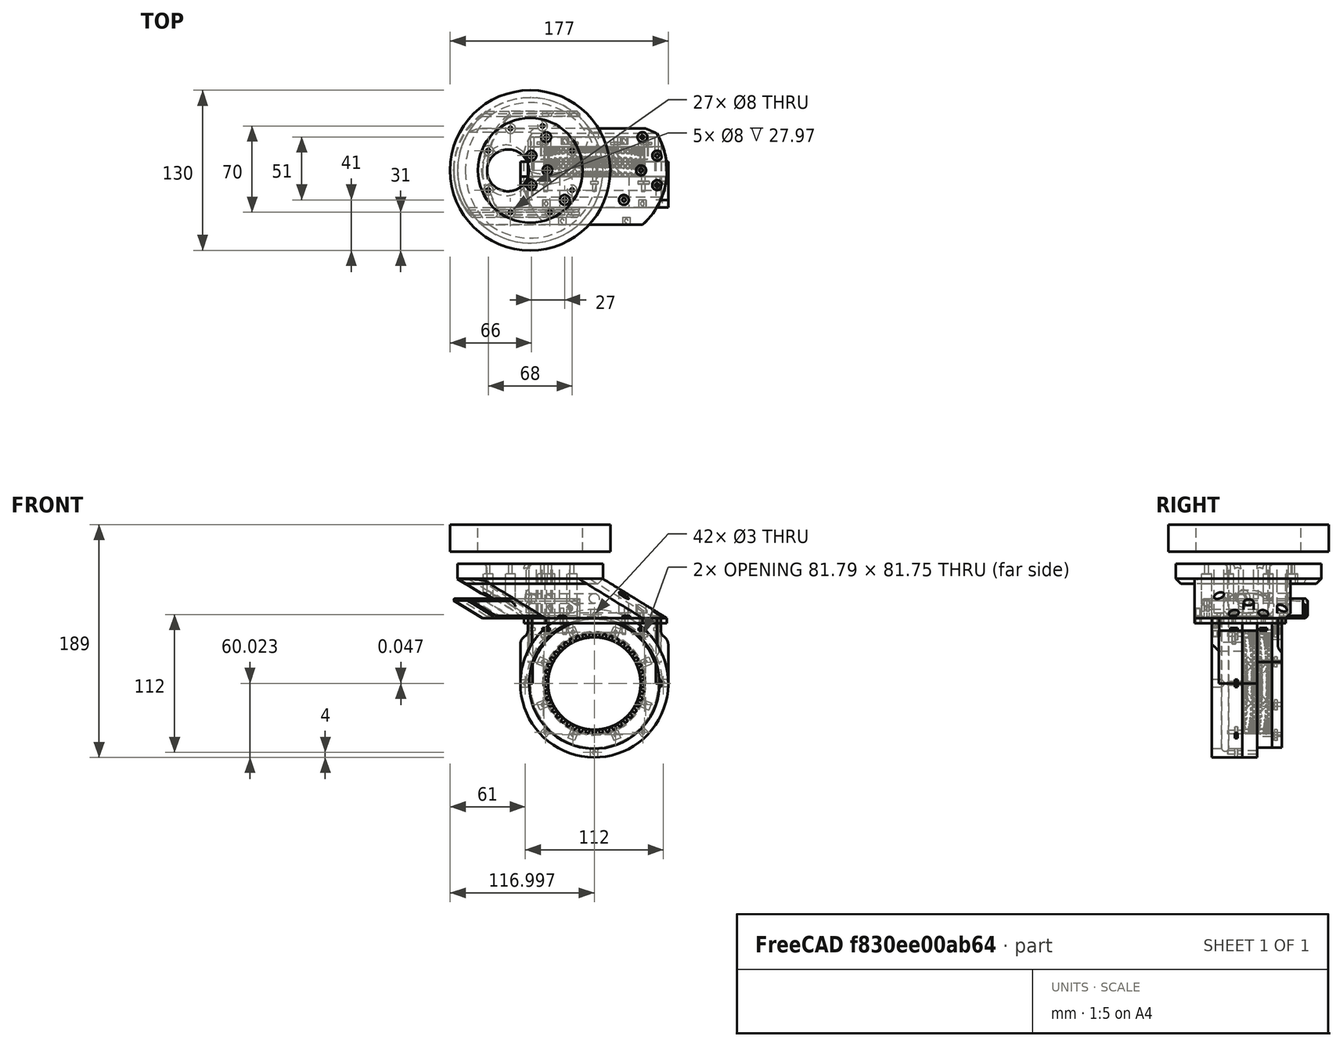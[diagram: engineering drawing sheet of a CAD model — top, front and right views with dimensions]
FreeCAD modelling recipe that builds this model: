
FCSTD DOCUMENT  (FreeCAD 0.19R24276 (Git))
Label: Base_neck_034
License: All rights reserved
LicenseURL: http://en.wikipedia.org/wiki/All_rights_reserved
objects: Part::Cylinder×1148, Part::Cut×314, Part::Compound×235, Part::Box×126, Part::Chamfer×46, Part::Fillet×33, Sketcher::SketchObject×20, Part::Extrusion×20, Part::Common×10, Part::FeaturePython×6, Part::Torus×3, Part::Mirroring×2, Mesh::Feature×1
note: 1963 computed .brp shape members not serialized (recipe doc carries the construction recipe); baked Part::Feature solids carry a one-line shape summary decoded from their .brp

FEATURE [Sketcher::SketchObject] Sketch003
  FullyConstrained = false
  sketch-geometry (1):
    g0: Circle CenterX=-186.411 CenterY=73.9277 CenterZ=0 NormalX=0 NormalY=0 NormalZ=1 AngleXU=0 Radius=59
FEATURE [Part::Extrusion] Extrude001
  Base = -> Sketch003
  Dir = (52,0,32)
  DirMode = 0
  FaceMakerClass = Part::FaceMakerBullseye
  LengthFwd = 61
  LengthRev = 0
  Placement = pos=(-134,74,-22) rot=(0,0,1;3.14159rad)
  Solid = true
  Symmetric = false
FEATURE [Part::Cylinder] Cylinder1076  label="Válec1076"
  Angle = 360
  AttacherType = Attacher::AttachEngine3D
  Height = 100
  Placement = pos=(103,-12,-60) rot=(0,0,1;0rad)
  Radius = 1.5
FEATURE [Part::Cylinder] Cylinder1077  label="Válec1077"
  Angle = 360
  AttacherType = Attacher::AttachEngine3D
  Height = 100
  Placement = pos=(103,6,-60) rot=(0,0,1;0rad)
  Radius = 1.5
FEATURE [Part::Cylinder] Cylinder1078  label="Válec1078"
  Angle = 360
  AttacherType = Attacher::AttachEngine3D
  Height = 100
  Placement = pos=(76,18,-60) rot=(0,0,1;0rad)
  Radius = 1.5
FEATURE [Part::Cylinder] Cylinder1079  label="Válec1079"
  Angle = 360
  AttacherType = Attacher::AttachEngine3D
  Height = 100
  Placement = pos=(91,-21,-60) rot=(0,0,1;0rad)
  Radius = 1.5
FEATURE [Part::Cylinder] Cylinder1080  label="Válec1080"
  Angle = 360
  AttacherType = Attacher::AttachEngine3D
  Height = 100
  Placement = pos=(13,-21,-60) rot=(0,0,1;0rad)
  Radius = 1.5
FEATURE [Part::Cylinder] Cylinder1081  label="Válec1081"
  Angle = 360
  AttacherType = Attacher::AttachEngine3D
  Height = 100
  Placement = pos=(28,18,-60) rot=(0,0,1;0rad)
  Radius = 1.5
FEATURE [Part::Cylinder] Cylinder1083  label="Válec1083"
  Angle = 360
  AttacherType = Attacher::AttachEngine3D
  Height = 100
  Placement = pos=(1,-12,-60) rot=(0,0,1;0rad)
  Radius = 1.5
FEATURE [Part::Cylinder] Cylinder1084  label="Válec1084"
  Angle = 360
  AttacherType = Attacher::AttachEngine3D
  Height = 100
  Placement = pos=(1,6,-60) rot=(0,0,1;0rad)
  Radius = 1.5
FEATURE [Part::Compound] Compound559  label="srouby_monoblok"
  Links = -> [Cylinder1076,Cylinder1077,Cylinder1078,Cylinder1079,Cylinder1080,Cylinder1081,Cylinder1083,Cylinder1084]
FEATURE [Part::Cut] Cut247
  Base = -> Extrude001
  Tool = -> Compound559
FEATURE [Part::Cylinder] Cylinder1085  label="Válec1085"
  Angle = 360
  AttacherType = Attacher::AttachEngine3D
  Height = 100
  Placement = pos=(-50,0,-60) rot=(0,0,1;0rad)
  Radius = 1.5
FEATURE [Part::Cylinder] Cylinder1086  label="Válec1086"
  Angle = 360
  AttacherType = Attacher::AttachEngine3D
  Height = 100
  Placement = pos=(-36,34,-60) rot=(0,0,1;0rad)
  Radius = 1.5
FEATURE [Part::Cylinder] Cylinder1087  label="Válec1087"
  Angle = 360
  AttacherType = Attacher::AttachEngine3D
  Height = 100
  Placement = pos=(-36,-34,-60) rot=(0,0,1;0rad)
  Radius = 1.5
FEATURE [Part::Cylinder] Cylinder1088  label="Válec1088"
  Angle = 360
  AttacherType = Attacher::AttachEngine3D
  Height = 100
  Placement = pos=(50,0,-60) rot=(0,0,1;0rad)
  Radius = 1.5
FEATURE [Part::Cylinder] Cylinder1089  label="Válec1089"
  Angle = 360
  AttacherType = Attacher::AttachEngine3D
  Height = 100
  Placement = pos=(36,34,-60) rot=(0,0,1;0rad)
  Radius = 1.5
FEATURE [Part::Cylinder] Cylinder1090  label="Válec1090"
  Angle = 360
  AttacherType = Attacher::AttachEngine3D
  Height = 100
  Placement = pos=(36,-34,-60) rot=(0,0,1;0rad)
  Radius = 1.5
FEATURE [Part::Compound] Compound560  label="sbouby_baze"
  Links = -> [Cylinder1085,Cylinder1086,Cylinder1087,Cylinder1088,Cylinder1089,Cylinder1090]
FEATURE [Part::Cylinder] Cylinder1091  label="Válec1091"
  Angle = 360
  AttacherType = Attacher::AttachEngine3D
  Height = 16
  Placement = pos=(0,0,2) rot=(0,0,1;0rad)
  Radius = 59
FEATURE [Part::Cylinder] Cylinder1092  label="Válec1092"
  Angle = 360
  AttacherType = Attacher::AttachEngine3D
  Height = 4
  Placement = pos=(52,0,-26) rot=(0,0,1;0rad)
  Radius = 59
FEATURE [Part::Cylinder] Cylinder1101  label="Válec1101"
  Angle = 360
  AttacherType = Attacher::AttachEngine3D
  Height = 100
  Placement = pos=(103,-12,-60) rot=(0,0,1;0rad)
  Radius = 1.5
FEATURE [Part::Cylinder] Cylinder1102  label="Válec1102"
  Angle = 360
  AttacherType = Attacher::AttachEngine3D
  Height = 100
  Placement = pos=(103,6,-60) rot=(0,0,1;0rad)
  Radius = 1.5
FEATURE [Part::Cylinder] Cylinder1103  label="Válec1103"
  Angle = 360
  AttacherType = Attacher::AttachEngine3D
  Height = 100
  Placement = pos=(76,18,-60) rot=(0,0,1;0rad)
  Radius = 1.5
FEATURE [Part::Cylinder] Cylinder1104  label="Válec1104"
  Angle = 360
  AttacherType = Attacher::AttachEngine3D
  Height = 100
  Placement = pos=(91,-21,-60) rot=(0,0,1;0rad)
  Radius = 1.5
FEATURE [Part::Cylinder] Cylinder1105  label="Válec1105"
  Angle = 360
  AttacherType = Attacher::AttachEngine3D
  Height = 100
  Placement = pos=(13,-21,-60) rot=(0,0,1;0rad)
  Radius = 1.5
FEATURE [Part::Cylinder] Cylinder1106  label="Válec1106"
  Angle = 360
  AttacherType = Attacher::AttachEngine3D
  Height = 100
  Placement = pos=(28,18,-60) rot=(0,0,1;0rad)
  Radius = 1.5
FEATURE [Part::Cylinder] Cylinder1107  label="Válec1107"
  Angle = 360
  AttacherType = Attacher::AttachEngine3D
  Height = 100
  Placement = pos=(1,-12,-60) rot=(0,0,1;0rad)
  Radius = 1.5
FEATURE [Part::Cylinder] Cylinder1108  label="Válec1108"
  Angle = 360
  AttacherType = Attacher::AttachEngine3D
  Height = 100
  Placement = pos=(1,6,-60) rot=(0,0,1;0rad)
  Radius = 1.5
FEATURE [Part::Compound] Compound562  label="srouby_monoblok001"
  Links = -> [Cylinder1101,Cylinder1102,Cylinder1103,Cylinder1104,Cylinder1105,Cylinder1106,Cylinder1107,Cylinder1108]
FEATURE [Part::Cut] Cut250
  Base = -> Cylinder1092
  Tool = -> Compound562
FEATURE [Part::Cylinder] Cylinder1109  label="Válec1109"
  Angle = 360
  AttacherType = Attacher::AttachEngine3D
  Height = 20
  Placement = pos=(103,-12,-20) rot=(0,0,1;0rad)
  Radius = 4
FEATURE [Part::Cylinder] Cylinder1110  label="Válec1110"
  Angle = 360
  AttacherType = Attacher::AttachEngine3D
  Height = 20
  Placement = pos=(103,6,-20) rot=(0,0,1;0rad)
  Radius = 4
FEATURE [Part::Cylinder] Cylinder1111  label="Válec1111"
  Angle = 360
  AttacherType = Attacher::AttachEngine3D
  Height = 20
  Placement = pos=(76,18,-18) rot=(0,0,1;0rad)
  Radius = 4
FEATURE [Part::Cylinder] Cylinder1112  label="Válec1112"
  Angle = 360
  AttacherType = Attacher::AttachEngine3D
  Height = 20
  Placement = pos=(91,-21,-18) rot=(0,0,1;0rad)
  Radius = 4
FEATURE [Part::Cylinder] Cylinder1113  label="Válec1113"
  Angle = 360
  AttacherType = Attacher::AttachEngine3D
  Height = 40
  Placement = pos=(13,-21,-18) rot=(0,0,1;0rad)
  Radius = 4
FEATURE [Part::Cylinder] Cylinder1114  label="Válec1114"
  Angle = 360
  AttacherType = Attacher::AttachEngine3D
  Height = 40
  Placement = pos=(28,18,-18) rot=(0,0,1;0rad)
  Radius = 4
FEATURE [Part::Cylinder] Cylinder1115  label="Válec1115"
  Angle = 360
  AttacherType = Attacher::AttachEngine3D
  Height = 40
  Placement = pos=(1,-12,-18) rot=(0,0,1;0rad)
  Radius = 4
FEATURE [Part::Cylinder] Cylinder1116  label="Válec1116"
  Angle = 360
  AttacherType = Attacher::AttachEngine3D
  Height = 40
  Placement = pos=(1,6,-18) rot=(0,0,1;0rad)
  Radius = 4
FEATURE [Part::Compound] Compound563  label="srouby_monoblok_silne001"
  Links = -> [Cylinder1109,Cylinder1110,Cylinder1111,Cylinder1112,Cylinder1113,Cylinder1114,Cylinder1115,Cylinder1116]
FEATURE [Part::Cut] Cut248
  Base = -> Cut247
  Tool = -> Compound563
FEATURE [Part::Cylinder] Cylinder1117  label="Válec1117"
  Angle = 360
  AttacherType = Attacher::AttachEngine3D
  Height = 20
  Placement = pos=(103,-12,-20) rot=(0,0,1;0rad)
  Radius = 4
FEATURE [Part::Cylinder] Cylinder1118  label="Válec1118"
  Angle = 360
  AttacherType = Attacher::AttachEngine3D
  Height = 20
  Placement = pos=(103,6,-20) rot=(0,0,1;0rad)
  Radius = 4
FEATURE [Part::Cylinder] Cylinder1119  label="Válec1119"
  Angle = 360
  AttacherType = Attacher::AttachEngine3D
  Height = 20
  Placement = pos=(76,18,-18) rot=(0,0,1;0rad)
  Radius = 4
FEATURE [Part::Cylinder] Cylinder1120  label="Válec1120"
  Angle = 360
  AttacherType = Attacher::AttachEngine3D
  Height = 20
  Placement = pos=(91,-21,-18) rot=(0,0,1;0rad)
  Radius = 4
FEATURE [Part::Cylinder] Cylinder1121  label="Válec1121"
  Angle = 360
  AttacherType = Attacher::AttachEngine3D
  Height = 40
  Placement = pos=(13,-21,-18) rot=(0,0,1;0rad)
  Radius = 4
FEATURE [Part::Cylinder] Cylinder1122  label="Válec1122"
  Angle = 360
  AttacherType = Attacher::AttachEngine3D
  Height = 40
  Placement = pos=(28,18,-18) rot=(0,0,1;0rad)
  Radius = 4
FEATURE [Part::Cylinder] Cylinder1123  label="Válec1123"
  Angle = 360
  AttacherType = Attacher::AttachEngine3D
  Height = 40
  Placement = pos=(1,-12,-18) rot=(0,0,1;0rad)
  Radius = 4
FEATURE [Part::Cylinder] Cylinder1124  label="Válec1124"
  Angle = 360
  AttacherType = Attacher::AttachEngine3D
  Height = 40
  Placement = pos=(1,6,-18) rot=(0,0,1;0rad)
  Radius = 4
FEATURE [Part::Compound] Compound564  label="srouby_monoblok_silne002"
  Links = -> [Cylinder1117,Cylinder1118,Cylinder1119,Cylinder1120,Cylinder1121,Cylinder1122,Cylinder1123,Cylinder1124]
FEATURE [Part::Cut] Cut249
  Base = -> Cylinder1091
  Tool = -> Compound564
FEATURE [Part::Cylinder] Cylinder1137  label="Válec1137"
  Angle = 360
  AttacherType = Attacher::AttachEngine3D
  Height = 100
  Placement = pos=(16,34,-90) rot=(0,0,1;0rad)
  Radius = 4
FEATURE [Part::Cylinder] Cylinder1138  label="Válec1138"
  Angle = 360
  AttacherType = Attacher::AttachEngine3D
  Height = 100
  Placement = pos=(-34,-16,-90) rot=(0,0,1;0rad)
  Radius = 4
FEATURE [Part::Cylinder] Cylinder1139  label="Válec1139"
  Angle = 360
  AttacherType = Attacher::AttachEngine3D
  Height = 100
  Placement = pos=(-16,34,-90) rot=(0,0,1;0rad)
  Radius = 4
FEATURE [Part::Cylinder] Cylinder1140  label="Válec1140"
  Angle = 360
  AttacherType = Attacher::AttachEngine3D
  Height = 100
  Placement = pos=(-16,-34,-90) rot=(0,0,1;0rad)
  Radius = 4
FEATURE [Part::Cylinder] Cylinder1141  label="Válec1141"
  Angle = 360
  AttacherType = Attacher::AttachEngine3D
  Height = 100
  Placement = pos=(36,0,-90) rot=(0,0,1;0rad)
  Radius = 4
FEATURE [Part::Cylinder] Cylinder1142  label="Válec1142"
  Angle = 360
  AttacherType = Attacher::AttachEngine3D
  Height = 100
  Placement = pos=(16,-34,-90) rot=(0,0,1;0rad)
  Radius = 4
FEATURE [Part::Compound] Compound567  label="sbouby_baze_silne002"
  Links = -> [Cylinder1138,Cylinder1139,Cylinder1140,Cylinder1141,Cylinder1137,Cylinder1142]
FEATURE [Part::Cut] Cut252
  Base = -> Cut248
  Tool = -> Compound567
FEATURE [Part::Cylinder] Cylinder1143  label="Válec1143"
  Angle = 360
  AttacherType = Attacher::AttachEngine3D
  Height = 100
  Placement = pos=(36,34,-60) rot=(0,0,1;0rad)
  Radius = 1.5
FEATURE [Part::Cylinder] Cylinder1144  label="Válec1144"
  Angle = 360
  AttacherType = Attacher::AttachEngine3D
  Height = 100
  Placement = pos=(-50,0,-60) rot=(0,0,1;0rad)
  Radius = 1.5
FEATURE [Part::Cylinder] Cylinder1145  label="Válec1145"
  Angle = 360
  AttacherType = Attacher::AttachEngine3D
  Height = 100
  Placement = pos=(-36,34,-60) rot=(0,0,1;0rad)
  Radius = 1.5
FEATURE [Part::Cylinder] Cylinder1146  label="Válec1146"
  Angle = 360
  AttacherType = Attacher::AttachEngine3D
  Height = 100
  Placement = pos=(-36,-34,-60) rot=(0,0,1;0rad)
  Radius = 1.5
FEATURE [Part::Cylinder] Cylinder1147  label="Válec1147"
  Angle = 360
  AttacherType = Attacher::AttachEngine3D
  Height = 100
  Placement = pos=(50,0,-60) rot=(0,0,1;0rad)
  Radius = 1.5
FEATURE [Part::Cylinder] Cylinder1148  label="Válec1148"
  Angle = 360
  AttacherType = Attacher::AttachEngine3D
  Height = 100
  Placement = pos=(36,-34,-60) rot=(0,0,1;0rad)
  Radius = 1.5
FEATURE [Part::Compound] Compound568  label="sbouby_baze001"
  Links = -> [Cylinder1144,Cylinder1145,Cylinder1146,Cylinder1147,Cylinder1143,Cylinder1148]
FEATURE [Part::Cut] Cut254
  Base = -> Cut252
  Tool = -> Compound568
FEATURE [Part::Box] Box214  label="Krychle214"
  AttacherType = Attacher::AttachEngine3D
  Height = 100
  Length = 200
  Placement = pos=(-60,-130,-90) rot=(0,0,1;0rad)
  Width = 100
FEATURE [Part::Cut] Cut256
  Base = -> Cut254
  Tool = -> Box214
FEATURE [Part::Box] Box233  label="Krychle233"
  AttacherType = Attacher::AttachEngine3D
  Height = 100
  Length = 200
  Placement = pos=(-60,-124,-90) rot=(0,0,1;0rad)
  Width = 100
FEATURE [Part::Box] Box234  label="Krychle234"
  AttacherType = Attacher::AttachEngine3D
  Height = 100
  Length = 200
  Placement = pos=(-60,44,-90) rot=(0,0,1;0rad)
  Width = 100
FEATURE [Part::Cut] Cut286
  Base = -> Cut256
  Tool = -> Box234
FEATURE [Part::Box] Box235  label="Krychle235"
  AttacherType = Attacher::AttachEngine3D
  Height = 100
  Length = 200
  Placement = pos=(-60,44,-90) rot=(0,0,1;0rad)
  Width = 100
FEATURE [Part::Cylinder] Cylinder1228  label="Válec1228"
  Angle = 360
  AttacherType = Attacher::AttachEngine3D
  Height = 100
  Placement = pos=(90,0,-60) rot=(0,0,1;0rad)
  Radius = 1.5
FEATURE [Part::Cylinder] Cylinder1229  label="Válec1229"
  Angle = 360
  AttacherType = Attacher::AttachEngine3D
  Height = 100
  Placement = pos=(14,0,-60) rot=(0,0,1;0rad)
  Radius = 1.5
FEATURE [Part::Compound] Compound623  label="srouby_troj"
  Links = -> [Cylinder1228,Cylinder1229]
FEATURE [Part::Cylinder] Cylinder1230  label="Válec1230"
  Angle = 360
  AttacherType = Attacher::AttachEngine3D
  Height = 100
  Placement = pos=(90,0,-18) rot=(0,0,1;0rad)
  Radius = 4
FEATURE [Part::Box] Box238  label="Krychle238"
  AttacherType = Attacher::AttachEngine3D
  Height = 2
  Length = 6
  Placement = pos=(75,38,-22) rot=(0,0,1;0rad)
  Width = 6
FEATURE [Part::Box] Box239  label="Krychle239"
  AttacherType = Attacher::AttachEngine3D
  Height = 2
  Length = 6
  Placement = pos=(23,38,-22) rot=(0,0,1;0rad)
  Width = 6
FEATURE [Part::Compound] Compound619
  Links = -> [Box238,Box239]
FEATURE [Part::Cut] Cut289
  Base = -> Cut286
  Tool = -> Compound619
FEATURE [Part::Cylinder] Cylinder1232  label="Válec1232"
  Angle = 360
  AttacherType = Attacher::AttachEngine3D
  Height = 32
  Placement = pos=(26,41,-42) rot=(0,0,1;0rad)
  Radius = 1.5
FEATURE [Part::Cylinder] Cylinder1233  label="Válec1233"
  Angle = 360
  AttacherType = Attacher::AttachEngine3D
  Height = 32
  Placement = pos=(78,41,-42) rot=(0,0,1;0rad)
  Radius = 1.5
FEATURE [Part::Compound] Compound620
  Links = -> [Cylinder1232,Cylinder1233]
FEATURE [Part::Cylinder] Cylinder1234  label="Válec1234"
  Angle = 360
  AttacherType = Attacher::AttachEngine3D
  Height = 32
  Placement = pos=(26,41,-46) rot=(0,0,1;0rad)
  Radius = 1.5
FEATURE [Part::Cylinder] Cylinder1235  label="Válec1235"
  Angle = 360
  AttacherType = Attacher::AttachEngine3D
  Height = 32
  Placement = pos=(78,41,-46) rot=(0,0,1;0rad)
  Radius = 1.5
FEATURE [Part::Compound] Compound621
  Links = -> [Cylinder1234,Cylinder1235]
FEATURE [Part::Cut] Cut290
  Base = -> Cut289
  Tool = -> Compound621
FEATURE [Part::Cut] Cut292
  Base = -> Cut290
  Tool = -> Compound623
FEATURE [Part::Cylinder] Cylinder1236  label="Válec1236"
  Angle = 360
  AttacherType = Attacher::AttachEngine3D
  Height = 100
  Placement = pos=(90,0,-18) rot=(0,0,1;0rad)
  Radius = 4
FEATURE [Part::Cylinder] Cylinder1237  label="Válec1237"
  Angle = 360
  AttacherType = Attacher::AttachEngine3D
  Height = 100
  Placement = pos=(14,0,-18) rot=(0,0,1;0rad)
  Radius = 4
FEATURE [Part::Compound] Compound624  label="srouby_troj_silne001"
  Links = -> [Cylinder1236,Cylinder1237]
FEATURE [Part::Cylinder] Cylinder1238  label="Válec1238"
  Angle = 360
  AttacherType = Attacher::AttachEngine3D
  Height = 100
  Placement = pos=(90,0,-60) rot=(0,0,1;0rad)
  Radius = 1.5
FEATURE [Part::Cylinder] Cylinder1239  label="Válec1239"
  Angle = 360
  AttacherType = Attacher::AttachEngine3D
  Height = 100
  Placement = pos=(14,0,-60) rot=(0,0,1;0rad)
  Radius = 1.5
FEATURE [Part::Compound] Compound625  label="srouby_troj001"
  Links = -> [Cylinder1238,Cylinder1239]
FEATURE [Part::FeaturePython] Tube044  label="ZKL-6017"  # WARN: FeaturePython — macro-defined, semantics opaque (R4)
  AttacherType = Attacher::AttachEngine3D
  Height = 22
  InnerRadius = 42.5
  OuterRadius = 65
  Placement = pos=(0,0,32) rot=(0,0,1;0rad)
FEATURE [Sketcher::SketchObject] Sketch004
  FullyConstrained = false
  sketch-geometry (1):
    g0: Circle CenterX=-186.411 CenterY=73.9277 CenterZ=0 NormalX=0 NormalY=0 NormalZ=1 AngleXU=0 Radius=59
FEATURE [Part::Extrusion] Extrude002
  Base = -> Sketch004
  Dir = (52,0,32)
  DirMode = 0
  FaceMakerClass = Part::FaceMakerBullseye
  LengthFwd = 61
  LengthRev = 0
  Placement = pos=(-134,74,-22) rot=(0,0,1;3.14159rad)
  Solid = true
  Symmetric = false
FEATURE [Part::Cylinder] Cylinder1256  label="Válec1256"
  Angle = 360
  AttacherType = Attacher::AttachEngine3D
  Height = 100
  Placement = pos=(16,34,-90) rot=(0,0,1;0rad)
  Radius = 4
FEATURE [Part::Cylinder] Cylinder1257  label="Válec1257"
  Angle = 360
  AttacherType = Attacher::AttachEngine3D
  Height = 100
  Placement = pos=(-34,-16,-90) rot=(0,0,1;0rad)
  Radius = 4
FEATURE [Part::Cylinder] Cylinder1258  label="Válec1258"
  Angle = 360
  AttacherType = Attacher::AttachEngine3D
  Height = 100
  Placement = pos=(-16,34,-90) rot=(0,0,1;0rad)
  Radius = 4
FEATURE [Part::Cylinder] Cylinder1259  label="Válec1259"
  Angle = 360
  AttacherType = Attacher::AttachEngine3D
  Height = 100
  Placement = pos=(-16,-34,-90) rot=(0,0,1;0rad)
  Radius = 4
FEATURE [Part::Cylinder] Cylinder1260  label="Válec1260"
  Angle = 360
  AttacherType = Attacher::AttachEngine3D
  Height = 100
  Placement = pos=(34,-16,-90) rot=(0,0,1;0rad)
  Radius = 4
FEATURE [Part::Cylinder] Cylinder1261  label="Válec1261"
  Angle = 360
  AttacherType = Attacher::AttachEngine3D
  Height = 100
  Placement = pos=(10,-36,-90) rot=(0,0,1;0rad)
  Radius = 4
FEATURE [Part::Cylinder] Cylinder1262  label="Válec1262"
  Angle = 360
  AttacherType = Attacher::AttachEngine3D
  Height = 100
  Placement = pos=(16,34,-60) rot=(0,0,1;0rad)
  Radius = 1.5
FEATURE [Part::Cylinder] Cylinder1263  label="Válec1263"
  Angle = 360
  AttacherType = Attacher::AttachEngine3D
  Height = 100
  Placement = pos=(-34,16,-60) rot=(0,0,1;0rad)
  Radius = 1.5
FEATURE [Part::Cylinder] Cylinder1264  label="Válec1264"
  Angle = 360
  AttacherType = Attacher::AttachEngine3D
  Height = 100
  Placement = pos=(-34,-16,-60) rot=(0,0,1;0rad)
  Radius = 1.5
FEATURE [Part::Cylinder] Cylinder1265  label="Válec1265"
  Angle = 360
  AttacherType = Attacher::AttachEngine3D
  Height = 100
  Placement = pos=(34,-16,-60) rot=(0,0,1;0rad)
  Radius = 1.5
FEATURE [Part::Cylinder] Cylinder1266  label="Válec1266"
  Angle = 360
  AttacherType = Attacher::AttachEngine3D
  Height = 100
  Placement = pos=(34,16,-60) rot=(0,0,1;0rad)
  Radius = 1.5
FEATURE [Part::Cylinder] Cylinder1267  label="Válec1267"
  Angle = 360
  AttacherType = Attacher::AttachEngine3D
  Height = 100
  Placement = pos=(10,-36,-60) rot=(0,0,1;0rad)
  Radius = 1.5
FEATURE [Part::Box] Box240  label="Krychle240"
  AttacherType = Attacher::AttachEngine3D
  Height = 100
  Length = 200
  Placement = pos=(-60,-134,-90) rot=(0,0,1;0rad)
  Width = 100
FEATURE [Part::Box] Box241  label="Krychle241"
  AttacherType = Attacher::AttachEngine3D
  Height = 100
  Length = 200
  Placement = pos=(-60,44,-90) rot=(0,0,1;0rad)
  Width = 100
FEATURE [Part::Cylinder] Cylinder1268  label="Válec1268"
  Angle = 360
  AttacherType = Attacher::AttachEngine3D
  Height = 100
  Placement = pos=(90,0,-60) rot=(0,0,1;0rad)
  Radius = 1.5
FEATURE [Part::Cylinder] Cylinder1269  label="Válec1269"
  Angle = 360
  AttacherType = Attacher::AttachEngine3D
  Height = 100
  Placement = pos=(14,0,-60) rot=(0,0,1;0rad)
  Radius = 1.5
FEATURE [Part::Cylinder] Cylinder1270  label="Válec1270"
  Angle = 360
  AttacherType = Attacher::AttachEngine3D
  Height = 100
  Placement = pos=(90,0,-18) rot=(0,0,1;0rad)
  Radius = 4
FEATURE [Part::Compound] Compound670  label="srouby_troj002"
  Links = -> [Cylinder1268,Cylinder1269]
FEATURE [Part::Cylinder] Cylinder1271  label="Válec1271"
  Angle = 360
  AttacherType = Attacher::AttachEngine3D
  Height = 100
  Placement = pos=(14,0,-18) rot=(0,0,1;0rad)
  Radius = 4
FEATURE [Part::Compound] Compound669  label="srouby_troj_silne002"
  Links = -> [Cylinder1270,Cylinder1271]
FEATURE [Part::Box] Box242  label="Krychle242"
  AttacherType = Attacher::AttachEngine3D
  Height = 2
  Length = 6
  Placement = pos=(75,38,-22) rot=(0,0,1;0rad)
  Width = 6
FEATURE [Part::Box] Box243  label="Krychle243"
  AttacherType = Attacher::AttachEngine3D
  Height = 2
  Length = 6
  Placement = pos=(23,38,-22) rot=(0,0,1;0rad)
  Width = 6
FEATURE [Part::Compound] Compound667
  Links = -> [Box242,Box243]
FEATURE [Part::Cylinder] Cylinder1272  label="Válec1272"
  Angle = 360
  AttacherType = Attacher::AttachEngine3D
  Height = 32
  Placement = pos=(26,41,-46) rot=(0,0,1;0rad)
  Radius = 1.5
FEATURE [Part::Cylinder] Cylinder1273  label="Válec1273"
  Angle = 360
  AttacherType = Attacher::AttachEngine3D
  Height = 32
  Placement = pos=(78,41,-46) rot=(0,0,1;0rad)
  Radius = 1.5
FEATURE [Part::Compound] Compound668
  Links = -> [Cylinder1272,Cylinder1273]
FEATURE [Part::Cylinder] Cylinder1274  label="Válec1274"
  Angle = 360
  AttacherType = Attacher::AttachEngine3D
  Height = 100
  Placement = pos=(-34,16,-90) rot=(0,0,1;0rad)
  Radius = 4
FEATURE [Part::Cylinder] Cylinder1275  label="Válec1275"
  Angle = 360
  AttacherType = Attacher::AttachEngine3D
  Height = 100
  Placement = pos=(34,16,-90) rot=(0,0,1;0rad)
  Radius = 4
FEATURE [Part::Compound] Compound665  label="sbouby_baze_silne003"
  Links = -> [Cylinder1257,Cylinder1258,Cylinder1259,Cylinder1260,Cylinder1256,Cylinder1261,Cylinder1274,Cylinder1275]
FEATURE [Part::FeaturePython] Tube045  label="ZKL-6017-2"  # WARN: FeaturePython — macro-defined, semantics opaque (R4)
  AttacherType = Attacher::AttachEngine3D
  Height = 22
  InnerRadius = 42.5
  OuterRadius = 65
  Placement = pos=(0,0,-16) rot=(0,0,1;0rad)
FEATURE [Part::Cylinder] Cylinder1276  label="Válec1276"
  Angle = 360
  AttacherType = Attacher::AttachEngine3D
  Height = 100
  Placement = pos=(-34,-16,-90) rot=(0,0,1;0rad)
  Radius = 4
FEATURE [Part::Cylinder] Cylinder1277  label="Válec1277"
  Angle = 360
  AttacherType = Attacher::AttachEngine3D
  Height = 100
  Placement = pos=(-16,34,-90) rot=(0,0,1;0rad)
  Radius = 4
FEATURE [Part::Cylinder] Cylinder1278  label="Válec1278"
  Angle = 360
  AttacherType = Attacher::AttachEngine3D
  Height = 100
  Placement = pos=(-16,-34,-90) rot=(0,0,1;0rad)
  Radius = 4
FEATURE [Part::Cylinder] Cylinder1279  label="Válec1279"
  Angle = 360
  AttacherType = Attacher::AttachEngine3D
  Height = 100
  Placement = pos=(34,-16,-90) rot=(0,0,1;0rad)
  Radius = 4
FEATURE [Part::Cylinder] Cylinder1280  label="Válec1280"
  Angle = 360
  AttacherType = Attacher::AttachEngine3D
  Height = 100
  Placement = pos=(16,34,-90) rot=(0,0,1;0rad)
  Radius = 4
FEATURE [Part::Cylinder] Cylinder1281  label="Válec1281"
  Angle = 360
  AttacherType = Attacher::AttachEngine3D
  Height = 100
  Placement = pos=(16,-34,-90) rot=(0,0,1;0rad)
  Radius = 4
FEATURE [Part::Cylinder] Cylinder1282  label="Válec1282"
  Angle = 360
  AttacherType = Attacher::AttachEngine3D
  Height = 100
  Placement = pos=(-34,16,-90) rot=(0,0,1;0rad)
  Radius = 4
FEATURE [Part::Cylinder] Cylinder1283  label="Válec1283"
  Angle = 360
  AttacherType = Attacher::AttachEngine3D
  Height = 100
  Placement = pos=(34,16,-90) rot=(0,0,1;0rad)
  Radius = 4
FEATURE [Part::Compound] Compound566  label="sbouby_baze_silne001"
  Links = -> [Cylinder1276,Cylinder1277,Cylinder1278,Cylinder1279,Cylinder1280,Cylinder1281,Cylinder1282,Cylinder1283]
FEATURE [Part::Cut] Cut253
  Base = -> Cut249
  Tool = -> Compound566
FEATURE [Part::Cut] Cut255
  Base = -> Cut253
  Tool = -> Compound560
FEATURE [Part::Chamfer] Chamfer036
  Base = -> Cut255
  Edges = 1 edges r=4: [Edge3]
FEATURE [Part::Cut] Cut294
  Base = -> Chamfer036
  Placement = pos=(0,0,4) rot=(0,0,1;0rad)
  Tool = -> Compound624
FEATURE [Part::Cylinder] Cylinder1284  label="Válec1284"
  Angle = 360
  AttacherType = Attacher::AttachEngine3D
  Height = 100
  Placement = pos=(-34,-16,-90) rot=(0,0,1;0rad)
  Radius = 4
FEATURE [Part::Cylinder] Cylinder1285  label="Válec1285"
  Angle = 360
  AttacherType = Attacher::AttachEngine3D
  Height = 100
  Placement = pos=(-16,34,-90) rot=(0,0,1;0rad)
  Radius = 4
FEATURE [Part::Cylinder] Cylinder1286  label="Válec1286"
  Angle = 360
  AttacherType = Attacher::AttachEngine3D
  Height = 100
  Placement = pos=(-16,-34,-90) rot=(0,0,1;0rad)
  Radius = 4
FEATURE [Part::Cylinder] Cylinder1287  label="Válec1287"
  Angle = 360
  AttacherType = Attacher::AttachEngine3D
  Height = 100
  Placement = pos=(34,-16,-90) rot=(0,0,1;0rad)
  Radius = 4
FEATURE [Part::Cylinder] Cylinder1288  label="Válec1288"
  Angle = 360
  AttacherType = Attacher::AttachEngine3D
  Height = 100
  Placement = pos=(16,34,-90) rot=(0,0,1;0rad)
  Radius = 4
FEATURE [Part::Cylinder] Cylinder1289  label="Válec1289"
  Angle = 360
  AttacherType = Attacher::AttachEngine3D
  Height = 100
  Placement = pos=(16,-34,-90) rot=(0,0,1;0rad)
  Radius = 4
FEATURE [Part::Cylinder] Cylinder1290  label="Válec1290"
  Angle = 360
  AttacherType = Attacher::AttachEngine3D
  Height = 100
  Placement = pos=(-34,16,-90) rot=(0,0,1;0rad)
  Radius = 4
FEATURE [Part::Cylinder] Cylinder1291  label="Válec1291"
  Angle = 360
  AttacherType = Attacher::AttachEngine3D
  Height = 100
  Placement = pos=(34,16,-90) rot=(0,0,1;0rad)
  Radius = 4
FEATURE [Part::Compound] Compound565  label="sbouby_baze_silne"
  Links = -> [Cylinder1284,Cylinder1285,Cylinder1286,Cylinder1287,Cylinder1288,Cylinder1289,Cylinder1290,Cylinder1291]
FEATURE [Part::Cut] Cut251
  Base = -> Cut250
  Tool = -> Compound565
FEATURE [Part::Cut] Cut285
  Base = -> Cut251
  Tool = -> Box233
FEATURE [Part::Cut] Cut287
  Base = -> Cut285
  Tool = -> Box235
FEATURE [Part::Cut] Cut288
  Base = -> Cut287
  Tool = -> Compound620
FEATURE [Part::Cut] Cut291
  Base = -> Cut288
  Tool = -> Compound625
FEATURE [Part::Cylinder] Cylinder1292  label="Válec1292"
  Angle = 360
  AttacherType = Attacher::AttachEngine3D
  Height = 100
  Placement = pos=(-16,-34,-60) rot=(0,0,1;0rad)
  Radius = 1.5
FEATURE [Part::Cylinder] Cylinder1293  label="Válec1293"
  Angle = 360
  AttacherType = Attacher::AttachEngine3D
  Height = 100
  Placement = pos=(-16,34,-60) rot=(0,0,1;0rad)
  Radius = 1.5
FEATURE [Part::Compound] Compound666  label="sbouby_baze002"
  Links = -> [Cylinder1263,Cylinder1264,Cylinder1265,Cylinder1266,Cylinder1262,Cylinder1267,Cylinder1292,Cylinder1293]
FEATURE [Part::Cylinder] Cylinder1294  label="Válec1294"
  Angle = 360
  AttacherType = Attacher::AttachEngine3D
  Height = 100
  Placement = pos=(-34,16,-60) rot=(0,0,1;0rad)
  Radius = 1.5
FEATURE [Part::Cylinder] Cylinder1295  label="Válec1295"
  Angle = 360
  AttacherType = Attacher::AttachEngine3D
  Height = 100
  Placement = pos=(-34,-16,-60) rot=(0,0,1;0rad)
  Radius = 1.5
FEATURE [Part::Cylinder] Cylinder1296  label="Válec1296"
  Angle = 360
  AttacherType = Attacher::AttachEngine3D
  Height = 100
  Placement = pos=(34,-16,-60) rot=(0,0,1;0rad)
  Radius = 1.5
FEATURE [Part::Cylinder] Cylinder1297  label="Válec1297"
  Angle = 360
  AttacherType = Attacher::AttachEngine3D
  Height = 100
  Placement = pos=(34,16,-60) rot=(0,0,1;0rad)
  Radius = 1.5
FEATURE [Part::Cylinder] Cylinder1298  label="Válec1298"
  Angle = 360
  AttacherType = Attacher::AttachEngine3D
  Height = 100
  Placement = pos=(16,34,-60) rot=(0,0,1;0rad)
  Radius = 1.5
FEATURE [Part::Cylinder] Cylinder1299  label="Válec1299"
  Angle = 360
  AttacherType = Attacher::AttachEngine3D
  Height = 100
  Placement = pos=(10,-36,-60) rot=(0,0,1;0rad)
  Radius = 1.5
FEATURE [Part::Cylinder] Cylinder1300  label="Válec1300"
  Angle = 360
  AttacherType = Attacher::AttachEngine3D
  Height = 100
  Placement = pos=(-16,-34,-60) rot=(0,0,1;0rad)
  Radius = 1.5
FEATURE [Part::Cylinder] Cylinder1301  label="Válec1301"
  Angle = 360
  AttacherType = Attacher::AttachEngine3D
  Height = 100
  Placement = pos=(-16,34,-60) rot=(0,0,1;0rad)
  Radius = 1.5
FEATURE [Part::Compound] Compound671  label="sbouby_baze003"
  Links = -> [Cylinder1294,Cylinder1295,Cylinder1296,Cylinder1297,Cylinder1298,Cylinder1299,Cylinder1300,Cylinder1301]
FEATURE [Part::Cylinder] Cylinder1308  label="Válec1308"
  Angle = 360
  AttacherType = Attacher::AttachEngine3D
  Height = 16
  Placement = pos=(0,0,2) rot=(0,0,1;0rad)
  Radius = 59
FEATURE [Part::Cylinder] Cylinder1309  label="Válec1309"
  Angle = 360
  AttacherType = Attacher::AttachEngine3D
  Height = 20
  Placement = pos=(103,-12,-20) rot=(0,0,1;0rad)
  Radius = 4
FEATURE [Part::Cylinder] Cylinder1310  label="Válec1310"
  Angle = 360
  AttacherType = Attacher::AttachEngine3D
  Height = 20
  Placement = pos=(103,12,-20) rot=(0,0,1;0rad)
  Radius = 4
FEATURE [Part::Cylinder] Cylinder1311  label="Válec1311"
  Angle = 360
  AttacherType = Attacher::AttachEngine3D
  Height = 20
  Placement = pos=(76,24,-18) rot=(0,0,1;0rad)
  Radius = 4
FEATURE [Part::Cylinder] Cylinder1312  label="Válec1312"
  Angle = 360
  AttacherType = Attacher::AttachEngine3D
  Height = 20
  Placement = pos=(91,-27,-18) rot=(0,0,1;0rad)
  Radius = 4
FEATURE [Part::Cylinder] Cylinder1313  label="Válec1313"
  Angle = 360
  AttacherType = Attacher::AttachEngine3D
  Height = 40
  Placement = pos=(13,-27,-18) rot=(0,0,1;0rad)
  Radius = 4
FEATURE [Part::Cylinder] Cylinder1314  label="Válec1314"
  Angle = 360
  AttacherType = Attacher::AttachEngine3D
  Height = 40
  Placement = pos=(28,24,-18) rot=(0,0,1;0rad)
  Radius = 4
FEATURE [Part::Cylinder] Cylinder1315  label="Válec1315"
  Angle = 360
  AttacherType = Attacher::AttachEngine3D
  Height = 40
  Placement = pos=(1,-12,-18) rot=(0,0,1;0rad)
  Radius = 4
FEATURE [Part::Cylinder] Cylinder1316  label="Válec1316"
  Angle = 360
  AttacherType = Attacher::AttachEngine3D
  Height = 40
  Placement = pos=(1,12,-18) rot=(0,0,1;0rad)
  Radius = 4
FEATURE [Part::Compound] Compound672  label="srouby_monoblok_silne004"
  Links = -> [Cylinder1309,Cylinder1310,Cylinder1311,Cylinder1312,Cylinder1313,Cylinder1314,Cylinder1315,Cylinder1316]
FEATURE [Part::Cut] Cut305
  Base = -> Cylinder1308
  Tool = -> Compound672
FEATURE [Part::Cylinder] Cylinder1317  label="Válec1317"
  Angle = 360
  AttacherType = Attacher::AttachEngine3D
  Height = 100
  Placement = pos=(90,0,-18) rot=(0,0,1;0rad)
  Radius = 4
FEATURE [Part::Cylinder] Cylinder1318  label="Válec1318"
  Angle = 360
  AttacherType = Attacher::AttachEngine3D
  Height = 100
  Placement = pos=(14,0,-18) rot=(0,0,1;0rad)
  Radius = 4
FEATURE [Part::Compound] Compound674  label="srouby_troj_silne003"
  Links = -> [Cylinder1317,Cylinder1318]
FEATURE [Part::Cylinder] Cylinder1319  label="Válec1319"
  Angle = 360
  AttacherType = Attacher::AttachEngine3D
  Height = 100
  Placement = pos=(-16,-34,-90) rot=(0,0,1;0rad)
  Radius = 4
FEATURE [Part::Cylinder] Cylinder1320  label="Válec1320"
  Angle = 360
  AttacherType = Attacher::AttachEngine3D
  Height = 100
  Placement = pos=(-34,-16,-90) rot=(0,0,1;0rad)
  Radius = 4
FEATURE [Part::Cylinder] Cylinder1321  label="Válec1321"
  Angle = 360
  AttacherType = Attacher::AttachEngine3D
  Height = 100
  Placement = pos=(-16,34,-90) rot=(0,0,1;0rad)
  Radius = 4
FEATURE [Part::Cylinder] Cylinder1322  label="Válec1322"
  Angle = 360
  AttacherType = Attacher::AttachEngine3D
  Height = 100
  Placement = pos=(34,-16,-90) rot=(0,0,1;0rad)
  Radius = 4
FEATURE [Part::Cylinder] Cylinder1323  label="Válec1323"
  Angle = 360
  AttacherType = Attacher::AttachEngine3D
  Height = 100
  Placement = pos=(16,34,-90) rot=(0,0,1;0rad)
  Radius = 4
FEATURE [Part::Cylinder] Cylinder1324  label="Válec1324"
  Angle = 360
  AttacherType = Attacher::AttachEngine3D
  Height = 100
  Placement = pos=(10,-36,-90) rot=(0,0,1;0rad)
  Radius = 4
FEATURE [Part::Cylinder] Cylinder1325  label="Válec1325"
  Angle = 360
  AttacherType = Attacher::AttachEngine3D
  Height = 100
  Placement = pos=(-34,16,-90) rot=(0,0,1;0rad)
  Radius = 4
FEATURE [Part::Cylinder] Cylinder1326  label="Válec1326"
  Angle = 360
  AttacherType = Attacher::AttachEngine3D
  Height = 100
  Placement = pos=(34,16,-90) rot=(0,0,1;0rad)
  Radius = 4
FEATURE [Part::Compound] Compound673  label="sbouby_baze_silne004"
  Links = -> [Cylinder1320,Cylinder1321,Cylinder1319,Cylinder1322,Cylinder1323,Cylinder1324,Cylinder1325,Cylinder1326]
FEATURE [Part::Cut] Cut306
  Base = -> Cut305
  Tool = -> Compound673
FEATURE [Part::Cut] Cut307
  Base = -> Cut306
  Tool = -> Compound671
FEATURE [Part::Chamfer] Chamfer038
  Base = -> Cut307
  Edges = 1 edges r=4: [Edge3]
FEATURE [Part::Cut] Cut308
  Base = -> Chamfer038
  Placement = pos=(0,0,4) rot=(0,0,1;0rad)
  Tool = -> Compound674
FEATURE [Part::Box] Box489  label="Krychle489"
  AttacherType = Attacher::AttachEngine3D
  Height = 6
  Length = 6
  Placement = pos=(-54,-45,4) rot=(0,0,1;0rad)
  Width = 2
FEATURE [Part::Cylinder] Cylinder1337  label="Válec1337"
  Angle = 360
  AttacherType = Attacher::AttachEngine3D
  Height = 20
  Placement = pos=(-39.6,-39.6,-10) rot=(0,0,-1;0.785398rad)
  Radius = 4
FEATURE [Part::Cylinder] Cylinder1338  label="Válec1338"
  Angle = 360
  AttacherType = Attacher::AttachEngine3D
  Height = 40
  Placement = pos=(59,-17,0) rot=(0,0,1;0rad)
  Radius = 10
FEATURE [Part::Box] Box490  label="Krychle490"
  AttacherType = Attacher::AttachEngine3D
  Height = 6
  Length = 6
  Placement = pos=(48,-45,4) rot=(0,0,1;0rad)
  Width = 2
FEATURE [Part::Cylinder] Cylinder1339  label="Válec1339"
  Angle = 360
  AttacherType = Attacher::AttachEngine3D
  Height = 20
  Placement = pos=(51,-40,7) rot=(1,0,0;1.5708rad)
  Radius = 1.5
FEATURE [Part::Cylinder] Cylinder1340  label="Válec1340"
  Angle = 360
  AttacherType = Attacher::AttachEngine3D
  Height = 20
  Placement = pos=(-24,-40,-5) rot=(1,0,0;1.5708rad)
  Radius = 1.5
FEATURE [Part::Cylinder] Cylinder1341  label="Válec1341"
  Angle = 360
  AttacherType = Attacher::AttachEngine3D
  Height = 8
  Placement = pos=(0,0,20) rot=(0,0,1;0rad)
  Radius = 52
FEATURE [Part::Box] Box491  label="Krychle491"
  AttacherType = Attacher::AttachEngine3D
  Height = 6
  Length = 6
  Placement = pos=(-27,-47,-8) rot=(0,0,1;0rad)
  Width = 2
FEATURE [Part::Cylinder] Cylinder1342  label="Válec1342"
  Angle = 360
  AttacherType = Attacher::AttachEngine3D
  Height = 40
  Placement = pos=(-59,-17,0) rot=(0,0,1;0rad)
  Radius = 10
FEATURE [Part::Box] Box492  label="Krychle492"
  AttacherType = Attacher::AttachEngine3D
  Height = 8
  Length = 108
  Placement = pos=(-54,-53,20) rot=(0,0,1;0rad)
  Width = 36
FEATURE [Part::Box] Box493  label="Krychle493"
  AttacherType = Attacher::AttachEngine3D
  Height = 6
  Length = 6
  Placement = pos=(21,-47,-8) rot=(0,0,1;0rad)
  Width = 2
FEATURE [Part::Cylinder] Cylinder1343  label="Válec1343"
  Angle = 360
  AttacherType = Attacher::AttachEngine3D
  Height = 20
  Placement = pos=(24,-40,-5) rot=(1,0,0;1.5708rad)
  Radius = 1.5
FEATURE [Part::Cylinder] Cylinder1344  label="Válec1344"
  Angle = 360
  AttacherType = Attacher::AttachEngine3D
  Height = 20
  Placement = pos=(39.6,-39.6,-10) rot=(0,0,1;0.785398rad)
  Radius = 4
FEATURE [Part::Cylinder] Cylinder1345  label="Válec1345"
  Angle = 360
  AttacherType = Attacher::AttachEngine3D
  Height = 20
  Placement = pos=(-51,-40,7) rot=(1,0,0;1.5708rad)
  Radius = 1.5
FEATURE [Part::Cylinder] Cylinder1346  label="Válec1346"
  Angle = 360
  AttacherType = Attacher::AttachEngine3D
  Height = 50
  Placement = pos=(0,-56,2) rot=(0,0,1;0rad)
  Radius = 1.5
FEATURE [Part::Cylinder] Cylinder1347  label="Válec1347"
  Angle = 360
  AttacherType = Attacher::AttachEngine3D
  Height = 50
  Placement = pos=(-39.598,39.598,2) rot=(0,0,1;3.92699rad)
  Radius = 1.5
FEATURE [Part::Box] Box494  label="Krychle494"
  AttacherType = Attacher::AttachEngine3D
  Height = 12
  Length = 10
  Placement = pos=(50,-43,10) rot=(0,0,1;0rad)
  Width = 43
FEATURE [Part::Cylinder] Cylinder1348  label="Válec1348"
  Angle = 360
  AttacherType = Attacher::AttachEngine3D
  Height = 16
  Placement = pos=(-60,-43,10) rot=(0,0,1;0rad)
  Radius = 6
FEATURE [Part::Cylinder] Cylinder1349  label="Válec1349"
  Angle = 360
  AttacherType = Attacher::AttachEngine3D
  Height = 50
  Placement = pos=(39.598,39.598,2) rot=(0,0,1;2.35619rad)
  Radius = 1.5
FEATURE [Part::Cylinder] Cylinder1350  label="Válec1350"
  Angle = 360
  AttacherType = Attacher::AttachEngine3D
  Height = 50
  Placement = pos=(-39.598,-39.598,2) rot=(0,0,-1;0.785398rad)
  Radius = 1.5
FEATURE [Part::Cylinder] Cylinder1351  label="Válec1351"
  Angle = 360
  AttacherType = Attacher::AttachEngine3D
  Height = 50
  Placement = pos=(56,0,2) rot=(0,0,1;1.5708rad)
  Radius = 1.5
FEATURE [Part::Compound] Compound863
  Links = -> [Cylinder1340,Cylinder1343,Cylinder1339,Cylinder1345]
FEATURE [Part::Compound] Compound864
  Links = -> [Box491,Box493,Box490,Box489]
FEATURE [Part::Cut] Cut481
  Base = -> Box492
  Placement = pos=(0,0,-20) rot=(0,0,1;0rad)
  Tool = -> Cylinder1341
FEATURE [Part::FeaturePython] Tube091  # WARN: FeaturePython — macro-defined, semantics opaque (R4)
  AttacherType = Attacher::AttachEngine3D
  Height = 8
  InnerRadius = 42
  OuterRadius = 52
  Placement = pos=(0,0,-8) rot=(0,0,1;0rad)
FEATURE [Part::Compound] Compound865
  Links = -> [Cylinder1338,Cylinder1342]
FEATURE [Part::Cut] Cut484
  Base = -> Cut481
  Placement = pos=(0,0,-8) rot=(0,0,1;0rad)
  Tool = -> Compound865
FEATURE [Part::Compound] Compound866
  Links = -> [Cylinder1337,Cylinder1344]
FEATURE [Part::Cut] Cut482
  Base = -> Cut484
  Tool = -> Compound866
FEATURE [Part::Cut] Cut483
  Base = -> Cut482
  Tool = -> Compound864
FEATURE [Part::Cut] Cut480
  Base = -> Cut483
  Tool = -> Compound863
FEATURE [Part::Fillet] Fillet020
  Base = -> Cut480
  Edges = 2 edges r=12: [Edge2,Edge38]
  Placement = pos=(0,0,-6) rot=(0,0,1;0rad)
FEATURE [Part::Box] Box495  label="Krychle495"
  AttacherType = Attacher::AttachEngine3D
  Height = 12
  Length = 10
  Placement = pos=(-60,-43,10) rot=(0,0,1;0rad)
  Width = 43
FEATURE [Part::Compound] Compound867
  Links = -> [Box495,Box494]
FEATURE [Part::Cylinder] Cylinder1352  label="Válec1352"
  Angle = 360
  AttacherType = Attacher::AttachEngine3D
  Height = 16
  Placement = pos=(60,-43,10) rot=(0,0,1;0rad)
  Radius = 6
FEATURE [Part::Compound] Compound869
  Links = -> [Cylinder1352,Cylinder1348]
FEATURE [Part::Cylinder] Cylinder1353  label="Válec1353"
  Angle = 360
  AttacherType = Attacher::AttachEngine3D
  Height = 50
  Placement = pos=(-1.2e-14,56,2) rot=(0,0,1;3.14159rad)
  Radius = 1.5
FEATURE [Part::Cylinder] Cylinder1354  label="Válec1354"
  Angle = 360
  AttacherType = Attacher::AttachEngine3D
  Height = 50
  Placement = pos=(-56,-1.3e-14,2) rot=(0,0,-1;1.5708rad)
  Radius = 1.5
FEATURE [Part::Cylinder] Cylinder1355  label="Válec1355"
  Angle = 360
  AttacherType = Attacher::AttachEngine3D
  Height = 50
  Placement = pos=(39.598,-39.598,2) rot=(0,0,1;0.785398rad)
  Radius = 1.5
FEATURE [Part::Compound] Compound868
  Links = -> [Cylinder1346,Cylinder1355,Cylinder1351,Cylinder1349,Cylinder1353,Cylinder1347,Cylinder1354,Cylinder1350]
FEATURE [Part::Cut] Cut485
  Base = -> Compound867
  Tool = -> Compound868
FEATURE [Part::Cut] Cut486
  Base = -> Cut485
  Tool = -> Compound869
FEATURE [Part::Fillet] Fillet021
  Base = -> Cut486
  Edges = 2 edges r=8: [Edge4,Edge43]
  Placement = pos=(0,0,-4) rot=(0,0,1;0rad)
FEATURE [Part::Cylinder] Cylinder1364  label="Válec1364"
  Angle = 360
  AttacherType = Attacher::AttachEngine3D
  Height = 50
  Placement = pos=(-39.598,39.598,2) rot=(0,0,1;3.92699rad)
  Radius = 1.5
FEATURE [Part::Cylinder] Cylinder1365  label="Válec1365"
  Angle = 360
  AttacherType = Attacher::AttachEngine3D
  Height = 50
  Placement = pos=(-56,-1.3e-14,2) rot=(0,0,-1;1.5708rad)
  Radius = 1.5
FEATURE [Part::Cylinder] Cylinder1366  label="Válec1366"
  Angle = 360
  AttacherType = Attacher::AttachEngine3D
  Height = 50
  Placement = pos=(39.598,39.598,2) rot=(0,0,1;2.35619rad)
  Radius = 1.5
FEATURE [Part::Cylinder] Cylinder1367  label="Válec1367"
  Angle = 360
  AttacherType = Attacher::AttachEngine3D
  Height = 50
  Placement = pos=(-39.598,-39.598,2) rot=(0,0,-1;0.785398rad)
  Radius = 1.5
FEATURE [Part::Cylinder] Cylinder1368  label="Válec1368"
  Angle = 360
  AttacherType = Attacher::AttachEngine3D
  Height = 16
  Placement = pos=(0,0,20) rot=(0,0,1;0rad)
  Radius = 52
FEATURE [Part::Cylinder] Cylinder1369  label="Válec1369"
  Angle = 360
  AttacherType = Attacher::AttachEngine3D
  Height = 50
  Placement = pos=(0,-56,2) rot=(0,0,1;0rad)
  Radius = 1.5
FEATURE [Part::Cylinder] Cylinder1370  label="Válec1370"
  Angle = 360
  AttacherType = Attacher::AttachEngine3D
  Height = 50
  Placement = pos=(-1.2e-14,56,2) rot=(0,0,1;3.14159rad)
  Radius = 1.5
FEATURE [Part::Cylinder] Cylinder1371  label="Válec1371"
  Angle = 360
  AttacherType = Attacher::AttachEngine3D
  Height = 50
  Placement = pos=(39.598,-39.598,2) rot=(0,0,1;0.785398rad)
  Radius = 1.5
FEATURE [Part::Compound] Compound871
  Links = -> [Cylinder1369,Cylinder1371,Cylinder1366,Cylinder1370,Cylinder1364,Cylinder1365,Cylinder1367]
FEATURE [Part::Box] Box497  label="Krychle497"
  AttacherType = Attacher::AttachEngine3D
  Height = 12
  Length = 108
  Placement = pos=(-54,-53,20) rot=(0,0,1;0rad)
  Width = 36
FEATURE [Part::Cut] Cut490
  Base = -> Box497
  Placement = pos=(0,0,-10) rot=(0,0,1;0rad)
  Tool = -> Cylinder1368
FEATURE [Part::Cut] Cut489
  Base = -> Cut490
  Placement = pos=(0,0,-4) rot=(0,0,1;0rad)
  Tool = -> Compound871
FEATURE [Part::Cylinder] Cylinder1372  label="Válec1372"
  Angle = 360
  AttacherType = Attacher::AttachEngine3D
  Height = 20
  Placement = pos=(51,-40,7) rot=(1,0,0;1.5708rad)
  Radius = 1.5
FEATURE [Part::Cylinder] Cylinder1373  label="Válec1373"
  Angle = 360
  AttacherType = Attacher::AttachEngine3D
  Height = 20
  Placement = pos=(0,45,-18) rot=(0,0,1;0rad)
  Radius = 1.5
FEATURE [Part::Cylinder] Cylinder1374  label="Válec1374"
  Angle = 360
  AttacherType = Attacher::AttachEngine3D
  Height = 20
  Placement = pos=(-24,-40,-5) rot=(1,0,0;1.5708rad)
  Radius = 1.5
FEATURE [Part::Box] Box498  label="Krychle498"
  AttacherType = Attacher::AttachEngine3D
  Height = 2
  Length = 6
  Placement = pos=(3,-41,-4) rot=(0,0,1;3.14159rad)
  Width = 8
FEATURE [Part::Cylinder] Cylinder1375  label="Válec1375"
  Angle = 360
  AttacherType = Attacher::AttachEngine3D
  Height = 20
  Placement = pos=(-51,-40,7) rot=(1,0,0;1.5708rad)
  Radius = 1.5
FEATURE [Part::Box] Box499  label="Krychle499"
  AttacherType = Attacher::AttachEngine3D
  Height = 6
  Length = 6
  Placement = pos=(48,-45,4) rot=(0,0,1;0rad)
  Width = 2
FEATURE [Part::Box] Box500  label="Krychle500"
  AttacherType = Attacher::AttachEngine3D
  Height = 2
  Length = 6
  Placement = pos=(-41,-3,-4) rot=(0,0,1;1.5708rad)
  Width = 8
FEATURE [Part::Cylinder] Cylinder1376  label="Válec1376"
  Angle = 360
  AttacherType = Attacher::AttachEngine3D
  Height = 20
  Placement = pos=(24,-40,-5) rot=(1,0,0;1.5708rad)
  Radius = 1.5
FEATURE [Part::Cylinder] Cylinder1377  label="Válec1377"
  Angle = 360
  AttacherType = Attacher::AttachEngine3D
  Height = 20
  Placement = pos=(1.4e-14,-45,-18) rot=(0,0,1;3.14159rad)
  Radius = 1.5
FEATURE [Part::Box] Box501  label="Krychle501"
  AttacherType = Attacher::AttachEngine3D
  Height = 2
  Length = 6
  Placement = pos=(41,3,-4) rot=(0,0,-1;1.5708rad)
  Width = 8
FEATURE [Part::Cylinder] Cylinder1378  label="Válec1378"
  Angle = 360
  AttacherType = Attacher::AttachEngine3D
  Height = 20
  Placement = pos=(-45,-6e-15,-18) rot=(0,0,1;1.5708rad)
  Radius = 1.5
FEATURE [Part::Cylinder] Cylinder1379  label="Válec1379"
  Angle = 360
  AttacherType = Attacher::AttachEngine3D
  Height = 20
  Placement = pos=(-31.8198,-31.8198,-18) rot=(0,0,1;2.35619rad)
  Radius = 1.5
FEATURE [Part::Cylinder] Cylinder1380  label="Válec1380"
  Angle = 360
  AttacherType = Attacher::AttachEngine3D
  Height = 20
  Placement = pos=(45,1.9e-14,-18) rot=(0,0,-1;1.5708rad)
  Radius = 1.5
FEATURE [Part::Box] Box502  label="Krychle502"
  AttacherType = Attacher::AttachEngine3D
  Height = 2
  Length = 6
  Placement = pos=(-3,41,-4) rot=(0,0,1;0rad)
  Width = 8
FEATURE [Part::Box] Box503  label="Krychle503"
  AttacherType = Attacher::AttachEngine3D
  Height = 2
  Length = 6
  Placement = pos=(-31.1127,26.8701,-4) rot=(0,0,1;0.785398rad)
  Width = 8
FEATURE [Part::Box] Box504  label="Krychle504"
  AttacherType = Attacher::AttachEngine3D
  Height = 6
  Length = 6
  Placement = pos=(-27,-47,-8) rot=(0,0,1;0rad)
  Width = 2
FEATURE [Part::Box] Box505  label="Krychle505"
  AttacherType = Attacher::AttachEngine3D
  Height = 2
  Length = 6
  Placement = pos=(31.1127,-26.8701,-4) rot=(0,0,1;3.92699rad)
  Width = 8
FEATURE [Part::Cylinder] Cylinder1381  label="Válec1381"
  Angle = 360
  AttacherType = Attacher::AttachEngine3D
  Height = 20
  Placement = pos=(31.8198,31.8198,-18) rot=(0,0,-1;0.785398rad)
  Radius = 1.5
FEATURE [Part::Box] Box506  label="Krychle506"
  AttacherType = Attacher::AttachEngine3D
  Height = 6
  Length = 6
  Placement = pos=(-54,-45,4) rot=(0,0,1;0rad)
  Width = 2
FEATURE [Part::Compound] Compound875
  Links = -> [Cylinder1374,Cylinder1376,Cylinder1372,Cylinder1375]
FEATURE [Part::FeaturePython] wormgear062  # WARN: FeaturePython — macro-defined, semantics opaque (R4)
  AttacherType = Attacher::AttachEngine3D
  Placement = pos=(0,0,0) rot=(0,0,1;0.083427rad)
  beta = 40.5833
  clearance = 0.25
  diameter = 78.8
  head = 0
  height = 20
  module = 1.5
  pressure_angle = 20
  reverse_pitch = false
  teeth = 45
  version = 0.0.3
FEATURE [Part::FeaturePython] wormgear063  # WARN: FeaturePython — macro-defined, semantics opaque (R4)
  AttacherType = Attacher::AttachEngine3D
  Placement = pos=(0,0,0) rot=(0,0,1;0.124791rad)
  beta = 40.5833
  clearance = 0.25
  diameter = 78.8
  head = 0
  height = 20
  module = 1.5
  pressure_angle = 20
  reverse_pitch = true
  teeth = 45
  version = 0.0.3
FEATURE [Part::Cylinder] Cylinder1382  label="Válec1382"
  Angle = 360
  AttacherType = Attacher::AttachEngine3D
  Height = 20
  Placement = pos=(-31.8198,31.8198,-18) rot=(0,0,1;0.785398rad)
  Radius = 1.5
FEATURE [Part::Box] Box507  label="Krychle507"
  AttacherType = Attacher::AttachEngine3D
  Height = 6
  Length = 6
  Placement = pos=(21,-47,-8) rot=(0,0,1;0rad)
  Width = 2
FEATURE [Part::Compound] Compound874
  Links = -> [Box504,Box507,Box499,Box506]
FEATURE [Part::Cut] Cut494
  Base = -> Tube091
  Tool = -> Compound874
FEATURE [Part::Cut] Cut492
  Base = -> Cut494
  Tool = -> Compound875
FEATURE [Part::Cylinder] Cylinder1383  label="Válec1383"
  Angle = 360
  AttacherType = Attacher::AttachEngine3D
  Height = 20
  Placement = pos=(31.8198,-31.8198,-18) rot=(0,0,1;3.92699rad)
  Radius = 1.5
FEATURE [Part::Compound] Compound872
  Links = -> [Cylinder1373,Cylinder1382,Cylinder1378,Cylinder1379,Cylinder1377,Cylinder1383,Cylinder1380,Cylinder1381]
  Placement = pos=(0,0,0) rot=(0,0,1;0.392699rad)
FEATURE [Part::Box] Box508  label="Krychle508"
  AttacherType = Attacher::AttachEngine3D
  Height = 2
  Length = 6
  Placement = pos=(26.8701,31.1127,-4) rot=(0,0,-1;0.785398rad)
  Width = 8
FEATURE [Part::Box] Box509  label="Krychle509"
  AttacherType = Attacher::AttachEngine3D
  Height = 2
  Length = 6
  Placement = pos=(-26.8701,-31.1127,-4) rot=(0,0,1;2.35619rad)
  Width = 8
FEATURE [Part::Compound] Compound873
  Links = -> [Box502,Box503,Box500,Box509,Box498,Box505,Box501,Box508]
  Placement = pos=(0,0,0) rot=(0,0,1;0.392699rad)
FEATURE [Part::Cut] Cut493
  Base = -> Cut492
  Tool = -> Compound873
FEATURE [Part::Cut] Cut491
  Base = -> Cut493
  Placement = pos=(0,0,-6) rot=(0,0,1;0rad)
  Tool = -> Compound872
FEATURE [Part::Cylinder] Cylinder1384  label="Válec1384"
  Angle = 360
  AttacherType = Attacher::AttachEngine3D
  Height = 40
  Placement = pos=(-59,-17,0) rot=(0,0,1;0rad)
  Radius = 10
FEATURE [Part::Cylinder] Cylinder1385  label="Válec1385"
  Angle = 360
  AttacherType = Attacher::AttachEngine3D
  Height = 20
  Placement = pos=(-51,-40,7) rot=(1,0,0;1.5708rad)
  Radius = 1.5
FEATURE [Part::Box] Box510  label="Krychle510"
  AttacherType = Attacher::AttachEngine3D
  Height = 12
  Length = 108
  Placement = pos=(-54,-53,20) rot=(0,0,1;0rad)
  Width = 36
FEATURE [Part::Cylinder] Cylinder1386  label="Válec1386"
  Angle = 360
  AttacherType = Attacher::AttachEngine3D
  Height = 20
  Placement = pos=(0,0,20) rot=(0,0,1;0rad)
  Radius = 52
FEATURE [Part::Cut] Cut498
  Base = -> Box510
  Placement = pos=(0,0,-20) rot=(0,0,1;0rad)
  Tool = -> Cylinder1386
FEATURE [Part::Cylinder] Cylinder1387  label="Válec1387"
  Angle = 360
  AttacherType = Attacher::AttachEngine3D
  Height = 20
  Placement = pos=(-39.6,-39.6,-10) rot=(0,0,-1;0.785398rad)
  Radius = 4
FEATURE [Part::Box] Box511  label="Krychle511"
  AttacherType = Attacher::AttachEngine3D
  Height = 6
  Length = 6
  Placement = pos=(48,-45,4) rot=(0,0,1;0rad)
  Width = 2
FEATURE [Part::Cylinder] Cylinder1388  label="Válec1388"
  Angle = 360
  AttacherType = Attacher::AttachEngine3D
  Height = 40
  Placement = pos=(59,-17,0) rot=(0,0,1;0rad)
  Radius = 10
FEATURE [Part::Compound] Compound878
  Links = -> [Cylinder1388,Cylinder1384]
FEATURE [Part::Cut] Cut499
  Base = -> Cut498
  Tool = -> Compound878
FEATURE [Part::Cylinder] Cylinder1389  label="Válec1389"
  Angle = 360
  AttacherType = Attacher::AttachEngine3D
  Height = 20
  Placement = pos=(-20,-40,-5) rot=(1,0,0;1.5708rad)
  Radius = 1.5
FEATURE [Part::Cylinder] Cylinder1390  label="Válec1390"
  Angle = 360
  AttacherType = Attacher::AttachEngine3D
  Height = 20
  Placement = pos=(51,-40,7) rot=(1,0,0;1.5708rad)
  Radius = 1.5
FEATURE [Part::Cylinder] Cylinder1391  label="Válec1391"
  Angle = 360
  AttacherType = Attacher::AttachEngine3D
  Height = 20
  Placement = pos=(20,-40,-5) rot=(1,0,0;1.5708rad)
  Radius = 1.5
FEATURE [Part::Compound] Compound879
  Links = -> [Cylinder1389,Cylinder1391,Cylinder1390,Cylinder1385]
FEATURE [Part::Box] Box512  label="Krychle512"
  AttacherType = Attacher::AttachEngine3D
  Height = 6
  Length = 6
  Placement = pos=(-23,-47,-8) rot=(0,0,1;0rad)
  Width = 2
FEATURE [Part::Box] Box513  label="Krychle513"
  AttacherType = Attacher::AttachEngine3D
  Height = 6
  Length = 6
  Placement = pos=(-54,-45,4) rot=(0,0,1;0rad)
  Width = 2
FEATURE [Part::Cylinder] Cylinder1392  label="Válec1392"
  Angle = 360
  AttacherType = Attacher::AttachEngine3D
  Height = 20
  Placement = pos=(39.6,-39.6,-10) rot=(0,0,1;0.785398rad)
  Radius = 4
FEATURE [Part::Compound] Compound876
  Links = -> [Cylinder1387,Cylinder1392]
FEATURE [Part::Cut] Cut496
  Base = -> Cut499
  Tool = -> Compound876
FEATURE [Part::Box] Box514  label="Krychle514"
  AttacherType = Attacher::AttachEngine3D
  Height = 6
  Length = 6
  Placement = pos=(17,-47,-8) rot=(0,0,1;0rad)
  Width = 2
FEATURE [Part::Compound] Compound877
  Links = -> [Box512,Box514,Box511,Box513]
FEATURE [Part::Cut] Cut497
  Base = -> Cut496
  Tool = -> Compound877
FEATURE [Part::Cut] Cut495
  Base = -> Cut497
  Tool = -> Compound879
FEATURE [Part::Fillet] Fillet022
  Base = -> Cut495
  Edges = 2 edges r=12: [Edge3,Edge36]
  Placement = pos=(0,0,-6) rot=(0,0,1;0rad)
FEATURE [Part::Cylinder] Cylinder1393  label="Válec1393"
  Angle = 360
  AttacherType = Attacher::AttachEngine3D
  Height = 50
  Placement = pos=(31.8198,31.8198,-18) rot=(0,0,-1;0.785398rad)
  Radius = 1.5
FEATURE [Part::Cylinder] Cylinder1394  label="Válec1394"
  Angle = 360
  AttacherType = Attacher::AttachEngine3D
  Height = 50
  Placement = pos=(39.598,-39.598,2) rot=(0,0,1;0.785398rad)
  Radius = 1.5
FEATURE [Part::Cylinder] Cylinder1395  label="Válec1395"
  Angle = 360
  AttacherType = Attacher::AttachEngine3D
  Height = 50
  Placement = pos=(0,45,-18) rot=(0,0,1;0rad)
  Radius = 1.5
FEATURE [Part::Cylinder] Cylinder1396  label="Válec1396"
  Angle = 360
  AttacherType = Attacher::AttachEngine3D
  Height = 50
  Placement = pos=(1.4e-14,-45,-18) rot=(0,0,1;3.14159rad)
  Radius = 1.5
FEATURE [Part::Cylinder] Cylinder1397  label="Válec1397"
  Angle = 360
  AttacherType = Attacher::AttachEngine3D
  Height = 50
  Placement = pos=(31.8198,-31.8198,-18) rot=(0,0,1;3.92699rad)
  Radius = 1.5
FEATURE [Part::Cylinder] Cylinder1398  label="Válec1398"
  Angle = 360
  AttacherType = Attacher::AttachEngine3D
  Height = 20
  Placement = pos=(39.6,-39.6,-10) rot=(0,0,1;0.785398rad)
  Radius = 4
FEATURE [Part::Cylinder] Cylinder1399  label="Válec1399"
  Angle = 360
  AttacherType = Attacher::AttachEngine3D
  Height = 50
  Placement = pos=(-31.8198,31.8198,-18) rot=(0,0,1;0.785398rad)
  Radius = 1.5
FEATURE [Part::Cylinder] Cylinder1400  label="Válec1400"
  Angle = 360
  AttacherType = Attacher::AttachEngine3D
  Height = 50
  Placement = pos=(-56,-1.3e-14,2) rot=(0,0,-1;1.5708rad)
  Radius = 1.5
FEATURE [Part::Cylinder] Cylinder1401  label="Válec1401"
  Angle = 360
  AttacherType = Attacher::AttachEngine3D
  Height = 50
  Placement = pos=(45,1.9e-14,-18) rot=(0,0,-1;1.5708rad)
  Radius = 1.5
FEATURE [Part::Cylinder] Cylinder1402  label="Válec1402"
  Angle = 360
  AttacherType = Attacher::AttachEngine3D
  Height = 50
  Placement = pos=(-39.598,39.598,2) rot=(0,0,1;3.92699rad)
  Radius = 1.5
FEATURE [Part::Cylinder] Cylinder1403  label="Válec1403"
  Angle = 360
  AttacherType = Attacher::AttachEngine3D
  Height = 50
  Placement = pos=(-31.8198,-31.8198,-18) rot=(0,0,1;2.35619rad)
  Radius = 1.5
FEATURE [Part::Cylinder] Cylinder1404  label="Válec1404"
  Angle = 360
  AttacherType = Attacher::AttachEngine3D
  Height = 50
  Placement = pos=(-45,-6e-15,-18) rot=(0,0,1;1.5708rad)
  Radius = 1.5
FEATURE [Part::Cylinder] Cylinder1405  label="Válec1405"
  Angle = 360
  AttacherType = Attacher::AttachEngine3D
  Height = 50
  Placement = pos=(-39.598,-39.598,2) rot=(0,0,-1;0.785398rad)
  Radius = 1.5
FEATURE [Part::Cylinder] Cylinder1406  label="Válec1406"
  Angle = 360
  AttacherType = Attacher::AttachEngine3D
  Height = 12
  Radius = 52
FEATURE [Part::Cut] Cut500
  Base = -> Cylinder1406
  Tool = -> wormgear062
FEATURE [Part::Cylinder] Cylinder1407  label="Válec1407"
  Angle = 360
  AttacherType = Attacher::AttachEngine3D
  Height = 50
  Placement = pos=(0,-56,2) rot=(0,0,1;0rad)
  Radius = 1.5
FEATURE [Part::Cylinder] Cylinder1408  label="Válec1408"
  Angle = 360
  AttacherType = Attacher::AttachEngine3D
  Height = 50
  Placement = pos=(-1.2e-14,56,2) rot=(0,0,1;3.14159rad)
  Radius = 1.5
FEATURE [Part::Cylinder] Cylinder1409  label="Válec1409"
  Angle = 360
  AttacherType = Attacher::AttachEngine3D
  Height = 50
  Placement = pos=(39.598,39.598,2) rot=(0,0,1;2.35619rad)
  Radius = 1.5
FEATURE [Part::Cylinder] Cylinder1410  label="Válec1410"
  Angle = 360
  AttacherType = Attacher::AttachEngine3D
  Height = 12
  Radius = 60
FEATURE [Part::Cylinder] Cylinder1411  label="Válec1411"
  Angle = 360
  AttacherType = Attacher::AttachEngine3D
  Height = 50
  Placement = pos=(56,0,2) rot=(0,0,1;1.5708rad)
  Radius = 1.5
FEATURE [Part::Compound] Compound881
  Links = -> [Cylinder1407,Cylinder1394,Cylinder1411,Cylinder1409,Cylinder1408,Cylinder1402,Cylinder1400,Cylinder1405]
FEATURE [Part::Cylinder] Cylinder1412  label="Válec1412"
  Angle = 360
  AttacherType = Attacher::AttachEngine3D
  Height = 20
  Placement = pos=(-39.6,-39.6,-10) rot=(0,0,-1;0.785398rad)
  Radius = 4
FEATURE [Part::Compound] Compound880
  Links = -> [Cylinder1412,Cylinder1398]
FEATURE [Part::Cylinder] Cylinder1413  label="Válec1413"
  Angle = 360
  AttacherType = Attacher::AttachEngine3D
  Height = 40
  Placement = pos=(0,-17,13) rot=(1,0,0;1.5708rad)
  Radius = 59
FEATURE [Part::Cut] Cut503
  Base = -> Cylinder1410
  Placement = pos=(0,0,12) rot=(0,0,1;0.034907rad)
  Tool = -> wormgear063
FEATURE [Part::Compound] Compound882
  Links = -> [Cut503,Cut500]
FEATURE [Part::Cut] Cut501
  Base = -> Compound882
  Tool = -> Compound881
FEATURE [Part::Cut] Cut504
  Base = -> Cut501
  Tool = -> Compound880
FEATURE [Part::Common] Common004
  Base = -> Fillet020
  Tool = -> Cylinder1413
FEATURE [Part::Compound] Compound883
  Links = -> [Cylinder1395,Cylinder1399,Cylinder1404,Cylinder1403,Cylinder1396,Cylinder1397,Cylinder1401,Cylinder1393]
  Placement = pos=(0,0,-20) rot=(0,0,1;0.392699rad)
FEATURE [Part::Cut] Cut502
  Base = -> Cut504
  Placement = pos=(0,0,-6) rot=(0,0,1;0rad)
  Tool = -> Compound883
FEATURE [Part::Compound] Compound884  label="J-max-deep_monoblok"
  Links = -> [Fillet021,Cut489,Cut491,Fillet022,Cut502,Common004]
  Placement = pos=(52,13,-75) rot=(0,0.707107,-0.707107;3.14159rad)
FEATURE [Part::Torus] Torus004  label="Anuloid004"
  Angle1 = -180
  Angle2 = 180
  Angle3 = 360
  AttacherType = Attacher::AttachEngine3D
  Placement = pos=(0,0,34) rot=(0,0,1;0rad)
  Radius1 = 51.9
  Radius2 = 3.1
FEATURE [Part::Box] Box464  label="Krychle464"
  AttacherType = Attacher::AttachEngine3D
  Height = 19
  Length = 10
  Placement = pos=(-60,-43,10) rot=(0,0,1;0rad)
  Width = 43
FEATURE [Part::Box] Box465  label="Krychle465"
  AttacherType = Attacher::AttachEngine3D
  Height = 19
  Length = 10
  Placement = pos=(50,-43,10) rot=(0,0,1;0rad)
  Width = 43
FEATURE [Part::Cylinder] Cylinder1414  label="Válec1414"
  Angle = 360
  AttacherType = Attacher::AttachEngine3D
  Height = 33
  Placement = pos=(60,-43,10) rot=(0,0,1;0rad)
  Radius = 6
FEATURE [Part::Box] Box466  label="Krychle466"
  AttacherType = Attacher::AttachEngine3D
  Height = 2
  Length = 6
  Placement = pos=(45.9619,41.7193,23) rot=(0,0,1;2.35619rad)
  Width = 10
FEATURE [Part::Box] Box467  label="Krychle467"
  AttacherType = Attacher::AttachEngine3D
  Height = 2
  Length = 6
  Placement = pos=(62,-3,23) rot=(0,0,1;1.5708rad)
  Width = 10
FEATURE [Part::Box] Box468  label="Krychle468"
  AttacherType = Attacher::AttachEngine3D
  Height = 2
  Length = 6
  Placement = pos=(41.7193,-45.9619,23) rot=(0,0,1;0.785398rad)
  Width = 10
FEATURE [Part::Box] Box469  label="Krychle469"
  AttacherType = Attacher::AttachEngine3D
  Height = 2
  Length = 6
  Placement = pos=(-3,-62,23) rot=(0,0,1;0rad)
  Width = 10
FEATURE [Part::Box] Box470  label="Krychle470"
  AttacherType = Attacher::AttachEngine3D
  Height = 2
  Length = 6
  Placement = pos=(-45.9619,-41.7193,23) rot=(0,0,-1;0.785398rad)
  Width = 10
FEATURE [Part::Box] Box471  label="Krychle471"
  AttacherType = Attacher::AttachEngine3D
  Height = 2
  Length = 6
  Placement = pos=(-62,3,23) rot=(0,0,-1;1.5708rad)
  Width = 10
FEATURE [Part::Cylinder] Cylinder1415  label="Válec1415"
  Angle = 360
  AttacherType = Attacher::AttachEngine3D
  Height = 50
  Placement = pos=(39.598,39.598,2) rot=(0,0,1;2.35619rad)
  Radius = 1.5
FEATURE [Part::Cylinder] Cylinder1416  label="Válec1416"
  Angle = 360
  AttacherType = Attacher::AttachEngine3D
  Height = 33
  Placement = pos=(-60,-43,10) rot=(0,0,1;0rad)
  Radius = 6
FEATURE [Part::Cylinder] Cylinder1417  label="Válec1417"
  Angle = 360
  AttacherType = Attacher::AttachEngine3D
  Height = 50
  Placement = pos=(-39.598,39.598,2) rot=(0,0,1;3.92699rad)
  Radius = 1.5
FEATURE [Part::Cylinder] Cylinder1418  label="Válec1418"
  Angle = 360
  AttacherType = Attacher::AttachEngine3D
  Height = 50
  Placement = pos=(56,0,2) rot=(0,0,1;1.5708rad)
  Radius = 1.5
FEATURE [Part::Cylinder] Cylinder1302  label="Válec1302"
  Angle = 360
  AttacherType = Attacher::AttachEngine3D
  Height = 50
  Placement = pos=(-1.2e-14,56,2) rot=(0,0,1;3.14159rad)
  Radius = 1.5
FEATURE [Part::Cylinder] Cylinder1303  label="Válec1303"
  Angle = 360
  AttacherType = Attacher::AttachEngine3D
  Height = 50
  Placement = pos=(-56,-1.3e-14,2) rot=(0,0,-1;1.5708rad)
  Radius = 1.5
FEATURE [Part::Cylinder] Cylinder1304  label="Válec1304"
  Angle = 360
  AttacherType = Attacher::AttachEngine3D
  Height = 50
  Placement = pos=(0,-56,2) rot=(0,0,1;0rad)
  Radius = 1.5
FEATURE [Part::Cylinder] Cylinder1305  label="Válec1305"
  Angle = 360
  AttacherType = Attacher::AttachEngine3D
  Height = 50
  Placement = pos=(39.598,-39.598,2) rot=(0,0,1;0.785398rad)
  Radius = 1.5
FEATURE [Part::Cylinder] Cylinder1306  label="Válec1306"
  Angle = 360
  AttacherType = Attacher::AttachEngine3D
  Height = 50
  Placement = pos=(-39.598,-39.598,2) rot=(0,0,-1;0.785398rad)
  Radius = 1.5
FEATURE [Part::Cylinder] Cylinder1307  label="Válec1307"
  Angle = 360
  AttacherType = Attacher::AttachEngine3D
  Height = 33
  Placement = pos=(0,0,20) rot=(0,0,1;0rad)
  Radius = 60
FEATURE [Part::Cylinder] Cylinder1419  label="Válec1419"
  Angle = 360
  AttacherType = Attacher::AttachEngine3D
  Height = 40
  Placement = pos=(-51,-40,25) rot=(1,0,0;1.5708rad)
  Radius = 1.5
FEATURE [Part::Cylinder] Cylinder1420  label="Válec1420"
  Angle = 360
  AttacherType = Attacher::AttachEngine3D
  Height = 40
  Placement = pos=(51,-40,25) rot=(1,0,0;1.5708rad)
  Radius = 1.5
FEATURE [Part::Box] Box472  label="Krychle472"
  AttacherType = Attacher::AttachEngine3D
  Height = 2
  Length = 6
  Placement = pos=(3,62,23) rot=(0,0,1;3.14159rad)
  Width = 10
FEATURE [Part::Box] Box473  label="Krychle473"
  AttacherType = Attacher::AttachEngine3D
  Height = 2
  Length = 6
  Placement = pos=(-41.7193,45.9619,23) rot=(0,0,1;3.92699rad)
  Width = 10
FEATURE [Part::Box] Box474  label="Krychle474"
  AttacherType = Attacher::AttachEngine3D
  Height = 6
  Length = 6
  Placement = pos=(48,-45,35) rot=(0,0,1;0rad)
  Width = 2
FEATURE [Part::Box] Box475  label="Krychle475"
  AttacherType = Attacher::AttachEngine3D
  Height = 6
  Length = 6
  Placement = pos=(-54,-45,35) rot=(0,0,1;0rad)
  Width = 2
FEATURE [Part::Cylinder] Cylinder1421  label="Válec1421"
  Angle = 360
  AttacherType = Attacher::AttachEngine3D
  Height = 40
  Placement = pos=(-51,-40,38) rot=(1,0,0;1.5708rad)
  Radius = 1.5
FEATURE [Part::Cylinder] Cylinder1422  label="Válec1422"
  Angle = 360
  AttacherType = Attacher::AttachEngine3D
  Height = 40
  Placement = pos=(51,-40,38) rot=(1,0,0;1.5708rad)
  Radius = 1.5
FEATURE [Part::Cylinder] Cylinder1423  label="Válec1423"
  Angle = 360
  AttacherType = Attacher::AttachEngine3D
  Height = 10
  Placement = pos=(-40,0,36) rot=(0,0,1;0rad)
  Radius = 3.5
FEATURE [Part::Cylinder] Cylinder1424  label="Válec1424"
  Angle = 360
  AttacherType = Attacher::AttachEngine3D
  Height = 20
  Placement = pos=(39.598,-39.598,2) rot=(0,0,1;0.785398rad)
  Radius = 1.5
FEATURE [Part::Cylinder] Cylinder1425  label="Válec1425"
  Angle = 360
  AttacherType = Attacher::AttachEngine3D
  Height = 50
  Placement = pos=(-51.5,0,34) rot=(0,0,1;0rad)
  Radius = 3.5
FEATURE [Part::Cylinder] Cylinder1426  label="Válec1426"
  Angle = 360
  AttacherType = Attacher::AttachEngine3D
  Height = 20
  Placement = pos=(0,-56,2) rot=(0,0,1;0rad)
  Radius = 1.5
FEATURE [Part::Cylinder] Cylinder1427  label="Válec1427"
  Angle = 360
  AttacherType = Attacher::AttachEngine3D
  Height = 20
  Placement = pos=(56,0,2) rot=(0,0,1;1.5708rad)
  Radius = 1.5
FEATURE [Part::Cylinder] Cylinder1428  label="Válec1428"
  Angle = 360
  AttacherType = Attacher::AttachEngine3D
  Height = 20
  Placement = pos=(39.598,39.598,2) rot=(0,0,1;2.35619rad)
  Radius = 1.5
FEATURE [Part::Cylinder] Cylinder1429  label="Válec1429"
  Angle = 360
  AttacherType = Attacher::AttachEngine3D
  Height = 20
  Placement = pos=(-1.2e-14,56,2) rot=(0,0,1;3.14159rad)
  Radius = 1.5
FEATURE [Part::Cylinder] Cylinder1430  label="Válec1430"
  Angle = 360
  AttacherType = Attacher::AttachEngine3D
  Height = 20
  Placement = pos=(-39.598,39.598,2) rot=(0,0,1;3.92699rad)
  Radius = 1.5
FEATURE [Part::Cylinder] Cylinder1431  label="Válec1431"
  Angle = 360
  AttacherType = Attacher::AttachEngine3D
  Height = 20
  Placement = pos=(-56,-1.3e-14,2) rot=(0,0,-1;1.5708rad)
  Radius = 1.5
FEATURE [Part::Cylinder] Cylinder1432  label="Válec1432"
  Angle = 360
  AttacherType = Attacher::AttachEngine3D
  Height = 20
  Placement = pos=(-39.598,-39.598,2) rot=(0,0,-1;0.785398rad)
  Radius = 1.5
FEATURE [Part::Box] Box476  label="Krychle476"
  AttacherType = Attacher::AttachEngine3D
  Height = 2
  Length = 6
  Placement = pos=(-3,-60,23) rot=(0,0,1;0rad)
  Width = 8
FEATURE [Part::Box] Box477  label="Krychle477"
  AttacherType = Attacher::AttachEngine3D
  Height = 2
  Length = 6
  Placement = pos=(40.3051,-44.5477,23) rot=(0,0,1;0.785398rad)
  Width = 8
FEATURE [Part::Box] Box478  label="Krychle478"
  AttacherType = Attacher::AttachEngine3D
  Height = 2
  Length = 6
  Placement = pos=(60,-3,23) rot=(0,0,1;1.5708rad)
  Width = 8
FEATURE [Part::Box] Box479  label="Krychle479"
  AttacherType = Attacher::AttachEngine3D
  Height = 2
  Length = 6
  Placement = pos=(44.5477,40.3051,23) rot=(0,0,1;2.35619rad)
  Width = 8
FEATURE [Part::Box] Box480  label="Krychle480"
  AttacherType = Attacher::AttachEngine3D
  Height = 2
  Length = 6
  Placement = pos=(3,60,23) rot=(0,0,1;3.14159rad)
  Width = 8
FEATURE [Part::Box] Box481  label="Krychle481"
  AttacherType = Attacher::AttachEngine3D
  Height = 2
  Length = 6
  Placement = pos=(-40.3051,44.5477,23) rot=(0,0,1;3.92699rad)
  Width = 8
FEATURE [Part::Box] Box482  label="Krychle482"
  AttacherType = Attacher::AttachEngine3D
  Height = 2
  Length = 6
  Placement = pos=(-60,3,23) rot=(0,0,-1;1.5708rad)
  Width = 8
FEATURE [Part::Box] Box483  label="Krychle483"
  AttacherType = Attacher::AttachEngine3D
  Height = 2
  Length = 6
  Placement = pos=(-44.5477,-40.3051,23) rot=(0,0,-1;0.785398rad)
  Width = 8
FEATURE [Part::Cylinder] Cylinder1433  label="Válec1433"
  Angle = 360
  AttacherType = Attacher::AttachEngine3D
  Height = 25
  Placement = pos=(0,0,20) rot=(0,0,1;0rad)
  Radius = 60
FEATURE [Part::Box] Box484  label="Krychle484"
  AttacherType = Attacher::AttachEngine3D
  Height = 25
  Length = 108
  Placement = pos=(-54,-53,20) rot=(0,0,1;0rad)
  Width = 46
FEATURE [Part::Cut] Cut458
  Base = -> Box484
  Tool = -> Cylinder1433
FEATURE [Part::Cylinder] Cylinder1434  label="Válec1434"
  Angle = 360
  AttacherType = Attacher::AttachEngine3D
  Height = 40
  Placement = pos=(0,-17,27) rot=(1,0,0;1.5708rad)
  Radius = 59
FEATURE [Part::Box] Box485  label="Krychle485"
  AttacherType = Attacher::AttachEngine3D
  Height = 6
  Length = 6
  Placement = pos=(36,-47,56) rot=(0,0,1;0rad)
  Width = 2
FEATURE [Part::FeaturePython] Tube090  # WARN: FeaturePython — macro-defined, semantics opaque (R4)
  AttacherType = Attacher::AttachEngine3D
  Height = 25
  InnerRadius = 53
  OuterRadius = 60
  Placement = pos=(0,0,20) rot=(0,0,1;0rad)
FEATURE [Part::Compound] Compound851
  Links = -> [Cylinder1421,Cylinder1422]
  Placement = pos=(0,8,-11) rot=(0,0,1;0rad)
FEATURE [Part::Cut] Cut468
  Base = -> Cut458
  Tool = -> Compound851
FEATURE [Part::Compound] Compound852
  Links = -> [Cylinder1426,Cylinder1424,Cylinder1427,Cylinder1428,Cylinder1429,Cylinder1430,Cylinder1431,Cylinder1432]
  Placement = pos=(0,0,10) rot=(0,0,1;0rad)
FEATURE [Part::Compound] Compound853
  Links = -> [Box474,Box475]
  Placement = pos=(0,0,-11) rot=(0,0,1;0rad)
FEATURE [Part::Cut] Cut455
  Base = -> Cut468
  Placement = pos=(0,0,12) rot=(0,0,1;0rad)
  Tool = -> Compound853
FEATURE [Part::Common] Common002
  Base = -> Cut455
  Tool = -> Cylinder1434
FEATURE [Part::Compound] Compound854
  Links = -> [Cylinder1304,Cylinder1305,Cylinder1418,Cylinder1415,Cylinder1302,Cylinder1417,Cylinder1303,Cylinder1306]
FEATURE [Part::Compound] Compound855
  Links = -> [Box476,Box477,Box478,Box479,Box480,Box481,Box482,Box483]
  Placement = pos=(0,0,1) rot=(0,0,1;0rad)
FEATURE [Part::Compound] Compound856
  Links = -> [Cylinder1419,Cylinder1420]
  Placement = pos=(0,8,2) rot=(0,0,1;0rad)
FEATURE [Part::Compound] Compound857
  Links = -> [Box472,Box473,Box471,Box470,Box469,Box468,Box467,Box466]
  Placement = pos=(0,0,1) rot=(0,0,1;0rad)
FEATURE [Part::Compound] Compound858
  Links = -> [Cylinder1414,Cylinder1416]
FEATURE [Part::Compound] Compound859
  Links = -> [Box464,Box465]
FEATURE [Part::Cut] Cut460
  Base = -> Compound859
  Tool = -> Compound854
FEATURE [Part::Cut] Cut461
  Base = -> Cut460
  Placement = pos=(0,0,10) rot=(0,0,1;0rad)
  Tool = -> Compound858
FEATURE [Part::Cut] Cut463
  Base = -> Tube090
  Tool = -> Torus004
FEATURE [Part::Cut] Cut462
  Base = -> Cut463
  Tool = -> Cylinder1423
FEATURE [Part::Cut] Cut456  label="J-max_lozo-harmo006"
  Base = -> Cut462
  Tool = -> Cylinder1425
FEATURE [Part::Cut] Cut457
  Base = -> Cut456
  Tool = -> Compound852
FEATURE [Part::Cut] Cut464
  Base = -> Cut457
  Placement = pos=(0,0,12) rot=(0,0,1;0rad)
  Tool = -> Compound855
FEATURE [Part::Cut] Cut465
  Base = -> Cut461
  Tool = -> Cylinder1307
FEATURE [Part::Cut] Cut466
  Base = -> Cut465
  Tool = -> Compound857
FEATURE [Part::Cut] Cut467
  Base = -> Cut466
  Placement = pos=(0,0,12) rot=(0,0,1;0rad)
  Tool = -> Compound856
FEATURE [Part::Cylinder] Cylinder1435  label="Válec1435"
  Angle = 360
  AttacherType = Attacher::AttachEngine3D
  Height = 40
  Placement = pos=(39,-40,59) rot=(1,0,0;1.5708rad)
  Radius = 1.5
FEATURE [Part::Cylinder] Cylinder1436  label="Válec1436"
  Angle = 360
  AttacherType = Attacher::AttachEngine3D
  Height = 40
  Placement = pos=(-39,-40,59) rot=(1,0,0;1.5708rad)
  Radius = 1.5
FEATURE [Part::Compound] Compound847
  Links = -> [Cylinder1435,Cylinder1436]
  Placement = pos=(0,0,-5) rot=(0,0,1;0rad)
FEATURE [Part::Box] Box486  label="Krychle486"
  AttacherType = Attacher::AttachEngine3D
  Height = 6
  Length = 6
  Placement = pos=(-42,-47,56) rot=(0,0,1;0rad)
  Width = 2
FEATURE [Part::Compound] Compound850
  Links = -> [Box486,Box485]
  Placement = pos=(0,2,-5) rot=(0,0,1;0rad)
FEATURE [Part::Cut] Cut470
  Base = -> Common002
  Tool = -> Compound850
FEATURE [Part::Cut] Cut471
  Base = -> Cut470
  Tool = -> Compound847
FEATURE [Part::Box] Box487  label="Krychle487"
  AttacherType = Attacher::AttachEngine3D
  Height = 6
  Length = 6
  Placement = pos=(36,-47,56) rot=(0,0,1;0rad)
  Width = 2
FEATURE [Part::Box] Box488  label="Krychle488"
  AttacherType = Attacher::AttachEngine3D
  Height = 6
  Length = 6
  Placement = pos=(-42,-47,56) rot=(0,0,1;0rad)
  Width = 2
FEATURE [Part::Compound] Compound849
  Links = -> [Box488,Box487]
  Placement = pos=(0,2,-5) rot=(0,0,1;0rad)
FEATURE [Part::Cut] Cut459
  Base = -> Cut464
  Tool = -> Compound849
FEATURE [Part::Cylinder] Cylinder1437  label="Válec1437"
  Angle = 360
  AttacherType = Attacher::AttachEngine3D
  Height = 40
  Placement = pos=(39,-40,59) rot=(1,0,0;1.5708rad)
  Radius = 1.5
FEATURE [Part::Cylinder] Cylinder1327  label="Válec1327"
  Angle = 360
  AttacherType = Attacher::AttachEngine3D
  Height = 40
  Placement = pos=(-39,-40,59) rot=(1,0,0;1.5708rad)
  Radius = 1.5
FEATURE [Part::Compound] Compound848
  Links = -> [Cylinder1437,Cylinder1327]
  Placement = pos=(0,2,-5) rot=(0,0,1;0rad)
FEATURE [Part::Cut] Cut469
  Base = -> Cut459
  Tool = -> Compound848
FEATURE [Part::Fillet] Fillet019
  Base = -> Cut467
  Edges = 2 edges r=8: [Edge8,Edge63]
FEATURE [Part::Compound] Compound860  label="J-max-deep_bearing-ring"
  Links = -> [Cut469,Fillet019,Cut471]
  Placement = pos=(52,27,-75) rot=(0,0.707107,-0.707107;3.14159rad)
FEATURE [Part::Cylinder] Cylinder1438  label="Válec1438"
  Angle = 360
  AttacherType = Attacher::AttachEngine3D
  Height = 100
  Placement = pos=(103,-12,-60) rot=(0,0,1;0rad)
  Radius = 1.5
FEATURE [Part::Cylinder] Cylinder1439  label="Válec1439"
  Angle = 360
  AttacherType = Attacher::AttachEngine3D
  Height = 100
  Placement = pos=(103,12,-60) rot=(0,0,1;0rad)
  Radius = 1.5
FEATURE [Part::Cylinder] Cylinder1440  label="Válec1440"
  Angle = 360
  AttacherType = Attacher::AttachEngine3D
  Height = 100
  Placement = pos=(76,24,-60) rot=(0,0,1;0rad)
  Radius = 1.5
FEATURE [Part::Cylinder] Cylinder1441  label="Válec1441"
  Angle = 360
  AttacherType = Attacher::AttachEngine3D
  Height = 100
  Placement = pos=(91,-27,-60) rot=(0,0,1;0rad)
  Radius = 1.5
FEATURE [Part::Cylinder] Cylinder1442  label="Válec1442"
  Angle = 360
  AttacherType = Attacher::AttachEngine3D
  Height = 100
  Placement = pos=(13,-27,-60) rot=(0,0,1;0rad)
  Radius = 1.5
FEATURE [Part::Cylinder] Cylinder1443  label="Válec1443"
  Angle = 360
  AttacherType = Attacher::AttachEngine3D
  Height = 100
  Placement = pos=(28,24,-60) rot=(0,0,1;0rad)
  Radius = 1.5
FEATURE [Part::Cylinder] Cylinder1444  label="Válec1444"
  Angle = 360
  AttacherType = Attacher::AttachEngine3D
  Height = 100
  Placement = pos=(1,-12,-60) rot=(0,0,1;0rad)
  Radius = 1.5
FEATURE [Part::Cylinder] Cylinder1445  label="Válec1445"
  Angle = 360
  AttacherType = Attacher::AttachEngine3D
  Height = 100
  Placement = pos=(1,12,-60) rot=(0,0,1;0rad)
  Radius = 1.5
FEATURE [Part::Compound] Compound663  label="srouby_monoblok002"
  Links = -> [Cylinder1438,Cylinder1439,Cylinder1440,Cylinder1441,Cylinder1442,Cylinder1443,Cylinder1444,Cylinder1445]
FEATURE [Part::Cut] Cut296
  Base = -> Extrude002
  Tool = -> Compound663
FEATURE [Part::Cylinder] Cylinder1446  label="Válec1446"
  Angle = 360
  AttacherType = Attacher::AttachEngine3D
  Height = 20
  Placement = pos=(103,-12,-20) rot=(0,0,1;0rad)
  Radius = 4
FEATURE [Part::Cylinder] Cylinder1447  label="Válec1447"
  Angle = 360
  AttacherType = Attacher::AttachEngine3D
  Height = 20
  Placement = pos=(103,12,-20) rot=(0,0,1;0rad)
  Radius = 4
FEATURE [Part::Cylinder] Cylinder1448  label="Válec1448"
  Angle = 360
  AttacherType = Attacher::AttachEngine3D
  Height = 20
  Placement = pos=(76,24,-18) rot=(0,0,1;0rad)
  Radius = 4
FEATURE [Part::Cylinder] Cylinder1449  label="Válec1449"
  Angle = 360
  AttacherType = Attacher::AttachEngine3D
  Height = 20
  Placement = pos=(91,-27,-18) rot=(0,0,1;0rad)
  Radius = 4
FEATURE [Part::Cylinder] Cylinder1450  label="Válec1450"
  Angle = 360
  AttacherType = Attacher::AttachEngine3D
  Height = 40
  Placement = pos=(13,-27,-18) rot=(0,0,1;0rad)
  Radius = 4
FEATURE [Part::Cylinder] Cylinder1451  label="Válec1451"
  Angle = 360
  AttacherType = Attacher::AttachEngine3D
  Height = 40
  Placement = pos=(28,24,-18) rot=(0,0,1;0rad)
  Radius = 4
FEATURE [Part::Cylinder] Cylinder1452  label="Válec1452"
  Angle = 360
  AttacherType = Attacher::AttachEngine3D
  Height = 40
  Placement = pos=(1,-12,-18) rot=(0,0,1;0rad)
  Radius = 4
FEATURE [Part::Cylinder] Cylinder1453  label="Válec1453"
  Angle = 360
  AttacherType = Attacher::AttachEngine3D
  Height = 40
  Placement = pos=(1,12,-18) rot=(0,0,1;0rad)
  Radius = 4
FEATURE [Part::Compound] Compound664  label="srouby_monoblok_silne003"
  Links = -> [Cylinder1446,Cylinder1447,Cylinder1448,Cylinder1449,Cylinder1450,Cylinder1451,Cylinder1452,Cylinder1453]
FEATURE [Part::Cut] Cut295
  Base = -> Cut296
  Tool = -> Compound664
FEATURE [Part::Cut] Cut297
  Base = -> Cut295
  Tool = -> Compound665
FEATURE [Part::Cut] Cut298
  Base = -> Cut297
  Tool = -> Compound666
FEATURE [Part::Cut] Cut299
  Base = -> Cut298
  Tool = -> Box240
FEATURE [Part::Cut] Cut300
  Base = -> Cut299
  Tool = -> Box241
FEATURE [Part::Cut] Cut301
  Base = -> Cut300
  Tool = -> Compound667
FEATURE [Part::Cut] Cut302
  Base = -> Cut301
  Tool = -> Compound668
FEATURE [Part::Cut] Cut303
  Base = -> Cut302
  Tool = -> Compound670
FEATURE [Part::Cut] Cut304
  Base = -> Cut303
  Tool = -> Compound669
FEATURE [Part::Chamfer] Chamfer
  Base = -> Cut304
  Edges = 1 edges r=4: [Edge44]
FEATURE [Part::Chamfer] Chamfer039
  Base = -> Chamfer
  Edges = 2 edges r=3.5: [Edge4,Edge6]
FEATURE [Part::Cylinder] Cylinder1454  label="Válec1454"
  Angle = 360
  AttacherType = Attacher::AttachEngine3D
  Height = 4
  Placement = pos=(52,0,-26) rot=(0,0,1;0rad)
  Radius = 59
FEATURE [Part::Cylinder] Cylinder1455  label="Válec1455"
  Angle = 360
  AttacherType = Attacher::AttachEngine3D
  Height = 100
  Placement = pos=(103,-12,-60) rot=(0,0,1;0rad)
  Radius = 1.5
FEATURE [Part::Cylinder] Cylinder1456  label="Válec1456"
  Angle = 360
  AttacherType = Attacher::AttachEngine3D
  Height = 100
  Placement = pos=(103,12,-60) rot=(0,0,1;0rad)
  Radius = 1.5
FEATURE [Part::Cylinder] Cylinder1457  label="Válec1457"
  Angle = 360
  AttacherType = Attacher::AttachEngine3D
  Height = 100
  Placement = pos=(76,24,-60) rot=(0,0,1;0rad)
  Radius = 1.5
FEATURE [Part::Cylinder] Cylinder1458  label="Válec1458"
  Angle = 360
  AttacherType = Attacher::AttachEngine3D
  Height = 100
  Placement = pos=(91,-27,-60) rot=(0,0,1;0rad)
  Radius = 1.5
FEATURE [Part::Cylinder] Cylinder1459  label="Válec1459"
  Angle = 360
  AttacherType = Attacher::AttachEngine3D
  Height = 100
  Placement = pos=(13,-27,-60) rot=(0,0,1;0rad)
  Radius = 1.5
FEATURE [Part::Cylinder] Cylinder1460  label="Válec1460"
  Angle = 360
  AttacherType = Attacher::AttachEngine3D
  Height = 100
  Placement = pos=(28,24,-60) rot=(0,0,1;0rad)
  Radius = 1.5
FEATURE [Part::Cylinder] Cylinder1461  label="Válec1461"
  Angle = 360
  AttacherType = Attacher::AttachEngine3D
  Height = 100
  Placement = pos=(1,-12,-60) rot=(0,0,1;0rad)
  Radius = 1.5
FEATURE [Part::Cylinder] Cylinder1462  label="Válec1462"
  Angle = 360
  AttacherType = Attacher::AttachEngine3D
  Height = 100
  Placement = pos=(1,12,-60) rot=(0,0,1;0rad)
  Radius = 1.5
FEATURE [Part::Compound] Compound885  label="srouby_monoblok003"
  Links = -> [Cylinder1455,Cylinder1456,Cylinder1457,Cylinder1458,Cylinder1459,Cylinder1460,Cylinder1461,Cylinder1462]
FEATURE [Part::Cut] Cut505
  Base = -> Cylinder1454
  Tool = -> Compound885
FEATURE [Part::Box] Box515  label="Krychle515"
  AttacherType = Attacher::AttachEngine3D
  Height = 100
  Length = 200
  Placement = pos=(-60,-130,-90) rot=(0,0,1;0rad)
  Width = 100
FEATURE [Part::Box] Box516  label="Krychle516"
  AttacherType = Attacher::AttachEngine3D
  Height = 100
  Length = 200
  Placement = pos=(-60,44,-90) rot=(0,0,1;0rad)
  Width = 100
FEATURE [Part::Cylinder] Cylinder1463  label="Válec1463"
  Angle = 360
  AttacherType = Attacher::AttachEngine3D
  Height = 100
  Placement = pos=(-34,-16,-90) rot=(0,0,1;0rad)
  Radius = 4
FEATURE [Part::Cylinder] Cylinder1464  label="Válec1464"
  Angle = 360
  AttacherType = Attacher::AttachEngine3D
  Height = 100
  Placement = pos=(-16,34,-90) rot=(0,0,1;0rad)
  Radius = 4
FEATURE [Part::Cylinder] Cylinder1465  label="Válec1465"
  Angle = 360
  AttacherType = Attacher::AttachEngine3D
  Height = 100
  Placement = pos=(-16,-34,-90) rot=(0,0,1;0rad)
  Radius = 4
FEATURE [Part::Cylinder] Cylinder1466  label="Válec1466"
  Angle = 360
  AttacherType = Attacher::AttachEngine3D
  Height = 100
  Placement = pos=(34,-16,-90) rot=(0,0,1;0rad)
  Radius = 4
FEATURE [Part::Cylinder] Cylinder1467  label="Válec1467"
  Angle = 360
  AttacherType = Attacher::AttachEngine3D
  Height = 100
  Placement = pos=(16,34,-90) rot=(0,0,1;0rad)
  Radius = 4
FEATURE [Part::Cylinder] Cylinder1468  label="Válec1468"
  Angle = 360
  AttacherType = Attacher::AttachEngine3D
  Height = 100
  Placement = pos=(16,-34,-90) rot=(0,0,1;0rad)
  Radius = 4
FEATURE [Part::Cylinder] Cylinder1469  label="Válec1469"
  Angle = 360
  AttacherType = Attacher::AttachEngine3D
  Height = 100
  Placement = pos=(-34,16,-90) rot=(0,0,1;0rad)
  Radius = 4
FEATURE [Part::Cylinder] Cylinder1470  label="Válec1470"
  Angle = 360
  AttacherType = Attacher::AttachEngine3D
  Height = 100
  Placement = pos=(34,16,-90) rot=(0,0,1;0rad)
  Radius = 4
FEATURE [Part::Compound] Compound886  label="sbouby_baze_silne005"
  Links = -> [Cylinder1463,Cylinder1464,Cylinder1465,Cylinder1466,Cylinder1467,Cylinder1468,Cylinder1469,Cylinder1470]
FEATURE [Part::Cut] Cut506
  Base = -> Cut505
  Tool = -> Compound886
FEATURE [Part::Cut] Cut507
  Base = -> Cut506
  Tool = -> Box515
FEATURE [Part::Cut] Cut508
  Base = -> Cut507
  Tool = -> Box516
FEATURE [Part::Cylinder] Cylinder1471  label="Válec1471"
  Angle = 360
  AttacherType = Attacher::AttachEngine3D
  Height = 32
  Placement = pos=(26,41,-42) rot=(0,0,1;0rad)
  Radius = 1.5
FEATURE [Part::Cylinder] Cylinder1472  label="Válec1472"
  Angle = 360
  AttacherType = Attacher::AttachEngine3D
  Height = 32
  Placement = pos=(78,41,-42) rot=(0,0,1;0rad)
  Radius = 1.5
FEATURE [Part::Compound] Compound887
  Links = -> [Cylinder1471,Cylinder1472]
FEATURE [Part::Cylinder] Cylinder1473  label="Válec1473"
  Angle = 360
  AttacherType = Attacher::AttachEngine3D
  Height = 100
  Placement = pos=(90,0,-60) rot=(0,0,1;0rad)
  Radius = 1.5
FEATURE [Part::Cylinder] Cylinder1474  label="Válec1474"
  Angle = 360
  AttacherType = Attacher::AttachEngine3D
  Height = 100
  Placement = pos=(14,0,-60) rot=(0,0,1;0rad)
  Radius = 1.5
FEATURE [Part::Compound] Compound888  label="srouby_troj003"
  Links = -> [Cylinder1473,Cylinder1474]
FEATURE [Part::Cut] Cut
  Base = -> Cut508
  Tool = -> Compound887
FEATURE [Part::Cut] Cut509
  Base = -> Cut
  Tool = -> Compound888
FEATURE [Part::Compound] Compound  label="Base_deep-neck"
  Links = -> [Chamfer039,Cut308,Cut509]
FEATURE [Mesh::Feature] Mesh  label="Base_deep-neck (Meshed)"
FEATURE [Part::Cylinder] Cylinder1231  label="Válec1231"
  Angle = 360
  AttacherType = Attacher::AttachEngine3D
  Height = 100
  Placement = pos=(14,0,-18) rot=(0,0,1;0rad)
  Radius = 4
FEATURE [Part::Compound] Compound622  label="srouby_troj_silne"
  Links = -> [Cylinder1230,Cylinder1231]
FEATURE [Part::Cut] Cut293
  Base = -> Cut292
  Tool = -> Compound622
FEATURE [Part::Compound] Compound662  label="Base_neck-foreshift-damaged"
  Links = -> [Cut291,Cut294]
FEATURE [Sketcher::SketchObject] Sketch005
  FullyConstrained = false
  sketch-geometry (1):
    g0: Circle CenterX=-186.411 CenterY=73.9277 CenterZ=0 NormalX=0 NormalY=0 NormalZ=1 AngleXU=0 Radius=59
FEATURE [Part::Cylinder] Cylinder1475  label="Válec1475"
  Angle = 360
  AttacherType = Attacher::AttachEngine3D
  Height = 100
  Placement = pos=(103,-12,-60) rot=(0,0,1;0rad)
  Radius = 1.5
FEATURE [Part::Cylinder] Cylinder1476  label="Válec1476"
  Angle = 360
  AttacherType = Attacher::AttachEngine3D
  Height = 100
  Placement = pos=(103,6,-60) rot=(0,0,1;0rad)
  Radius = 1.5
FEATURE [Part::Cylinder] Cylinder1477  label="Válec1477"
  Angle = 360
  AttacherType = Attacher::AttachEngine3D
  Height = 100
  Placement = pos=(76,18,-60) rot=(0,0,1;0rad)
  Radius = 1.5
FEATURE [Part::Cylinder] Cylinder1478  label="Válec1478"
  Angle = 360
  AttacherType = Attacher::AttachEngine3D
  Height = 100
  Placement = pos=(91,-21,-60) rot=(0,0,1;0rad)
  Radius = 1.5
FEATURE [Part::Cylinder] Cylinder1479  label="Válec1479"
  Angle = 360
  AttacherType = Attacher::AttachEngine3D
  Height = 100
  Placement = pos=(13,-21,-60) rot=(0,0,1;0rad)
  Radius = 1.5
FEATURE [Part::Cylinder] Cylinder1480  label="Válec1480"
  Angle = 360
  AttacherType = Attacher::AttachEngine3D
  Height = 100
  Placement = pos=(28,18,-60) rot=(0,0,1;0rad)
  Radius = 1.5
FEATURE [Part::Cylinder] Cylinder1481  label="Válec1481"
  Angle = 360
  AttacherType = Attacher::AttachEngine3D
  Height = 100
  Placement = pos=(1,-12,-60) rot=(0,0,1;0rad)
  Radius = 1.5
FEATURE [Part::Cylinder] Cylinder1482  label="Válec1482"
  Angle = 360
  AttacherType = Attacher::AttachEngine3D
  Height = 100
  Placement = pos=(1,6,-60) rot=(0,0,1;0rad)
  Radius = 1.5
FEATURE [Part::Cylinder] Cylinder1483  label="Válec1483"
  Angle = 360
  AttacherType = Attacher::AttachEngine3D
  Height = 100
  Placement = pos=(-50,0,-60) rot=(0,0,1;0rad)
  Radius = 1.5
FEATURE [Part::Cylinder] Cylinder1484  label="Válec1484"
  Angle = 360
  AttacherType = Attacher::AttachEngine3D
  Height = 100
  Placement = pos=(-36,34,-60) rot=(0,0,1;0rad)
  Radius = 1.5
FEATURE [Part::Cylinder] Cylinder1485  label="Válec1485"
  Angle = 360
  AttacherType = Attacher::AttachEngine3D
  Height = 100
  Placement = pos=(-36,-34,-60) rot=(0,0,1;0rad)
  Radius = 1.5
FEATURE [Part::Extrusion] Extrude003
  Base = -> Sketch005
  Dir = (52,0,32)
  DirMode = 0
  FaceMakerClass = Part::FaceMakerBullseye
  LengthFwd = 61
  LengthRev = 0
  Placement = pos=(-134,74,-22) rot=(0,0,1;3.14159rad)
  Solid = true
  Symmetric = false
FEATURE [Part::Compound] Compound891  label="srouby_monoblok004"
  Links = -> [Cylinder1475,Cylinder1476,Cylinder1477,Cylinder1478,Cylinder1479,Cylinder1480,Cylinder1481,Cylinder1482]
FEATURE [Part::Cut] Cut510
  Base = -> Extrude003
  Tool = -> Compound891
FEATURE [Part::Cylinder] Cylinder1486  label="Válec1486"
  Angle = 360
  AttacherType = Attacher::AttachEngine3D
  Height = 100
  Placement = pos=(50,0,-60) rot=(0,0,1;0rad)
  Radius = 1.5
FEATURE [Part::Cylinder] Cylinder1487  label="Válec1487"
  Angle = 360
  AttacherType = Attacher::AttachEngine3D
  Height = 100
  Placement = pos=(36,34,-60) rot=(0,0,1;0rad)
  Radius = 1.5
FEATURE [Part::Cylinder] Cylinder1488  label="Válec1488"
  Angle = 360
  AttacherType = Attacher::AttachEngine3D
  Height = 100
  Placement = pos=(36,-34,-60) rot=(0,0,1;0rad)
  Radius = 1.5
FEATURE [Part::Compound] Compound892  label="sbouby_baze004"
  Links = -> [Cylinder1483,Cylinder1484,Cylinder1485,Cylinder1486,Cylinder1487,Cylinder1488]
FEATURE [Part::Cylinder] Cylinder1489  label="Válec1489"
  Angle = 360
  AttacherType = Attacher::AttachEngine3D
  Height = 16
  Placement = pos=(0,0,2) rot=(0,0,1;0rad)
  Radius = 59
FEATURE [Part::Cylinder] Cylinder1490  label="Válec1490"
  Angle = 360
  AttacherType = Attacher::AttachEngine3D
  Height = 4
  Placement = pos=(52,0,-26) rot=(0,0,1;0rad)
  Radius = 59
FEATURE [Part::Cylinder] Cylinder1491  label="Válec1491"
  Angle = 360
  AttacherType = Attacher::AttachEngine3D
  Height = 100
  Placement = pos=(103,-12,-60) rot=(0,0,1;0rad)
  Radius = 1.5
FEATURE [Part::Cylinder] Cylinder1492  label="Válec1492"
  Angle = 360
  AttacherType = Attacher::AttachEngine3D
  Height = 100
  Placement = pos=(103,6,-60) rot=(0,0,1;0rad)
  Radius = 1.5
FEATURE [Part::Cylinder] Cylinder1493  label="Válec1493"
  Angle = 360
  AttacherType = Attacher::AttachEngine3D
  Height = 100
  Placement = pos=(76,18,-60) rot=(0,0,1;0rad)
  Radius = 1.5
FEATURE [Part::Cylinder] Cylinder1494  label="Válec1494"
  Angle = 360
  AttacherType = Attacher::AttachEngine3D
  Height = 100
  Placement = pos=(91,-21,-60) rot=(0,0,1;0rad)
  Radius = 1.5
FEATURE [Part::Cylinder] Cylinder1495  label="Válec1495"
  Angle = 360
  AttacherType = Attacher::AttachEngine3D
  Height = 100
  Placement = pos=(13,-21,-60) rot=(0,0,1;0rad)
  Radius = 1.5
FEATURE [Part::Cylinder] Cylinder1496  label="Válec1496"
  Angle = 360
  AttacherType = Attacher::AttachEngine3D
  Height = 100
  Placement = pos=(28,18,-60) rot=(0,0,1;0rad)
  Radius = 1.5
FEATURE [Part::Cylinder] Cylinder1497  label="Válec1497"
  Angle = 360
  AttacherType = Attacher::AttachEngine3D
  Height = 100
  Placement = pos=(1,-12,-60) rot=(0,0,1;0rad)
  Radius = 1.5
FEATURE [Part::Cylinder] Cylinder1498  label="Válec1498"
  Angle = 360
  AttacherType = Attacher::AttachEngine3D
  Height = 100
  Placement = pos=(1,6,-60) rot=(0,0,1;0rad)
  Radius = 1.5
FEATURE [Part::Compound] Compound893  label="srouby_monoblok005"
  Links = -> [Cylinder1491,Cylinder1492,Cylinder1493,Cylinder1494,Cylinder1495,Cylinder1496,Cylinder1497,Cylinder1498]
FEATURE [Part::Cut] Cut513
  Base = -> Cylinder1490
  Tool = -> Compound893
FEATURE [Part::Cylinder] Cylinder1499  label="Válec1499"
  Angle = 360
  AttacherType = Attacher::AttachEngine3D
  Height = 20
  Placement = pos=(103,-12,-20) rot=(0,0,1;0rad)
  Radius = 4
FEATURE [Part::Cylinder] Cylinder1500  label="Válec1500"
  Angle = 360
  AttacherType = Attacher::AttachEngine3D
  Height = 20
  Placement = pos=(103,6,-20) rot=(0,0,1;0rad)
  Radius = 4
FEATURE [Part::Cylinder] Cylinder1501  label="Válec1501"
  Angle = 360
  AttacherType = Attacher::AttachEngine3D
  Height = 20
  Placement = pos=(76,18,-18) rot=(0,0,1;0rad)
  Radius = 4
FEATURE [Part::Cylinder] Cylinder1502  label="Válec1502"
  Angle = 360
  AttacherType = Attacher::AttachEngine3D
  Height = 20
  Placement = pos=(91,-21,-18) rot=(0,0,1;0rad)
  Radius = 4
FEATURE [Part::Cylinder] Cylinder1503  label="Válec1503"
  Angle = 360
  AttacherType = Attacher::AttachEngine3D
  Height = 40
  Placement = pos=(13,-21,-18) rot=(0,0,1;0rad)
  Radius = 4
FEATURE [Part::Cylinder] Cylinder1504  label="Válec1504"
  Angle = 360
  AttacherType = Attacher::AttachEngine3D
  Height = 40
  Placement = pos=(28,18,-18) rot=(0,0,1;0rad)
  Radius = 4
FEATURE [Part::Cylinder] Cylinder1505  label="Válec1505"
  Angle = 360
  AttacherType = Attacher::AttachEngine3D
  Height = 40
  Placement = pos=(1,-12,-18) rot=(0,0,1;0rad)
  Radius = 4
FEATURE [Part::Cylinder] Cylinder1506  label="Válec1506"
  Angle = 360
  AttacherType = Attacher::AttachEngine3D
  Height = 40
  Placement = pos=(1,6,-18) rot=(0,0,1;0rad)
  Radius = 4
FEATURE [Part::Compound] Compound894  label="srouby_monoblok_silne005"
  Links = -> [Cylinder1499,Cylinder1500,Cylinder1501,Cylinder1502,Cylinder1503,Cylinder1504,Cylinder1505,Cylinder1506]
FEATURE [Part::Cut] Cut511
  Base = -> Cut510
  Tool = -> Compound894
FEATURE [Part::Cylinder] Cylinder1507  label="Válec1507"
  Angle = 360
  AttacherType = Attacher::AttachEngine3D
  Height = 20
  Placement = pos=(103,-12,-20) rot=(0,0,1;0rad)
  Radius = 4
FEATURE [Part::Cylinder] Cylinder1508  label="Válec1508"
  Angle = 360
  AttacherType = Attacher::AttachEngine3D
  Height = 20
  Placement = pos=(103,6,-20) rot=(0,0,1;0rad)
  Radius = 4
FEATURE [Part::Cylinder] Cylinder1509  label="Válec1509"
  Angle = 360
  AttacherType = Attacher::AttachEngine3D
  Height = 20
  Placement = pos=(76,18,-18) rot=(0,0,1;0rad)
  Radius = 4
FEATURE [Part::Cylinder] Cylinder1510  label="Válec1510"
  Angle = 360
  AttacherType = Attacher::AttachEngine3D
  Height = 20
  Placement = pos=(91,-21,-18) rot=(0,0,1;0rad)
  Radius = 4
FEATURE [Part::Cylinder] Cylinder1511  label="Válec1511"
  Angle = 360
  AttacherType = Attacher::AttachEngine3D
  Height = 40
  Placement = pos=(13,-21,-18) rot=(0,0,1;0rad)
  Radius = 4
FEATURE [Part::Cylinder] Cylinder1512  label="Válec1512"
  Angle = 360
  AttacherType = Attacher::AttachEngine3D
  Height = 40
  Placement = pos=(28,18,-18) rot=(0,0,1;0rad)
  Radius = 4
FEATURE [Part::Cylinder] Cylinder1513  label="Válec1513"
  Angle = 360
  AttacherType = Attacher::AttachEngine3D
  Height = 40
  Placement = pos=(1,-12,-18) rot=(0,0,1;0rad)
  Radius = 4
FEATURE [Part::Cylinder] Cylinder1514  label="Válec1514"
  Angle = 360
  AttacherType = Attacher::AttachEngine3D
  Height = 40
  Placement = pos=(1,6,-18) rot=(0,0,1;0rad)
  Radius = 4
FEATURE [Part::Compound] Compound895  label="srouby_monoblok_silne006"
  Links = -> [Cylinder1507,Cylinder1508,Cylinder1509,Cylinder1510,Cylinder1511,Cylinder1512,Cylinder1513,Cylinder1514]
FEATURE [Part::Cut] Cut512
  Base = -> Cylinder1489
  Tool = -> Compound895
FEATURE [Part::Cylinder] Cylinder1125  label="Válec1125"
  Angle = 360
  AttacherType = Attacher::AttachEngine3D
  Height = 100
  Placement = pos=(36,34,-90) rot=(0,0,1;0rad)
  Radius = 4
FEATURE [Part::Cylinder] Cylinder1126  label="Válec1126"
  Angle = 360
  AttacherType = Attacher::AttachEngine3D
  Height = 100
  Placement = pos=(-50,0,-90) rot=(0,0,1;0rad)
  Radius = 4
FEATURE [Part::Cylinder] Cylinder1127  label="Válec1127"
  Angle = 360
  AttacherType = Attacher::AttachEngine3D
  Height = 100
  Placement = pos=(-36,34,-90) rot=(0,0,1;0rad)
  Radius = 4
FEATURE [Part::Cylinder] Cylinder1128  label="Válec1128"
  Angle = 360
  AttacherType = Attacher::AttachEngine3D
  Height = 100
  Placement = pos=(-36,-34,-90) rot=(0,0,1;0rad)
  Radius = 4
FEATURE [Part::Cylinder] Cylinder1129  label="Válec1129"
  Angle = 360
  AttacherType = Attacher::AttachEngine3D
  Height = 100
  Placement = pos=(50,0,-90) rot=(0,0,1;0rad)
  Radius = 4
FEATURE [Part::Cylinder] Cylinder1130  label="Válec1130"
  Angle = 360
  AttacherType = Attacher::AttachEngine3D
  Height = 100
  Placement = pos=(36,-34,-90) rot=(0,0,1;0rad)
  Radius = 4
FEATURE [Part::Compound] Compound896  label="sbouby_baze_silne006"
  Links = -> [Cylinder1126,Cylinder1127,Cylinder1128,Cylinder1129,Cylinder1125,Cylinder1130]
FEATURE [Part::Cut] Cut514
  Base = -> Cut513
  Tool = -> Compound896
FEATURE [Part::Cylinder] Cylinder1131  label="Válec1131"
  Angle = 360
  AttacherType = Attacher::AttachEngine3D
  Height = 100
  Placement = pos=(36,34,-90) rot=(0,0,1;0rad)
  Radius = 4
FEATURE [Part::Cylinder] Cylinder1132  label="Válec1132"
  Angle = 360
  AttacherType = Attacher::AttachEngine3D
  Height = 100
  Placement = pos=(-50,0,-90) rot=(0,0,1;0rad)
  Radius = 4
FEATURE [Part::Cylinder] Cylinder1133  label="Válec1133"
  Angle = 360
  AttacherType = Attacher::AttachEngine3D
  Height = 100
  Placement = pos=(-36,34,-90) rot=(0,0,1;0rad)
  Radius = 4
FEATURE [Part::Cylinder] Cylinder1134  label="Válec1134"
  Angle = 360
  AttacherType = Attacher::AttachEngine3D
  Height = 100
  Placement = pos=(-36,-34,-90) rot=(0,0,1;0rad)
  Radius = 4
FEATURE [Part::Cylinder] Cylinder1135  label="Válec1135"
  Angle = 360
  AttacherType = Attacher::AttachEngine3D
  Height = 100
  Placement = pos=(50,0,-90) rot=(0,0,1;0rad)
  Radius = 4
FEATURE [Part::Cylinder] Cylinder1136  label="Válec1136"
  Angle = 360
  AttacherType = Attacher::AttachEngine3D
  Height = 100
  Placement = pos=(36,-34,-90) rot=(0,0,1;0rad)
  Radius = 4
FEATURE [Part::Compound] Compound897  label="sbouby_baze_silne007"
  Links = -> [Cylinder1132,Cylinder1133,Cylinder1134,Cylinder1135,Cylinder1131,Cylinder1136]
FEATURE [Part::Cut] Cut516
  Base = -> Cut512
  Tool = -> Compound897
FEATURE [Part::Cut] Cut518
  Base = -> Cut516
  Tool = -> Compound892
FEATURE [Part::Cylinder] Cylinder1515  label="Válec1515"
  Angle = 360
  AttacherType = Attacher::AttachEngine3D
  Height = 100
  Placement = pos=(36,34,-90) rot=(0,0,1;0rad)
  Radius = 4
FEATURE [Part::Cylinder] Cylinder1516  label="Válec1516"
  Angle = 360
  AttacherType = Attacher::AttachEngine3D
  Height = 100
  Placement = pos=(-50,0,-90) rot=(0,0,1;0rad)
  Radius = 4
FEATURE [Part::Cylinder] Cylinder1517  label="Válec1517"
  Angle = 360
  AttacherType = Attacher::AttachEngine3D
  Height = 100
  Placement = pos=(-36,34,-90) rot=(0,0,1;0rad)
  Radius = 4
FEATURE [Part::Cylinder] Cylinder1518  label="Válec1518"
  Angle = 360
  AttacherType = Attacher::AttachEngine3D
  Height = 100
  Placement = pos=(-36,-34,-90) rot=(0,0,1;0rad)
  Radius = 4
FEATURE [Part::Cylinder] Cylinder1519  label="Válec1519"
  Angle = 360
  AttacherType = Attacher::AttachEngine3D
  Height = 100
  Placement = pos=(50,0,-90) rot=(0,0,1;0rad)
  Radius = 4
FEATURE [Part::Cylinder] Cylinder1520  label="Válec1520"
  Angle = 360
  AttacherType = Attacher::AttachEngine3D
  Height = 100
  Placement = pos=(36,-34,-90) rot=(0,0,1;0rad)
  Radius = 4
FEATURE [Part::Compound] Compound898  label="sbouby_baze_silne008"
  Links = -> [Cylinder1516,Cylinder1517,Cylinder1518,Cylinder1519,Cylinder1515,Cylinder1520]
FEATURE [Part::Cut] Cut515
  Base = -> Cut511
  Tool = -> Compound898
FEATURE [Part::Cylinder] Cylinder1521  label="Válec1521"
  Angle = 360
  AttacherType = Attacher::AttachEngine3D
  Height = 100
  Placement = pos=(36,34,-60) rot=(0,0,1;0rad)
  Radius = 1.5
FEATURE [Part::Cylinder] Cylinder1522  label="Válec1522"
  Angle = 360
  AttacherType = Attacher::AttachEngine3D
  Height = 100
  Placement = pos=(-50,0,-60) rot=(0,0,1;0rad)
  Radius = 1.5
FEATURE [Part::Cylinder] Cylinder1523  label="Válec1523"
  Angle = 360
  AttacherType = Attacher::AttachEngine3D
  Height = 100
  Placement = pos=(-36,34,-60) rot=(0,0,1;0rad)
  Radius = 1.5
FEATURE [Part::Cylinder] Cylinder1524  label="Válec1524"
  Angle = 360
  AttacherType = Attacher::AttachEngine3D
  Height = 100
  Placement = pos=(-36,-34,-60) rot=(0,0,1;0rad)
  Radius = 1.5
FEATURE [Part::Cylinder] Cylinder1525  label="Válec1525"
  Angle = 360
  AttacherType = Attacher::AttachEngine3D
  Height = 100
  Placement = pos=(50,0,-60) rot=(0,0,1;0rad)
  Radius = 1.5
FEATURE [Part::Cylinder] Cylinder1526  label="Válec1526"
  Angle = 360
  AttacherType = Attacher::AttachEngine3D
  Height = 100
  Placement = pos=(36,-34,-60) rot=(0,0,1;0rad)
  Radius = 1.5
FEATURE [Part::Compound] Compound899  label="sbouby_baze005"
  Links = -> [Cylinder1522,Cylinder1523,Cylinder1524,Cylinder1525,Cylinder1521,Cylinder1526]
FEATURE [Part::Cut] Cut517
  Base = -> Cut515
  Tool = -> Compound899
FEATURE [Part::Box] Box517  label="Krychle517"
  AttacherType = Attacher::AttachEngine3D
  Height = 100
  Length = 200
  Placement = pos=(-60,-130,-90) rot=(0,0,1;0rad)
  Width = 100
FEATURE [Part::Cut] Cut519
  Base = -> Cut517
  Tool = -> Box517
FEATURE [Part::Box] Box518  label="Krychle518"
  AttacherType = Attacher::AttachEngine3D
  Height = 100
  Length = 200
  Placement = pos=(-60,-124,-90) rot=(0,0,1;0rad)
  Width = 100
FEATURE [Part::Cut] Cut520
  Base = -> Cut514
  Tool = -> Box518
FEATURE [Part::Box] Box519  label="Krychle519"
  AttacherType = Attacher::AttachEngine3D
  Height = 100
  Length = 200
  Placement = pos=(-60,44,-90) rot=(0,0,1;0rad)
  Width = 100
FEATURE [Part::Cut] Cut521
  Base = -> Cut519
  Tool = -> Box519
FEATURE [Part::Box] Box520  label="Krychle520"
  AttacherType = Attacher::AttachEngine3D
  Height = 100
  Length = 200
  Placement = pos=(-60,44,-90) rot=(0,0,1;0rad)
  Width = 100
FEATURE [Part::Cut] Cut522
  Base = -> Cut520
  Tool = -> Box520
FEATURE [Part::Cylinder] Cylinder1527  label="Válec1527"
  Angle = 360
  AttacherType = Attacher::AttachEngine3D
  Height = 100
  Placement = pos=(90,0,-60) rot=(0,0,1;0rad)
  Radius = 1.5
FEATURE [Part::Cylinder] Cylinder1528  label="Válec1528"
  Angle = 360
  AttacherType = Attacher::AttachEngine3D
  Height = 100
  Placement = pos=(14,0,-60) rot=(0,0,1;0rad)
  Radius = 1.5
FEATURE [Part::Cylinder] Cylinder1529  label="Válec1529"
  Angle = 360
  AttacherType = Attacher::AttachEngine3D
  Height = 100
  Placement = pos=(90,0,-18) rot=(0,0,1;0rad)
  Radius = 4
FEATURE [Part::Chamfer] Chamfer040
  Base = -> Cut518
  Edges = 1 edges r=4: [Edge3]
FEATURE [Part::Cylinder] Cylinder1530  label="Válec1530"
  Angle = 360
  AttacherType = Attacher::AttachEngine3D
  Height = 100
  Placement = pos=(14,0,-18) rot=(0,0,1;0rad)
  Radius = 4
FEATURE [Part::Box] Box521  label="Krychle521"
  AttacherType = Attacher::AttachEngine3D
  Height = 2
  Length = 6
  Placement = pos=(75,38,-22) rot=(0,0,1;0rad)
  Width = 6
FEATURE [Part::Box] Box522  label="Krychle522"
  AttacherType = Attacher::AttachEngine3D
  Height = 2
  Length = 6
  Placement = pos=(23,38,-22) rot=(0,0,1;0rad)
  Width = 6
FEATURE [Part::Cylinder] Cylinder1531  label="Válec1531"
  Angle = 360
  AttacherType = Attacher::AttachEngine3D
  Height = 32
  Placement = pos=(26,41,-42) rot=(0,0,1;0rad)
  Radius = 1.5
FEATURE [Part::Compound] Compound900
  Links = -> [Box521,Box522]
FEATURE [Part::Cut] Cut524
  Base = -> Cut521
  Tool = -> Compound900
FEATURE [Part::Compound] Compound903  label="srouby_troj_silne004"
  Links = -> [Cylinder1529,Cylinder1530]
FEATURE [Part::Compound] Compound904  label="srouby_troj005"
  Links = -> [Cylinder1527,Cylinder1528]
FEATURE [Part::Cylinder] Cylinder1532  label="Válec1532"
  Angle = 360
  AttacherType = Attacher::AttachEngine3D
  Height = 32
  Placement = pos=(78,41,-42) rot=(0,0,1;0rad)
  Radius = 1.5
FEATURE [Part::Compound] Compound901
  Links = -> [Cylinder1531,Cylinder1532]
FEATURE [Part::Cut] Cut523
  Base = -> Cut522
  Tool = -> Compound901
FEATURE [Part::Cylinder] Cylinder1533  label="Válec1533"
  Angle = 360
  AttacherType = Attacher::AttachEngine3D
  Height = 32
  Placement = pos=(26,41,-46) rot=(0,0,1;0rad)
  Radius = 1.5
FEATURE [Part::Cylinder] Cylinder1534  label="Válec1534"
  Angle = 360
  AttacherType = Attacher::AttachEngine3D
  Height = 32
  Placement = pos=(78,41,-46) rot=(0,0,1;0rad)
  Radius = 1.5
FEATURE [Part::Compound] Compound902
  Links = -> [Cylinder1533,Cylinder1534]
FEATURE [Part::Cut] Cut525
  Base = -> Cut524
  Tool = -> Compound902
FEATURE [Part::Cut] Cut527
  Base = -> Cut525
  Tool = -> Compound904
FEATURE [Part::Cut] Cut528
  Base = -> Cut527
  Tool = -> Compound903
FEATURE [Part::Chamfer] Chamfer041
  Base = -> Cut528
  Edges = 2 edges r=6: [Edge40,Edge42]
FEATURE [Part::Cylinder] Cylinder1535  label="Válec1535"
  Angle = 360
  AttacherType = Attacher::AttachEngine3D
  Height = 100
  Placement = pos=(90,0,-18) rot=(0,0,1;0rad)
  Radius = 4
FEATURE [Part::Cylinder] Cylinder1536  label="Válec1536"
  Angle = 360
  AttacherType = Attacher::AttachEngine3D
  Height = 100
  Placement = pos=(14,0,-18) rot=(0,0,1;0rad)
  Radius = 4
FEATURE [Part::Compound] Compound905  label="srouby_troj_silne005"
  Links = -> [Cylinder1535,Cylinder1536]
FEATURE [Part::Cut] Cut529
  Base = -> Chamfer040
  Placement = pos=(0,0,4) rot=(0,0,1;0rad)
  Tool = -> Compound905
FEATURE [Part::Cylinder] Cylinder1537  label="Válec1537"
  Angle = 360
  AttacherType = Attacher::AttachEngine3D
  Height = 100
  Placement = pos=(90,0,-60) rot=(0,0,1;0rad)
  Radius = 1.5
FEATURE [Part::Cylinder] Cylinder1538  label="Válec1538"
  Angle = 360
  AttacherType = Attacher::AttachEngine3D
  Height = 100
  Placement = pos=(14,0,-60) rot=(0,0,1;0rad)
  Radius = 1.5
FEATURE [Part::Compound] Compound889  label="srouby_troj004"
  Links = -> [Cylinder1537,Cylinder1538]
FEATURE [Part::Cut] Cut526
  Base = -> Cut523
  Tool = -> Compound889
FEATURE [Part::Compound] Compound890  label="Base_neck-foreshift"
  Links = -> [Cut526,Cut529,Chamfer041]
FEATURE [Sketcher::SketchObject] Sketch006
  FullyConstrained = false
  sketch-geometry (1):
    g0: Circle CenterX=-186.411 CenterY=73.9277 CenterZ=0 NormalX=0 NormalY=0 NormalZ=1 AngleXU=0 Radius=59
FEATURE [Part::Extrusion] Extrude004
  Base = -> Sketch006
  Dir = (52,0,32)
  DirMode = 0
  FaceMakerClass = Part::FaceMakerBullseye
  LengthFwd = 61
  LengthRev = 0
  Placement = pos=(-134,74,-22) rot=(0,0,1;3.14159rad)
  Solid = true
  Symmetric = false
FEATURE [Part::Cylinder] Cylinder1539  label="Válec1539"
  Angle = 360
  AttacherType = Attacher::AttachEngine3D
  Height = 100
  Placement = pos=(103,-12,-60) rot=(0,0,1;0rad)
  Radius = 1.5
FEATURE [Part::Cylinder] Cylinder1540  label="Válec1540"
  Angle = 360
  AttacherType = Attacher::AttachEngine3D
  Height = 100
  Placement = pos=(103,6,-60) rot=(0,0,1;0rad)
  Radius = 1.5
FEATURE [Part::Cylinder] Cylinder1541  label="Válec1541"
  Angle = 360
  AttacherType = Attacher::AttachEngine3D
  Height = 100
  Placement = pos=(76,18,-60) rot=(0,0,1;0rad)
  Radius = 1.5
FEATURE [Part::Cylinder] Cylinder1542  label="Válec1542"
  Angle = 360
  AttacherType = Attacher::AttachEngine3D
  Height = 100
  Placement = pos=(91,-21,-60) rot=(0,0,1;0rad)
  Radius = 1.5
FEATURE [Part::Cylinder] Cylinder1543  label="Válec1543"
  Angle = 360
  AttacherType = Attacher::AttachEngine3D
  Height = 100
  Placement = pos=(13,-21,-60) rot=(0,0,1;0rad)
  Radius = 1.5
FEATURE [Part::Cylinder] Cylinder1544  label="Válec1544"
  Angle = 360
  AttacherType = Attacher::AttachEngine3D
  Height = 100
  Placement = pos=(28,18,-60) rot=(0,0,1;0rad)
  Radius = 1.5
FEATURE [Part::Cylinder] Cylinder1545  label="Válec1545"
  Angle = 360
  AttacherType = Attacher::AttachEngine3D
  Height = 100
  Placement = pos=(1,-12,-60) rot=(0,0,1;0rad)
  Radius = 1.5
FEATURE [Part::Cylinder] Cylinder1546  label="Válec1546"
  Angle = 360
  AttacherType = Attacher::AttachEngine3D
  Height = 100
  Placement = pos=(1,6,-60) rot=(0,0,1;0rad)
  Radius = 1.5
FEATURE [Part::Compound] Compound906  label="srouby_monoblok006"
  Links = -> [Cylinder1539,Cylinder1540,Cylinder1541,Cylinder1542,Cylinder1543,Cylinder1544,Cylinder1545,Cylinder1546]
FEATURE [Part::Cut] Cut530
  Base = -> Extrude004
  Tool = -> Compound906
FEATURE [Part::Cylinder] Cylinder1547  label="Válec1547"
  Angle = 360
  AttacherType = Attacher::AttachEngine3D
  Height = 20
  Placement = pos=(103,-12,-20) rot=(0,0,1;0rad)
  Radius = 4
FEATURE [Part::Cylinder] Cylinder1548  label="Válec1548"
  Angle = 360
  AttacherType = Attacher::AttachEngine3D
  Height = 20
  Placement = pos=(103,6,-20) rot=(0,0,1;0rad)
  Radius = 4
FEATURE [Part::Cylinder] Cylinder1549  label="Válec1549"
  Angle = 360
  AttacherType = Attacher::AttachEngine3D
  Height = 20
  Placement = pos=(76,18,-18) rot=(0,0,1;0rad)
  Radius = 4
FEATURE [Part::Cylinder] Cylinder1550  label="Válec1550"
  Angle = 360
  AttacherType = Attacher::AttachEngine3D
  Height = 20
  Placement = pos=(91,-21,-18) rot=(0,0,1;0rad)
  Radius = 4
FEATURE [Part::Cylinder] Cylinder1551  label="Válec1551"
  Angle = 360
  AttacherType = Attacher::AttachEngine3D
  Height = 40
  Placement = pos=(13,-21,-18) rot=(0,0,1;0rad)
  Radius = 4
FEATURE [Part::Cylinder] Cylinder1552  label="Válec1552"
  Angle = 360
  AttacherType = Attacher::AttachEngine3D
  Height = 40
  Placement = pos=(28,18,-18) rot=(0,0,1;0rad)
  Radius = 4
FEATURE [Part::Cylinder] Cylinder1553  label="Válec1553"
  Angle = 360
  AttacherType = Attacher::AttachEngine3D
  Height = 40
  Placement = pos=(1,-12,-18) rot=(0,0,1;0rad)
  Radius = 4
FEATURE [Part::Cylinder] Cylinder1554  label="Válec1554"
  Angle = 360
  AttacherType = Attacher::AttachEngine3D
  Height = 40
  Placement = pos=(1,6,-18) rot=(0,0,1;0rad)
  Radius = 4
FEATURE [Part::Compound] Compound907  label="srouby_monoblok_silne007"
  Links = -> [Cylinder1547,Cylinder1548,Cylinder1549,Cylinder1550,Cylinder1551,Cylinder1552,Cylinder1553,Cylinder1554]
FEATURE [Part::Cut] Cut531
  Base = -> Cut530
  Tool = -> Compound907
FEATURE [Part::Cylinder] Cylinder1555  label="Válec1555"
  Angle = 360
  AttacherType = Attacher::AttachEngine3D
  Height = 100
  Placement = pos=(36,34,-90) rot=(0,0,1;0rad)
  Radius = 4
FEATURE [Part::Cylinder] Cylinder1556  label="Válec1556"
  Angle = 360
  AttacherType = Attacher::AttachEngine3D
  Height = 100
  Placement = pos=(-50,0,-90) rot=(0,0,1;0rad)
  Radius = 4
FEATURE [Part::Cylinder] Cylinder1557  label="Válec1557"
  Angle = 360
  AttacherType = Attacher::AttachEngine3D
  Height = 100
  Placement = pos=(-36,34,-90) rot=(0,0,1;0rad)
  Radius = 4
FEATURE [Part::Cylinder] Cylinder1558  label="Válec1558"
  Angle = 360
  AttacherType = Attacher::AttachEngine3D
  Height = 100
  Placement = pos=(-36,-34,-90) rot=(0,0,1;0rad)
  Radius = 4
FEATURE [Part::Cylinder] Cylinder1559  label="Válec1559"
  Angle = 360
  AttacherType = Attacher::AttachEngine3D
  Height = 100
  Placement = pos=(50,0,-90) rot=(0,0,1;0rad)
  Radius = 4
FEATURE [Part::Cylinder] Cylinder1560  label="Válec1560"
  Angle = 360
  AttacherType = Attacher::AttachEngine3D
  Height = 100
  Placement = pos=(36,-34,-90) rot=(0,0,1;0rad)
  Radius = 4
FEATURE [Part::Compound] Compound908  label="sbouby_baze_silne009"
  Links = -> [Cylinder1556,Cylinder1557,Cylinder1558,Cylinder1559,Cylinder1555,Cylinder1560]
FEATURE [Part::Cut] Cut532
  Base = -> Cut531
  Tool = -> Compound908
FEATURE [Part::Cylinder] Cylinder1561  label="Válec1561"
  Angle = 360
  AttacherType = Attacher::AttachEngine3D
  Height = 100
  Placement = pos=(36,34,-60) rot=(0,0,1;0rad)
  Radius = 1.5
FEATURE [Part::Cylinder] Cylinder1562  label="Válec1562"
  Angle = 360
  AttacherType = Attacher::AttachEngine3D
  Height = 100
  Placement = pos=(-50,0,-60) rot=(0,0,1;0rad)
  Radius = 1.5
FEATURE [Part::Cylinder] Cylinder1563  label="Válec1563"
  Angle = 360
  AttacherType = Attacher::AttachEngine3D
  Height = 100
  Placement = pos=(-36,34,-60) rot=(0,0,1;0rad)
  Radius = 1.5
FEATURE [Part::Cylinder] Cylinder1564  label="Válec1564"
  Angle = 360
  AttacherType = Attacher::AttachEngine3D
  Height = 100
  Placement = pos=(-36,-34,-60) rot=(0,0,1;0rad)
  Radius = 1.5
FEATURE [Part::Cylinder] Cylinder1565  label="Válec1565"
  Angle = 360
  AttacherType = Attacher::AttachEngine3D
  Height = 100
  Placement = pos=(50,0,-60) rot=(0,0,1;0rad)
  Radius = 1.5
FEATURE [Part::Cylinder] Cylinder1566  label="Válec1566"
  Angle = 360
  AttacherType = Attacher::AttachEngine3D
  Height = 100
  Placement = pos=(36,-34,-60) rot=(0,0,1;0rad)
  Radius = 1.5
FEATURE [Part::Compound] Compound909  label="sbouby_baze006"
  Links = -> [Cylinder1562,Cylinder1563,Cylinder1564,Cylinder1565,Cylinder1561,Cylinder1566]
FEATURE [Part::Cut] Cut533
  Base = -> Cut532
  Tool = -> Compound909
FEATURE [Part::Box] Box523  label="Krychle523"
  AttacherType = Attacher::AttachEngine3D
  Height = 100
  Length = 200
  Placement = pos=(-60,-130,-90) rot=(0,0,1;0rad)
  Width = 100
FEATURE [Part::Cut] Cut534
  Base = -> Cut533
  Tool = -> Box523
FEATURE [Part::Box] Box524  label="Krychle524"
  AttacherType = Attacher::AttachEngine3D
  Height = 100
  Length = 200
  Placement = pos=(-60,44,-90) rot=(0,0,1;0rad)
  Width = 100
FEATURE [Part::Cut] Cut535
  Base = -> Cut534
  Tool = -> Box524
FEATURE [Sketcher::SketchObject] Sketch007
  FullyConstrained = false
  sketch-geometry (1):
    g0: Circle CenterX=-186.411 CenterY=73.9277 CenterZ=0 NormalX=0 NormalY=0 NormalZ=1 AngleXU=0 Radius=59
FEATURE [Part::Extrusion] Extrude005
  Base = -> Sketch007
  Dir = (52,0,32)
  DirMode = 0
  FaceMakerClass = Part::FaceMakerBullseye
  LengthFwd = 61
  LengthRev = 0
  Placement = pos=(-134,74,-22) rot=(0,0,1;3.14159rad)
  Solid = true
  Symmetric = false
FEATURE [Part::Cylinder] Cylinder1567  label="Válec1567"
  Angle = 360
  AttacherType = Attacher::AttachEngine3D
  Height = 100
  Placement = pos=(103,-12,-60) rot=(0,0,1;0rad)
  Radius = 1.5
FEATURE [Part::Cylinder] Cylinder1568  label="Válec1568"
  Angle = 360
  AttacherType = Attacher::AttachEngine3D
  Height = 100
  Placement = pos=(103,6,-60) rot=(0,0,1;0rad)
  Radius = 1.5
FEATURE [Part::Cylinder] Cylinder1569  label="Válec1569"
  Angle = 360
  AttacherType = Attacher::AttachEngine3D
  Height = 100
  Placement = pos=(76,18,-60) rot=(0,0,1;0rad)
  Radius = 1.5
FEATURE [Part::Cylinder] Cylinder1570  label="Válec1570"
  Angle = 360
  AttacherType = Attacher::AttachEngine3D
  Height = 100
  Placement = pos=(91,-21,-60) rot=(0,0,1;0rad)
  Radius = 1.5
FEATURE [Part::Cylinder] Cylinder1571  label="Válec1571"
  Angle = 360
  AttacherType = Attacher::AttachEngine3D
  Height = 100
  Placement = pos=(13,-21,-60) rot=(0,0,1;0rad)
  Radius = 1.5
FEATURE [Part::Cylinder] Cylinder1572  label="Válec1572"
  Angle = 360
  AttacherType = Attacher::AttachEngine3D
  Height = 100
  Placement = pos=(28,18,-60) rot=(0,0,1;0rad)
  Radius = 1.5
FEATURE [Part::Cylinder] Cylinder1573  label="Válec1573"
  Angle = 360
  AttacherType = Attacher::AttachEngine3D
  Height = 100
  Placement = pos=(1,-12,-60) rot=(0,0,1;0rad)
  Radius = 1.5
FEATURE [Part::Cylinder] Cylinder1574  label="Válec1574"
  Angle = 360
  AttacherType = Attacher::AttachEngine3D
  Height = 100
  Placement = pos=(1,6,-60) rot=(0,0,1;0rad)
  Radius = 1.5
FEATURE [Part::Compound] Compound910  label="srouby_monoblok007"
  Links = -> [Cylinder1567,Cylinder1568,Cylinder1569,Cylinder1570,Cylinder1571,Cylinder1572,Cylinder1573,Cylinder1574]
FEATURE [Part::Cut] Cut536
  Base = -> Extrude005
  Tool = -> Compound910
FEATURE [Part::Cylinder] Cylinder1575  label="Válec1575"
  Angle = 360
  AttacherType = Attacher::AttachEngine3D
  Height = 20
  Placement = pos=(103,-12,-20) rot=(0,0,1;0rad)
  Radius = 4
FEATURE [Part::Cylinder] Cylinder1576  label="Válec1576"
  Angle = 360
  AttacherType = Attacher::AttachEngine3D
  Height = 20
  Placement = pos=(103,6,-20) rot=(0,0,1;0rad)
  Radius = 4
FEATURE [Part::Cylinder] Cylinder1577  label="Válec1577"
  Angle = 360
  AttacherType = Attacher::AttachEngine3D
  Height = 20
  Placement = pos=(76,18,-18) rot=(0,0,1;0rad)
  Radius = 4
FEATURE [Part::Cylinder] Cylinder1578  label="Válec1578"
  Angle = 360
  AttacherType = Attacher::AttachEngine3D
  Height = 20
  Placement = pos=(91,-21,-18) rot=(0,0,1;0rad)
  Radius = 4
FEATURE [Part::Cylinder] Cylinder1579  label="Válec1579"
  Angle = 360
  AttacherType = Attacher::AttachEngine3D
  Height = 40
  Placement = pos=(13,-21,-18) rot=(0,0,1;0rad)
  Radius = 4
FEATURE [Part::Cylinder] Cylinder1580  label="Válec1580"
  Angle = 360
  AttacherType = Attacher::AttachEngine3D
  Height = 40
  Placement = pos=(28,18,-18) rot=(0,0,1;0rad)
  Radius = 4
FEATURE [Part::Cylinder] Cylinder1581  label="Válec1581"
  Angle = 360
  AttacherType = Attacher::AttachEngine3D
  Height = 40
  Placement = pos=(1,-12,-18) rot=(0,0,1;0rad)
  Radius = 4
FEATURE [Part::Cylinder] Cylinder1582  label="Válec1582"
  Angle = 360
  AttacherType = Attacher::AttachEngine3D
  Height = 40
  Placement = pos=(1,6,-18) rot=(0,0,1;0rad)
  Radius = 4
FEATURE [Part::Compound] Compound911  label="srouby_monoblok_silne008"
  Links = -> [Cylinder1575,Cylinder1576,Cylinder1577,Cylinder1578,Cylinder1579,Cylinder1580,Cylinder1581,Cylinder1582]
FEATURE [Part::Cut] Cut537
  Base = -> Cut536
  Tool = -> Compound911
FEATURE [Part::Cylinder] Cylinder1583  label="Válec1583"
  Angle = 360
  AttacherType = Attacher::AttachEngine3D
  Height = 100
  Placement = pos=(36,34,-90) rot=(0,0,1;0rad)
  Radius = 4
FEATURE [Part::Cylinder] Cylinder1584  label="Válec1584"
  Angle = 360
  AttacherType = Attacher::AttachEngine3D
  Height = 100
  Placement = pos=(-50,0,-90) rot=(0,0,1;0rad)
  Radius = 4
FEATURE [Part::Cylinder] Cylinder1585  label="Válec1585"
  Angle = 360
  AttacherType = Attacher::AttachEngine3D
  Height = 100
  Placement = pos=(-36,34,-90) rot=(0,0,1;0rad)
  Radius = 4
FEATURE [Part::Cylinder] Cylinder1586  label="Válec1586"
  Angle = 360
  AttacherType = Attacher::AttachEngine3D
  Height = 100
  Placement = pos=(-36,-34,-90) rot=(0,0,1;0rad)
  Radius = 4
FEATURE [Part::Cylinder] Cylinder1587  label="Válec1587"
  Angle = 360
  AttacherType = Attacher::AttachEngine3D
  Height = 100
  Placement = pos=(50,0,-90) rot=(0,0,1;0rad)
  Radius = 4
FEATURE [Part::Cylinder] Cylinder1588  label="Válec1588"
  Angle = 360
  AttacherType = Attacher::AttachEngine3D
  Height = 100
  Placement = pos=(36,-34,-90) rot=(0,0,1;0rad)
  Radius = 4
FEATURE [Part::Compound] Compound912  label="sbouby_baze_silne010"
  Links = -> [Cylinder1584,Cylinder1585,Cylinder1586,Cylinder1587,Cylinder1583,Cylinder1588]
FEATURE [Part::Cut] Cut538
  Base = -> Cut537
  Tool = -> Compound912
FEATURE [Part::Cylinder] Cylinder1589  label="Válec1589"
  Angle = 360
  AttacherType = Attacher::AttachEngine3D
  Height = 100
  Placement = pos=(36,34,-60) rot=(0,0,1;0rad)
  Radius = 1.5
FEATURE [Part::Cylinder] Cylinder1590  label="Válec1590"
  Angle = 360
  AttacherType = Attacher::AttachEngine3D
  Height = 100
  Placement = pos=(-50,0,-60) rot=(0,0,1;0rad)
  Radius = 1.5
FEATURE [Part::Cylinder] Cylinder1591  label="Válec1591"
  Angle = 360
  AttacherType = Attacher::AttachEngine3D
  Height = 100
  Placement = pos=(-36,34,-60) rot=(0,0,1;0rad)
  Radius = 1.5
FEATURE [Part::Cylinder] Cylinder1592  label="Válec1592"
  Angle = 360
  AttacherType = Attacher::AttachEngine3D
  Height = 100
  Placement = pos=(-36,-34,-60) rot=(0,0,1;0rad)
  Radius = 1.5
FEATURE [Part::Cylinder] Cylinder1593  label="Válec1593"
  Angle = 360
  AttacherType = Attacher::AttachEngine3D
  Height = 100
  Placement = pos=(50,0,-60) rot=(0,0,1;0rad)
  Radius = 1.5
FEATURE [Part::Cylinder] Cylinder1594  label="Válec1594"
  Angle = 360
  AttacherType = Attacher::AttachEngine3D
  Height = 100
  Placement = pos=(36,-34,-60) rot=(0,0,1;0rad)
  Radius = 1.5
FEATURE [Part::Compound] Compound913  label="sbouby_baze007"
  Links = -> [Cylinder1590,Cylinder1591,Cylinder1592,Cylinder1593,Cylinder1589,Cylinder1594]
FEATURE [Part::Cut] Cut539
  Base = -> Cut538
  Tool = -> Compound913
FEATURE [Part::Box] Box525  label="Krychle525"
  AttacherType = Attacher::AttachEngine3D
  Height = 100
  Length = 200
  Placement = pos=(-60,-130,-90) rot=(0,0,1;0rad)
  Width = 100
FEATURE [Part::Cut] Cut540
  Base = -> Cut539
  Tool = -> Box525
FEATURE [Part::Box] Box526  label="Krychle526"
  AttacherType = Attacher::AttachEngine3D
  Height = 100
  Length = 200
  Placement = pos=(-60,44,-90) rot=(0,0,1;0rad)
  Width = 100
FEATURE [Part::Cut] Cut541
  Base = -> Cut540
  Tool = -> Box526
FEATURE [Sketcher::SketchObject] Sketch008
  FullyConstrained = false
  sketch-geometry (1):
    g0: Circle CenterX=-186.411 CenterY=73.9277 CenterZ=0 NormalX=0 NormalY=0 NormalZ=1 AngleXU=0 Radius=59
FEATURE [Part::Extrusion] Extrude006
  Base = -> Sketch008
  Dir = (52,0,32)
  DirMode = 0
  FaceMakerClass = Part::FaceMakerBullseye
  LengthFwd = 61
  LengthRev = 0
  Placement = pos=(-134,74,-22) rot=(0,0,1;3.14159rad)
  Solid = true
  Symmetric = false
FEATURE [Part::Box] Box527  label="Krychle527"
  AttacherType = Attacher::AttachEngine3D
  Height = 100
  Length = 200
  Placement = pos=(-60,-134,-90) rot=(0,0,1;0rad)
  Width = 100
FEATURE [Part::Box] Box528  label="Krychle528"
  AttacherType = Attacher::AttachEngine3D
  Height = 100
  Length = 200
  Placement = pos=(-60,48,-90) rot=(0,0,1;0rad)
  Width = 100
FEATURE [Part::Cut] Cut542
  Base = -> Extrude006
  Tool = -> Box527
FEATURE [Part::Cut] Cut543
  Base = -> Cut542
  Placement = pos=(-32,0,0) rot=(0,0,1;0rad)
  Tool = -> Box528
FEATURE [Sketcher::SketchObject] Sketch009
  FullyConstrained = false
  sketch-geometry (1):
    g0: Circle CenterX=-186.411 CenterY=73.9277 CenterZ=0 NormalX=0 NormalY=0 NormalZ=1 AngleXU=0 Radius=59
FEATURE [Part::Extrusion] Extrude007
  Base = -> Sketch009
  Dir = (52,0,32)
  DirMode = 0
  FaceMakerClass = Part::FaceMakerBullseye
  LengthFwd = 61
  LengthRev = 0
  Placement = pos=(-134,74,-22) rot=(0,0,1;3.14159rad)
  Solid = true
  Symmetric = false
FEATURE [Part::Box] Box529  label="Krychle529"
  AttacherType = Attacher::AttachEngine3D
  Height = 100
  Length = 200
  Placement = pos=(-60,-130,-90) rot=(0,0,1;0rad)
  Width = 100
FEATURE [Part::Cut] Cut544
  Base = -> Extrude007
  Tool = -> Box529
FEATURE [Part::Box] Box530  label="Krychle530"
  AttacherType = Attacher::AttachEngine3D
  Height = 100
  Length = 200
  Placement = pos=(-60,44,-90) rot=(0,0,1;0rad)
  Width = 100
FEATURE [Part::Cut] Cut545
  Base = -> Cut544
  Placement = pos=(-26,0,0) rot=(0,0,1;0rad)
  Tool = -> Box530
FEATURE [Part::Cut] Cut546
  Base = -> Cut543
  Tool = -> Cut545
FEATURE [Part::Cylinder] Cylinder  label="Válec"
  Angle = 360
  AttacherType = Attacher::AttachEngine3D
  Height = 40
  Placement = pos=(0,0,-6) rot=(0,0,1;0rad)
  Radius = 100
FEATURE [Part::Cut] Cut547
  Base = -> Cut546
  Tool = -> Cylinder
FEATURE [Part::Cylinder] Cylinder1595  label="Válec1595"
  Angle = 360
  AttacherType = Attacher::AttachEngine3D
  Height = 160
  Placement = pos=(32,80,-14) rot=(1,0,0;1.5708rad)
  Radius = 1.25
FEATURE [Part::Cylinder] Cylinder1596  label="Válec1596"
  Angle = 360
  AttacherType = Attacher::AttachEngine3D
  Height = 160
  Placement = pos=(16,80,-14) rot=(1,0,0;1.5708rad)
  Radius = 1.25
FEATURE [Part::Compound] Compound914
  Links = -> [Cylinder1595,Cylinder1596]
FEATURE [Part::Cylinder] Cylinder1597  label="Válec1597"
  Angle = 360
  AttacherType = Attacher::AttachEngine3D
  Height = 3
  Placement = pos=(32,80,-14) rot=(1,0,0;1.5708rad)
  Radius = 2.5
FEATURE [Part::Cylinder] Cylinder1598  label="Válec1598"
  Angle = 360
  AttacherType = Attacher::AttachEngine3D
  Height = 3
  Placement = pos=(16,80,-14) rot=(1,0,0;1.5708rad)
  Radius = 2.5
FEATURE [Part::Compound] Compound915
  Links = -> [Cylinder1597,Cylinder1598]
  Placement = pos=(0,-31,0) rot=(0,0,1;0rad)
FEATURE [Part::Cylinder] Cylinder1599  label="Válec1599"
  Angle = 360
  AttacherType = Attacher::AttachEngine3D
  Height = 3
  Placement = pos=(32,80,-14) rot=(1,0,0;1.5708rad)
  Radius = 2.5
FEATURE [Part::Cylinder] Cylinder1600  label="Válec1600"
  Angle = 360
  AttacherType = Attacher::AttachEngine3D
  Height = 3
  Placement = pos=(16,80,-14) rot=(1,0,0;1.5708rad)
  Radius = 2.5
FEATURE [Part::Compound] Compound916
  Links = -> [Cylinder1599,Cylinder1600]
  Placement = pos=(0,-112,0) rot=(0,0,1;0rad)
FEATURE [Part::Cut] Cut548
  Base = -> Cut547
  Tool = -> Compound914
FEATURE [Part::Cut] Cut549
  Base = -> Cut548
  Tool = -> Compound916
FEATURE [Part::Cut] Cut550
  Base = -> Cut549
  Tool = -> Compound915
FEATURE [Part::Chamfer] Chamfer042
  Base = -> Cut550
  Edges = 2 edges r=3: [Edge3,Edge18]
FEATURE [Part::Chamfer] Chamfer043
  Base = -> Chamfer042
  Edges = 2 edges r=2: [Edge6,Edge23]
FEATURE [Part::Box] Box531  label="Krychle531"
  AttacherType = Attacher::AttachEngine3D
  Height = 100
  Length = 100
  Placement = pos=(40,-100,-90) rot=(0,0,1;0rad)
  Width = 200
FEATURE [Part::Cut] Cut551
  Base = -> Chamfer043
  Tool = -> Box531
FEATURE [Part::Chamfer] Chamfer044
  Base = -> Cut551
  Edges = 1 edges r=2: [Edge6]
FEATURE [Part::Chamfer] Chamfer045
  Base = -> Chamfer044
  Edges = 1 edges r=2: [Edge23]
FEATURE [Part::Chamfer] Chamfer046  label="cable-organizer"
  Base = -> Chamfer045
  Edges = 2 edges r=1.9: [Edge11,Edge41]
FEATURE [Sketcher::SketchObject] Sketch010
  FullyConstrained = false
  sketch-geometry (1):
    g0: Circle CenterX=-186.411 CenterY=73.9277 CenterZ=0 NormalX=0 NormalY=0 NormalZ=1 AngleXU=0 Radius=59
FEATURE [Part::Extrusion] Extrude008
  Base = -> Sketch010
  Dir = (52,0,32)
  DirMode = 0
  FaceMakerClass = Part::FaceMakerBullseye
  LengthFwd = 61
  LengthRev = 0
  Placement = pos=(-134,74,-22) rot=(0,0,1;3.14159rad)
  Solid = true
  Symmetric = false
FEATURE [Sketcher::SketchObject] Sketch011
  FullyConstrained = false
  sketch-geometry (1):
    g0: Circle CenterX=-186.411 CenterY=73.9277 CenterZ=0 NormalX=0 NormalY=0 NormalZ=1 AngleXU=0 Radius=59
FEATURE [Part::Extrusion] Extrude009
  Base = -> Sketch011
  Dir = (52,0,32)
  DirMode = 0
  FaceMakerClass = Part::FaceMakerBullseye
  LengthFwd = 61
  LengthRev = 0
  Placement = pos=(-134,74,-22) rot=(0,0,1;3.14159rad)
  Solid = true
  Symmetric = false
FEATURE [Part::Box] Box532  label="Krychle532"
  AttacherType = Attacher::AttachEngine3D
  Height = 100
  Length = 200
  Placement = pos=(-60,-138,-90) rot=(0,0,1;0rad)
  Width = 100
FEATURE [Part::Cut] Cut552
  Base = -> Extrude008
  Tool = -> Box532
FEATURE [Part::Box] Box533  label="Krychle533"
  AttacherType = Attacher::AttachEngine3D
  Height = 100
  Length = 200
  Placement = pos=(-60,48,-90) rot=(0,0,1;0rad)
  Width = 100
FEATURE [Part::Cut] Cut553
  Base = -> Cut552
  Placement = pos=(-32,0,0) rot=(0,0,1;0rad)
  Tool = -> Box533
FEATURE [Part::Box] Box534  label="Krychle534"
  AttacherType = Attacher::AttachEngine3D
  Height = 100
  Length = 200
  Placement = pos=(-60,-134,-90) rot=(0,0,1;0rad)
  Width = 100
FEATURE [Part::Cut] Cut555
  Base = -> Extrude009
  Tool = -> Box534
FEATURE [Part::Box] Box535  label="Krychle535"
  AttacherType = Attacher::AttachEngine3D
  Height = 100
  Length = 200
  Placement = pos=(-60,44,-90) rot=(0,0,1;0rad)
  Width = 100
FEATURE [Part::Cut] Cut554
  Base = -> Cut555
  Placement = pos=(-26,0,0) rot=(0,0,1;0rad)
  Tool = -> Box535
FEATURE [Part::Cut] Cut557
  Base = -> Cut553
  Tool = -> Cut554
FEATURE [Part::Cylinder] Cylinder1601  label="Válec1601"
  Angle = 360
  AttacherType = Attacher::AttachEngine3D
  Height = 160
  Placement = pos=(32,80,-14) rot=(1,0,0;1.5708rad)
  Radius = 1.25
FEATURE [Part::Cylinder] Cylinder1602  label="Válec1602"
  Angle = 360
  AttacherType = Attacher::AttachEngine3D
  Height = 160
  Placement = pos=(16,80,-14) rot=(1,0,0;1.5708rad)
  Radius = 1.25
FEATURE [Part::Compound] Compound917
  Links = -> [Cylinder1601,Cylinder1602]
FEATURE [Part::Cylinder] Cylinder1603  label="Válec1603"
  Angle = 360
  AttacherType = Attacher::AttachEngine3D
  Height = 40
  Placement = pos=(0,0,-6) rot=(0,0,1;0rad)
  Radius = 100
FEATURE [Part::Cut] Cut556
  Base = -> Cut557
  Tool = -> Cylinder1603
FEATURE [Part::Cylinder] Cylinder1604  label="Válec1604"
  Angle = 360
  AttacherType = Attacher::AttachEngine3D
  Height = 3
  Placement = pos=(32,80,-14) rot=(1,0,0;1.5708rad)
  Radius = 2.5
FEATURE [Part::Cylinder] Cylinder1605  label="Válec1605"
  Angle = 360
  AttacherType = Attacher::AttachEngine3D
  Height = 3
  Placement = pos=(16,80,-14) rot=(1,0,0;1.5708rad)
  Radius = 2.5
FEATURE [Part::Compound] Compound918
  Links = -> [Cylinder1604,Cylinder1605]
  Placement = pos=(0,-31,0) rot=(0,0,1;0rad)
FEATURE [Part::Cylinder] Cylinder1606  label="Válec1606"
  Angle = 360
  AttacherType = Attacher::AttachEngine3D
  Height = 3
  Placement = pos=(32,80,-14) rot=(1,0,0;1.5708rad)
  Radius = 2.5
FEATURE [Part::Cylinder] Cylinder1607  label="Válec1607"
  Angle = 360
  AttacherType = Attacher::AttachEngine3D
  Height = 3
  Placement = pos=(16,80,-14) rot=(1,0,0;1.5708rad)
  Radius = 2.5
FEATURE [Part::Compound] Compound919
  Links = -> [Cylinder1606,Cylinder1607]
  Placement = pos=(0,-116,0) rot=(0,0,1;0rad)
FEATURE [Part::Box] Box536  label="Krychle536"
  AttacherType = Attacher::AttachEngine3D
  Height = 100
  Length = 100
  Placement = pos=(40,-100,-90) rot=(0,0,1;0rad)
  Width = 200
FEATURE [Part::Cut] Cut558
  Base = -> Cut556
  Tool = -> Compound917
FEATURE [Part::Cut] Cut559
  Base = -> Cut558
  Tool = -> Compound919
FEATURE [Part::Cut] Cut560
  Base = -> Cut559
  Tool = -> Compound918
FEATURE [Part::Chamfer] Chamfer047
  Base = -> Cut560
  Edges = 2 edges r=3: [Edge3,Edge18]
FEATURE [Part::Chamfer] Chamfer048
  Base = -> Chamfer047
  Edges = 2 edges r=2: [Edge6,Edge23]
FEATURE [Part::Cut] Cut561
  Base = -> Chamfer048
  Tool = -> Box536
FEATURE [Part::Chamfer] Chamfer049
  Base = -> Cut561
  Edges = 1 edges r=2: [Edge6]
FEATURE [Part::Chamfer] Chamfer050
  Base = -> Chamfer049
  Edges = 1 edges r=2: [Edge23]
FEATURE [Part::Chamfer] Chamfer051  label="deep-neck-cable-organizer"
  Base = -> Chamfer050
  Edges = 2 edges r=1.9: [Edge11,Edge41]
FEATURE [Part::Chamfer] Chamfer052  label="Base_deep-neck-cable-organizer"
  Base = -> Chamfer051
  Edges = 2 edges r=3: [Edge26,Edge27]
FEATURE [Part::Chamfer] Chamfer053  label="Base_neck-cable-organizer"
  Base = -> Chamfer046
  Edges = 2 edges r=3: [Edge26,Edge27]
FEATURE [Sketcher::SketchObject] Sketch012
  FullyConstrained = false
  sketch-geometry (1):
    g0: Circle CenterX=-186.411 CenterY=73.9277 CenterZ=0 NormalX=0 NormalY=0 NormalZ=1 AngleXU=0 Radius=59
FEATURE [Part::Extrusion] Extrude010
  Base = -> Sketch012
  Dir = (40,0,32)
  DirMode = 0
  FaceMakerClass = Part::FaceMakerBullseye
  LengthFwd = 67
  LengthRev = 0
  Placement = pos=(-134,74,-22) rot=(0,0,1;3.14159rad)
  Solid = true
  Symmetric = false
FEATURE [Part::Cylinder] Cylinder1608  label="Válec1608"
  Angle = 360
  AttacherType = Attacher::AttachEngine3D
  Height = 100
  Placement = pos=(-34,-16,-90) rot=(0,0,1;0rad)
  Radius = 4
FEATURE [Part::Cylinder] Cylinder1609  label="Válec1609"
  Angle = 360
  AttacherType = Attacher::AttachEngine3D
  Height = 100
  Placement = pos=(16,34,-90) rot=(0,0,1;0rad)
  Radius = 4
FEATURE [Part::Cylinder] Cylinder1610  label="Válec1610"
  Angle = 360
  AttacherType = Attacher::AttachEngine3D
  Height = 100
  Placement = pos=(-16,34,-90) rot=(0,0,1;0rad)
  Radius = 4
FEATURE [Part::Cylinder] Cylinder1611  label="Válec1611"
  Angle = 360
  AttacherType = Attacher::AttachEngine3D
  Height = 100
  Placement = pos=(-16,-34,-90) rot=(0,0,1;0rad)
  Radius = 4
FEATURE [Part::Cylinder] Cylinder1612  label="Válec1612"
  Angle = 360
  AttacherType = Attacher::AttachEngine3D
  Height = 100
  Placement = pos=(34,-16,-90) rot=(0,0,1;0rad)
  Radius = 4
FEATURE [Part::Cylinder] Cylinder1613  label="Válec1613"
  Angle = 360
  AttacherType = Attacher::AttachEngine3D
  Height = 100
  Placement = pos=(10,-36,-90) rot=(0,0,1;0rad)
  Radius = 4
FEATURE [Part::Cylinder] Cylinder1614  label="Válec1614"
  Angle = 360
  AttacherType = Attacher::AttachEngine3D
  Height = 100
  Placement = pos=(16,34,-60) rot=(0,0,1;0rad)
  Radius = 1.5
FEATURE [Part::Cylinder] Cylinder1615  label="Válec1615"
  Angle = 360
  AttacherType = Attacher::AttachEngine3D
  Height = 100
  Placement = pos=(-34,16,-60) rot=(0,0,1;0rad)
  Radius = 1.5
FEATURE [Part::Cylinder] Cylinder1616  label="Válec1616"
  Angle = 360
  AttacherType = Attacher::AttachEngine3D
  Height = 100
  Placement = pos=(-34,-16,-60) rot=(0,0,1;0rad)
  Radius = 1.5
FEATURE [Part::Cylinder] Cylinder1617  label="Válec1617"
  Angle = 360
  AttacherType = Attacher::AttachEngine3D
  Height = 100
  Placement = pos=(34,-16,-60) rot=(0,0,1;0rad)
  Radius = 1.5
FEATURE [Part::Cylinder] Cylinder1618  label="Válec1618"
  Angle = 360
  AttacherType = Attacher::AttachEngine3D
  Height = 100
  Placement = pos=(34,16,-60) rot=(0,0,1;0rad)
  Radius = 1.5
FEATURE [Part::Cylinder] Cylinder1619  label="Válec1619"
  Angle = 360
  AttacherType = Attacher::AttachEngine3D
  Height = 100
  Placement = pos=(10,-36,-60) rot=(0,0,1;0rad)
  Radius = 1.5
FEATURE [Part::Box] Box537  label="Krychle537"
  AttacherType = Attacher::AttachEngine3D
  Height = 120
  Length = 200
  Placement = pos=(-60,-134,-90) rot=(0,0,1;0rad)
  Width = 100
FEATURE [Part::Box] Box538  label="Krychle538"
  AttacherType = Attacher::AttachEngine3D
  Height = 120
  Length = 200
  Placement = pos=(-60,44,-90) rot=(0,0,1;0rad)
  Width = 100
FEATURE [Part::Cylinder] Cylinder1620  label="Válec1620"
  Angle = 360
  AttacherType = Attacher::AttachEngine3D
  Height = 100
  Placement = pos=(90,0,-60) rot=(0,0,1;0rad)
  Radius = 1.5
FEATURE [Part::Cylinder] Cylinder1621  label="Válec1621"
  Angle = 360
  AttacherType = Attacher::AttachEngine3D
  Height = 100
  Placement = pos=(14,0,-60) rot=(0,0,1;0rad)
  Radius = 1.5
FEATURE [Part::Cylinder] Cylinder1622  label="Válec1622"
  Angle = 360
  AttacherType = Attacher::AttachEngine3D
  Height = 100
  Placement = pos=(90,0,-18) rot=(0,0,1;0rad)
  Radius = 4
FEATURE [Part::Cylinder] Cylinder1623  label="Válec1623"
  Angle = 360
  AttacherType = Attacher::AttachEngine3D
  Height = 100
  Placement = pos=(14,0,-18) rot=(0,0,1;0rad)
  Radius = 4
FEATURE [Part::Box] Box539  label="Krychle539"
  AttacherType = Attacher::AttachEngine3D
  Height = 2
  Length = 6
  Placement = pos=(75,38,-22) rot=(0,0,1;0rad)
  Width = 6
FEATURE [Part::Box] Box540  label="Krychle540"
  AttacherType = Attacher::AttachEngine3D
  Height = 2
  Length = 6
  Placement = pos=(23,38,-22) rot=(0,0,1;0rad)
  Width = 6
FEATURE [Part::Cylinder] Cylinder1624  label="Válec1624"
  Angle = 360
  AttacherType = Attacher::AttachEngine3D
  Height = 32
  Placement = pos=(26,41,-46) rot=(0,0,1;0rad)
  Radius = 1.5
FEATURE [Part::Cylinder] Cylinder1625  label="Válec1625"
  Angle = 360
  AttacherType = Attacher::AttachEngine3D
  Height = 32
  Placement = pos=(78,41,-46) rot=(0,0,1;0rad)
  Radius = 1.5
FEATURE [Part::Cylinder] Cylinder1626  label="Válec1626"
  Angle = 360
  AttacherType = Attacher::AttachEngine3D
  Height = 100
  Placement = pos=(-34,16,-90) rot=(0,0,1;0rad)
  Radius = 4
FEATURE [Part::Cylinder] Cylinder1627  label="Válec1627"
  Angle = 360
  AttacherType = Attacher::AttachEngine3D
  Height = 100
  Placement = pos=(34,16,-90) rot=(0,0,1;0rad)
  Radius = 4
FEATURE [Part::Cylinder] Cylinder1628  label="Válec1628"
  Angle = 360
  AttacherType = Attacher::AttachEngine3D
  Height = 100
  Placement = pos=(-16,-34,-60) rot=(0,0,1;0rad)
  Radius = 1.5
FEATURE [Part::Cylinder] Cylinder1629  label="Válec1629"
  Angle = 360
  AttacherType = Attacher::AttachEngine3D
  Height = 100
  Placement = pos=(-16,34,-60) rot=(0,0,1;0rad)
  Radius = 1.5
FEATURE [Part::Cylinder] Cylinder1630  label="Válec1630"
  Angle = 360
  AttacherType = Attacher::AttachEngine3D
  Height = 100
  Placement = pos=(-34,16,-60) rot=(0,0,1;0rad)
  Radius = 1.5
FEATURE [Part::Cylinder] Cylinder1631  label="Válec1631"
  Angle = 360
  AttacherType = Attacher::AttachEngine3D
  Height = 100
  Placement = pos=(-34,-16,-60) rot=(0,0,1;0rad)
  Radius = 1.5
FEATURE [Part::Cylinder] Cylinder1632  label="Válec1632"
  Angle = 360
  AttacherType = Attacher::AttachEngine3D
  Height = 100
  Placement = pos=(34,-16,-60) rot=(0,0,1;0rad)
  Radius = 1.5
FEATURE [Part::Cylinder] Cylinder1633  label="Válec1633"
  Angle = 360
  AttacherType = Attacher::AttachEngine3D
  Height = 100
  Placement = pos=(34,16,-60) rot=(0,0,1;0rad)
  Radius = 1.5
FEATURE [Part::Compound] Compound922  label="sbouby_baze_silne011"
  Links = -> [Cylinder1608,Cylinder1610,Cylinder1611,Cylinder1612,Cylinder1609,Cylinder1613,Cylinder1626,Cylinder1627]
  Placement = pos=(0,0,12) rot=(0,0,1;0rad)
FEATURE [Part::Compound] Compound923  label="sbouby_baze008"
  Links = -> [Cylinder1615,Cylinder1616,Cylinder1617,Cylinder1618,Cylinder1614,Cylinder1619,Cylinder1628,Cylinder1629]
FEATURE [Part::Compound] Compound924
  Links = -> [Box539,Box540]
FEATURE [Part::Compound] Compound925
  Links = -> [Cylinder1624,Cylinder1625]
FEATURE [Part::Compound] Compound926  label="srouby_troj_silne006"
  Links = -> [Cylinder1622,Cylinder1623]
FEATURE [Part::Compound] Compound927  label="srouby_troj006"
  Links = -> [Cylinder1620,Cylinder1621]
FEATURE [Part::Cylinder] Cylinder1634  label="Válec1634"
  Angle = 360
  AttacherType = Attacher::AttachEngine3D
  Height = 100
  Placement = pos=(16,34,-60) rot=(0,0,1;0rad)
  Radius = 1.5
FEATURE [Part::Cylinder] Cylinder1635  label="Válec1635"
  Angle = 360
  AttacherType = Attacher::AttachEngine3D
  Height = 100
  Placement = pos=(10,-36,-60) rot=(0,0,1;0rad)
  Radius = 1.5
FEATURE [Part::Cylinder] Cylinder1636  label="Válec1636"
  Angle = 360
  AttacherType = Attacher::AttachEngine3D
  Height = 100
  Placement = pos=(-16,-34,-60) rot=(0,0,1;0rad)
  Radius = 1.5
FEATURE [Part::Cylinder] Cylinder1637  label="Válec1637"
  Angle = 360
  AttacherType = Attacher::AttachEngine3D
  Height = 100
  Placement = pos=(-16,34,-60) rot=(0,0,1;0rad)
  Radius = 1.5
FEATURE [Part::Compound] Compound928  label="sbouby_baze009"
  Links = -> [Cylinder1630,Cylinder1631,Cylinder1632,Cylinder1633,Cylinder1634,Cylinder1635,Cylinder1636,Cylinder1637]
FEATURE [Part::Cylinder] Cylinder1638  label="Válec1638"
  Angle = 360
  AttacherType = Attacher::AttachEngine3D
  Height = 16
  Placement = pos=(0,0,2) rot=(0,0,1;0rad)
  Radius = 59
FEATURE [Part::Cylinder] Cylinder1639  label="Válec1639"
  Angle = 360
  AttacherType = Attacher::AttachEngine3D
  Height = 20
  Placement = pos=(103,-12,-20) rot=(0,0,1;0rad)
  Radius = 4
FEATURE [Part::Cylinder] Cylinder1640  label="Válec1640"
  Angle = 360
  AttacherType = Attacher::AttachEngine3D
  Height = 20
  Placement = pos=(103,12,-20) rot=(0,0,1;0rad)
  Radius = 4
FEATURE [Part::Cylinder] Cylinder1641  label="Válec1641"
  Angle = 360
  AttacherType = Attacher::AttachEngine3D
  Height = 20
  Placement = pos=(76,24,-18) rot=(0,0,1;0rad)
  Radius = 4
FEATURE [Part::Cylinder] Cylinder1642  label="Válec1642"
  Angle = 360
  AttacherType = Attacher::AttachEngine3D
  Height = 20
  Placement = pos=(91,-27,-18) rot=(0,0,1;0rad)
  Radius = 4
FEATURE [Part::Cylinder] Cylinder1643  label="Válec1643"
  Angle = 360
  AttacherType = Attacher::AttachEngine3D
  Height = 40
  Placement = pos=(13,-27,-18) rot=(0,0,1;0rad)
  Radius = 4
FEATURE [Part::Cylinder] Cylinder1644  label="Válec1644"
  Angle = 360
  AttacherType = Attacher::AttachEngine3D
  Height = 40
  Placement = pos=(28,24,-18) rot=(0,0,1;0rad)
  Radius = 4
FEATURE [Part::Cylinder] Cylinder1645  label="Válec1645"
  Angle = 360
  AttacherType = Attacher::AttachEngine3D
  Height = 40
  Placement = pos=(1,-12,-18) rot=(0,0,1;0rad)
  Radius = 4
FEATURE [Part::Cylinder] Cylinder1646  label="Válec1646"
  Angle = 360
  AttacherType = Attacher::AttachEngine3D
  Height = 40
  Placement = pos=(1,12,-18) rot=(0,0,1;0rad)
  Radius = 4
FEATURE [Part::Compound] Compound929  label="srouby_monoblok_silne010"
  Links = -> [Cylinder1639,Cylinder1640,Cylinder1641,Cylinder1642,Cylinder1643,Cylinder1644,Cylinder1645,Cylinder1646]
FEATURE [Part::Cut] Cut572
  Base = -> Cylinder1638
  Tool = -> Compound929
FEATURE [Part::Cylinder] Cylinder1647  label="Válec1647"
  Angle = 360
  AttacherType = Attacher::AttachEngine3D
  Height = 100
  Placement = pos=(90,0,-18) rot=(0,0,1;0rad)
  Radius = 4
FEATURE [Part::Cylinder] Cylinder1648  label="Válec1648"
  Angle = 360
  AttacherType = Attacher::AttachEngine3D
  Height = 100
  Placement = pos=(14,0,-18) rot=(0,0,1;0rad)
  Radius = 4
FEATURE [Part::Compound] Compound931  label="srouby_troj_silne007"
  Links = -> [Cylinder1647,Cylinder1648]
FEATURE [Part::Cylinder] Cylinder1649  label="Válec1649"
  Angle = 360
  AttacherType = Attacher::AttachEngine3D
  Height = 100
  Placement = pos=(-16,-34,-90) rot=(0,0,1;0rad)
  Radius = 4
FEATURE [Part::Cylinder] Cylinder1650  label="Válec1650"
  Angle = 360
  AttacherType = Attacher::AttachEngine3D
  Height = 100
  Placement = pos=(-34,-16,-90) rot=(0,0,1;0rad)
  Radius = 4
FEATURE [Part::Cylinder] Cylinder1651  label="Válec1651"
  Angle = 360
  AttacherType = Attacher::AttachEngine3D
  Height = 100
  Placement = pos=(-16,34,-90) rot=(0,0,1;0rad)
  Radius = 4
FEATURE [Part::Cylinder] Cylinder1652  label="Válec1652"
  Angle = 360
  AttacherType = Attacher::AttachEngine3D
  Height = 100
  Placement = pos=(34,-16,-90) rot=(0,0,1;0rad)
  Radius = 4
FEATURE [Part::Cylinder] Cylinder1653  label="Válec1653"
  Angle = 360
  AttacherType = Attacher::AttachEngine3D
  Height = 100
  Placement = pos=(16,34,-90) rot=(0,0,1;0rad)
  Radius = 4
FEATURE [Part::Cylinder] Cylinder1654  label="Válec1654"
  Angle = 360
  AttacherType = Attacher::AttachEngine3D
  Height = 100
  Placement = pos=(10,-36,-90) rot=(0,0,1;0rad)
  Radius = 4
FEATURE [Part::Cylinder] Cylinder1655  label="Válec1655"
  Angle = 360
  AttacherType = Attacher::AttachEngine3D
  Height = 100
  Placement = pos=(-34,16,-90) rot=(0,0,1;0rad)
  Radius = 4
FEATURE [Part::Cylinder] Cylinder1656  label="Válec1656"
  Angle = 360
  AttacherType = Attacher::AttachEngine3D
  Height = 100
  Placement = pos=(34,16,-90) rot=(0,0,1;0rad)
  Radius = 4
FEATURE [Part::Compound] Compound930  label="sbouby_baze_silne012"
  Links = -> [Cylinder1650,Cylinder1651,Cylinder1649,Cylinder1652,Cylinder1653,Cylinder1654,Cylinder1655,Cylinder1656]
FEATURE [Part::Cut] Cut573
  Base = -> Cut572
  Tool = -> Compound930
FEATURE [Part::Cut] Cut574
  Base = -> Cut573
  Tool = -> Compound928
FEATURE [Part::Chamfer] Chamfer054
  Base = -> Cut574
  Edges = 1 edges r=4: [Edge3]
FEATURE [Part::Cut] Cut575
  Base = -> Chamfer054
  Placement = pos=(0,0,14) rot=(0,0,1;0rad)
  Tool = -> Compound931
FEATURE [Part::Cylinder] Cylinder1657  label="Válec1657"
  Angle = 360
  AttacherType = Attacher::AttachEngine3D
  Height = 100
  Placement = pos=(103,-12,-60) rot=(0,0,1;0rad)
  Radius = 1.5
FEATURE [Part::Cylinder] Cylinder1658  label="Válec1658"
  Angle = 360
  AttacherType = Attacher::AttachEngine3D
  Height = 100
  Placement = pos=(103,12,-60) rot=(0,0,1;0rad)
  Radius = 1.5
FEATURE [Part::Cylinder] Cylinder1659  label="Válec1659"
  Angle = 360
  AttacherType = Attacher::AttachEngine3D
  Height = 100
  Placement = pos=(76,24,-60) rot=(0,0,1;0rad)
  Radius = 1.5
FEATURE [Part::Cylinder] Cylinder1660  label="Válec1660"
  Angle = 360
  AttacherType = Attacher::AttachEngine3D
  Height = 100
  Placement = pos=(91,-27,-60) rot=(0,0,1;0rad)
  Radius = 1.5
FEATURE [Part::Cylinder] Cylinder1661  label="Válec1661"
  Angle = 360
  AttacherType = Attacher::AttachEngine3D
  Height = 100
  Placement = pos=(13,-27,-60) rot=(0,0,1;0rad)
  Radius = 1.5
FEATURE [Part::Cylinder] Cylinder1662  label="Válec1662"
  Angle = 360
  AttacherType = Attacher::AttachEngine3D
  Height = 100
  Placement = pos=(28,24,-60) rot=(0,0,1;0rad)
  Radius = 1.5
FEATURE [Part::Cylinder] Cylinder1663  label="Válec1663"
  Angle = 360
  AttacherType = Attacher::AttachEngine3D
  Height = 100
  Placement = pos=(1,-12,-60) rot=(0,0,1;0rad)
  Radius = 1.5
FEATURE [Part::Cylinder] Cylinder1664  label="Válec1664"
  Angle = 360
  AttacherType = Attacher::AttachEngine3D
  Height = 100
  Placement = pos=(1,12,-60) rot=(0,0,1;0rad)
  Radius = 1.5
FEATURE [Part::Compound] Compound920  label="srouby_monoblok008"
  Links = -> [Cylinder1657,Cylinder1658,Cylinder1659,Cylinder1660,Cylinder1661,Cylinder1662,Cylinder1663,Cylinder1664]
FEATURE [Part::Cut] Cut563
  Base = -> Extrude010
  Tool = -> Compound920
FEATURE [Part::Cylinder] Cylinder1665  label="Válec1665"
  Angle = 360
  AttacherType = Attacher::AttachEngine3D
  Height = 20
  Placement = pos=(103,-12,-20) rot=(0,0,1;0rad)
  Radius = 4
FEATURE [Part::Cylinder] Cylinder1666  label="Válec1666"
  Angle = 360
  AttacherType = Attacher::AttachEngine3D
  Height = 20
  Placement = pos=(103,12,-20) rot=(0,0,1;0rad)
  Radius = 4
FEATURE [Part::Cylinder] Cylinder1667  label="Válec1667"
  Angle = 360
  AttacherType = Attacher::AttachEngine3D
  Height = 32
  Placement = pos=(76,24,-18) rot=(0,0,1;0rad)
  Radius = 4
FEATURE [Part::Cylinder] Cylinder1668  label="Válec1668"
  Angle = 360
  AttacherType = Attacher::AttachEngine3D
  Height = 20
  Placement = pos=(91,-27,-18) rot=(0,0,1;0rad)
  Radius = 4
FEATURE [Part::Cylinder] Cylinder1669  label="Válec1669"
  Angle = 360
  AttacherType = Attacher::AttachEngine3D
  Height = 40
  Placement = pos=(13,-27,-18) rot=(0,0,1;0rad)
  Radius = 4
FEATURE [Part::Cylinder] Cylinder1670  label="Válec1670"
  Angle = 360
  AttacherType = Attacher::AttachEngine3D
  Height = 40
  Placement = pos=(28,24,-18) rot=(0,0,1;0rad)
  Radius = 4
FEATURE [Part::Cylinder] Cylinder1671  label="Válec1671"
  Angle = 360
  AttacherType = Attacher::AttachEngine3D
  Height = 40
  Placement = pos=(1,-12,-18) rot=(0,0,1;0rad)
  Radius = 4
FEATURE [Part::Cylinder] Cylinder1672  label="Válec1672"
  Angle = 360
  AttacherType = Attacher::AttachEngine3D
  Height = 40
  Placement = pos=(1,12,-18) rot=(0,0,1;0rad)
  Radius = 4
FEATURE [Part::Compound] Compound921  label="srouby_monoblok_silne009"
  Links = -> [Cylinder1665,Cylinder1666,Cylinder1667,Cylinder1668,Cylinder1669,Cylinder1670,Cylinder1671,Cylinder1672]
FEATURE [Part::Cut] Cut562
  Base = -> Cut563
  Tool = -> Compound921
FEATURE [Part::Cut] Cut564
  Base = -> Cut562
  Tool = -> Compound922
FEATURE [Part::Cut] Cut565
  Base = -> Cut564
  Tool = -> Compound923
FEATURE [Part::Cut] Cut566
  Base = -> Cut565
  Tool = -> Box537
FEATURE [Part::Cut] Cut567
  Base = -> Cut566
  Tool = -> Box538
FEATURE [Part::Cut] Cut568
  Base = -> Cut567
  Tool = -> Compound924
FEATURE [Part::Cut] Cut569
  Base = -> Cut568
  Tool = -> Compound925
FEATURE [Part::Cut] Cut570
  Base = -> Cut569
  Tool = -> Compound927
FEATURE [Part::Cut] Cut571
  Base = -> Cut570
  Tool = -> Compound926
FEATURE [Part::Chamfer] Chamfer055
  Base = -> Cut571
  Edges = 1 edges r=4: [Edge44]
FEATURE [Part::Chamfer] Chamfer056
  Base = -> Chamfer055
  Edges = 2 edges r=3.5: [Edge4,Edge6]
FEATURE [Part::Cylinder] Cylinder1673  label="Válec1673"
  Angle = 360
  AttacherType = Attacher::AttachEngine3D
  Height = 4
  Placement = pos=(52,0,-26) rot=(0,0,1;0rad)
  Radius = 59
FEATURE [Part::Cylinder] Cylinder1674  label="Válec1674"
  Angle = 360
  AttacherType = Attacher::AttachEngine3D
  Height = 100
  Placement = pos=(103,-12,-60) rot=(0,0,1;0rad)
  Radius = 1.5
FEATURE [Part::Cylinder] Cylinder1675  label="Válec1675"
  Angle = 360
  AttacherType = Attacher::AttachEngine3D
  Height = 100
  Placement = pos=(103,12,-60) rot=(0,0,1;0rad)
  Radius = 1.5
FEATURE [Part::Cylinder] Cylinder1676  label="Válec1676"
  Angle = 360
  AttacherType = Attacher::AttachEngine3D
  Height = 100
  Placement = pos=(76,24,-60) rot=(0,0,1;0rad)
  Radius = 1.5
FEATURE [Part::Cylinder] Cylinder1677  label="Válec1677"
  Angle = 360
  AttacherType = Attacher::AttachEngine3D
  Height = 100
  Placement = pos=(91,-27,-60) rot=(0,0,1;0rad)
  Radius = 1.5
FEATURE [Part::Cylinder] Cylinder1678  label="Válec1678"
  Angle = 360
  AttacherType = Attacher::AttachEngine3D
  Height = 100
  Placement = pos=(13,-27,-60) rot=(0,0,1;0rad)
  Radius = 1.5
FEATURE [Part::Cylinder] Cylinder1679  label="Válec1679"
  Angle = 360
  AttacherType = Attacher::AttachEngine3D
  Height = 100
  Placement = pos=(28,24,-60) rot=(0,0,1;0rad)
  Radius = 1.5
FEATURE [Part::Cylinder] Cylinder1680  label="Válec1680"
  Angle = 360
  AttacherType = Attacher::AttachEngine3D
  Height = 100
  Placement = pos=(1,-12,-60) rot=(0,0,1;0rad)
  Radius = 1.5
FEATURE [Part::Cylinder] Cylinder1681  label="Válec1681"
  Angle = 360
  AttacherType = Attacher::AttachEngine3D
  Height = 100
  Placement = pos=(1,12,-60) rot=(0,0,1;0rad)
  Radius = 1.5
FEATURE [Part::Compound] Compound932  label="srouby_monoblok009"
  Links = -> [Cylinder1674,Cylinder1675,Cylinder1676,Cylinder1677,Cylinder1678,Cylinder1679,Cylinder1680,Cylinder1681]
FEATURE [Part::Cut] Cut576
  Base = -> Cylinder1673
  Tool = -> Compound932
FEATURE [Part::Box] Box541  label="Krychle541"
  AttacherType = Attacher::AttachEngine3D
  Height = 100
  Length = 200
  Placement = pos=(-60,-130,-90) rot=(0,0,1;0rad)
  Width = 100
FEATURE [Part::Box] Box542  label="Krychle542"
  AttacherType = Attacher::AttachEngine3D
  Height = 100
  Length = 200
  Placement = pos=(-60,44,-90) rot=(0,0,1;0rad)
  Width = 100
FEATURE [Part::Cylinder] Cylinder1682  label="Válec1682"
  Angle = 360
  AttacherType = Attacher::AttachEngine3D
  Height = 100
  Placement = pos=(-34,-16,-90) rot=(0,0,1;0rad)
  Radius = 4
FEATURE [Part::Cylinder] Cylinder1683  label="Válec1683"
  Angle = 360
  AttacherType = Attacher::AttachEngine3D
  Height = 100
  Placement = pos=(-16,34,-90) rot=(0,0,1;0rad)
  Radius = 4
FEATURE [Part::Cylinder] Cylinder1684  label="Válec1684"
  Angle = 360
  AttacherType = Attacher::AttachEngine3D
  Height = 100
  Placement = pos=(-16,-34,-90) rot=(0,0,1;0rad)
  Radius = 4
FEATURE [Part::Cylinder] Cylinder1685  label="Válec1685"
  Angle = 360
  AttacherType = Attacher::AttachEngine3D
  Height = 100
  Placement = pos=(34,-16,-90) rot=(0,0,1;0rad)
  Radius = 4
FEATURE [Part::Cylinder] Cylinder1686  label="Válec1686"
  Angle = 360
  AttacherType = Attacher::AttachEngine3D
  Height = 100
  Placement = pos=(16,34,-90) rot=(0,0,1;0rad)
  Radius = 4
FEATURE [Part::Cylinder] Cylinder1687  label="Válec1687"
  Angle = 360
  AttacherType = Attacher::AttachEngine3D
  Height = 100
  Placement = pos=(16,-34,-90) rot=(0,0,1;0rad)
  Radius = 4
FEATURE [Part::Cylinder] Cylinder1688  label="Válec1688"
  Angle = 360
  AttacherType = Attacher::AttachEngine3D
  Height = 100
  Placement = pos=(-34,16,-90) rot=(0,0,1;0rad)
  Radius = 4
FEATURE [Part::Cylinder] Cylinder1689  label="Válec1689"
  Angle = 360
  AttacherType = Attacher::AttachEngine3D
  Height = 100
  Placement = pos=(34,16,-90) rot=(0,0,1;0rad)
  Radius = 4
FEATURE [Part::Compound] Compound933  label="sbouby_baze_silne013"
  Links = -> [Cylinder1682,Cylinder1683,Cylinder1684,Cylinder1685,Cylinder1686,Cylinder1687,Cylinder1688,Cylinder1689]
FEATURE [Part::Cut] Cut577
  Base = -> Cut576
  Tool = -> Compound933
FEATURE [Part::Cut] Cut578
  Base = -> Cut577
  Tool = -> Box541
FEATURE [Part::Cut] Cut579
  Base = -> Cut578
  Tool = -> Box542
FEATURE [Part::Cylinder] Cylinder1690  label="Válec1690"
  Angle = 360
  AttacherType = Attacher::AttachEngine3D
  Height = 32
  Placement = pos=(26,41,-42) rot=(0,0,1;0rad)
  Radius = 1.5
FEATURE [Part::Cylinder] Cylinder1691  label="Válec1691"
  Angle = 360
  AttacherType = Attacher::AttachEngine3D
  Height = 32
  Placement = pos=(78,41,-42) rot=(0,0,1;0rad)
  Radius = 1.5
FEATURE [Part::Compound] Compound934
  Links = -> [Cylinder1690,Cylinder1691]
FEATURE [Part::Cut] Cut580
  Base = -> Cut579
  Tool = -> Compound934
FEATURE [Part::Cylinder] Cylinder1692  label="Válec1692"
  Angle = 360
  AttacherType = Attacher::AttachEngine3D
  Height = 100
  Placement = pos=(90,0,-60) rot=(0,0,1;0rad)
  Radius = 1.5
FEATURE [Part::Cylinder] Cylinder1693  label="Válec1693"
  Angle = 360
  AttacherType = Attacher::AttachEngine3D
  Height = 100
  Placement = pos=(14,0,-60) rot=(0,0,1;0rad)
  Radius = 1.5
FEATURE [Part::Compound] Compound935  label="srouby_troj007"
  Links = -> [Cylinder1692,Cylinder1693]
FEATURE [Part::Cut] Cut581
  Base = -> Cut580
  Tool = -> Compound935
FEATURE [Part::Compound] Compound936  label="Base_deep-neck-higher"
  Links = -> [Chamfer056,Cut575,Cut581]
FEATURE [Part::Cylinder] Cylinder1694  label="Válec1694"
  Angle = 360
  AttacherType = Attacher::AttachEngine3D
  Height = 160
  Placement = pos=(-18,0,-60) rot=(0,0,1;0rad)
  Radius = 17
FEATURE [Part::Cylinder] Cylinder1695  label="Válec1695"
  Angle = 360
  AttacherType = Attacher::AttachEngine3D
  Height = 100
  Placement = pos=(-34,16,-60) rot=(0,0,1;0rad)
  Radius = 1.5
FEATURE [Part::Cylinder] Cylinder1696  label="Válec1696"
  Angle = 360
  AttacherType = Attacher::AttachEngine3D
  Height = 100
  Placement = pos=(-34,-16,-60) rot=(0,0,1;0rad)
  Radius = 1.5
FEATURE [Part::Cylinder] Cylinder1697  label="Válec1697"
  Angle = 360
  AttacherType = Attacher::AttachEngine3D
  Height = 100
  Placement = pos=(34,-16,-60) rot=(0,0,1;0rad)
  Radius = 1.5
FEATURE [Part::Cylinder] Cylinder1698  label="Válec1698"
  Angle = 360
  AttacherType = Attacher::AttachEngine3D
  Height = 100
  Placement = pos=(34,16,-60) rot=(0,0,1;0rad)
  Radius = 1.5
FEATURE [Part::Cylinder] Cylinder1699  label="Válec1699"
  Angle = 360
  AttacherType = Attacher::AttachEngine3D
  Height = 100
  Placement = pos=(16,34,-60) rot=(0,0,1;0rad)
  Radius = 1.5
FEATURE [Part::Cylinder] Cylinder1700  label="Válec1700"
  Angle = 360
  AttacherType = Attacher::AttachEngine3D
  Height = 100
  Placement = pos=(10,-36,-60) rot=(0,0,1;0rad)
  Radius = 1.5
FEATURE [Part::Cylinder] Cylinder1701  label="Válec1701"
  Angle = 360
  AttacherType = Attacher::AttachEngine3D
  Height = 100
  Placement = pos=(-16,-34,-60) rot=(0,0,1;0rad)
  Radius = 1.5
FEATURE [Part::Cylinder] Cylinder1702  label="Válec1702"
  Angle = 360
  AttacherType = Attacher::AttachEngine3D
  Height = 100
  Placement = pos=(-16,34,-60) rot=(0,0,1;0rad)
  Radius = 1.5
FEATURE [Part::Cylinder] Cylinder1703  label="Válec1703"
  Angle = 360
  AttacherType = Attacher::AttachEngine3D
  Height = 16
  Placement = pos=(0,0,2) rot=(0,0,1;0rad)
  Radius = 59
FEATURE [Part::Cylinder] Cylinder1704  label="Válec1704"
  Angle = 360
  AttacherType = Attacher::AttachEngine3D
  Height = 20
  Placement = pos=(103,-12,-20) rot=(0,0,1;0rad)
  Radius = 4
FEATURE [Part::Cylinder] Cylinder1705  label="Válec1705"
  Angle = 360
  AttacherType = Attacher::AttachEngine3D
  Height = 20
  Placement = pos=(103,12,-20) rot=(0,0,1;0rad)
  Radius = 4
FEATURE [Part::Cylinder] Cylinder1706  label="Válec1706"
  Angle = 360
  AttacherType = Attacher::AttachEngine3D
  Height = 20
  Placement = pos=(76,24,-18) rot=(0,0,1;0rad)
  Radius = 4
FEATURE [Part::Cylinder] Cylinder1707  label="Válec1707"
  Angle = 360
  AttacherType = Attacher::AttachEngine3D
  Height = 20
  Placement = pos=(91,-27,-18) rot=(0,0,1;0rad)
  Radius = 4
FEATURE [Part::Cylinder] Cylinder1708  label="Válec1708"
  Angle = 360
  AttacherType = Attacher::AttachEngine3D
  Height = 40
  Placement = pos=(13,-27,-18) rot=(0,0,1;0rad)
  Radius = 4
FEATURE [Part::Cylinder] Cylinder1709  label="Válec1709"
  Angle = 360
  AttacherType = Attacher::AttachEngine3D
  Height = 40
  Placement = pos=(28,24,-18) rot=(0,0,1;0rad)
  Radius = 4
FEATURE [Part::Cylinder] Cylinder1710  label="Válec1710"
  Angle = 360
  AttacherType = Attacher::AttachEngine3D
  Height = 40
  Placement = pos=(1,-12,-18) rot=(0,0,1;0rad)
  Radius = 4
FEATURE [Part::Cylinder] Cylinder1711  label="Válec1711"
  Angle = 360
  AttacherType = Attacher::AttachEngine3D
  Height = 40
  Placement = pos=(1,12,-18) rot=(0,0,1;0rad)
  Radius = 4
FEATURE [Part::Cylinder] Cylinder1712  label="Válec1712"
  Angle = 360
  AttacherType = Attacher::AttachEngine3D
  Height = 100
  Placement = pos=(90,0,-18) rot=(0,0,1;0rad)
  Radius = 4
FEATURE [Part::Cylinder] Cylinder1713  label="Válec1713"
  Angle = 360
  AttacherType = Attacher::AttachEngine3D
  Height = 100
  Placement = pos=(14,0,-18) rot=(0,0,1;0rad)
  Radius = 4
FEATURE [Part::Cylinder] Cylinder1714  label="Válec1714"
  Angle = 360
  AttacherType = Attacher::AttachEngine3D
  Height = 100
  Placement = pos=(-16,-34,-90) rot=(0,0,1;0rad)
  Radius = 4
FEATURE [Part::Cylinder] Cylinder1715  label="Válec1715"
  Angle = 360
  AttacherType = Attacher::AttachEngine3D
  Height = 100
  Placement = pos=(-34,-16,-90) rot=(0,0,1;0rad)
  Radius = 4
FEATURE [Part::Cylinder] Cylinder1716  label="Válec1716"
  Angle = 360
  AttacherType = Attacher::AttachEngine3D
  Height = 100
  Placement = pos=(-16,34,-90) rot=(0,0,1;0rad)
  Radius = 4
FEATURE [Part::Cylinder] Cylinder1717  label="Válec1717"
  Angle = 360
  AttacherType = Attacher::AttachEngine3D
  Height = 100
  Placement = pos=(34,-16,-90) rot=(0,0,1;0rad)
  Radius = 4
FEATURE [Part::Cylinder] Cylinder1718  label="Válec1718"
  Angle = 360
  AttacherType = Attacher::AttachEngine3D
  Height = 100
  Placement = pos=(16,34,-90) rot=(0,0,1;0rad)
  Radius = 4
FEATURE [Part::Cylinder] Cylinder1719  label="Válec1719"
  Angle = 360
  AttacherType = Attacher::AttachEngine3D
  Height = 100
  Placement = pos=(10,-36,-90) rot=(0,0,1;0rad)
  Radius = 4
FEATURE [Part::Cylinder] Cylinder1720  label="Válec1720"
  Angle = 360
  AttacherType = Attacher::AttachEngine3D
  Height = 100
  Placement = pos=(-34,16,-90) rot=(0,0,1;0rad)
  Radius = 4
FEATURE [Part::Cylinder] Cylinder1721  label="Válec1721"
  Angle = 360
  AttacherType = Attacher::AttachEngine3D
  Height = 100
  Placement = pos=(34,16,-90) rot=(0,0,1;0rad)
  Radius = 4
FEATURE [Part::Cylinder] Cylinder1722  label="Válec1722"
  Angle = 360
  AttacherType = Attacher::AttachEngine3D
  Height = 4
  Placement = pos=(52,0,-26) rot=(0,0,1;0rad)
  Radius = 59
FEATURE [Part::Cylinder] Cylinder1723  label="Válec1723"
  Angle = 360
  AttacherType = Attacher::AttachEngine3D
  Height = 100
  Placement = pos=(103,-12,-60) rot=(0,0,1;0rad)
  Radius = 1.5
FEATURE [Part::Cylinder] Cylinder1724  label="Válec1724"
  Angle = 360
  AttacherType = Attacher::AttachEngine3D
  Height = 100
  Placement = pos=(103,12,-60) rot=(0,0,1;0rad)
  Radius = 1.5
FEATURE [Part::Cylinder] Cylinder1725  label="Válec1725"
  Angle = 360
  AttacherType = Attacher::AttachEngine3D
  Height = 100
  Placement = pos=(76,24,-60) rot=(0,0,1;0rad)
  Radius = 1.5
FEATURE [Part::Cylinder] Cylinder1726  label="Válec1726"
  Angle = 360
  AttacherType = Attacher::AttachEngine3D
  Height = 100
  Placement = pos=(91,-27,-60) rot=(0,0,1;0rad)
  Radius = 1.5
FEATURE [Part::Cylinder] Cylinder1727  label="Válec1727"
  Angle = 360
  AttacherType = Attacher::AttachEngine3D
  Height = 100
  Placement = pos=(13,-27,-60) rot=(0,0,1;0rad)
  Radius = 1.5
FEATURE [Part::Cylinder] Cylinder1728  label="Válec1728"
  Angle = 360
  AttacherType = Attacher::AttachEngine3D
  Height = 100
  Placement = pos=(28,24,-60) rot=(0,0,1;0rad)
  Radius = 1.5
FEATURE [Part::Cylinder] Cylinder1729  label="Válec1729"
  Angle = 360
  AttacherType = Attacher::AttachEngine3D
  Height = 100
  Placement = pos=(1,-12,-60) rot=(0,0,1;0rad)
  Radius = 1.5
FEATURE [Part::Cylinder] Cylinder1730  label="Válec1730"
  Angle = 360
  AttacherType = Attacher::AttachEngine3D
  Height = 100
  Placement = pos=(1,12,-60) rot=(0,0,1;0rad)
  Radius = 1.5
FEATURE [Part::Box] Box543  label="Krychle543"
  AttacherType = Attacher::AttachEngine3D
  Height = 100
  Length = 200
  Placement = pos=(-60,-130,-90) rot=(0,0,1;0rad)
  Width = 100
FEATURE [Part::Box] Box544  label="Krychle544"
  AttacherType = Attacher::AttachEngine3D
  Height = 100
  Length = 200
  Placement = pos=(-60,44,-90) rot=(0,0,1;0rad)
  Width = 100
FEATURE [Part::Cylinder] Cylinder1731  label="Válec1731"
  Angle = 360
  AttacherType = Attacher::AttachEngine3D
  Height = 100
  Placement = pos=(-34,-16,-90) rot=(0,0,1;0rad)
  Radius = 4
FEATURE [Part::Cylinder] Cylinder1732  label="Válec1732"
  Angle = 360
  AttacherType = Attacher::AttachEngine3D
  Height = 100
  Placement = pos=(-16,34,-90) rot=(0,0,1;0rad)
  Radius = 4
FEATURE [Part::Cylinder] Cylinder1733  label="Válec1733"
  Angle = 360
  AttacherType = Attacher::AttachEngine3D
  Height = 100
  Placement = pos=(-16,-34,-90) rot=(0,0,1;0rad)
  Radius = 4
FEATURE [Part::Cylinder] Cylinder1734  label="Válec1734"
  Angle = 360
  AttacherType = Attacher::AttachEngine3D
  Height = 100
  Placement = pos=(34,-16,-90) rot=(0,0,1;0rad)
  Radius = 4
FEATURE [Part::Cylinder] Cylinder1735  label="Válec1735"
  Angle = 360
  AttacherType = Attacher::AttachEngine3D
  Height = 100
  Placement = pos=(16,34,-90) rot=(0,0,1;0rad)
  Radius = 4
FEATURE [Part::Cylinder] Cylinder1736  label="Válec1736"
  Angle = 360
  AttacherType = Attacher::AttachEngine3D
  Height = 100
  Placement = pos=(16,-34,-90) rot=(0,0,1;0rad)
  Radius = 4
FEATURE [Part::Cylinder] Cylinder1737  label="Válec1737"
  Angle = 360
  AttacherType = Attacher::AttachEngine3D
  Height = 100
  Placement = pos=(-34,16,-90) rot=(0,0,1;0rad)
  Radius = 4
FEATURE [Part::Cylinder] Cylinder1738  label="Válec1738"
  Angle = 360
  AttacherType = Attacher::AttachEngine3D
  Height = 100
  Placement = pos=(34,16,-90) rot=(0,0,1;0rad)
  Radius = 4
FEATURE [Part::Cylinder] Cylinder1739  label="Válec1739"
  Angle = 360
  AttacherType = Attacher::AttachEngine3D
  Height = 32
  Placement = pos=(26,41,-42) rot=(0,0,1;0rad)
  Radius = 1.5
FEATURE [Part::Cylinder] Cylinder1740  label="Válec1740"
  Angle = 360
  AttacherType = Attacher::AttachEngine3D
  Height = 32
  Placement = pos=(78,41,-42) rot=(0,0,1;0rad)
  Radius = 1.5
FEATURE [Part::Cylinder] Cylinder1741  label="Válec1741"
  Angle = 360
  AttacherType = Attacher::AttachEngine3D
  Height = 100
  Placement = pos=(90,0,-60) rot=(0,0,1;0rad)
  Radius = 1.5
FEATURE [Part::Cylinder] Cylinder1742  label="Válec1742"
  Angle = 360
  AttacherType = Attacher::AttachEngine3D
  Height = 100
  Placement = pos=(14,0,-60) rot=(0,0,1;0rad)
  Radius = 1.5
FEATURE [Sketcher::SketchObject] Sketch013
  FullyConstrained = false
  sketch-geometry (1):
    g0: Circle CenterX=-186.411 CenterY=73.9277 CenterZ=0 NormalX=0 NormalY=0 NormalZ=1 AngleXU=0 Radius=59
FEATURE [Part::Extrusion] Extrude011
  Base = -> Sketch013
  Dir = (52,0,32)
  DirMode = 0
  FaceMakerClass = Part::FaceMakerBullseye
  LengthFwd = 61
  LengthRev = 0
  Placement = pos=(-134.5,74,-22) rot=(0,0,1;3.14159rad)
  Solid = true
  Symmetric = false
FEATURE [Part::Compound] Compound938  label="sbouby_baze010"
  Links = -> [Cylinder1695,Cylinder1696,Cylinder1697,Cylinder1698,Cylinder1699,Cylinder1700,Cylinder1701,Cylinder1702]
FEATURE [Part::Compound] Compound939  label="srouby_monoblok_silne011"
  Links = -> [Cylinder1704,Cylinder1705,Cylinder1706,Cylinder1707,Cylinder1708,Cylinder1709,Cylinder1710,Cylinder1711]
FEATURE [Part::Cut] Cut593
  Base = -> Cylinder1703
  Tool = -> Compound939
FEATURE [Part::Compound] Compound940  label="sbouby_baze_silne014"
  Links = -> [Cylinder1715,Cylinder1716,Cylinder1714,Cylinder1717,Cylinder1718,Cylinder1719,Cylinder1720,Cylinder1721]
FEATURE [Part::Cut] Cut594
  Base = -> Cut593
  Tool = -> Compound940
FEATURE [Part::Cut] Cut595
  Base = -> Cut594
  Tool = -> Compound938
FEATURE [Part::Chamfer] Chamfer059
  Base = -> Cut595
  Edges = 1 edges r=4: [Edge3]
FEATURE [Part::Compound] Compound941  label="srouby_troj_silne008"
  Links = -> [Cylinder1712,Cylinder1713]
FEATURE [Part::Cut] Cut596
  Base = -> Chamfer059
  Placement = pos=(0,0,4) rot=(0,0,1;0rad)
  Tool = -> Compound941
FEATURE [Part::Cut] Cut585
  Base = -> Cut596
  Tool = -> Cylinder1694
FEATURE [Part::Fillet] Fillet003
  Base = -> Cut585
  Edges = 1 edges r=4: [Edge10]
FEATURE [Part::Compound] Compound942  label="srouby_monoblok010"
  Links = -> [Cylinder1723,Cylinder1724,Cylinder1725,Cylinder1726,Cylinder1727,Cylinder1728,Cylinder1729,Cylinder1730]
FEATURE [Part::Cut] Cut597
  Base = -> Cylinder1722
  Tool = -> Compound942
FEATURE [Part::Compound] Compound943  label="sbouby_baze_silne015"
  Links = -> [Cylinder1731,Cylinder1732,Cylinder1733,Cylinder1734,Cylinder1735,Cylinder1736,Cylinder1737,Cylinder1738]
FEATURE [Part::Cut] Cut598
  Base = -> Cut597
  Tool = -> Compound943
FEATURE [Part::Cut] Cut599
  Base = -> Cut598
  Tool = -> Box543
FEATURE [Part::Cut] Cut600
  Base = -> Cut599
  Tool = -> Box544
FEATURE [Part::Compound] Compound944
  Links = -> [Cylinder1739,Cylinder1740]
FEATURE [Part::Cut] Cut601
  Base = -> Cut600
  Tool = -> Compound944
FEATURE [Part::Compound] Compound945  label="srouby_troj008"
  Links = -> [Cylinder1741,Cylinder1742]
FEATURE [Part::Cut] Cut602
  Base = -> Cut601
  Tool = -> Compound945
FEATURE [Part::Cylinder] Cylinder1743  label="Válec1743"
  Angle = 360
  AttacherType = Attacher::AttachEngine3D
  Height = 100
  Placement = pos=(-16,34,-90) rot=(0,0,1;0rad)
  Radius = 4
FEATURE [Part::Cylinder] Cylinder1744  label="Válec1744"
  Angle = 360
  AttacherType = Attacher::AttachEngine3D
  Height = 100
  Placement = pos=(-34,-16,-90) rot=(0,0,1;0rad)
  Radius = 4
FEATURE [Part::Cylinder] Cylinder1745  label="Válec1745"
  Angle = 360
  AttacherType = Attacher::AttachEngine3D
  Height = 100
  Placement = pos=(16,34,-90) rot=(0,0,1;0rad)
  Radius = 4
FEATURE [Part::Cylinder] Cylinder1746  label="Válec1746"
  Angle = 360
  AttacherType = Attacher::AttachEngine3D
  Height = 160
  Placement = pos=(-18,0,-60) rot=(0,0,1;0rad)
  Radius = 17
FEATURE [Part::Cut] Cut586
  Base = -> Cut602
  Tool = -> Cylinder1746
FEATURE [Part::Fillet] Fillet001
  Base = -> Cut586
  Edges = 1 edges r=8: [Edge55]
FEATURE [Part::Fillet] Fillet002
  Base = -> Fillet001
  Edges = 1 edges r=8: [Edge38]
FEATURE [Part::Cylinder] Cylinder1747  label="Válec1747"
  Angle = 360
  AttacherType = Attacher::AttachEngine3D
  Height = 160
  Placement = pos=(-18,0,-60) rot=(0,0,1;0rad)
  Radius = 17
FEATURE [Part::Cylinder] Cylinder1748  label="Válec1748"
  Angle = 360
  AttacherType = Attacher::AttachEngine3D
  Height = 100
  Placement = pos=(34,-16,-90) rot=(0,0,1;0rad)
  Radius = 4
FEATURE [Part::Cylinder] Cylinder1749  label="Válec1749"
  Angle = 360
  AttacherType = Attacher::AttachEngine3D
  Height = 100
  Placement = pos=(-16,-34,-90) rot=(0,0,1;0rad)
  Radius = 4
FEATURE [Part::Cylinder] Cylinder1750  label="Válec1750"
  Angle = 360
  AttacherType = Attacher::AttachEngine3D
  Height = 100
  Placement = pos=(10,-36,-90) rot=(0,0,1;0rad)
  Radius = 4
FEATURE [Part::Cylinder] Cylinder1751  label="Válec1751"
  Angle = 360
  AttacherType = Attacher::AttachEngine3D
  Height = 100
  Placement = pos=(16,34,-60) rot=(0,0,1;0rad)
  Radius = 1.5
FEATURE [Part::Cylinder] Cylinder1752  label="Válec1752"
  Angle = 360
  AttacherType = Attacher::AttachEngine3D
  Height = 100
  Placement = pos=(-34,16,-60) rot=(0,0,1;0rad)
  Radius = 1.5
FEATURE [Part::Cylinder] Cylinder1753  label="Válec1753"
  Angle = 360
  AttacherType = Attacher::AttachEngine3D
  Height = 100
  Placement = pos=(-34,-16,-60) rot=(0,0,1;0rad)
  Radius = 1.5
FEATURE [Part::Cylinder] Cylinder1754  label="Válec1754"
  Angle = 360
  AttacherType = Attacher::AttachEngine3D
  Height = 100
  Placement = pos=(34,-16,-60) rot=(0,0,1;0rad)
  Radius = 1.5
FEATURE [Part::Cylinder] Cylinder1755  label="Válec1755"
  Angle = 360
  AttacherType = Attacher::AttachEngine3D
  Height = 100
  Placement = pos=(34,16,-60) rot=(0,0,1;0rad)
  Radius = 1.5
FEATURE [Part::Cylinder] Cylinder1756  label="Válec1756"
  Angle = 360
  AttacherType = Attacher::AttachEngine3D
  Height = 100
  Placement = pos=(10,-36,-60) rot=(0,0,1;0rad)
  Radius = 1.5
FEATURE [Part::Box] Box545  label="Krychle545"
  AttacherType = Attacher::AttachEngine3D
  Height = 100
  Length = 200
  Placement = pos=(-60,-134,-90) rot=(0,0,1;0rad)
  Width = 100
FEATURE [Part::Box] Box546  label="Krychle546"
  AttacherType = Attacher::AttachEngine3D
  Height = 100
  Length = 200
  Placement = pos=(-60,44,-90) rot=(0,0,1;0rad)
  Width = 100
FEATURE [Part::Cylinder] Cylinder1757  label="Válec1757"
  Angle = 360
  AttacherType = Attacher::AttachEngine3D
  Height = 100
  Placement = pos=(90,0,-60) rot=(0,0,1;0rad)
  Radius = 1.5
FEATURE [Part::Cylinder] Cylinder1758  label="Válec1758"
  Angle = 360
  AttacherType = Attacher::AttachEngine3D
  Height = 100
  Placement = pos=(14,0,-60) rot=(0,0,1;0rad)
  Radius = 1.5
FEATURE [Part::Cylinder] Cylinder1759  label="Válec1759"
  Angle = 360
  AttacherType = Attacher::AttachEngine3D
  Height = 100
  Placement = pos=(90,0,-18) rot=(0,0,1;0rad)
  Radius = 4
FEATURE [Part::Cylinder] Cylinder1760  label="Válec1760"
  Angle = 360
  AttacherType = Attacher::AttachEngine3D
  Height = 100
  Placement = pos=(14,0,-18) rot=(0,0,1;0rad)
  Radius = 4
FEATURE [Part::Box] Box547  label="Krychle547"
  AttacherType = Attacher::AttachEngine3D
  Height = 2
  Length = 6
  Placement = pos=(75,38,-22) rot=(0,0,1;0rad)
  Width = 6
FEATURE [Part::Box] Box548  label="Krychle548"
  AttacherType = Attacher::AttachEngine3D
  Height = 2
  Length = 6
  Placement = pos=(23,38,-22) rot=(0,0,1;0rad)
  Width = 6
FEATURE [Part::Cylinder] Cylinder1761  label="Válec1761"
  Angle = 360
  AttacherType = Attacher::AttachEngine3D
  Height = 32
  Placement = pos=(26,41,-46) rot=(0,0,1;0rad)
  Radius = 1.5
FEATURE [Part::Cylinder] Cylinder1762  label="Válec1762"
  Angle = 360
  AttacherType = Attacher::AttachEngine3D
  Height = 32
  Placement = pos=(78,41,-46) rot=(0,0,1;0rad)
  Radius = 1.5
FEATURE [Part::Cylinder] Cylinder1763  label="Válec1763"
  Angle = 360
  AttacherType = Attacher::AttachEngine3D
  Height = 100
  Placement = pos=(-34,16,-90) rot=(0,0,1;0rad)
  Radius = 4
FEATURE [Part::Cylinder] Cylinder1764  label="Válec1764"
  Angle = 360
  AttacherType = Attacher::AttachEngine3D
  Height = 100
  Placement = pos=(34,16,-90) rot=(0,0,1;0rad)
  Radius = 4
FEATURE [Part::Cylinder] Cylinder1765  label="Válec1765"
  Angle = 360
  AttacherType = Attacher::AttachEngine3D
  Height = 100
  Placement = pos=(-16,-34,-60) rot=(0,0,1;0rad)
  Radius = 1.5
FEATURE [Part::Cylinder] Cylinder1766  label="Válec1766"
  Angle = 360
  AttacherType = Attacher::AttachEngine3D
  Height = 100
  Placement = pos=(-16,34,-60) rot=(0,0,1;0rad)
  Radius = 1.5
FEATURE [Part::Cylinder] Cylinder1767  label="Válec1767"
  Angle = 360
  AttacherType = Attacher::AttachEngine3D
  Height = 100
  Placement = pos=(103,-12,-60) rot=(0,0,1;0rad)
  Radius = 1.5
FEATURE [Part::Cylinder] Cylinder1768  label="Válec1768"
  Angle = 360
  AttacherType = Attacher::AttachEngine3D
  Height = 100
  Placement = pos=(103,12,-60) rot=(0,0,1;0rad)
  Radius = 1.5
FEATURE [Part::Cylinder] Cylinder1769  label="Válec1769"
  Angle = 360
  AttacherType = Attacher::AttachEngine3D
  Height = 100
  Placement = pos=(76,24,-60) rot=(0,0,1;0rad)
  Radius = 1.5
FEATURE [Part::Cylinder] Cylinder1770  label="Válec1770"
  Angle = 360
  AttacherType = Attacher::AttachEngine3D
  Height = 100
  Placement = pos=(91,-27,-60) rot=(0,0,1;0rad)
  Radius = 1.5
FEATURE [Part::Cylinder] Cylinder1771  label="Válec1771"
  Angle = 360
  AttacherType = Attacher::AttachEngine3D
  Height = 100
  Placement = pos=(13,-27,-60) rot=(0,0,1;0rad)
  Radius = 1.5
FEATURE [Part::Cylinder] Cylinder1772  label="Válec1772"
  Angle = 360
  AttacherType = Attacher::AttachEngine3D
  Height = 100
  Placement = pos=(28,24,-60) rot=(0,0,1;0rad)
  Radius = 1.5
FEATURE [Part::Cylinder] Cylinder1773  label="Válec1773"
  Angle = 360
  AttacherType = Attacher::AttachEngine3D
  Height = 100
  Placement = pos=(1,-12,-60) rot=(0,0,1;0rad)
  Radius = 1.5
FEATURE [Part::Cylinder] Cylinder1774  label="Válec1774"
  Angle = 360
  AttacherType = Attacher::AttachEngine3D
  Height = 100
  Placement = pos=(1,12,-60) rot=(0,0,1;0rad)
  Radius = 1.5
FEATURE [Part::Cylinder] Cylinder1775  label="Válec1775"
  Angle = 360
  AttacherType = Attacher::AttachEngine3D
  Height = 20
  Placement = pos=(103,-12,-20) rot=(0,0,1;0rad)
  Radius = 4
FEATURE [Part::Cylinder] Cylinder1776  label="Válec1776"
  Angle = 360
  AttacherType = Attacher::AttachEngine3D
  Height = 20
  Placement = pos=(103,12,-20) rot=(0,0,1;0rad)
  Radius = 4
FEATURE [Part::Cylinder] Cylinder1777  label="Válec1777"
  Angle = 360
  AttacherType = Attacher::AttachEngine3D
  Height = 20
  Placement = pos=(76,24,-18) rot=(0,0,1;0rad)
  Radius = 4
FEATURE [Part::Cylinder] Cylinder1778  label="Válec1778"
  Angle = 360
  AttacherType = Attacher::AttachEngine3D
  Height = 20
  Placement = pos=(91,-27,-18) rot=(0,0,1;0rad)
  Radius = 4
FEATURE [Part::Cylinder] Cylinder1779  label="Válec1779"
  Angle = 360
  AttacherType = Attacher::AttachEngine3D
  Height = 40
  Placement = pos=(13,-27,-18) rot=(0,0,1;0rad)
  Radius = 4
FEATURE [Part::Cylinder] Cylinder1780  label="Válec1780"
  Angle = 360
  AttacherType = Attacher::AttachEngine3D
  Height = 40
  Placement = pos=(28,24,-18) rot=(0,0,1;0rad)
  Radius = 4
FEATURE [Part::Cylinder] Cylinder1781  label="Válec1781"
  Angle = 360
  AttacherType = Attacher::AttachEngine3D
  Height = 40
  Placement = pos=(1,-12,-18) rot=(0,0,1;0rad)
  Radius = 4
FEATURE [Part::Cylinder] Cylinder1782  label="Válec1782"
  Angle = 360
  AttacherType = Attacher::AttachEngine3D
  Height = 40
  Placement = pos=(1,12,-18) rot=(0,0,1;0rad)
  Radius = 4
FEATURE [Part::Compound] Compound946  label="srouby_monoblok_silne012"
  Links = -> [Cylinder1775,Cylinder1776,Cylinder1777,Cylinder1778,Cylinder1779,Cylinder1780,Cylinder1781,Cylinder1782]
FEATURE [Part::Compound] Compound947  label="srouby_monoblok011"
  Links = -> [Cylinder1767,Cylinder1768,Cylinder1769,Cylinder1770,Cylinder1771,Cylinder1772,Cylinder1773,Cylinder1774]
FEATURE [Part::Cut] Cut584
  Base = -> Extrude011
  Tool = -> Compound947
FEATURE [Part::Cut] Cut589
  Base = -> Cut584
  Tool = -> Compound946
FEATURE [Part::Compound] Compound948  label="sbouby_baze_silne016"
  Links = -> [Cylinder1744,Cylinder1743,Cylinder1749,Cylinder1748,Cylinder1745,Cylinder1750,Cylinder1763,Cylinder1764]
FEATURE [Part::Cut] Cut587
  Base = -> Cut589
  Tool = -> Compound948
FEATURE [Part::Compound] Compound949  label="sbouby_baze011"
  Links = -> [Cylinder1752,Cylinder1753,Cylinder1754,Cylinder1755,Cylinder1751,Cylinder1756,Cylinder1765,Cylinder1766]
FEATURE [Part::Cut] Cut591
  Base = -> Cut587
  Tool = -> Compound949
FEATURE [Part::Cut] Cut592
  Base = -> Cut591
  Tool = -> Box545
FEATURE [Part::Cut] Cut590
  Base = -> Cut592
  Tool = -> Box546
FEATURE [Part::Compound] Compound950
  Links = -> [Box547,Box548]
FEATURE [Part::Cut] Cut588
  Base = -> Cut590
  Tool = -> Compound950
FEATURE [Part::Compound] Compound951
  Links = -> [Cylinder1761,Cylinder1762]
FEATURE [Part::Cut] Cut603
  Base = -> Cut588
  Tool = -> Compound951
FEATURE [Part::Compound] Compound952  label="srouby_troj_silne009"
  Links = -> [Cylinder1759,Cylinder1760]
FEATURE [Part::Compound] Compound953  label="srouby_troj009"
  Links = -> [Cylinder1757,Cylinder1758]
FEATURE [Part::Cut] Cut604
  Base = -> Cut603
  Tool = -> Compound953
FEATURE [Part::Cut] Cut582
  Base = -> Cut604
  Tool = -> Compound952
FEATURE [Part::Chamfer] Chamfer060
  Base = -> Cut582
  Edges = 1 edges r=4: [Edge44]
FEATURE [Part::Chamfer] Chamfer057
  Base = -> Chamfer060
  Edges = 1 edges r=3: [Edge6]
FEATURE [Part::Chamfer] Chamfer058
  Base = -> Chamfer057
  Edges = 1 edges r=3: [Edge7]
FEATURE [Part::Cut] Cut583
  Base = -> Chamfer058
  Tool = -> Cylinder1747
FEATURE [Part::Fillet] Fillet
  Base = -> Cut583
  Edges = 2 edges r=3: [Edge4,Edge36]
FEATURE [Part::Compound] Compound937  label="Base_deep-neck-holed"
  Links = -> [Fillet,Fillet002,Fillet003]
FEATURE [Sketcher::SketchObject] Sketch014
  FullyConstrained = false
  sketch-geometry (1):
    g0: Circle CenterX=-186.411 CenterY=73.9277 CenterZ=0 NormalX=0 NormalY=0 NormalZ=1 AngleXU=0 Radius=59
FEATURE [Part::Cylinder] Cylinder1783  label="Válec1783"
  Angle = 360
  AttacherType = Attacher::AttachEngine3D
  Height = 100
  Placement = pos=(16,34,-90) rot=(0,0,1;0rad)
  Radius = 4
FEATURE [Part::Cylinder] Cylinder1784  label="Válec1784"
  Angle = 360
  AttacherType = Attacher::AttachEngine3D
  Height = 100
  Placement = pos=(-34,16,-90) rot=(0,0,1;0rad)
  Radius = 4
FEATURE [Part::Cylinder] Cylinder1785  label="Válec1785"
  Angle = 360
  AttacherType = Attacher::AttachEngine3D
  Height = 100
  Placement = pos=(10,-36,-90) rot=(0,0,1;0rad)
  Radius = 4
FEATURE [Part::Cylinder] Cylinder1786  label="Válec1786"
  Angle = 360
  AttacherType = Attacher::AttachEngine3D
  Height = 100
  Placement = pos=(34,16,-90) rot=(0,0,1;0rad)
  Radius = 4
FEATURE [Part::Cylinder] Cylinder1787  label="Válec1787"
  Angle = 360
  AttacherType = Attacher::AttachEngine3D
  Height = 100
  Placement = pos=(34,-16,-90) rot=(0,0,1;0rad)
  Radius = 4
FEATURE [Part::Cylinder] Cylinder1788  label="Válec1788"
  Angle = 360
  AttacherType = Attacher::AttachEngine3D
  Height = 100
  Placement = pos=(-16,-34,-90) rot=(0,0,1;0rad)
  Radius = 4
FEATURE [Part::Cylinder] Cylinder1789  label="Válec1789"
  Angle = 360
  AttacherType = Attacher::AttachEngine3D
  Height = 100
  Placement = pos=(14,0,-18) rot=(0,0,1;0rad)
  Radius = 4
FEATURE [Part::Cylinder] Cylinder1790  label="Válec1790"
  Angle = 360
  AttacherType = Attacher::AttachEngine3D
  Height = 100
  Placement = pos=(90,0,-18) rot=(0,0,1;0rad)
  Radius = 4
FEATURE [Part::Cylinder] Cylinder1791  label="Válec1791"
  Angle = 360
  AttacherType = Attacher::AttachEngine3D
  Height = 40
  Placement = pos=(1,12,-18) rot=(0,0,1;0rad)
  Radius = 4
FEATURE [Part::Cylinder] Cylinder1792  label="Válec1792"
  Angle = 360
  AttacherType = Attacher::AttachEngine3D
  Height = 40
  Placement = pos=(1,-12,-18) rot=(0,0,1;0rad)
  Radius = 4
FEATURE [Part::Cylinder] Cylinder1793  label="Válec1793"
  Angle = 360
  AttacherType = Attacher::AttachEngine3D
  Height = 40
  Placement = pos=(28,24,-18) rot=(0,0,1;0rad)
  Radius = 4
FEATURE [Part::Cylinder] Cylinder1794  label="Válec1794"
  Angle = 360
  AttacherType = Attacher::AttachEngine3D
  Height = 40
  Placement = pos=(13,-27,-18) rot=(0,0,1;0rad)
  Radius = 4
FEATURE [Part::Cylinder] Cylinder1795  label="Válec1795"
  Angle = 360
  AttacherType = Attacher::AttachEngine3D
  Height = 20
  Placement = pos=(91,-27,-18) rot=(0,0,1;0rad)
  Radius = 4
FEATURE [Part::Cylinder] Cylinder1796  label="Válec1796"
  Angle = 360
  AttacherType = Attacher::AttachEngine3D
  Height = 20
  Placement = pos=(76,24,-18) rot=(0,0,1;0rad)
  Radius = 4
FEATURE [Part::Cylinder] Cylinder1797  label="Válec1797"
  Angle = 360
  AttacherType = Attacher::AttachEngine3D
  Height = 20
  Placement = pos=(103,12,-20) rot=(0,0,1;0rad)
  Radius = 4
FEATURE [Part::Cylinder] Cylinder1798  label="Válec1798"
  Angle = 360
  AttacherType = Attacher::AttachEngine3D
  Height = 16
  Placement = pos=(0,0,2) rot=(0,0,1;0rad)
  Radius = 59
FEATURE [Part::Cylinder] Cylinder1799  label="Válec1799"
  Angle = 360
  AttacherType = Attacher::AttachEngine3D
  Height = 100
  Placement = pos=(1,12,-60) rot=(0,0,1;0rad)
  Radius = 1.5
FEATURE [Part::Cylinder] Cylinder1800  label="Válec1800"
  Angle = 360
  AttacherType = Attacher::AttachEngine3D
  Height = 100
  Placement = pos=(-16,-34,-90) rot=(0,0,1;0rad)
  Radius = 4
FEATURE [Part::Cylinder] Cylinder1801  label="Válec1801"
  Angle = 360
  AttacherType = Attacher::AttachEngine3D
  Height = 100
  Placement = pos=(-34,16,-90) rot=(0,0,1;0rad)
  Radius = 4
FEATURE [Part::Cylinder] Cylinder1802  label="Válec1802"
  Angle = 360
  AttacherType = Attacher::AttachEngine3D
  Height = 32
  Placement = pos=(26,41,-42) rot=(0,0,1;0rad)
  Radius = 1.5
FEATURE [Part::Cylinder] Cylinder1803  label="Válec1803"
  Angle = 360
  AttacherType = Attacher::AttachEngine3D
  Height = 100
  Placement = pos=(-16,34,-60) rot=(0,0,1;0rad)
  Radius = 1.5
FEATURE [Part::Cylinder] Cylinder1804  label="Válec1804"
  Angle = 360
  AttacherType = Attacher::AttachEngine3D
  Height = 100
  Placement = pos=(-16,-34,-60) rot=(0,0,1;0rad)
  Radius = 1.5
FEATURE [Part::Cylinder] Cylinder1805  label="Válec1805"
  Angle = 360
  AttacherType = Attacher::AttachEngine3D
  Height = 100
  Placement = pos=(10,-36,-60) rot=(0,0,1;0rad)
  Radius = 1.5
FEATURE [Part::Cylinder] Cylinder1806  label="Válec1806"
  Angle = 360
  AttacherType = Attacher::AttachEngine3D
  Height = 100
  Placement = pos=(16,34,-60) rot=(0,0,1;0rad)
  Radius = 1.5
FEATURE [Part::Cylinder] Cylinder1807  label="Válec1807"
  Angle = 360
  AttacherType = Attacher::AttachEngine3D
  Height = 100
  Placement = pos=(1,-12,-60) rot=(0,0,1;0rad)
  Radius = 1.5
FEATURE [Part::Cylinder] Cylinder1808  label="Válec1808"
  Angle = 360
  AttacherType = Attacher::AttachEngine3D
  Height = 100
  Placement = pos=(28,24,-60) rot=(0,0,1;0rad)
  Radius = 1.5
FEATURE [Part::Cylinder] Cylinder1809  label="Válec1809"
  Angle = 360
  AttacherType = Attacher::AttachEngine3D
  Height = 100
  Placement = pos=(-34,-16,-60) rot=(0,0,1;0rad)
  Radius = 1.5
FEATURE [Part::Cylinder] Cylinder1810  label="Válec1810"
  Angle = 360
  AttacherType = Attacher::AttachEngine3D
  Height = 32
  Placement = pos=(78,41,-42) rot=(0,0,1;0rad)
  Radius = 1.5
FEATURE [Part::Cylinder] Cylinder1811  label="Válec1811"
  Angle = 360
  AttacherType = Attacher::AttachEngine3D
  Height = 100
  Placement = pos=(34,16,-90) rot=(0,0,1;0rad)
  Radius = 4
FEATURE [Part::Cylinder] Cylinder1812  label="Válec1812"
  Angle = 360
  AttacherType = Attacher::AttachEngine3D
  Height = 100
  Placement = pos=(16,-34,-90) rot=(0,0,1;0rad)
  Radius = 4
FEATURE [Part::Cylinder] Cylinder1813  label="Válec1813"
  Angle = 360
  AttacherType = Attacher::AttachEngine3D
  Height = 100
  Placement = pos=(-16,34,-90) rot=(0,0,1;0rad)
  Radius = 4
FEATURE [Part::Cylinder] Cylinder1814  label="Válec1814"
  Angle = 360
  AttacherType = Attacher::AttachEngine3D
  Height = 100
  Placement = pos=(-34,-16,-90) rot=(0,0,1;0rad)
  Radius = 4
FEATURE [Part::Cylinder] Cylinder1815  label="Válec1815"
  Angle = 360
  AttacherType = Attacher::AttachEngine3D
  Height = 100
  Placement = pos=(16,34,-90) rot=(0,0,1;0rad)
  Radius = 4
FEATURE [Part::Cylinder] Cylinder1816  label="Válec1816"
  Angle = 360
  AttacherType = Attacher::AttachEngine3D
  Height = 100
  Placement = pos=(34,-16,-90) rot=(0,0,1;0rad)
  Radius = 4
FEATURE [Part::Cylinder] Cylinder1817  label="Válec1817"
  Angle = 360
  AttacherType = Attacher::AttachEngine3D
  Height = 20
  Placement = pos=(103,-12,-20) rot=(0,0,1;0rad)
  Radius = 4
FEATURE [Part::Box] Box549  label="Krychle549"
  AttacherType = Attacher::AttachEngine3D
  Height = 100
  Length = 200
  Placement = pos=(-60,44,-90) rot=(0,0,1;0rad)
  Width = 100
FEATURE [Part::Box] Box550  label="Krychle550"
  AttacherType = Attacher::AttachEngine3D
  Height = 100
  Length = 200
  Placement = pos=(-60,-130,-90) rot=(0,0,1;0rad)
  Width = 100
FEATURE [Part::Cylinder] Cylinder1818  label="Válec1818"
  Angle = 360
  AttacherType = Attacher::AttachEngine3D
  Height = 100
  Placement = pos=(13,-27,-60) rot=(0,0,1;0rad)
  Radius = 1.5
FEATURE [Part::Cylinder] Cylinder1819  label="Válec1819"
  Angle = 360
  AttacherType = Attacher::AttachEngine3D
  Height = 100
  Placement = pos=(91,-27,-60) rot=(0,0,1;0rad)
  Radius = 1.5
FEATURE [Part::Cylinder] Cylinder1820  label="Válec1820"
  Angle = 360
  AttacherType = Attacher::AttachEngine3D
  Height = 100
  Placement = pos=(76,24,-60) rot=(0,0,1;0rad)
  Radius = 1.5
FEATURE [Part::Cylinder] Cylinder1821  label="Válec1821"
  Angle = 360
  AttacherType = Attacher::AttachEngine3D
  Height = 100
  Placement = pos=(103,12,-60) rot=(0,0,1;0rad)
  Radius = 1.5
FEATURE [Part::Cylinder] Cylinder1822  label="Válec1822"
  Angle = 360
  AttacherType = Attacher::AttachEngine3D
  Height = 100
  Placement = pos=(103,-12,-60) rot=(0,0,1;0rad)
  Radius = 1.5
FEATURE [Part::Cylinder] Cylinder1823  label="Válec1823"
  Angle = 360
  AttacherType = Attacher::AttachEngine3D
  Height = 4
  Placement = pos=(52,0,-26) rot=(0,0,1;0rad)
  Radius = 59
FEATURE [Part::Cylinder] Cylinder1824  label="Válec1824"
  Angle = 360
  AttacherType = Attacher::AttachEngine3D
  Height = 100
  Placement = pos=(34,16,-60) rot=(0,0,1;0rad)
  Radius = 1.5
FEATURE [Part::Cylinder] Cylinder1825  label="Válec1825"
  Angle = 360
  AttacherType = Attacher::AttachEngine3D
  Height = 100
  Placement = pos=(34,-16,-60) rot=(0,0,1;0rad)
  Radius = 1.5
FEATURE [Part::Cylinder] Cylinder1826  label="Válec1826"
  Angle = 360
  AttacherType = Attacher::AttachEngine3D
  Height = 100
  Placement = pos=(-16,34,-90) rot=(0,0,1;0rad)
  Radius = 4
FEATURE [Part::Cylinder] Cylinder1827  label="Válec1827"
  Angle = 360
  AttacherType = Attacher::AttachEngine3D
  Height = 100
  Placement = pos=(-34,-16,-90) rot=(0,0,1;0rad)
  Radius = 4
FEATURE [Part::Cylinder] Cylinder1828  label="Válec1828"
  Angle = 360
  AttacherType = Attacher::AttachEngine3D
  Height = 100
  Placement = pos=(-34,16,-60) rot=(0,0,1;0rad)
  Radius = 1.5
FEATURE [Part::Cylinder] Cylinder1829  label="Válec1829"
  Angle = 360
  AttacherType = Attacher::AttachEngine3D
  Height = 100
  Placement = pos=(90,0,-60) rot=(0,0,1;0rad)
  Radius = 1.5
FEATURE [Part::Extrusion] Extrude012
  Base = -> Sketch014
  Dir = (40,0,32)
  DirMode = 0
  FaceMakerClass = Part::FaceMakerBullseye
  LengthFwd = 67
  LengthRev = 0
  Placement = pos=(-134.5,74,-22) rot=(0,0,1;3.14159rad)
  Solid = true
  Symmetric = false
FEATURE [Part::Compound] Compound954  label="sbouby_baze012"
  Links = -> [Cylinder1828,Cylinder1809,Cylinder1825,Cylinder1824,Cylinder1806,Cylinder1805,Cylinder1804,Cylinder1803]
FEATURE [Part::Compound] Compound955  label="srouby_monoblok_silne013"
  Links = -> [Cylinder1817,Cylinder1797,Cylinder1796,Cylinder1795,Cylinder1794,Cylinder1793,Cylinder1792,Cylinder1791]
FEATURE [Part::Compound] Compound956  label="sbouby_baze_silne017"
  Links = -> [Cylinder1827,Cylinder1826,Cylinder1788,Cylinder1787,Cylinder1783,Cylinder1785,Cylinder1784,Cylinder1786]
FEATURE [Part::Compound] Compound957  label="srouby_troj_silne010"
  Links = -> [Cylinder1790,Cylinder1789]
FEATURE [Part::Cut] Cut614
  Base = -> Cylinder1798
  Tool = -> Compound955
FEATURE [Part::Cut] Cut615
  Base = -> Cut614
  Tool = -> Compound956
FEATURE [Part::Cut] Cut619
  Base = -> Cut615
  Tool = -> Compound954
FEATURE [Part::Chamfer] Chamfer061
  Base = -> Cut619
  Edges = 1 edges r=4: [Edge3]
FEATURE [Part::Cut] Cut620
  Base = -> Chamfer061
  Placement = pos=(-0.5,0,14) rot=(0,0,1;0rad)
  Tool = -> Compound957
FEATURE [Part::Box] Box551  label="Krychle551"
  AttacherType = Attacher::AttachEngine3D
  Height = 120
  Length = 200
  Placement = pos=(-60,44,-90) rot=(0,0,1;0rad)
  Width = 100
FEATURE [Part::Cylinder] Cylinder1830  label="Válec1830"
  Angle = 360
  AttacherType = Attacher::AttachEngine3D
  Height = 100
  Placement = pos=(14,0,-60) rot=(0,0,1;0rad)
  Radius = 1.5
FEATURE [Part::Box] Box552  label="Krychle552"
  AttacherType = Attacher::AttachEngine3D
  Height = 120
  Length = 200
  Placement = pos=(-60,-134,-90) rot=(0,0,1;0rad)
  Width = 100
FEATURE [Part::Cylinder] Cylinder1831  label="Válec1831"
  Angle = 360
  AttacherType = Attacher::AttachEngine3D
  Height = 100
  Placement = pos=(90,0,-60) rot=(0,0,1;0rad)
  Radius = 1.5
FEATURE [Part::Cylinder] Cylinder1832  label="Válec1832"
  Angle = 360
  AttacherType = Attacher::AttachEngine3D
  Height = 100
  Placement = pos=(10,-36,-60) rot=(0,0,1;0rad)
  Radius = 1.5
FEATURE [Part::Cylinder] Cylinder1833  label="Válec1833"
  Angle = 360
  AttacherType = Attacher::AttachEngine3D
  Height = 100
  Placement = pos=(34,16,-60) rot=(0,0,1;0rad)
  Radius = 1.5
FEATURE [Part::Cylinder] Cylinder1834  label="Válec1834"
  Angle = 360
  AttacherType = Attacher::AttachEngine3D
  Height = 160
  Placement = pos=(-18,0,-60) rot=(0,0,1;0rad)
  Radius = 17
FEATURE [Part::Cylinder] Cylinder1835  label="Válec1835"
  Angle = 360
  AttacherType = Attacher::AttachEngine3D
  Height = 160
  Placement = pos=(-18,0,-60) rot=(0,0,1;0rad)
  Radius = 17
FEATURE [Part::Cylinder] Cylinder1836  label="Válec1836"
  Angle = 360
  AttacherType = Attacher::AttachEngine3D
  Height = 100
  Placement = pos=(14,0,-18) rot=(0,0,1;0rad)
  Radius = 4
FEATURE [Part::Cylinder] Cylinder1837  label="Válec1837"
  Angle = 360
  AttacherType = Attacher::AttachEngine3D
  Height = 100
  Placement = pos=(-34,16,-90) rot=(0,0,1;0rad)
  Radius = 4
FEATURE [Part::Cylinder] Cylinder1838  label="Válec1838"
  Angle = 360
  AttacherType = Attacher::AttachEngine3D
  Height = 100
  Placement = pos=(90,0,-18) rot=(0,0,1;0rad)
  Radius = 4
FEATURE [Part::Cylinder] Cylinder1839  label="Válec1839"
  Angle = 360
  AttacherType = Attacher::AttachEngine3D
  Height = 100
  Placement = pos=(16,34,-90) rot=(0,0,1;0rad)
  Radius = 4
FEATURE [Part::Box] Box553  label="Krychle553"
  AttacherType = Attacher::AttachEngine3D
  Height = 2
  Length = 6
  Placement = pos=(23,38,-22) rot=(0,0,1;0rad)
  Width = 6
FEATURE [Part::Cylinder] Cylinder1840  label="Válec1840"
  Angle = 360
  AttacherType = Attacher::AttachEngine3D
  Height = 100
  Placement = pos=(34,-16,-60) rot=(0,0,1;0rad)
  Radius = 1.5
FEATURE [Part::Cylinder] Cylinder1841  label="Válec1841"
  Angle = 360
  AttacherType = Attacher::AttachEngine3D
  Height = 100
  Placement = pos=(-34,-16,-60) rot=(0,0,1;0rad)
  Radius = 1.5
FEATURE [Part::Cylinder] Cylinder1842  label="Válec1842"
  Angle = 360
  AttacherType = Attacher::AttachEngine3D
  Height = 100
  Placement = pos=(34,16,-90) rot=(0,0,1;0rad)
  Radius = 4
FEATURE [Part::Cylinder] Cylinder1843  label="Válec1843"
  Angle = 360
  AttacherType = Attacher::AttachEngine3D
  Height = 32
  Placement = pos=(78,41,-46) rot=(0,0,1;0rad)
  Radius = 1.5
FEATURE [Part::Cylinder] Cylinder1844  label="Válec1844"
  Angle = 360
  AttacherType = Attacher::AttachEngine3D
  Height = 100
  Placement = pos=(-34,16,-60) rot=(0,0,1;0rad)
  Radius = 1.5
FEATURE [Part::Cylinder] Cylinder1845  label="Válec1845"
  Angle = 360
  AttacherType = Attacher::AttachEngine3D
  Height = 160
  Placement = pos=(-18,0,-60) rot=(0,0,1;0rad)
  Radius = 17
FEATURE [Part::Cut] Cut613
  Base = -> Cut620
  Tool = -> Cylinder1845
FEATURE [Part::Cylinder] Cylinder1846  label="Válec1846"
  Angle = 360
  AttacherType = Attacher::AttachEngine3D
  Height = 100
  Placement = pos=(-16,34,-60) rot=(0,0,1;0rad)
  Radius = 1.5
FEATURE [Part::Cylinder] Cylinder1847  label="Válec1847"
  Angle = 360
  AttacherType = Attacher::AttachEngine3D
  Height = 100
  Placement = pos=(103,-12,-60) rot=(0,0,1;0rad)
  Radius = 1.5
FEATURE [Part::Cylinder] Cylinder1848  label="Válec1848"
  Angle = 360
  AttacherType = Attacher::AttachEngine3D
  Height = 100
  Placement = pos=(103,12,-60) rot=(0,0,1;0rad)
  Radius = 1.5
FEATURE [Part::Cylinder] Cylinder1849  label="Válec1849"
  Angle = 360
  AttacherType = Attacher::AttachEngine3D
  Height = 100
  Placement = pos=(76,24,-60) rot=(0,0,1;0rad)
  Radius = 1.5
FEATURE [Part::Cylinder] Cylinder1850  label="Válec1850"
  Angle = 360
  AttacherType = Attacher::AttachEngine3D
  Height = 100
  Placement = pos=(91,-27,-60) rot=(0,0,1;0rad)
  Radius = 1.5
FEATURE [Part::Cylinder] Cylinder1851  label="Válec1851"
  Angle = 360
  AttacherType = Attacher::AttachEngine3D
  Height = 100
  Placement = pos=(28,24,-60) rot=(0,0,1;0rad)
  Radius = 1.5
FEATURE [Part::Cylinder] Cylinder1852  label="Válec1852"
  Angle = 360
  AttacherType = Attacher::AttachEngine3D
  Height = 100
  Placement = pos=(1,-12,-60) rot=(0,0,1;0rad)
  Radius = 1.5
FEATURE [Part::Cylinder] Cylinder1853  label="Válec1853"
  Angle = 360
  AttacherType = Attacher::AttachEngine3D
  Height = 20
  Placement = pos=(103,-12,-20) rot=(0,0,1;0rad)
  Radius = 4
FEATURE [Part::Cylinder] Cylinder1854  label="Válec1854"
  Angle = 360
  AttacherType = Attacher::AttachEngine3D
  Height = 32
  Placement = pos=(76,24,-18) rot=(0,0,1;0rad)
  Radius = 4
FEATURE [Part::Cylinder] Cylinder1855  label="Válec1855"
  Angle = 360
  AttacherType = Attacher::AttachEngine3D
  Height = 20
  Placement = pos=(91,-27,-18) rot=(0,0,1;0rad)
  Radius = 4
FEATURE [Part::Cylinder] Cylinder1856  label="Válec1856"
  Angle = 360
  AttacherType = Attacher::AttachEngine3D
  Height = 40
  Placement = pos=(13,-27,-18) rot=(0,0,1;0rad)
  Radius = 4
FEATURE [Part::Cylinder] Cylinder1857  label="Válec1857"
  Angle = 360
  AttacherType = Attacher::AttachEngine3D
  Height = 40
  Placement = pos=(28,24,-18) rot=(0,0,1;0rad)
  Radius = 4
FEATURE [Part::Cylinder] Cylinder1858  label="Válec1858"
  Angle = 360
  AttacherType = Attacher::AttachEngine3D
  Height = 40
  Placement = pos=(1,-12,-18) rot=(0,0,1;0rad)
  Radius = 4
FEATURE [Part::Cylinder] Cylinder1859  label="Válec1859"
  Angle = 360
  AttacherType = Attacher::AttachEngine3D
  Height = 40
  Placement = pos=(1,12,-18) rot=(0,0,1;0rad)
  Radius = 4
FEATURE [Part::Cylinder] Cylinder1860  label="Válec1860"
  Angle = 360
  AttacherType = Attacher::AttachEngine3D
  Height = 100
  Placement = pos=(1,12,-60) rot=(0,0,1;0rad)
  Radius = 1.5
FEATURE [Part::Cylinder] Cylinder1861  label="Válec1861"
  Angle = 360
  AttacherType = Attacher::AttachEngine3D
  Height = 20
  Placement = pos=(103,12,-20) rot=(0,0,1;0rad)
  Radius = 4
FEATURE [Part::Cylinder] Cylinder1862  label="Válec1862"
  Angle = 360
  AttacherType = Attacher::AttachEngine3D
  Height = 100
  Placement = pos=(13,-27,-60) rot=(0,0,1;0rad)
  Radius = 1.5
FEATURE [Part::Cylinder] Cylinder1863  label="Válec1863"
  Angle = 360
  AttacherType = Attacher::AttachEngine3D
  Height = 100
  Placement = pos=(-16,-34,-60) rot=(0,0,1;0rad)
  Radius = 1.5
FEATURE [Part::Cylinder] Cylinder1864  label="Válec1864"
  Angle = 360
  AttacherType = Attacher::AttachEngine3D
  Height = 100
  Placement = pos=(-34,-16,-90) rot=(0,0,1;0rad)
  Radius = 4
FEATURE [Part::Cylinder] Cylinder1865  label="Válec1865"
  Angle = 360
  AttacherType = Attacher::AttachEngine3D
  Height = 100
  Placement = pos=(-16,34,-90) rot=(0,0,1;0rad)
  Radius = 4
FEATURE [Part::Cylinder] Cylinder1866  label="Válec1866"
  Angle = 360
  AttacherType = Attacher::AttachEngine3D
  Height = 100
  Placement = pos=(16,34,-60) rot=(0,0,1;0rad)
  Radius = 1.5
FEATURE [Part::Cylinder] Cylinder1867  label="Válec1867"
  Angle = 360
  AttacherType = Attacher::AttachEngine3D
  Height = 100
  Placement = pos=(10,-36,-90) rot=(0,0,1;0rad)
  Radius = 4
FEATURE [Part::Cylinder] Cylinder1868  label="Válec1868"
  Angle = 360
  AttacherType = Attacher::AttachEngine3D
  Height = 100
  Placement = pos=(34,-16,-90) rot=(0,0,1;0rad)
  Radius = 4
FEATURE [Part::Box] Box554  label="Krychle554"
  AttacherType = Attacher::AttachEngine3D
  Height = 2
  Length = 6
  Placement = pos=(75,38,-22) rot=(0,0,1;0rad)
  Width = 6
FEATURE [Part::Cylinder] Cylinder1869  label="Válec1869"
  Angle = 360
  AttacherType = Attacher::AttachEngine3D
  Height = 32
  Placement = pos=(26,41,-46) rot=(0,0,1;0rad)
  Radius = 1.5
FEATURE [Part::Cylinder] Cylinder1870  label="Válec1870"
  Angle = 360
  AttacherType = Attacher::AttachEngine3D
  Height = 100
  Placement = pos=(-16,-34,-90) rot=(0,0,1;0rad)
  Radius = 4
FEATURE [Part::Cylinder] Cylinder1871  label="Válec1871"
  Angle = 360
  AttacherType = Attacher::AttachEngine3D
  Height = 100
  Placement = pos=(14,0,-60) rot=(0,0,1;0rad)
  Radius = 1.5
FEATURE [Part::Fillet] Fillet025
  Base = -> Cut613
  Edges = 1 edges r=4: [Edge11]
FEATURE [Part::Compound] Compound959  label="sbouby_baze013"
  Links = -> [Cylinder1844,Cylinder1841,Cylinder1840,Cylinder1833,Cylinder1866,Cylinder1832,Cylinder1863,Cylinder1846]
FEATURE [Part::Compound] Compound960  label="srouby_monoblok_silne014"
  Links = -> [Cylinder1853,Cylinder1861,Cylinder1854,Cylinder1855,Cylinder1856,Cylinder1857,Cylinder1858,Cylinder1859]
FEATURE [Part::Compound] Compound961  label="srouby_troj010"
  Links = -> [Cylinder1831,Cylinder1830]
FEATURE [Part::Compound] Compound962
  Links = -> [Box554,Box553]
FEATURE [Part::Compound] Compound963  label="sbouby_baze_silne018"
  Links = -> [Cylinder1864,Cylinder1865,Cylinder1870,Cylinder1868,Cylinder1839,Cylinder1867,Cylinder1837,Cylinder1842]
  Placement = pos=(-0.5,0,12) rot=(0,0,1;0rad)
FEATURE [Part::Compound] Compound964  label="srouby_monoblok012"
  Links = -> [Cylinder1847,Cylinder1848,Cylinder1849,Cylinder1850,Cylinder1862,Cylinder1851,Cylinder1852,Cylinder1860]
FEATURE [Part::Cut] Cut618
  Base = -> Extrude012
  Tool = -> Compound964
FEATURE [Part::Cut] Cut617
  Base = -> Cut618
  Tool = -> Compound960
FEATURE [Part::Cut] Cut610
  Base = -> Cut617
  Tool = -> Compound963
FEATURE [Part::Cut] Cut625
  Base = -> Cut610
  Tool = -> Compound959
FEATURE [Part::Cut] Cut605
  Base = -> Cut625
  Tool = -> Box552
FEATURE [Part::Cut] Cut606
  Base = -> Cut605
  Tool = -> Box551
FEATURE [Part::Cut] Cut607
  Base = -> Cut606
  Tool = -> Compound962
FEATURE [Part::Compound] Compound965
  Links = -> [Cylinder1869,Cylinder1843]
FEATURE [Part::Cut] Cut608
  Base = -> Cut607
  Tool = -> Compound965
FEATURE [Part::Cut] Cut609
  Base = -> Cut608
  Tool = -> Compound961
FEATURE [Part::Compound] Compound966  label="srouby_troj_silne011"
  Links = -> [Cylinder1838,Cylinder1836]
FEATURE [Part::Cut] Cut616
  Base = -> Cut609
  Tool = -> Compound966
FEATURE [Part::Chamfer] Chamfer062
  Base = -> Cut616
  Edges = 1 edges r=4: [Edge44]
FEATURE [Part::Compound] Compound967  label="srouby_troj011"
  Links = -> [Cylinder1829,Cylinder1871]
FEATURE [Part::Compound] Compound968  label="srouby_monoblok013"
  Links = -> [Cylinder1822,Cylinder1821,Cylinder1820,Cylinder1819,Cylinder1818,Cylinder1808,Cylinder1807,Cylinder1799]
FEATURE [Part::Cut] Cut621
  Base = -> Cylinder1823
  Tool = -> Compound968
FEATURE [Part::Compound] Compound969
  Links = -> [Cylinder1802,Cylinder1810]
FEATURE [Part::Compound] Compound970  label="sbouby_baze_silne019"
  Links = -> [Cylinder1814,Cylinder1813,Cylinder1800,Cylinder1816,Cylinder1815,Cylinder1812,Cylinder1801,Cylinder1811]
  Placement = pos=(-0.5,0,0) rot=(0,0,1;0rad)
FEATURE [Part::Cut] Cut622
  Base = -> Cut621
  Tool = -> Compound970
FEATURE [Part::Cut] Cut623
  Base = -> Cut622
  Tool = -> Box550
FEATURE [Part::Cut] Cut626
  Base = -> Cut623
  Tool = -> Box549
FEATURE [Part::Cut] Cut627
  Base = -> Cut626
  Tool = -> Compound969
FEATURE [Part::Cut] Cut624
  Base = -> Cut627
  Tool = -> Compound967
FEATURE [Part::Cut] Cut612
  Base = -> Cut624
  Tool = -> Cylinder1834
FEATURE [Part::Fillet] Fillet023
  Base = -> Cut612
  Edges = 2 edges r=8: [Edge55,Edge57]
FEATURE [Part::Chamfer] Chamfer063
  Base = -> Chamfer062
  Edges = 2 edges r=3: [Edge4,Edge6]
FEATURE [Part::Cut] Cut611
  Base = -> Chamfer063
  Tool = -> Cylinder1835
FEATURE [Part::Fillet] Fillet024
  Base = -> Cut611
  Edges = 2 edges r=3: [Edge3,Edge34]
FEATURE [Part::Compound] Compound958  label="Base_deep-highneck-holed"
  Links = -> [Fillet024,Fillet023,Fillet025]
FEATURE [Part::Cylinder] Cylinder1872  label="Válec1872"
  Angle = 360
  AttacherType = Attacher::AttachEngine3D
  Height = 100
  Placement = pos=(-16,-34,-90) rot=(0,0,1;0rad)
  Radius = 4
FEATURE [Part::Cylinder] Cylinder1873  label="Válec1873"
  Angle = 360
  AttacherType = Attacher::AttachEngine3D
  Height = 100
  Placement = pos=(14,0,-18) rot=(0,0,1;0rad)
  Radius = 4
FEATURE [Part::Cylinder] Cylinder1874  label="Válec1874"
  Angle = 360
  AttacherType = Attacher::AttachEngine3D
  Height = 20
  Placement = pos=(76,24,-18) rot=(0,0,1;0rad)
  Radius = 4
FEATURE [Part::Cylinder] Cylinder1875  label="Válec1875"
  Angle = 360
  AttacherType = Attacher::AttachEngine3D
  Height = 20
  Placement = pos=(103,-12,-20) rot=(0,0,1;0rad)
  Radius = 4
FEATURE [Part::Cylinder] Cylinder1876  label="Válec1876"
  Angle = 360
  AttacherType = Attacher::AttachEngine3D
  Height = 16
  Placement = pos=(0,0,2) rot=(0,0,1;0rad)
  Radius = 59
FEATURE [Part::Cylinder] Cylinder1877  label="Válec1877"
  Angle = 360
  AttacherType = Attacher::AttachEngine3D
  Height = 20
  Placement = pos=(103,12,-20) rot=(0,0,1;0rad)
  Radius = 4
FEATURE [Part::Cylinder] Cylinder1878  label="Válec1878"
  Angle = 360
  AttacherType = Attacher::AttachEngine3D
  Height = 20
  Placement = pos=(91,-27,-18) rot=(0,0,1;0rad)
  Radius = 4
FEATURE [Part::Cylinder] Cylinder1879  label="Válec1879"
  Angle = 360
  AttacherType = Attacher::AttachEngine3D
  Height = 40
  Placement = pos=(13,-27,-18) rot=(0,0,1;0rad)
  Radius = 4
FEATURE [Part::Cylinder] Cylinder1880  label="Válec1880"
  Angle = 360
  AttacherType = Attacher::AttachEngine3D
  Height = 40
  Placement = pos=(28,24,-18) rot=(0,0,1;0rad)
  Radius = 4
FEATURE [Part::Cylinder] Cylinder1881  label="Válec1881"
  Angle = 360
  AttacherType = Attacher::AttachEngine3D
  Height = 40
  Placement = pos=(1,-12,-18) rot=(0,0,1;0rad)
  Radius = 4
FEATURE [Part::Cylinder] Cylinder1882  label="Válec1882"
  Angle = 360
  AttacherType = Attacher::AttachEngine3D
  Height = 40
  Placement = pos=(1,12,-18) rot=(0,0,1;0rad)
  Radius = 4
FEATURE [Part::Compound] Compound974  label="srouby_monoblok_silne015"
  Links = -> [Cylinder1875,Cylinder1877,Cylinder1874,Cylinder1878,Cylinder1879,Cylinder1880,Cylinder1881,Cylinder1882]
FEATURE [Part::Cylinder] Cylinder1883  label="Válec1883"
  Angle = 360
  AttacherType = Attacher::AttachEngine3D
  Height = 100
  Placement = pos=(90,0,-18) rot=(0,0,1;0rad)
  Radius = 4
FEATURE [Part::Compound] Compound973  label="srouby_troj_silne012"
  Links = -> [Cylinder1883,Cylinder1873]
FEATURE [Part::Cylinder] Cylinder1884  label="Válec1884"
  Angle = 360
  AttacherType = Attacher::AttachEngine3D
  Height = 100
  Placement = pos=(-16,34,-90) rot=(0,0,1;0rad)
  Radius = 4
FEATURE [Part::Cylinder] Cylinder1885  label="Válec1885"
  Angle = 360
  AttacherType = Attacher::AttachEngine3D
  Height = 100
  Placement = pos=(-34,16,-90) rot=(0,0,1;0rad)
  Radius = 4
FEATURE [Part::Cylinder] Cylinder1886  label="Válec1886"
  Angle = 360
  AttacherType = Attacher::AttachEngine3D
  Height = 16
  Placement = pos=(0,0,10) rot=(0,0,1;0rad)
  Radius = 59
FEATURE [Part::Cylinder] Cylinder1887  label="Válec1887"
  Angle = 360
  AttacherType = Attacher::AttachEngine3D
  Height = 100
  Placement = pos=(10,-36,-60) rot=(0,0,1;0rad)
  Radius = 1.5
FEATURE [Part::Cylinder] Cylinder1888  label="Válec1888"
  Angle = 360
  AttacherType = Attacher::AttachEngine3D
  Height = 100
  Placement = pos=(-16,-34,-60) rot=(0,0,1;0rad)
  Radius = 1.5
FEATURE [Part::Cylinder] Cylinder1889  label="Válec1889"
  Angle = 360
  AttacherType = Attacher::AttachEngine3D
  Height = 100
  Placement = pos=(34,16,-60) rot=(0,0,1;0rad)
  Radius = 1.5
FEATURE [Part::Cylinder] Cylinder1890  label="Válec1890"
  Angle = 360
  AttacherType = Attacher::AttachEngine3D
  Height = 100
  Placement = pos=(16,34,-60) rot=(0,0,1;0rad)
  Radius = 1.5
FEATURE [Part::Cylinder] Cylinder1891  label="Válec1891"
  Angle = 360
  AttacherType = Attacher::AttachEngine3D
  Height = 100
  Placement = pos=(91,-27,-60) rot=(0,0,1;0rad)
  Radius = 1.5
FEATURE [Part::Cylinder] Cylinder1892  label="Válec1892"
  Angle = 360
  AttacherType = Attacher::AttachEngine3D
  Height = 100
  Placement = pos=(-34,-16,-60) rot=(0,0,1;0rad)
  Radius = 1.5
FEATURE [Part::Cylinder] Cylinder1893  label="Válec1893"
  Angle = 360
  AttacherType = Attacher::AttachEngine3D
  Height = 100
  Placement = pos=(16,34,-90) rot=(0,0,1;0rad)
  Radius = 4
FEATURE [Part::Cylinder] Cylinder1894  label="Válec1894"
  Angle = 360
  AttacherType = Attacher::AttachEngine3D
  Height = 100
  Placement = pos=(13,-27,-60) rot=(0,0,1;0rad)
  Radius = 1.5
FEATURE [Part::Cylinder] Cylinder1895  label="Válec1895"
  Angle = 360
  AttacherType = Attacher::AttachEngine3D
  Height = 100
  Placement = pos=(34,-16,-60) rot=(0,0,1;0rad)
  Radius = 1.5
FEATURE [Part::Cylinder] Cylinder1896  label="Válec1896"
  Angle = 360
  AttacherType = Attacher::AttachEngine3D
  Height = 100
  Placement = pos=(10,-36,-90) rot=(0,0,1;0rad)
  Radius = 4
FEATURE [Part::Cylinder] Cylinder1897  label="Válec1897"
  Angle = 360
  AttacherType = Attacher::AttachEngine3D
  Height = 160
  Placement = pos=(-18,0,-60) rot=(0,0,1;0rad)
  Radius = 17
FEATURE [Part::Box] Box555  label="Krychle555"
  AttacherType = Attacher::AttachEngine3D
  Height = 100
  Length = 200
  Placement = pos=(-60,44,-90) rot=(0,0,1;0rad)
  Width = 100
FEATURE [Part::Cylinder] Cylinder1898  label="Válec1898"
  Angle = 360
  AttacherType = Attacher::AttachEngine3D
  Height = 100
  Placement = pos=(1,-12,-60) rot=(0,0,1;0rad)
  Radius = 1.5
FEATURE [Part::Cylinder] Cylinder1899  label="Válec1899"
  Angle = 360
  AttacherType = Attacher::AttachEngine3D
  Height = 100
  Placement = pos=(34,16,-90) rot=(0,0,1;0rad)
  Radius = 4
FEATURE [Part::Cylinder] Cylinder1900  label="Válec1900"
  Angle = 360
  AttacherType = Attacher::AttachEngine3D
  Height = 100
  Placement = pos=(-34,-16,-90) rot=(0,0,1;0rad)
  Radius = 4
FEATURE [Part::Cylinder] Cylinder1901  label="Válec1901"
  Angle = 360
  AttacherType = Attacher::AttachEngine3D
  Height = 100
  Placement = pos=(-34,16,-90) rot=(0,0,1;0rad)
  Radius = 4
FEATURE [Part::Cylinder] Cylinder1902  label="Válec1902"
  Angle = 360
  AttacherType = Attacher::AttachEngine3D
  Height = 100
  Placement = pos=(34,16,-90) rot=(0,0,1;0rad)
  Radius = 4
FEATURE [Part::Cylinder] Cylinder1903  label="Válec1903"
  Angle = 360
  AttacherType = Attacher::AttachEngine3D
  Height = 32
  Placement = pos=(26,41,-42) rot=(0,0,1;0rad)
  Radius = 1.5
FEATURE [Part::Cylinder] Cylinder1904  label="Válec1904"
  Angle = 360
  AttacherType = Attacher::AttachEngine3D
  Height = 160
  Placement = pos=(-18,0,-60) rot=(0,0,1;0rad)
  Radius = 17
FEATURE [Part::Cylinder] Cylinder1905  label="Válec1905"
  Angle = 360
  AttacherType = Attacher::AttachEngine3D
  Height = 100
  Placement = pos=(-34,16,-60) rot=(0,0,1;0rad)
  Radius = 1.5
FEATURE [Part::Cylinder] Cylinder1906  label="Válec1906"
  Angle = 360
  AttacherType = Attacher::AttachEngine3D
  Height = 20
  Placement = pos=(103,12,-20) rot=(0,0,1;0rad)
  Radius = 4
FEATURE [Part::Cylinder] Cylinder1907  label="Válec1907"
  Angle = 360
  AttacherType = Attacher::AttachEngine3D
  Height = 100
  Placement = pos=(-16,34,-90) rot=(0,0,1;0rad)
  Radius = 4
FEATURE [Part::Cylinder] Cylinder1908  label="Válec1908"
  Angle = 360
  AttacherType = Attacher::AttachEngine3D
  Height = 100
  Placement = pos=(-16,-34,-90) rot=(0,0,1;0rad)
  Radius = 4
FEATURE [Part::Cylinder] Cylinder1909  label="Válec1909"
  Angle = 360
  AttacherType = Attacher::AttachEngine3D
  Height = 40
  Placement = pos=(1,-12,-18) rot=(0,0,1;0rad)
  Radius = 4
FEATURE [Part::Cylinder] Cylinder1910  label="Válec1910"
  Angle = 360
  AttacherType = Attacher::AttachEngine3D
  Height = 100
  Placement = pos=(14,0,-60) rot=(0,0,1;0rad)
  Radius = 1.5
FEATURE [Part::Cylinder] Cylinder1911  label="Válec1911"
  Angle = 360
  AttacherType = Attacher::AttachEngine3D
  Height = 100
  Placement = pos=(-16,34,-60) rot=(0,0,1;0rad)
  Radius = 1.5
FEATURE [Part::Cylinder] Cylinder1912  label="Válec1912"
  Angle = 360
  AttacherType = Attacher::AttachEngine3D
  Height = 100
  Placement = pos=(34,-16,-90) rot=(0,0,1;0rad)
  Radius = 4
FEATURE [Part::Cylinder] Cylinder1913  label="Válec1913"
  Angle = 360
  AttacherType = Attacher::AttachEngine3D
  Height = 100
  Placement = pos=(16,34,-90) rot=(0,0,1;0rad)
  Radius = 4
FEATURE [Part::Cylinder] Cylinder1914  label="Válec1914"
  Angle = 360
  AttacherType = Attacher::AttachEngine3D
  Height = 100
  Placement = pos=(16,-34,-90) rot=(0,0,1;0rad)
  Radius = 4
FEATURE [Part::Cylinder] Cylinder1915  label="Válec1915"
  Angle = 360
  AttacherType = Attacher::AttachEngine3D
  Height = 40
  Placement = pos=(28,24,-18) rot=(0,0,1;0rad)
  Radius = 4
FEATURE [Part::Cylinder] Cylinder1916  label="Válec1916"
  Angle = 360
  AttacherType = Attacher::AttachEngine3D
  Height = 20
  Placement = pos=(91,-27,-18) rot=(0,0,1;0rad)
  Radius = 4
FEATURE [Part::Cylinder] Cylinder1917  label="Válec1917"
  Angle = 360
  AttacherType = Attacher::AttachEngine3D
  Height = 100
  Placement = pos=(28,24,-60) rot=(0,0,1;0rad)
  Radius = 1.5
FEATURE [Part::Cylinder] Cylinder1918  label="Válec1918"
  Angle = 360
  AttacherType = Attacher::AttachEngine3D
  Height = 20
  Placement = pos=(76,24,-18) rot=(0,0,1;0rad)
  Radius = 4
FEATURE [Part::Cylinder] Cylinder1919  label="Válec1919"
  Angle = 360
  AttacherType = Attacher::AttachEngine3D
  Height = 100
  Placement = pos=(-34,-16,-90) rot=(0,0,1;0rad)
  Radius = 4
FEATURE [Part::Cylinder] Cylinder1920  label="Válec1920"
  Angle = 360
  AttacherType = Attacher::AttachEngine3D
  Height = 100
  Placement = pos=(1,12,-60) rot=(0,0,1;0rad)
  Radius = 1.5
FEATURE [Part::Cylinder] Cylinder1921  label="Válec1921"
  Angle = 360
  AttacherType = Attacher::AttachEngine3D
  Height = 40
  Placement = pos=(13,-27,-18) rot=(0,0,1;0rad)
  Radius = 4
FEATURE [Part::Cylinder] Cylinder1922  label="Válec1922"
  Angle = 360
  AttacherType = Attacher::AttachEngine3D
  Height = 100
  Placement = pos=(34,-16,-90) rot=(0,0,1;0rad)
  Radius = 4
FEATURE [Part::Cylinder] Cylinder1923  label="Válec1923"
  Angle = 360
  AttacherType = Attacher::AttachEngine3D
  Height = 100
  Placement = pos=(-34,-16,-90) rot=(0,0,1;0rad)
  Radius = 4
FEATURE [Part::Cylinder] Cylinder1924  label="Válec1924"
  Angle = 360
  AttacherType = Attacher::AttachEngine3D
  Height = 100
  Placement = pos=(103,-12,-60) rot=(0,0,1;0rad)
  Radius = 1.5
FEATURE [Part::Cylinder] Cylinder1925  label="Válec1925"
  Angle = 360
  AttacherType = Attacher::AttachEngine3D
  Height = 4
  Placement = pos=(52,0,-26) rot=(0,0,1;0rad)
  Radius = 59
FEATURE [Part::Cylinder] Cylinder1926  label="Válec1926"
  Angle = 360
  AttacherType = Attacher::AttachEngine3D
  Height = 100
  Placement = pos=(76,24,-60) rot=(0,0,1;0rad)
  Radius = 1.5
FEATURE [Part::Cylinder] Cylinder1927  label="Válec1927"
  Angle = 360
  AttacherType = Attacher::AttachEngine3D
  Height = 100
  Placement = pos=(103,12,-60) rot=(0,0,1;0rad)
  Radius = 1.5
FEATURE [Part::Cylinder] Cylinder1928  label="Válec1928"
  Angle = 360
  AttacherType = Attacher::AttachEngine3D
  Height = 100
  Placement = pos=(-16,-34,-90) rot=(0,0,1;0rad)
  Radius = 4
FEATURE [Part::Cylinder] Cylinder1929  label="Válec1929"
  Angle = 360
  AttacherType = Attacher::AttachEngine3D
  Height = 100
  Placement = pos=(14,0,-18) rot=(0,0,1;0rad)
  Radius = 4
FEATURE [Part::Cylinder] Cylinder1930  label="Válec1930"
  Angle = 360
  AttacherType = Attacher::AttachEngine3D
  Height = 20
  Placement = pos=(76,24,-18) rot=(0,0,1;0rad)
  Radius = 4
FEATURE [Part::Cylinder] Cylinder1931  label="Válec1931"
  Angle = 360
  AttacherType = Attacher::AttachEngine3D
  Height = 20
  Placement = pos=(103,-12,-20) rot=(0,0,1;0rad)
  Radius = 4
FEATURE [Part::Cylinder] Cylinder1932  label="Válec1932"
  Angle = 360
  AttacherType = Attacher::AttachEngine3D
  Height = 40
  Placement = pos=(1,12,-18) rot=(0,0,1;0rad)
  Radius = 4
FEATURE [Part::Cylinder] Cylinder1933  label="Válec1933"
  Angle = 360
  AttacherType = Attacher::AttachEngine3D
  Height = 16
  Placement = pos=(0,0,2) rot=(0,0,1;0rad)
  Radius = 59
FEATURE [Part::Cylinder] Cylinder1934  label="Válec1934"
  Angle = 360
  AttacherType = Attacher::AttachEngine3D
  Height = 20
  Placement = pos=(103,12,-20) rot=(0,0,1;0rad)
  Radius = 4
FEATURE [Part::Cylinder] Cylinder1935  label="Válec1935"
  Angle = 360
  AttacherType = Attacher::AttachEngine3D
  Height = 20
  Placement = pos=(91,-27,-18) rot=(0,0,1;0rad)
  Radius = 4
FEATURE [Part::Cylinder] Cylinder1936  label="Válec1936"
  Angle = 360
  AttacherType = Attacher::AttachEngine3D
  Height = 40
  Placement = pos=(13,-27,-18) rot=(0,0,1;0rad)
  Radius = 4
FEATURE [Part::Cylinder] Cylinder1937  label="Válec1937"
  Angle = 360
  AttacherType = Attacher::AttachEngine3D
  Height = 40
  Placement = pos=(28,24,-18) rot=(0,0,1;0rad)
  Radius = 4
FEATURE [Part::Cylinder] Cylinder1938  label="Válec1938"
  Angle = 360
  AttacherType = Attacher::AttachEngine3D
  Height = 40
  Placement = pos=(1,-12,-18) rot=(0,0,1;0rad)
  Radius = 4
FEATURE [Part::Cylinder] Cylinder1939  label="Válec1939"
  Angle = 360
  AttacherType = Attacher::AttachEngine3D
  Height = 40
  Placement = pos=(1,12,-18) rot=(0,0,1;0rad)
  Radius = 4
FEATURE [Part::Cylinder] Cylinder1940  label="Válec1940"
  Angle = 360
  AttacherType = Attacher::AttachEngine3D
  Height = 100
  Placement = pos=(90,0,-18) rot=(0,0,1;0rad)
  Radius = 4
FEATURE [Part::Cylinder] Cylinder1941  label="Válec1941"
  Angle = 360
  AttacherType = Attacher::AttachEngine3D
  Height = 100
  Placement = pos=(-16,34,-90) rot=(0,0,1;0rad)
  Radius = 4
FEATURE [Part::Cylinder] Cylinder1942  label="Válec1942"
  Angle = 360
  AttacherType = Attacher::AttachEngine3D
  Height = 100
  Placement = pos=(-16,34,-90) rot=(0,0,1;0rad)
  Radius = 4
FEATURE [Part::Cylinder] Cylinder1943  label="Válec1943"
  Angle = 360
  AttacherType = Attacher::AttachEngine3D
  Height = 100
  Placement = pos=(90,0,-60) rot=(0,0,1;0rad)
  Radius = 1.5
FEATURE [Part::Cylinder] Cylinder1944  label="Válec1944"
  Angle = 360
  AttacherType = Attacher::AttachEngine3D
  Height = 32
  Placement = pos=(78,41,-42) rot=(0,0,1;0rad)
  Radius = 1.5
FEATURE [Part::Box] Box556  label="Krychle556"
  AttacherType = Attacher::AttachEngine3D
  Height = 100
  Length = 200
  Placement = pos=(-60,-130,-90) rot=(0,0,1;0rad)
  Width = 100
FEATURE [Part::Cylinder] Cylinder1945  label="Válec1945"
  Angle = 360
  AttacherType = Attacher::AttachEngine3D
  Height = 100
  Placement = pos=(16,34,-90) rot=(0,0,1;0rad)
  Radius = 4
FEATURE [Part::Cylinder] Cylinder1946  label="Válec1946"
  Angle = 360
  AttacherType = Attacher::AttachEngine3D
  Height = 160
  Placement = pos=(-18,0,-60) rot=(0,0,1;0rad)
  Radius = 17
FEATURE [Part::Cylinder] Cylinder1947  label="Válec1947"
  Angle = 360
  AttacherType = Attacher::AttachEngine3D
  Height = 100
  Placement = pos=(-34,16,-90) rot=(0,0,1;0rad)
  Radius = 4
FEATURE [Part::Compound] Compound976  label="sbouby_baze_silne021"
  Links = -> [Cylinder1923,Cylinder1942,Cylinder1928,Cylinder1922,Cylinder1893,Cylinder1896,Cylinder1947,Cylinder1899]
FEATURE [Part::Compound] Compound977  label="srouby_monoblok_silne016"
  Links = -> [Cylinder1931,Cylinder1934,Cylinder1930,Cylinder1935,Cylinder1936,Cylinder1937,Cylinder1938,Cylinder1939]
FEATURE [Part::Cut] Cut648
  Base = -> Cylinder1933
  Tool = -> Compound977
FEATURE [Part::Cut] Cut649
  Base = -> Cut648
  Tool = -> Compound976
FEATURE [Part::Compound] Compound978  label="srouby_troj_silne013"
  Links = -> [Cylinder1940,Cylinder1929]
FEATURE [Part::Compound] Compound979  label="srouby_monoblok014"
  Links = -> [Cylinder1924,Cylinder1927,Cylinder1926,Cylinder1891,Cylinder1894,Cylinder1917,Cylinder1898,Cylinder1920]
FEATURE [Part::Cut] Cut630
  Base = -> Cylinder1925
  Tool = -> Compound979
FEATURE [Part::Compound] Compound980  label="sbouby_baze015"
  Links = -> [Cylinder1905,Cylinder1892,Cylinder1895,Cylinder1889,Cylinder1890,Cylinder1887,Cylinder1888,Cylinder1911]
FEATURE [Part::Cut] Cut628
  Base = -> Cut649
  Tool = -> Compound980
FEATURE [Part::Chamfer] Chamfer067
  Base = -> Cut628
  Edges = 1 edges r=4: [Edge3]
FEATURE [Part::Cut] Cut629
  Base = -> Chamfer067
  Placement = pos=(0,0,4) rot=(0,0,1;0rad)
  Tool = -> Compound978
FEATURE [Part::Cut] Cut635
  Base = -> Cut629
  Tool = -> Cylinder1904
FEATURE [Part::Fillet] Fillet028
  Base = -> Cut635
  Edges = 1 edges r=4: [Edge10]
FEATURE [Part::Compound] Compound981  label="sbouby_baze_silne022"
  Links = -> [Cylinder1919,Cylinder1907,Cylinder1908,Cylinder1912,Cylinder1913,Cylinder1914,Cylinder1901,Cylinder1902]
FEATURE [Part::Cut] Cut644
  Base = -> Cut630
  Tool = -> Compound981
FEATURE [Part::Cut] Cut645
  Base = -> Cut644
  Tool = -> Box556
FEATURE [Part::Cut] Cut646
  Base = -> Cut645
  Tool = -> Box555
FEATURE [Sketcher::SketchObject] Sketch015
  FullyConstrained = false
  sketch-geometry (1):
    g0: Circle CenterX=-186.411 CenterY=73.9277 CenterZ=0 NormalX=0 NormalY=0 NormalZ=1 AngleXU=0 Radius=59
FEATURE [Part::Extrusion] Extrude013
  Base = -> Sketch015
  Dir = (52,0,32)
  DirMode = 0
  FaceMakerClass = Part::FaceMakerBullseye
  LengthFwd = 61
  LengthRev = 0
  Placement = pos=(-134.5,74,-22) rot=(0,0,1;3.14159rad)
  Solid = true
  Symmetric = false
FEATURE [Part::Common] Common001
  Base = -> Fillet028
  Tool = -> Extrude013
FEATURE [Sketcher::SketchObject] Sketch016
  FullyConstrained = false
  sketch-geometry (1):
    g0: Circle CenterX=-186.411 CenterY=73.9277 CenterZ=0 NormalX=0 NormalY=0 NormalZ=1 AngleXU=0 Radius=59
FEATURE [Part::Extrusion] Extrude014
  Base = -> Sketch016
  Dir = (52,0,32)
  DirMode = 0
  FaceMakerClass = Part::FaceMakerBullseye
  LengthFwd = 61
  LengthRev = 0
  Placement = pos=(-134.5,74,-22) rot=(0,0,1;3.14159rad)
  Solid = true
  Symmetric = false
FEATURE [Part::Compound] Compound988  label="srouby_troj013"
  Links = -> [Cylinder1943,Cylinder1910]
FEATURE [Part::Compound] Compound991
  Links = -> [Cylinder1903,Cylinder1944]
FEATURE [Part::Cut] Cut647
  Base = -> Cut646
  Tool = -> Compound991
FEATURE [Part::Cut] Cut651
  Base = -> Cut647
  Tool = -> Compound988
FEATURE [Part::Cut] Cut636
  Base = -> Cut651
  Tool = -> Cylinder1946
FEATURE [Part::Fillet] Fillet029
  Base = -> Cut636
  Edges = 1 edges r=8: [Edge55]
FEATURE [Part::Fillet] Fillet027
  Base = -> Fillet029
  Edges = 1 edges r=8: [Edge38]
FEATURE [Part::Cut] Cut653
  Base = -> Cylinder1876
  Tool = -> Compound974
FEATURE [Part::Cylinder] Cylinder1948  label="Válec1948"
  Angle = 360
  AttacherType = Attacher::AttachEngine3D
  Height = 100
  Placement = pos=(34,16,-90) rot=(0,0,1;0rad)
  Radius = 4
FEATURE [Part::Cylinder] Cylinder1949  label="Válec1949"
  Angle = 360
  AttacherType = Attacher::AttachEngine3D
  Height = 100
  Placement = pos=(10,-36,-90) rot=(0,0,1;0rad)
  Radius = 4
FEATURE [Part::Cylinder] Cylinder1950  label="Válec1950"
  Angle = 360
  AttacherType = Attacher::AttachEngine3D
  Height = 100
  Placement = pos=(34,-16,-60) rot=(0,0,1;0rad)
  Radius = 1.5
FEATURE [Part::Cylinder] Cylinder1951  label="Válec1951"
  Angle = 360
  AttacherType = Attacher::AttachEngine3D
  Height = 100
  Placement = pos=(16,34,-90) rot=(0,0,1;0rad)
  Radius = 4
FEATURE [Part::Cylinder] Cylinder1952  label="Válec1952"
  Angle = 360
  AttacherType = Attacher::AttachEngine3D
  Height = 100
  Placement = pos=(-34,-16,-60) rot=(0,0,1;0rad)
  Radius = 1.5
FEATURE [Part::Cylinder] Cylinder1953  label="Válec1953"
  Angle = 360
  AttacherType = Attacher::AttachEngine3D
  Height = 100
  Placement = pos=(-16,-34,-60) rot=(0,0,1;0rad)
  Radius = 1.5
FEATURE [Part::Cylinder] Cylinder1954  label="Válec1954"
  Angle = 360
  AttacherType = Attacher::AttachEngine3D
  Height = 100
  Placement = pos=(34,16,-60) rot=(0,0,1;0rad)
  Radius = 1.5
FEATURE [Part::Cylinder] Cylinder1955  label="Válec1955"
  Angle = 360
  AttacherType = Attacher::AttachEngine3D
  Height = 100
  Placement = pos=(10,-36,-60) rot=(0,0,1;0rad)
  Radius = 1.5
FEATURE [Part::Cylinder] Cylinder1956  label="Válec1956"
  Angle = 360
  AttacherType = Attacher::AttachEngine3D
  Height = 100
  Placement = pos=(-34,16,-60) rot=(0,0,1;0rad)
  Radius = 1.5
FEATURE [Part::Cylinder] Cylinder1957  label="Válec1957"
  Angle = 360
  AttacherType = Attacher::AttachEngine3D
  Height = 160
  Placement = pos=(-18,0,-60) rot=(0,0,1;0rad)
  Radius = 17
FEATURE [Part::Cylinder] Cylinder1958  label="Válec1958"
  Angle = 360
  AttacherType = Attacher::AttachEngine3D
  Height = 100
  Placement = pos=(-16,34,-60) rot=(0,0,1;0rad)
  Radius = 1.5
FEATURE [Part::Cylinder] Cylinder1959  label="Válec1959"
  Angle = 360
  AttacherType = Attacher::AttachEngine3D
  Height = 100
  Placement = pos=(34,-16,-90) rot=(0,0,1;0rad)
  Radius = 4
FEATURE [Part::Cylinder] Cylinder1960  label="Válec1960"
  Angle = 360
  AttacherType = Attacher::AttachEngine3D
  Height = 100
  Placement = pos=(-34,-16,-90) rot=(0,0,1;0rad)
  Radius = 4
FEATURE [Part::Compound] Compound975  label="sbouby_baze_silne020"
  Links = -> [Cylinder1960,Cylinder1884,Cylinder1872,Cylinder1959,Cylinder1951,Cylinder1949,Cylinder1885,Cylinder1948]
FEATURE [Part::Cut] Cut652
  Base = -> Cut653
  Tool = -> Compound975
FEATURE [Part::Cylinder] Cylinder1961  label="Válec1961"
  Angle = 360
  AttacherType = Attacher::AttachEngine3D
  Height = 20
  Placement = pos=(103,-12,-20) rot=(0,0,1;0rad)
  Radius = 4
FEATURE [Part::Compound] Compound985  label="srouby_monoblok_silne017"
  Links = -> [Cylinder1961,Cylinder1906,Cylinder1918,Cylinder1916,Cylinder1921,Cylinder1915,Cylinder1909,Cylinder1932]
FEATURE [Part::Cylinder] Cylinder1962  label="Válec1962"
  Angle = 360
  AttacherType = Attacher::AttachEngine3D
  Height = 100
  Placement = pos=(1,12,-60) rot=(0,0,1;0rad)
  Radius = 1.5
FEATURE [Part::Cylinder] Cylinder1963  label="Válec1963"
  Angle = 360
  AttacherType = Attacher::AttachEngine3D
  Height = 100
  Placement = pos=(1,-12,-60) rot=(0,0,1;0rad)
  Radius = 1.5
FEATURE [Part::Cylinder] Cylinder1964  label="Válec1964"
  Angle = 360
  AttacherType = Attacher::AttachEngine3D
  Height = 100
  Placement = pos=(28,24,-60) rot=(0,0,1;0rad)
  Radius = 1.5
FEATURE [Part::Cylinder] Cylinder1965  label="Válec1965"
  Angle = 360
  AttacherType = Attacher::AttachEngine3D
  Height = 100
  Placement = pos=(13,-27,-60) rot=(0,0,1;0rad)
  Radius = 1.5
FEATURE [Part::Cylinder] Cylinder1966  label="Válec1966"
  Angle = 360
  AttacherType = Attacher::AttachEngine3D
  Height = 100
  Placement = pos=(91,-27,-60) rot=(0,0,1;0rad)
  Radius = 1.5
FEATURE [Part::Cylinder] Cylinder1967  label="Válec1967"
  Angle = 360
  AttacherType = Attacher::AttachEngine3D
  Height = 100
  Placement = pos=(76,24,-60) rot=(0,0,1;0rad)
  Radius = 1.5
FEATURE [Part::Cylinder] Cylinder1968  label="Válec1968"
  Angle = 360
  AttacherType = Attacher::AttachEngine3D
  Height = 100
  Placement = pos=(103,12,-60) rot=(0,0,1;0rad)
  Radius = 1.5
FEATURE [Part::Cylinder] Cylinder1969  label="Válec1969"
  Angle = 360
  AttacherType = Attacher::AttachEngine3D
  Height = 100
  Placement = pos=(103,-12,-60) rot=(0,0,1;0rad)
  Radius = 1.5
FEATURE [Part::Compound] Compound986  label="srouby_monoblok015"
  Links = -> [Cylinder1969,Cylinder1968,Cylinder1967,Cylinder1966,Cylinder1965,Cylinder1964,Cylinder1963,Cylinder1962]
FEATURE [Part::Cut] Cut634
  Base = -> Extrude014
  Tool = -> Compound986
FEATURE [Part::Cut] Cut639
  Base = -> Cut634
  Tool = -> Compound985
FEATURE [Part::Cylinder] Cylinder1970  label="Válec1970"
  Angle = 360
  AttacherType = Attacher::AttachEngine3D
  Height = 100
  Placement = pos=(-16,34,-60) rot=(0,0,1;0rad)
  Radius = 1.5
FEATURE [Part::Cylinder] Cylinder1971  label="Válec1971"
  Angle = 360
  AttacherType = Attacher::AttachEngine3D
  Height = 100
  Placement = pos=(16,34,-60) rot=(0,0,1;0rad)
  Radius = 1.5
FEATURE [Part::Compound] Compound971  label="sbouby_baze014"
  Links = -> [Cylinder1956,Cylinder1952,Cylinder1950,Cylinder1954,Cylinder1971,Cylinder1955,Cylinder1953,Cylinder1958]
FEATURE [Part::Cut] Cut650
  Base = -> Cut652
  Tool = -> Compound971
FEATURE [Part::Chamfer] Chamfer064
  Base = -> Cut650
  Edges = 1 edges r=4: [Edge3]
FEATURE [Part::Cut] Cut655
  Base = -> Chamfer064
  Placement = pos=(0,0,4) rot=(0,0,1;0rad)
  Tool = -> Compound973
FEATURE [Part::Cut] Cut654
  Base = -> Cut655
  Tool = -> Cylinder1957
FEATURE [Part::Fillet] Fillet004
  Base = -> Cut654
  Edges = 1 edges r=4: [Edge10]
FEATURE [Part::Common] Common
  Base = -> Fillet004
  Tool = -> Cylinder1886
FEATURE [Part::Cylinder] Cylinder1972  label="Válec1972"
  Angle = 360
  AttacherType = Attacher::AttachEngine3D
  Height = 100
  Placement = pos=(-16,-34,-60) rot=(0,0,1;0rad)
  Radius = 1.5
FEATURE [Part::Cylinder] Cylinder1973  label="Válec1973"
  Angle = 360
  AttacherType = Attacher::AttachEngine3D
  Height = 100
  Placement = pos=(34,16,-90) rot=(0,0,1;0rad)
  Radius = 4
FEATURE [Part::Cylinder] Cylinder1974  label="Válec1974"
  Angle = 360
  AttacherType = Attacher::AttachEngine3D
  Height = 100
  Placement = pos=(-34,16,-90) rot=(0,0,1;0rad)
  Radius = 4
FEATURE [Part::Cylinder] Cylinder1975  label="Válec1975"
  Angle = 360
  AttacherType = Attacher::AttachEngine3D
  Height = 32
  Placement = pos=(78,41,-46) rot=(0,0,1;0rad)
  Radius = 1.5
FEATURE [Part::Cylinder] Cylinder1976  label="Válec1976"
  Angle = 360
  AttacherType = Attacher::AttachEngine3D
  Height = 32
  Placement = pos=(26,41,-46) rot=(0,0,1;0rad)
  Radius = 1.5
FEATURE [Part::Compound] Compound990
  Links = -> [Cylinder1976,Cylinder1975]
FEATURE [Part::Box] Box557  label="Krychle557"
  AttacherType = Attacher::AttachEngine3D
  Height = 2
  Length = 6
  Placement = pos=(23,38,-22) rot=(0,0,1;0rad)
  Width = 6
FEATURE [Part::Box] Box558  label="Krychle558"
  AttacherType = Attacher::AttachEngine3D
  Height = 2
  Length = 6
  Placement = pos=(75,38,-22) rot=(0,0,1;0rad)
  Width = 6
FEATURE [Part::Compound] Compound989
  Links = -> [Box558,Box557]
FEATURE [Part::Cylinder] Cylinder1977  label="Válec1977"
  Angle = 360
  AttacherType = Attacher::AttachEngine3D
  Height = 100
  Placement = pos=(14,0,-18) rot=(0,0,1;0rad)
  Radius = 4
FEATURE [Part::Cylinder] Cylinder1978  label="Válec1978"
  Angle = 360
  AttacherType = Attacher::AttachEngine3D
  Height = 100
  Placement = pos=(90,0,-18) rot=(0,0,1;0rad)
  Radius = 4
FEATURE [Part::Compound] Compound983  label="srouby_troj_silne014"
  Links = -> [Cylinder1978,Cylinder1977]
FEATURE [Part::Cylinder] Cylinder1979  label="Válec1979"
  Angle = 360
  AttacherType = Attacher::AttachEngine3D
  Height = 100
  Placement = pos=(14,0,-60) rot=(0,0,1;0rad)
  Radius = 1.5
FEATURE [Part::Cylinder] Cylinder1980  label="Válec1980"
  Angle = 360
  AttacherType = Attacher::AttachEngine3D
  Height = 100
  Placement = pos=(90,0,-60) rot=(0,0,1;0rad)
  Radius = 1.5
FEATURE [Part::Compound] Compound982  label="srouby_troj012"
  Links = -> [Cylinder1980,Cylinder1979]
FEATURE [Part::Box] Box559  label="Krychle559"
  AttacherType = Attacher::AttachEngine3D
  Height = 100
  Length = 200
  Placement = pos=(-60,44,-90) rot=(0,0,1;0rad)
  Width = 100
FEATURE [Part::Box] Box560  label="Krychle560"
  AttacherType = Attacher::AttachEngine3D
  Height = 100
  Length = 200
  Placement = pos=(-60,-134,-90) rot=(0,0,1;0rad)
  Width = 100
FEATURE [Part::Cylinder] Cylinder1981  label="Válec1981"
  Angle = 360
  AttacherType = Attacher::AttachEngine3D
  Height = 100
  Placement = pos=(10,-36,-60) rot=(0,0,1;0rad)
  Radius = 1.5
FEATURE [Part::Cylinder] Cylinder1982  label="Válec1982"
  Angle = 360
  AttacherType = Attacher::AttachEngine3D
  Height = 100
  Placement = pos=(34,16,-60) rot=(0,0,1;0rad)
  Radius = 1.5
FEATURE [Part::Cylinder] Cylinder1983  label="Válec1983"
  Angle = 360
  AttacherType = Attacher::AttachEngine3D
  Height = 100
  Placement = pos=(34,-16,-60) rot=(0,0,1;0rad)
  Radius = 1.5
FEATURE [Part::Cylinder] Cylinder1984  label="Válec1984"
  Angle = 360
  AttacherType = Attacher::AttachEngine3D
  Height = 100
  Placement = pos=(-34,-16,-60) rot=(0,0,1;0rad)
  Radius = 1.5
FEATURE [Part::Cylinder] Cylinder1985  label="Válec1985"
  Angle = 360
  AttacherType = Attacher::AttachEngine3D
  Height = 100
  Placement = pos=(-34,16,-60) rot=(0,0,1;0rad)
  Radius = 1.5
FEATURE [Part::Cylinder] Cylinder1986  label="Válec1986"
  Angle = 360
  AttacherType = Attacher::AttachEngine3D
  Height = 100
  Placement = pos=(16,34,-60) rot=(0,0,1;0rad)
  Radius = 1.5
FEATURE [Part::Compound] Compound984  label="sbouby_baze016"
  Links = -> [Cylinder1985,Cylinder1984,Cylinder1983,Cylinder1982,Cylinder1986,Cylinder1981,Cylinder1972,Cylinder1970]
FEATURE [Part::Cylinder] Cylinder1987  label="Válec1987"
  Angle = 360
  AttacherType = Attacher::AttachEngine3D
  Height = 100
  Placement = pos=(10,-36,-90) rot=(0,0,1;0rad)
  Radius = 4
FEATURE [Part::Cylinder] Cylinder1988  label="Válec1988"
  Angle = 360
  AttacherType = Attacher::AttachEngine3D
  Height = 100
  Placement = pos=(-16,-34,-90) rot=(0,0,1;0rad)
  Radius = 4
FEATURE [Part::Cylinder] Cylinder1989  label="Válec1989"
  Angle = 360
  AttacherType = Attacher::AttachEngine3D
  Height = 100
  Placement = pos=(34,-16,-90) rot=(0,0,1;0rad)
  Radius = 4
FEATURE [Part::Compound] Compound987  label="sbouby_baze_silne023"
  Links = -> [Cylinder1900,Cylinder1941,Cylinder1988,Cylinder1989,Cylinder1945,Cylinder1987,Cylinder1974,Cylinder1973]
FEATURE [Part::Cut] Cut637
  Base = -> Cut639
  Tool = -> Compound987
FEATURE [Part::Cut] Cut641
  Base = -> Cut637
  Tool = -> Compound984
FEATURE [Part::Cut] Cut642
  Base = -> Cut641
  Tool = -> Box560
FEATURE [Part::Cut] Cut640
  Base = -> Cut642
  Tool = -> Box559
FEATURE [Part::Cut] Cut638
  Base = -> Cut640
  Tool = -> Compound989
FEATURE [Part::Cut] Cut631
  Base = -> Cut638
  Tool = -> Compound990
FEATURE [Part::Cut] Cut632
  Base = -> Cut631
  Tool = -> Compound982
FEATURE [Part::Cut] Cut643
  Base = -> Cut632
  Tool = -> Compound983
FEATURE [Part::Chamfer] Chamfer068
  Base = -> Cut643
  Edges = 1 edges r=4: [Edge44]
FEATURE [Part::Chamfer] Chamfer065
  Base = -> Chamfer068
  Edges = 1 edges r=3: [Edge6]
FEATURE [Part::Chamfer] Chamfer066
  Base = -> Chamfer065
  Edges = 1 edges r=3: [Edge7]
FEATURE [Part::Cut] Cut633
  Base = -> Chamfer066
  Tool = -> Cylinder1897
FEATURE [Part::Fillet] Fillet026
  Base = -> Cut633
  Edges = 2 edges r=3: [Edge4,Edge36]
FEATURE [Part::Compound] Compound972  label="Base_deep-neck-holed_v2"
  Links = -> [Fillet026,Fillet027,Common,Common001]
FEATURE [Sketcher::SketchObject] Sketch017
  FullyConstrained = false
  sketch-geometry (1):
    g0: Circle CenterX=-186.411 CenterY=73.9277 CenterZ=0 NormalX=0 NormalY=0 NormalZ=1 AngleXU=0 Radius=59
FEATURE [Part::Extrusion] Extrude015
  Base = -> Sketch017
  Dir = (40,0,32)
  DirMode = 0
  FaceMakerClass = Part::FaceMakerBullseye
  LengthFwd = 67
  LengthRev = 0
  Placement = pos=(-134.5,74,-22) rot=(0,0,1;3.14159rad)
  Solid = true
  Symmetric = false
FEATURE [Sketcher::SketchObject] Sketch018
  FullyConstrained = false
  sketch-geometry (1):
    g0: Circle CenterX=-186.411 CenterY=73.9277 CenterZ=0 NormalX=0 NormalY=0 NormalZ=1 AngleXU=0 Radius=59
FEATURE [Part::Cylinder] Cylinder1990  label="Válec1990"
  Angle = 360
  AttacherType = Attacher::AttachEngine3D
  Height = 100
  Placement = pos=(34,-16,-90) rot=(0,0,1;0rad)
  Radius = 4
FEATURE [Part::Cylinder] Cylinder1991  label="Válec1991"
  Angle = 360
  AttacherType = Attacher::AttachEngine3D
  Height = 100
  Placement = pos=(-16,-34,-90) rot=(0,0,1;0rad)
  Radius = 4
FEATURE [Part::Cylinder] Cylinder1992  label="Válec1992"
  Angle = 360
  AttacherType = Attacher::AttachEngine3D
  Height = 100
  Placement = pos=(14,0,-18) rot=(0,0,1;0rad)
  Radius = 4
FEATURE [Part::Cylinder] Cylinder1993  label="Válec1993"
  Angle = 360
  AttacherType = Attacher::AttachEngine3D
  Height = 100
  Placement = pos=(90,0,-18) rot=(0,0,1;0rad)
  Radius = 4
FEATURE [Part::Cylinder] Cylinder1994  label="Válec1994"
  Angle = 360
  AttacherType = Attacher::AttachEngine3D
  Height = 40
  Placement = pos=(1,12,-18) rot=(0,0,1;0rad)
  Radius = 4
FEATURE [Part::Cylinder] Cylinder1995  label="Válec1995"
  Angle = 360
  AttacherType = Attacher::AttachEngine3D
  Height = 40
  Placement = pos=(1,-12,-18) rot=(0,0,1;0rad)
  Radius = 4
FEATURE [Part::Cylinder] Cylinder1996  label="Válec1996"
  Angle = 360
  AttacherType = Attacher::AttachEngine3D
  Height = 40
  Placement = pos=(28,24,-18) rot=(0,0,1;0rad)
  Radius = 4
FEATURE [Part::Cylinder] Cylinder1997  label="Válec1997"
  Angle = 360
  AttacherType = Attacher::AttachEngine3D
  Height = 40
  Placement = pos=(13,-27,-18) rot=(0,0,1;0rad)
  Radius = 4
FEATURE [Part::Cylinder] Cylinder1998  label="Válec1998"
  Angle = 360
  AttacherType = Attacher::AttachEngine3D
  Height = 20
  Placement = pos=(91,-27,-18) rot=(0,0,1;0rad)
  Radius = 4
FEATURE [Part::Cylinder] Cylinder1999  label="Válec1999"
  Angle = 360
  AttacherType = Attacher::AttachEngine3D
  Height = 20
  Placement = pos=(76,24,-18) rot=(0,0,1;0rad)
  Radius = 4
FEATURE [Part::Cylinder] Cylinder2000  label="Válec2000"
  Angle = 360
  AttacherType = Attacher::AttachEngine3D
  Height = 20
  Placement = pos=(103,12,-20) rot=(0,0,1;0rad)
  Radius = 4
FEATURE [Part::Cylinder] Cylinder2001  label="Válec2001"
  Angle = 360
  AttacherType = Attacher::AttachEngine3D
  Height = 16
  Placement = pos=(0,0,2) rot=(0,0,1;0rad)
  Radius = 59
FEATURE [Part::Cylinder] Cylinder2002  label="Válec2002"
  Angle = 360
  AttacherType = Attacher::AttachEngine3D
  Height = 100
  Placement = pos=(-16,34,-60) rot=(0,0,1;0rad)
  Radius = 1.5
FEATURE [Part::Cylinder] Cylinder2003  label="Válec2003"
  Angle = 360
  AttacherType = Attacher::AttachEngine3D
  Height = 100
  Placement = pos=(-16,-34,-60) rot=(0,0,1;0rad)
  Radius = 1.5
FEATURE [Part::Cylinder] Cylinder2004  label="Válec2004"
  Angle = 360
  AttacherType = Attacher::AttachEngine3D
  Height = 100
  Placement = pos=(10,-36,-60) rot=(0,0,1;0rad)
  Radius = 1.5
FEATURE [Part::Cylinder] Cylinder2005  label="Válec2005"
  Angle = 360
  AttacherType = Attacher::AttachEngine3D
  Height = 100
  Placement = pos=(16,34,-60) rot=(0,0,1;0rad)
  Radius = 1.5
FEATURE [Part::Cylinder] Cylinder2006  label="Válec2006"
  Angle = 360
  AttacherType = Attacher::AttachEngine3D
  Height = 100
  Placement = pos=(-34,-16,-60) rot=(0,0,1;0rad)
  Radius = 1.5
FEATURE [Part::Cylinder] Cylinder2007  label="Válec2007"
  Angle = 360
  AttacherType = Attacher::AttachEngine3D
  Height = 20
  Placement = pos=(103,-12,-20) rot=(0,0,1;0rad)
  Radius = 4
FEATURE [Part::Cylinder] Cylinder2008  label="Válec2008"
  Angle = 360
  AttacherType = Attacher::AttachEngine3D
  Height = 100
  Placement = pos=(34,16,-60) rot=(0,0,1;0rad)
  Radius = 1.5
FEATURE [Part::Cylinder] Cylinder2009  label="Válec2009"
  Angle = 360
  AttacherType = Attacher::AttachEngine3D
  Height = 100
  Placement = pos=(34,-16,-60) rot=(0,0,1;0rad)
  Radius = 1.5
FEATURE [Part::Cylinder] Cylinder2010  label="Válec2010"
  Angle = 360
  AttacherType = Attacher::AttachEngine3D
  Height = 100
  Placement = pos=(-16,34,-90) rot=(0,0,1;0rad)
  Radius = 4
FEATURE [Part::Cylinder] Cylinder2011  label="Válec2011"
  Angle = 360
  AttacherType = Attacher::AttachEngine3D
  Height = 100
  Placement = pos=(-34,-16,-90) rot=(0,0,1;0rad)
  Radius = 4
FEATURE [Part::Cylinder] Cylinder2012  label="Válec2012"
  Angle = 360
  AttacherType = Attacher::AttachEngine3D
  Height = 100
  Placement = pos=(-34,16,-60) rot=(0,0,1;0rad)
  Radius = 1.5
FEATURE [Part::Cylinder] Cylinder2013  label="Válec2013"
  Angle = 360
  AttacherType = Attacher::AttachEngine3D
  Height = 160
  Placement = pos=(-18,0,-60) rot=(0,0,1;0rad)
  Radius = 17
FEATURE [Part::Cylinder] Cylinder2014  label="Válec2014"
  Angle = 360
  AttacherType = Attacher::AttachEngine3D
  Height = 16
  Placement = pos=(-0.5,0,19.85) rot=(0,0,1;0rad)
  Radius = 59
FEATURE [Part::Cylinder] Cylinder2015  label="Válec2015"
  Angle = 360
  AttacherType = Attacher::AttachEngine3D
  Height = 100
  Placement = pos=(10,-36,-90) rot=(0,0,1;0rad)
  Radius = 4
FEATURE [Part::Cylinder] Cylinder2016  label="Válec2016"
  Angle = 360
  AttacherType = Attacher::AttachEngine3D
  Height = 100
  Placement = pos=(-34,16,-90) rot=(0,0,1;0rad)
  Radius = 4
FEATURE [Part::Cylinder] Cylinder2017  label="Válec2017"
  Angle = 360
  AttacherType = Attacher::AttachEngine3D
  Height = 100
  Placement = pos=(16,34,-90) rot=(0,0,1;0rad)
  Radius = 4
FEATURE [Part::Cylinder] Cylinder2018  label="Válec2018"
  Angle = 360
  AttacherType = Attacher::AttachEngine3D
  Height = 100
  Placement = pos=(34,16,-90) rot=(0,0,1;0rad)
  Radius = 4
FEATURE [Part::Cylinder] Cylinder2019  label="Válec2019"
  Angle = 360
  AttacherType = Attacher::AttachEngine3D
  Height = 100
  Placement = pos=(34,-16,-90) rot=(0,0,1;0rad)
  Radius = 4
FEATURE [Part::Cylinder] Cylinder2020  label="Válec2020"
  Angle = 360
  AttacherType = Attacher::AttachEngine3D
  Height = 100
  Placement = pos=(-16,-34,-90) rot=(0,0,1;0rad)
  Radius = 4
FEATURE [Part::Cylinder] Cylinder2021  label="Válec2021"
  Angle = 360
  AttacherType = Attacher::AttachEngine3D
  Height = 100
  Placement = pos=(14,0,-18) rot=(0,0,1;0rad)
  Radius = 4
FEATURE [Part::Cylinder] Cylinder2022  label="Válec2022"
  Angle = 360
  AttacherType = Attacher::AttachEngine3D
  Height = 100
  Placement = pos=(90,0,-18) rot=(0,0,1;0rad)
  Radius = 4
FEATURE [Part::Cylinder] Cylinder2023  label="Válec2023"
  Angle = 360
  AttacherType = Attacher::AttachEngine3D
  Height = 40
  Placement = pos=(1,12,-18) rot=(0,0,1;0rad)
  Radius = 4
FEATURE [Part::Cylinder] Cylinder2024  label="Válec2024"
  Angle = 360
  AttacherType = Attacher::AttachEngine3D
  Height = 40
  Placement = pos=(1,-12,-18) rot=(0,0,1;0rad)
  Radius = 4
FEATURE [Part::Cylinder] Cylinder2025  label="Válec2025"
  Angle = 360
  AttacherType = Attacher::AttachEngine3D
  Height = 40
  Placement = pos=(28,24,-18) rot=(0,0,1;0rad)
  Radius = 4
FEATURE [Part::Cylinder] Cylinder2026  label="Válec2026"
  Angle = 360
  AttacherType = Attacher::AttachEngine3D
  Height = 40
  Placement = pos=(13,-27,-18) rot=(0,0,1;0rad)
  Radius = 4
FEATURE [Part::Cylinder] Cylinder2027  label="Válec2027"
  Angle = 360
  AttacherType = Attacher::AttachEngine3D
  Height = 20
  Placement = pos=(91,-27,-18) rot=(0,0,1;0rad)
  Radius = 4
FEATURE [Part::Cylinder] Cylinder2028  label="Válec2028"
  Angle = 360
  AttacherType = Attacher::AttachEngine3D
  Height = 20
  Placement = pos=(76,24,-18) rot=(0,0,1;0rad)
  Radius = 4
FEATURE [Part::Cylinder] Cylinder2029  label="Válec2029"
  Angle = 360
  AttacherType = Attacher::AttachEngine3D
  Height = 20
  Placement = pos=(103,12,-20) rot=(0,0,1;0rad)
  Radius = 4
FEATURE [Part::Cylinder] Cylinder2030  label="Válec2030"
  Angle = 360
  AttacherType = Attacher::AttachEngine3D
  Height = 16
  Placement = pos=(0,0,2) rot=(0,0,1;0rad)
  Radius = 59
FEATURE [Part::Cylinder] Cylinder2031  label="Válec2031"
  Angle = 360
  AttacherType = Attacher::AttachEngine3D
  Height = 100
  Placement = pos=(1,12,-60) rot=(0,0,1;0rad)
  Radius = 1.5
FEATURE [Part::Cylinder] Cylinder2032  label="Válec2032"
  Angle = 360
  AttacherType = Attacher::AttachEngine3D
  Height = 100
  Placement = pos=(1,12,-60) rot=(0,0,1;0rad)
  Radius = 1.5
FEATURE [Part::Cylinder] Cylinder2033  label="Válec2033"
  Angle = 360
  AttacherType = Attacher::AttachEngine3D
  Height = 100
  Placement = pos=(-16,-34,-90) rot=(0,0,1;0rad)
  Radius = 4
FEATURE [Part::Cylinder] Cylinder2034  label="Válec2034"
  Angle = 360
  AttacherType = Attacher::AttachEngine3D
  Height = 100
  Placement = pos=(-34,16,-90) rot=(0,0,1;0rad)
  Radius = 4
FEATURE [Part::Cylinder] Cylinder2035  label="Válec2035"
  Angle = 360
  AttacherType = Attacher::AttachEngine3D
  Height = 32
  Placement = pos=(26,41,-42) rot=(0,0,1;0rad)
  Radius = 1.5
FEATURE [Part::Cylinder] Cylinder2036  label="Válec2036"
  Angle = 360
  AttacherType = Attacher::AttachEngine3D
  Height = 100
  Placement = pos=(-16,34,-60) rot=(0,0,1;0rad)
  Radius = 1.5
FEATURE [Part::Cylinder] Cylinder2037  label="Válec2037"
  Angle = 360
  AttacherType = Attacher::AttachEngine3D
  Height = 100
  Placement = pos=(-16,-34,-60) rot=(0,0,1;0rad)
  Radius = 1.5
FEATURE [Part::Cylinder] Cylinder2038  label="Válec2038"
  Angle = 360
  AttacherType = Attacher::AttachEngine3D
  Height = 100
  Placement = pos=(10,-36,-60) rot=(0,0,1;0rad)
  Radius = 1.5
FEATURE [Part::Cylinder] Cylinder2039  label="Válec2039"
  Angle = 360
  AttacherType = Attacher::AttachEngine3D
  Height = 100
  Placement = pos=(16,34,-60) rot=(0,0,1;0rad)
  Radius = 1.5
FEATURE [Part::Cylinder] Cylinder2040  label="Válec2040"
  Angle = 360
  AttacherType = Attacher::AttachEngine3D
  Height = 100
  Placement = pos=(1,-12,-60) rot=(0,0,1;0rad)
  Radius = 1.5
FEATURE [Part::Cylinder] Cylinder2041  label="Válec2041"
  Angle = 360
  AttacherType = Attacher::AttachEngine3D
  Height = 100
  Placement = pos=(28,24,-60) rot=(0,0,1;0rad)
  Radius = 1.5
FEATURE [Part::Cylinder] Cylinder2042  label="Válec2042"
  Angle = 360
  AttacherType = Attacher::AttachEngine3D
  Height = 100
  Placement = pos=(-34,-16,-60) rot=(0,0,1;0rad)
  Radius = 1.5
FEATURE [Part::Cylinder] Cylinder2043  label="Válec2043"
  Angle = 360
  AttacherType = Attacher::AttachEngine3D
  Height = 32
  Placement = pos=(78,41,-42) rot=(0,0,1;0rad)
  Radius = 1.5
FEATURE [Part::Cylinder] Cylinder2044  label="Válec2044"
  Angle = 360
  AttacherType = Attacher::AttachEngine3D
  Height = 100
  Placement = pos=(34,16,-90) rot=(0,0,1;0rad)
  Radius = 4
FEATURE [Part::Cylinder] Cylinder2045  label="Válec2045"
  Angle = 360
  AttacherType = Attacher::AttachEngine3D
  Height = 100
  Placement = pos=(16,-34,-90) rot=(0,0,1;0rad)
  Radius = 4
FEATURE [Part::Cylinder] Cylinder2046  label="Válec2046"
  Angle = 360
  AttacherType = Attacher::AttachEngine3D
  Height = 100
  Placement = pos=(-16,34,-90) rot=(0,0,1;0rad)
  Radius = 4
FEATURE [Part::Cylinder] Cylinder2047  label="Válec2047"
  Angle = 360
  AttacherType = Attacher::AttachEngine3D
  Height = 100
  Placement = pos=(-34,-16,-90) rot=(0,0,1;0rad)
  Radius = 4
FEATURE [Part::Cylinder] Cylinder2048  label="Válec2048"
  Angle = 360
  AttacherType = Attacher::AttachEngine3D
  Height = 100
  Placement = pos=(16,34,-90) rot=(0,0,1;0rad)
  Radius = 4
FEATURE [Part::Cylinder] Cylinder2049  label="Válec2049"
  Angle = 360
  AttacherType = Attacher::AttachEngine3D
  Height = 100
  Placement = pos=(34,-16,-90) rot=(0,0,1;0rad)
  Radius = 4
FEATURE [Part::Cylinder] Cylinder2050  label="Válec2050"
  Angle = 360
  AttacherType = Attacher::AttachEngine3D
  Height = 20
  Placement = pos=(103,-12,-20) rot=(0,0,1;0rad)
  Radius = 4
FEATURE [Part::Box] Box561  label="Krychle561"
  AttacherType = Attacher::AttachEngine3D
  Height = 100
  Length = 200
  Placement = pos=(-60,44,-90) rot=(0,0,1;0rad)
  Width = 100
FEATURE [Part::Box] Box562  label="Krychle562"
  AttacherType = Attacher::AttachEngine3D
  Height = 100
  Length = 200
  Placement = pos=(-60,-130,-90) rot=(0,0,1;0rad)
  Width = 100
FEATURE [Part::Cylinder] Cylinder2051  label="Válec2051"
  Angle = 360
  AttacherType = Attacher::AttachEngine3D
  Height = 100
  Placement = pos=(13,-27,-60) rot=(0,0,1;0rad)
  Radius = 1.5
FEATURE [Part::Cylinder] Cylinder2052  label="Válec2052"
  Angle = 360
  AttacherType = Attacher::AttachEngine3D
  Height = 100
  Placement = pos=(91,-27,-60) rot=(0,0,1;0rad)
  Radius = 1.5
FEATURE [Part::Cylinder] Cylinder2053  label="Válec2053"
  Angle = 360
  AttacherType = Attacher::AttachEngine3D
  Height = 100
  Placement = pos=(76,24,-60) rot=(0,0,1;0rad)
  Radius = 1.5
FEATURE [Part::Cylinder] Cylinder2054  label="Válec2054"
  Angle = 360
  AttacherType = Attacher::AttachEngine3D
  Height = 100
  Placement = pos=(103,12,-60) rot=(0,0,1;0rad)
  Radius = 1.5
FEATURE [Part::Cylinder] Cylinder2055  label="Válec2055"
  Angle = 360
  AttacherType = Attacher::AttachEngine3D
  Height = 100
  Placement = pos=(103,-12,-60) rot=(0,0,1;0rad)
  Radius = 1.5
FEATURE [Part::Cylinder] Cylinder2056  label="Válec2056"
  Angle = 360
  AttacherType = Attacher::AttachEngine3D
  Height = 4
  Placement = pos=(52,0,-26) rot=(0,0,1;0rad)
  Radius = 59
FEATURE [Part::Cylinder] Cylinder2057  label="Válec2057"
  Angle = 360
  AttacherType = Attacher::AttachEngine3D
  Height = 100
  Placement = pos=(34,16,-60) rot=(0,0,1;0rad)
  Radius = 1.5
FEATURE [Part::Cylinder] Cylinder2058  label="Válec2058"
  Angle = 360
  AttacherType = Attacher::AttachEngine3D
  Height = 100
  Placement = pos=(34,-16,-60) rot=(0,0,1;0rad)
  Radius = 1.5
FEATURE [Part::Cylinder] Cylinder2059  label="Válec2059"
  Angle = 360
  AttacherType = Attacher::AttachEngine3D
  Height = 100
  Placement = pos=(-16,34,-90) rot=(0,0,1;0rad)
  Radius = 4
FEATURE [Part::Cylinder] Cylinder2060  label="Válec2060"
  Angle = 360
  AttacherType = Attacher::AttachEngine3D
  Height = 100
  Placement = pos=(-34,-16,-90) rot=(0,0,1;0rad)
  Radius = 4
FEATURE [Part::Cylinder] Cylinder2061  label="Válec2061"
  Angle = 360
  AttacherType = Attacher::AttachEngine3D
  Height = 100
  Placement = pos=(-34,16,-60) rot=(0,0,1;0rad)
  Radius = 1.5
FEATURE [Part::Compound] Compound993  label="sbouby_baze017"
  Links = -> [Cylinder2061,Cylinder2042,Cylinder2058,Cylinder2057,Cylinder2039,Cylinder2038,Cylinder2037,Cylinder2036]
FEATURE [Part::Cylinder] Cylinder2062  label="Válec2062"
  Angle = 360
  AttacherType = Attacher::AttachEngine3D
  Height = 100
  Placement = pos=(90,0,-60) rot=(0,0,1;0rad)
  Radius = 1.5
FEATURE [Part::Box] Box563  label="Krychle563"
  AttacherType = Attacher::AttachEngine3D
  Height = 120
  Length = 200
  Placement = pos=(-60,44,-90) rot=(0,0,1;0rad)
  Width = 100
FEATURE [Part::Cylinder] Cylinder2063  label="Válec2063"
  Angle = 360
  AttacherType = Attacher::AttachEngine3D
  Height = 100
  Placement = pos=(14,0,-60) rot=(0,0,1;0rad)
  Radius = 1.5
FEATURE [Part::Box] Box564  label="Krychle564"
  AttacherType = Attacher::AttachEngine3D
  Height = 120
  Length = 200
  Placement = pos=(-60,-134,-90) rot=(0,0,1;0rad)
  Width = 100
FEATURE [Part::Cylinder] Cylinder2064  label="Válec2064"
  Angle = 360
  AttacherType = Attacher::AttachEngine3D
  Height = 100
  Placement = pos=(90,0,-60) rot=(0,0,1;0rad)
  Radius = 1.5
FEATURE [Part::Cylinder] Cylinder2065  label="Válec2065"
  Angle = 360
  AttacherType = Attacher::AttachEngine3D
  Height = 100
  Placement = pos=(10,-36,-60) rot=(0,0,1;0rad)
  Radius = 1.5
FEATURE [Part::Cylinder] Cylinder2066  label="Válec2066"
  Angle = 360
  AttacherType = Attacher::AttachEngine3D
  Height = 100
  Placement = pos=(34,16,-60) rot=(0,0,1;0rad)
  Radius = 1.5
FEATURE [Part::Cylinder] Cylinder2067  label="Válec2067"
  Angle = 360
  AttacherType = Attacher::AttachEngine3D
  Height = 160
  Placement = pos=(-18,0,-60) rot=(0,0,1;0rad)
  Radius = 17
FEATURE [Part::Cylinder] Cylinder2068  label="Válec2068"
  Angle = 360
  AttacherType = Attacher::AttachEngine3D
  Height = 160
  Placement = pos=(-18,0,-60) rot=(0,0,1;0rad)
  Radius = 17
FEATURE [Part::Cylinder] Cylinder2069  label="Válec2069"
  Angle = 360
  AttacherType = Attacher::AttachEngine3D
  Height = 100
  Placement = pos=(14,0,-18) rot=(0,0,1;0rad)
  Radius = 4
FEATURE [Part::Cylinder] Cylinder2070  label="Válec2070"
  Angle = 360
  AttacherType = Attacher::AttachEngine3D
  Height = 100
  Placement = pos=(-34,16,-90) rot=(0,0,1;0rad)
  Radius = 4
FEATURE [Part::Cylinder] Cylinder2071  label="Válec2071"
  Angle = 360
  AttacherType = Attacher::AttachEngine3D
  Height = 100
  Placement = pos=(90,0,-18) rot=(0,0,1;0rad)
  Radius = 4
FEATURE [Part::Cylinder] Cylinder2072  label="Válec2072"
  Angle = 360
  AttacherType = Attacher::AttachEngine3D
  Height = 100
  Placement = pos=(16,34,-90) rot=(0,0,1;0rad)
  Radius = 4
FEATURE [Part::Box] Box565  label="Krychle565"
  AttacherType = Attacher::AttachEngine3D
  Height = 2
  Length = 6
  Placement = pos=(23,38,-22) rot=(0,0,1;0rad)
  Width = 6
FEATURE [Part::Cylinder] Cylinder2073  label="Válec2073"
  Angle = 360
  AttacherType = Attacher::AttachEngine3D
  Height = 100
  Placement = pos=(34,-16,-60) rot=(0,0,1;0rad)
  Radius = 1.5
FEATURE [Part::Cylinder] Cylinder2074  label="Válec2074"
  Angle = 360
  AttacherType = Attacher::AttachEngine3D
  Height = 100
  Placement = pos=(-34,-16,-60) rot=(0,0,1;0rad)
  Radius = 1.5
FEATURE [Part::Cylinder] Cylinder2075  label="Válec2075"
  Angle = 360
  AttacherType = Attacher::AttachEngine3D
  Height = 100
  Placement = pos=(34,16,-90) rot=(0,0,1;0rad)
  Radius = 4
FEATURE [Part::Cylinder] Cylinder2076  label="Válec2076"
  Angle = 360
  AttacherType = Attacher::AttachEngine3D
  Height = 32
  Placement = pos=(78,41,-46) rot=(0,0,1;0rad)
  Radius = 1.5
FEATURE [Part::Cylinder] Cylinder2077  label="Válec2077"
  Angle = 360
  AttacherType = Attacher::AttachEngine3D
  Height = 100
  Placement = pos=(-34,16,-60) rot=(0,0,1;0rad)
  Radius = 1.5
FEATURE [Part::Cylinder] Cylinder2078  label="Válec2078"
  Angle = 360
  AttacherType = Attacher::AttachEngine3D
  Height = 160
  Placement = pos=(-18,0,-60) rot=(0,0,1;0rad)
  Radius = 17
FEATURE [Part::Cylinder] Cylinder2079  label="Válec2079"
  Angle = 360
  AttacherType = Attacher::AttachEngine3D
  Height = 100
  Placement = pos=(-16,34,-60) rot=(0,0,1;0rad)
  Radius = 1.5
FEATURE [Part::Cylinder] Cylinder2080  label="Válec2080"
  Angle = 360
  AttacherType = Attacher::AttachEngine3D
  Height = 100
  Placement = pos=(103,-12,-60) rot=(0,0,1;0rad)
  Radius = 1.5
FEATURE [Part::Cylinder] Cylinder2081  label="Válec2081"
  Angle = 360
  AttacherType = Attacher::AttachEngine3D
  Height = 100
  Placement = pos=(103,12,-60) rot=(0,0,1;0rad)
  Radius = 1.5
FEATURE [Part::Cylinder] Cylinder2082  label="Válec2082"
  Angle = 360
  AttacherType = Attacher::AttachEngine3D
  Height = 100
  Placement = pos=(76,24,-60) rot=(0,0,1;0rad)
  Radius = 1.5
FEATURE [Part::Cylinder] Cylinder2083  label="Válec2083"
  Angle = 360
  AttacherType = Attacher::AttachEngine3D
  Height = 100
  Placement = pos=(91,-27,-60) rot=(0,0,1;0rad)
  Radius = 1.5
FEATURE [Part::Cylinder] Cylinder2084  label="Válec2084"
  Angle = 360
  AttacherType = Attacher::AttachEngine3D
  Height = 100
  Placement = pos=(28,24,-60) rot=(0,0,1;0rad)
  Radius = 1.5
FEATURE [Part::Cylinder] Cylinder2085  label="Válec2085"
  Angle = 360
  AttacherType = Attacher::AttachEngine3D
  Height = 100
  Placement = pos=(1,-12,-60) rot=(0,0,1;0rad)
  Radius = 1.5
FEATURE [Part::Cylinder] Cylinder2086  label="Válec2086"
  Angle = 360
  AttacherType = Attacher::AttachEngine3D
  Height = 20
  Placement = pos=(103,-12,-20) rot=(0,0,1;0rad)
  Radius = 4
FEATURE [Part::Cylinder] Cylinder2087  label="Válec2087"
  Angle = 360
  AttacherType = Attacher::AttachEngine3D
  Height = 32
  Placement = pos=(76,24,-18) rot=(0,0,1;0rad)
  Radius = 4
FEATURE [Part::Cylinder] Cylinder2088  label="Válec2088"
  Angle = 360
  AttacherType = Attacher::AttachEngine3D
  Height = 20
  Placement = pos=(91,-27,-18) rot=(0,0,1;0rad)
  Radius = 4
FEATURE [Part::Cylinder] Cylinder2089  label="Válec2089"
  Angle = 360
  AttacherType = Attacher::AttachEngine3D
  Height = 40
  Placement = pos=(13,-27,-18) rot=(0,0,1;0rad)
  Radius = 4
FEATURE [Part::Cylinder] Cylinder2090  label="Válec2090"
  Angle = 360
  AttacherType = Attacher::AttachEngine3D
  Height = 40
  Placement = pos=(28,24,-18) rot=(0,0,1;0rad)
  Radius = 4
FEATURE [Part::Cylinder] Cylinder2091  label="Válec2091"
  Angle = 360
  AttacherType = Attacher::AttachEngine3D
  Height = 40
  Placement = pos=(1,-12,-18) rot=(0,0,1;0rad)
  Radius = 4
FEATURE [Part::Cylinder] Cylinder2092  label="Válec2092"
  Angle = 360
  AttacherType = Attacher::AttachEngine3D
  Height = 40
  Placement = pos=(1,12,-18) rot=(0,0,1;0rad)
  Radius = 4
FEATURE [Part::Cylinder] Cylinder2093  label="Válec2093"
  Angle = 360
  AttacherType = Attacher::AttachEngine3D
  Height = 20
  Placement = pos=(103,12,-20) rot=(0,0,1;0rad)
  Radius = 4
FEATURE [Part::Cylinder] Cylinder2094  label="Válec2094"
  Angle = 360
  AttacherType = Attacher::AttachEngine3D
  Height = 100
  Placement = pos=(13,-27,-60) rot=(0,0,1;0rad)
  Radius = 1.5
FEATURE [Part::Cylinder] Cylinder2095  label="Válec2095"
  Angle = 360
  AttacherType = Attacher::AttachEngine3D
  Height = 100
  Placement = pos=(-16,-34,-60) rot=(0,0,1;0rad)
  Radius = 1.5
FEATURE [Part::Cylinder] Cylinder2096  label="Válec2096"
  Angle = 360
  AttacherType = Attacher::AttachEngine3D
  Height = 100
  Placement = pos=(-34,-16,-90) rot=(0,0,1;0rad)
  Radius = 4
FEATURE [Part::Cylinder] Cylinder2097  label="Válec2097"
  Angle = 360
  AttacherType = Attacher::AttachEngine3D
  Height = 100
  Placement = pos=(-16,34,-90) rot=(0,0,1;0rad)
  Radius = 4
FEATURE [Part::Cylinder] Cylinder2098  label="Válec2098"
  Angle = 360
  AttacherType = Attacher::AttachEngine3D
  Height = 100
  Placement = pos=(16,34,-60) rot=(0,0,1;0rad)
  Radius = 1.5
FEATURE [Part::Cylinder] Cylinder2099  label="Válec2099"
  Angle = 360
  AttacherType = Attacher::AttachEngine3D
  Height = 100
  Placement = pos=(10,-36,-90) rot=(0,0,1;0rad)
  Radius = 4
FEATURE [Part::Cylinder] Cylinder2100  label="Válec2100"
  Angle = 360
  AttacherType = Attacher::AttachEngine3D
  Height = 100
  Placement = pos=(34,-16,-90) rot=(0,0,1;0rad)
  Radius = 4
FEATURE [Part::Box] Box566  label="Krychle566"
  AttacherType = Attacher::AttachEngine3D
  Height = 2
  Length = 6
  Placement = pos=(75,38,-22) rot=(0,0,1;0rad)
  Width = 6
FEATURE [Part::Cylinder] Cylinder2101  label="Válec2101"
  Angle = 360
  AttacherType = Attacher::AttachEngine3D
  Height = 32
  Placement = pos=(26,41,-46) rot=(0,0,1;0rad)
  Radius = 1.5
FEATURE [Part::Cylinder] Cylinder2102  label="Válec2102"
  Angle = 360
  AttacherType = Attacher::AttachEngine3D
  Height = 100
  Placement = pos=(-16,-34,-90) rot=(0,0,1;0rad)
  Radius = 4
FEATURE [Part::Cylinder] Cylinder2103  label="Válec2103"
  Angle = 360
  AttacherType = Attacher::AttachEngine3D
  Height = 100
  Placement = pos=(14,0,-60) rot=(0,0,1;0rad)
  Radius = 1.5
FEATURE [Part::Cylinder] Cylinder2104  label="Válec2104"
  Angle = 360
  AttacherType = Attacher::AttachEngine3D
  Height = 100
  Placement = pos=(10,-36,-90) rot=(0,0,1;0rad)
  Radius = 4
FEATURE [Part::Cylinder] Cylinder2105  label="Válec2105"
  Angle = 360
  AttacherType = Attacher::AttachEngine3D
  Height = 100
  Placement = pos=(-34,16,-90) rot=(0,0,1;0rad)
  Radius = 4
FEATURE [Part::Cylinder] Cylinder2106  label="Válec2106"
  Angle = 360
  AttacherType = Attacher::AttachEngine3D
  Height = 100
  Placement = pos=(16,34,-90) rot=(0,0,1;0rad)
  Radius = 4
FEATURE [Part::Cylinder] Cylinder2107  label="Válec2107"
  Angle = 360
  AttacherType = Attacher::AttachEngine3D
  Height = 100
  Placement = pos=(34,16,-90) rot=(0,0,1;0rad)
  Radius = 4
FEATURE [Part::Compound] Compound994  label="sbouby_baze018"
  Links = -> [Cylinder2012,Cylinder2006,Cylinder2009,Cylinder2008,Cylinder2005,Cylinder2004,Cylinder2003,Cylinder2002]
FEATURE [Part::Compound] Compound995  label="srouby_monoblok_silne018"
  Links = -> [Cylinder2007,Cylinder2000,Cylinder1999,Cylinder1998,Cylinder1997,Cylinder1996,Cylinder1995,Cylinder1994]
FEATURE [Part::Cut] Cut657
  Base = -> Cylinder2001
  Tool = -> Compound995
FEATURE [Part::Compound] Compound996  label="sbouby_baze_silne024"
  Links = -> [Cylinder2011,Cylinder2010,Cylinder1991,Cylinder1990,Cylinder2106,Cylinder2104,Cylinder2105,Cylinder2107]
FEATURE [Part::Cut] Cut661
  Base = -> Cut657
  Tool = -> Compound996
FEATURE [Part::Cut] Cut662
  Base = -> Cut661
  Tool = -> Compound994
FEATURE [Part::Chamfer] Chamfer069
  Base = -> Cut662
  Edges = 1 edges r=4: [Edge3]
FEATURE [Part::Compound] Compound997  label="srouby_troj_silne015"
  Links = -> [Cylinder1993,Cylinder1992]
FEATURE [Part::Extrusion] Extrude016
  Base = -> Sketch018
  Dir = (40,0,32)
  DirMode = 0
  FaceMakerClass = Part::FaceMakerBullseye
  LengthFwd = 67
  LengthRev = 0
  Placement = pos=(-134.5,74,-22) rot=(0,0,1;3.14159rad)
  Solid = true
  Symmetric = false
FEATURE [Part::Compound] Compound998
  Links = -> [Box566,Box565]
FEATURE [Part::Compound] Compound999  label="sbouby_baze_silne025"
  Links = -> [Cylinder2096,Cylinder2097,Cylinder2102,Cylinder2100,Cylinder2072,Cylinder2099,Cylinder2070,Cylinder2075]
  Placement = pos=(-0.5,0,12) rot=(0,0,1;0rad)
FEATURE [Part::Compound] Compound1000  label="srouby_monoblok016"
  Links = -> [Cylinder2080,Cylinder2081,Cylinder2082,Cylinder2083,Cylinder2094,Cylinder2084,Cylinder2085,Cylinder2031]
FEATURE [Part::Compound] Compound1001
  Links = -> [Cylinder2101,Cylinder2076]
FEATURE [Part::Compound] Compound1002  label="srouby_troj_silne016"
  Links = -> [Cylinder2071,Cylinder2069]
FEATURE [Part::Compound] Compound1003  label="srouby_troj014"
  Links = -> [Cylinder2062,Cylinder2103]
FEATURE [Part::Compound] Compound1004  label="srouby_monoblok017"
  Links = -> [Cylinder2055,Cylinder2054,Cylinder2053,Cylinder2052,Cylinder2051,Cylinder2041,Cylinder2040,Cylinder2032]
FEATURE [Part::Compound] Compound1005
  Links = -> [Cylinder2035,Cylinder2043]
FEATURE [Part::Compound] Compound1006  label="sbouby_baze_silne026"
  Links = -> [Cylinder2047,Cylinder2046,Cylinder2033,Cylinder2049,Cylinder2048,Cylinder2045,Cylinder2034,Cylinder2044]
  Placement = pos=(-0.5,0,0) rot=(0,0,1;0rad)
FEATURE [Part::Cut] Cut673
  Base = -> Extrude015
  Tool = -> Compound1000
FEATURE [Part::Cut] Cut676
  Base = -> Cylinder2056
  Tool = -> Compound1004
FEATURE [Part::Cut] Cut677
  Base = -> Cut676
  Tool = -> Compound1006
FEATURE [Part::Cut] Cut678
  Base = -> Cut677
  Tool = -> Box562
FEATURE [Part::Cut] Cut681
  Base = -> Cut678
  Tool = -> Box561
FEATURE [Part::Cut] Cut682
  Base = -> Cut681
  Tool = -> Compound1005
FEATURE [Part::Cut] Cut679
  Base = -> Cut682
  Tool = -> Compound1003
FEATURE [Part::Cut] Cut667
  Base = -> Cut679
  Tool = -> Cylinder2067
FEATURE [Part::Cut] Cut683
  Base = -> Chamfer069
  Placement = pos=(-0.5,0,14) rot=(0,0,1;0rad)
  Tool = -> Compound997
FEATURE [Part::Cut] Cut656
  Base = -> Cut683
  Tool = -> Cylinder2013
FEATURE [Part::Fillet] Fillet008
  Base = -> Cut656
  Edges = 1 edges r=4: [Edge11]
FEATURE [Part::Common] Common005
  Base = -> Extrude016
  Tool = -> Fillet008
FEATURE [Part::Compound] Compound1007  label="srouby_monoblok_silne019"
  Links = -> [Cylinder2050,Cylinder2029,Cylinder2028,Cylinder2027,Cylinder2026,Cylinder2025,Cylinder2024,Cylinder2023]
FEATURE [Part::Cut] Cut669
  Base = -> Cylinder2030
  Tool = -> Compound1007
FEATURE [Part::Compound] Compound1008  label="sbouby_baze_silne027"
  Links = -> [Cylinder2060,Cylinder2059,Cylinder2020,Cylinder2019,Cylinder2017,Cylinder2015,Cylinder2016,Cylinder2018]
FEATURE [Part::Cut] Cut670
  Base = -> Cut669
  Tool = -> Compound1008
FEATURE [Part::Cut] Cut674
  Base = -> Cut670
  Tool = -> Compound993
FEATURE [Part::Chamfer] Chamfer071
  Base = -> Cut674
  Edges = 1 edges r=4: [Edge3]
FEATURE [Part::Compound] Compound1009  label="srouby_troj_silne017"
  Links = -> [Cylinder2022,Cylinder2021]
FEATURE [Part::Cut] Cut675
  Base = -> Chamfer071
  Placement = pos=(-0.5,0,14) rot=(0,0,1;0rad)
  Tool = -> Compound1009
FEATURE [Part::Cut] Cut668
  Base = -> Cut675
  Tool = -> Cylinder2078
FEATURE [Part::Fillet] Fillet005
  Base = -> Cut667
  Edges = 2 edges r=8: [Edge55,Edge57]
FEATURE [Part::Fillet] Fillet007
  Base = -> Cut668
  Edges = 1 edges r=4: [Edge11]
  Placement = pos=(0,0,-0.15) rot=(0,0,1;0rad)
FEATURE [Part::Common] Common003
  Base = -> Fillet007
  Tool = -> Cylinder2014
FEATURE [Part::Compound] Compound1010  label="sbouby_baze019"
  Links = -> [Cylinder2077,Cylinder2074,Cylinder2073,Cylinder2066,Cylinder2098,Cylinder2065,Cylinder2095,Cylinder2079]
FEATURE [Part::Compound] Compound1011  label="srouby_monoblok_silne020"
  Links = -> [Cylinder2086,Cylinder2093,Cylinder2087,Cylinder2088,Cylinder2089,Cylinder2090,Cylinder2091,Cylinder2092]
FEATURE [Part::Cut] Cut672
  Base = -> Cut673
  Tool = -> Compound1011
FEATURE [Part::Cut] Cut664
  Base = -> Cut672
  Tool = -> Compound999
FEATURE [Part::Cut] Cut680
  Base = -> Cut664
  Tool = -> Compound1010
FEATURE [Part::Cut] Cut660
  Base = -> Cut680
  Tool = -> Box564
FEATURE [Part::Cut] Cut659
  Base = -> Cut660
  Tool = -> Box563
FEATURE [Part::Cut] Cut658
  Base = -> Cut659
  Tool = -> Compound998
FEATURE [Part::Cut] Cut663
  Base = -> Cut658
  Tool = -> Compound1001
FEATURE [Part::Compound] Compound1012  label="srouby_troj015"
  Links = -> [Cylinder2064,Cylinder2063]
FEATURE [Part::Cut] Cut665
  Base = -> Cut663
  Tool = -> Compound1012
FEATURE [Part::Cut] Cut671
  Base = -> Cut665
  Tool = -> Compound1002
FEATURE [Part::Chamfer] Chamfer072
  Base = -> Cut671
  Edges = 1 edges r=4: [Edge44]
FEATURE [Part::Chamfer] Chamfer070
  Base = -> Chamfer072
  Edges = 2 edges r=3: [Edge4,Edge6]
FEATURE [Part::Cut] Cut666
  Base = -> Chamfer070
  Tool = -> Cylinder2068
FEATURE [Part::Fillet] Fillet006
  Base = -> Cut666
  Edges = 2 edges r=3: [Edge3,Edge34]
FEATURE [Part::Compound] Compound992  label="Base_deep-highneck-holed_v2"
  Links = -> [Fillet005,Fillet006,Common005,Common003]
FEATURE [Sketcher::SketchObject] Sketch019
  FullyConstrained = false
  sketch-geometry (1):
    g0: Circle CenterX=-186.411 CenterY=73.9277 CenterZ=0 NormalX=0 NormalY=0 NormalZ=1 AngleXU=0 Radius=59
FEATURE [Part::Extrusion] Extrude018
  Base = -> Sketch019
  Dir = (40,0,32)
  DirMode = 0
  FaceMakerClass = Part::FaceMakerBullseye
  LengthFwd = 67
  LengthRev = 0
  Placement = pos=(-134.5,74,-22) rot=(0,0,1;3.14159rad)
  Solid = true
  Symmetric = false
FEATURE [Part::Cylinder] Cylinder2108  label="Válec2108"
  Angle = 360
  AttacherType = Attacher::AttachEngine3D
  Height = 100
  Placement = pos=(-34,16,-90) rot=(0,0,1;0rad)
  Radius = 4
FEATURE [Part::Cylinder] Cylinder2109  label="Válec2109"
  Angle = 360
  AttacherType = Attacher::AttachEngine3D
  Height = 100
  Placement = pos=(34,-16,-90) rot=(0,0,1;0rad)
  Radius = 4
FEATURE [Part::Cylinder] Cylinder2110  label="Válec2110"
  Angle = 360
  AttacherType = Attacher::AttachEngine3D
  Height = 100
  Placement = pos=(90,0,-18) rot=(0,0,1;0rad)
  Radius = 4
FEATURE [Part::Cylinder] Cylinder2111  label="Válec2111"
  Angle = 360
  AttacherType = Attacher::AttachEngine3D
  Height = 20
  Placement = pos=(76,24,-18) rot=(0,0,1;0rad)
  Radius = 4
FEATURE [Part::Cylinder] Cylinder2112  label="Válec2112"
  Angle = 360
  AttacherType = Attacher::AttachEngine3D
  Height = 100
  Placement = pos=(-34,-16,-60) rot=(0,0,1;0rad)
  Radius = 1.5
FEATURE [Part::Cylinder] Cylinder2113  label="Válec2113"
  Angle = 360
  AttacherType = Attacher::AttachEngine3D
  Height = 40
  Placement = pos=(1,-12,-18) rot=(0,0,1;0rad)
  Radius = 4
FEATURE [Part::Cylinder] Cylinder2114  label="Válec2114"
  Angle = 360
  AttacherType = Attacher::AttachEngine3D
  Height = 20
  Placement = pos=(91,-27,-18) rot=(0,0,1;0rad)
  Radius = 4
FEATURE [Part::Cylinder] Cylinder2115  label="Válec2115"
  Angle = 360
  AttacherType = Attacher::AttachEngine3D
  Height = 100
  Placement = pos=(-16,-34,-90) rot=(0,0,1;0rad)
  Radius = 4
FEATURE [Part::Cylinder] Cylinder2116  label="Válec2116"
  Angle = 360
  AttacherType = Attacher::AttachEngine3D
  Height = 40
  Placement = pos=(28,24,-18) rot=(0,0,1;0rad)
  Radius = 4
FEATURE [Part::Cylinder] Cylinder2117  label="Válec2117"
  Angle = 360
  AttacherType = Attacher::AttachEngine3D
  Height = 100
  Placement = pos=(10,-36,-60) rot=(0,0,1;0rad)
  Radius = 1.5
FEATURE [Part::Cylinder] Cylinder2118  label="Válec2118"
  Angle = 360
  AttacherType = Attacher::AttachEngine3D
  Height = 100
  Placement = pos=(-16,34,-60) rot=(0,0,1;0rad)
  Radius = 1.5
FEATURE [Part::Cylinder] Cylinder2119  label="Válec2119"
  Angle = 360
  AttacherType = Attacher::AttachEngine3D
  Height = 100
  Placement = pos=(-34,-16,-90) rot=(0,0,1;0rad)
  Radius = 4
FEATURE [Part::Cylinder] Cylinder2120  label="Válec2120"
  Angle = 360
  AttacherType = Attacher::AttachEngine3D
  Height = 100
  Placement = pos=(14,0,-18) rot=(0,0,1;0rad)
  Radius = 4
FEATURE [Part::Cylinder] Cylinder2121  label="Válec2121"
  Angle = 360
  AttacherType = Attacher::AttachEngine3D
  Height = 20
  Placement = pos=(103,12,-20) rot=(0,0,1;0rad)
  Radius = 4
FEATURE [Part::Cylinder] Cylinder2122  label="Válec2122"
  Angle = 360
  AttacherType = Attacher::AttachEngine3D
  Height = 40
  Placement = pos=(1,12,-18) rot=(0,0,1;0rad)
  Radius = 4
FEATURE [Part::Cylinder] Cylinder2123  label="Válec2123"
  Angle = 360
  AttacherType = Attacher::AttachEngine3D
  Height = 100
  Placement = pos=(-16,-34,-60) rot=(0,0,1;0rad)
  Radius = 1.5
FEATURE [Part::Cylinder] Cylinder2124  label="Válec2124"
  Angle = 360
  AttacherType = Attacher::AttachEngine3D
  Height = 40
  Placement = pos=(13,-27,-18) rot=(0,0,1;0rad)
  Radius = 4
FEATURE [Part::Cylinder] Cylinder2125  label="Válec2125"
  Angle = 360
  AttacherType = Attacher::AttachEngine3D
  Height = 160
  Placement = pos=(-18,0,-60) rot=(0,0,1;0rad)
  Radius = 17
FEATURE [Part::Cylinder] Cylinder2126  label="Válec2126"
  Angle = 360
  AttacherType = Attacher::AttachEngine3D
  Height = 100
  Placement = pos=(-34,16,-90) rot=(0,0,1;0rad)
  Radius = 4
FEATURE [Part::Cylinder] Cylinder2127  label="Válec2127"
  Angle = 360
  AttacherType = Attacher::AttachEngine3D
  Height = 100
  Placement = pos=(-34,16,-60) rot=(0,0,1;0rad)
  Radius = 1.5
FEATURE [Part::Cylinder] Cylinder2128  label="Válec2128"
  Angle = 360
  AttacherType = Attacher::AttachEngine3D
  Height = 20
  Placement = pos=(103,-12,-20) rot=(0,0,1;0rad)
  Radius = 4
FEATURE [Part::Cylinder] Cylinder2129  label="Válec2129"
  Angle = 360
  AttacherType = Attacher::AttachEngine3D
  Height = 16
  Placement = pos=(0,0,2) rot=(0,0,1;0rad)
  Radius = 59
FEATURE [Part::Cylinder] Cylinder2130  label="Válec2130"
  Angle = 360
  AttacherType = Attacher::AttachEngine3D
  Height = 100
  Placement = pos=(-16,34,-90) rot=(0,0,1;0rad)
  Radius = 4
FEATURE [Part::Cylinder] Cylinder2131  label="Válec2131"
  Angle = 360
  AttacherType = Attacher::AttachEngine3D
  Height = 100
  Placement = pos=(10,-36,-90) rot=(0,0,1;0rad)
  Radius = 4
FEATURE [Part::Cylinder] Cylinder2132  label="Válec2132"
  Angle = 360
  AttacherType = Attacher::AttachEngine3D
  Height = 100
  Placement = pos=(1,12,-60) rot=(0,0,1;0rad)
  Radius = 1.5
FEATURE [Part::Cylinder] Cylinder2133  label="Válec2133"
  Angle = 360
  AttacherType = Attacher::AttachEngine3D
  Height = 20
  Placement = pos=(103,12,-20) rot=(0,0,1;0rad)
  Radius = 4
FEATURE [Part::Cylinder] Cylinder2134  label="Válec2134"
  Angle = 360
  AttacherType = Attacher::AttachEngine3D
  Height = 100
  Placement = pos=(14,0,-18) rot=(0,0,1;0rad)
  Radius = 4
FEATURE [Part::Cylinder] Cylinder2135  label="Válec2135"
  Angle = 360
  AttacherType = Attacher::AttachEngine3D
  Height = 100
  Placement = pos=(16,34,-60) rot=(0,0,1;0rad)
  Radius = 1.5
FEATURE [Part::Cylinder] Cylinder2136  label="Válec2136"
  Angle = 360
  AttacherType = Attacher::AttachEngine3D
  Height = 100
  Placement = pos=(34,-16,-60) rot=(0,0,1;0rad)
  Radius = 1.5
FEATURE [Part::Cylinder] Cylinder2137  label="Válec2137"
  Angle = 360
  AttacherType = Attacher::AttachEngine3D
  Height = 100
  Placement = pos=(34,16,-60) rot=(0,0,1;0rad)
  Radius = 1.5
FEATURE [Part::Cylinder] Cylinder2138  label="Válec2138"
  Angle = 360
  AttacherType = Attacher::AttachEngine3D
  Height = 100
  Placement = pos=(-16,-34,-90) rot=(0,0,1;0rad)
  Radius = 4
FEATURE [Part::Cylinder] Cylinder2139  label="Válec2139"
  Angle = 360
  AttacherType = Attacher::AttachEngine3D
  Height = 100
  Placement = pos=(34,-16,-90) rot=(0,0,1;0rad)
  Radius = 4
FEATURE [Part::Cylinder] Cylinder2140  label="Válec2140"
  Angle = 360
  AttacherType = Attacher::AttachEngine3D
  Height = 40
  Placement = pos=(1,-12,-18) rot=(0,0,1;0rad)
  Radius = 4
FEATURE [Part::Cylinder] Cylinder2141  label="Válec2141"
  Angle = 360
  AttacherType = Attacher::AttachEngine3D
  Height = 100
  Placement = pos=(16,34,-90) rot=(0,0,1;0rad)
  Radius = 4
FEATURE [Part::Cylinder] Cylinder2142  label="Válec2142"
  Angle = 360
  AttacherType = Attacher::AttachEngine3D
  Height = 100
  Placement = pos=(34,16,-90) rot=(0,0,1;0rad)
  Radius = 4
FEATURE [Part::Cylinder] Cylinder2143  label="Válec2143"
  Angle = 360
  AttacherType = Attacher::AttachEngine3D
  Height = 100
  Placement = pos=(90,0,-18) rot=(0,0,1;0rad)
  Radius = 4
FEATURE [Part::Cylinder] Cylinder2144  label="Válec2144"
  Angle = 360
  AttacherType = Attacher::AttachEngine3D
  Height = 20
  Placement = pos=(76,24,-18) rot=(0,0,1;0rad)
  Radius = 4
FEATURE [Part::Cylinder] Cylinder2145  label="Válec2145"
  Angle = 360
  AttacherType = Attacher::AttachEngine3D
  Height = 16
  Placement = pos=(0,0,2) rot=(0,0,1;0rad)
  Radius = 59
FEATURE [Part::Cylinder] Cylinder2146  label="Válec2146"
  Angle = 360
  AttacherType = Attacher::AttachEngine3D
  Height = 40
  Placement = pos=(13,-27,-18) rot=(0,0,1;0rad)
  Radius = 4
FEATURE [Part::Cylinder] Cylinder2147  label="Válec2147"
  Angle = 360
  AttacherType = Attacher::AttachEngine3D
  Height = 16
  Placement = pos=(-0.5,0,19.85) rot=(0,0,1;0rad)
  Radius = 59
FEATURE [Part::Cylinder] Cylinder2148  label="Válec2148"
  Angle = 360
  AttacherType = Attacher::AttachEngine3D
  Height = 40
  Placement = pos=(1,12,-18) rot=(0,0,1;0rad)
  Radius = 4
FEATURE [Part::Cylinder] Cylinder2149  label="Válec2149"
  Angle = 360
  AttacherType = Attacher::AttachEngine3D
  Height = 40
  Placement = pos=(28,24,-18) rot=(0,0,1;0rad)
  Radius = 4
FEATURE [Part::Cylinder] Cylinder2150  label="Válec2150"
  Angle = 360
  AttacherType = Attacher::AttachEngine3D
  Height = 20
  Placement = pos=(91,-27,-18) rot=(0,0,1;0rad)
  Radius = 4
FEATURE [Part::Cylinder] Cylinder2151  label="Válec2151"
  Angle = 360
  AttacherType = Attacher::AttachEngine3D
  Height = 100
  Placement = pos=(1,12,-60) rot=(0,0,1;0rad)
  Radius = 1.5
FEATURE [Part::Cylinder] Cylinder2152  label="Válec2152"
  Angle = 360
  AttacherType = Attacher::AttachEngine3D
  Height = 100
  Placement = pos=(-16,-34,-90) rot=(0,0,1;0rad)
  Radius = 4
FEATURE [Part::Cylinder] Cylinder2153  label="Válec2153"
  Angle = 360
  AttacherType = Attacher::AttachEngine3D
  Height = 100
  Placement = pos=(34,-16,-90) rot=(0,0,1;0rad)
  Radius = 4
FEATURE [Part::Cylinder] Cylinder2154  label="Válec2154"
  Angle = 360
  AttacherType = Attacher::AttachEngine3D
  Height = 100
  Placement = pos=(-16,34,-90) rot=(0,0,1;0rad)
  Radius = 4
FEATURE [Part::Cylinder] Cylinder2155  label="Válec2155"
  Angle = 360
  AttacherType = Attacher::AttachEngine3D
  Height = 100
  Placement = pos=(16,34,-60) rot=(0,0,1;0rad)
  Radius = 1.5
FEATURE [Part::Box] Box567  label="Krychle567"
  AttacherType = Attacher::AttachEngine3D
  Height = 100
  Length = 200
  Placement = pos=(-60,-130,-90) rot=(0,0,1;0rad)
  Width = 100
FEATURE [Part::Cylinder] Cylinder2156  label="Válec2156"
  Angle = 360
  AttacherType = Attacher::AttachEngine3D
  Height = 100
  Placement = pos=(16,-34,-90) rot=(0,0,1;0rad)
  Radius = 4
FEATURE [Part::Cylinder] Cylinder2157  label="Válec2157"
  Angle = 360
  AttacherType = Attacher::AttachEngine3D
  Height = 100
  Placement = pos=(-34,16,-90) rot=(0,0,1;0rad)
  Radius = 4
FEATURE [Part::Cylinder] Cylinder2158  label="Válec2158"
  Angle = 360
  AttacherType = Attacher::AttachEngine3D
  Height = 100
  Placement = pos=(-34,-16,-60) rot=(0,0,1;0rad)
  Radius = 1.5
FEATURE [Part::Cylinder] Cylinder2159  label="Válec2159"
  Angle = 360
  AttacherType = Attacher::AttachEngine3D
  Height = 100
  Placement = pos=(1,-12,-60) rot=(0,0,1;0rad)
  Radius = 1.5
FEATURE [Part::Cylinder] Cylinder2160  label="Válec2160"
  Angle = 360
  AttacherType = Attacher::AttachEngine3D
  Height = 100
  Placement = pos=(34,16,-90) rot=(0,0,1;0rad)
  Radius = 4
FEATURE [Part::Cylinder] Cylinder2161  label="Válec2161"
  Angle = 360
  AttacherType = Attacher::AttachEngine3D
  Height = 100
  Placement = pos=(-16,34,-60) rot=(0,0,1;0rad)
  Radius = 1.5
FEATURE [Part::Cylinder] Cylinder2162  label="Válec2162"
  Angle = 360
  AttacherType = Attacher::AttachEngine3D
  Height = 100
  Placement = pos=(16,34,-90) rot=(0,0,1;0rad)
  Radius = 4
FEATURE [Part::Cylinder] Cylinder2163  label="Válec2163"
  Angle = 360
  AttacherType = Attacher::AttachEngine3D
  Height = 100
  Placement = pos=(28,24,-60) rot=(0,0,1;0rad)
  Radius = 1.5
FEATURE [Part::Cylinder] Cylinder2164  label="Válec2164"
  Angle = 360
  AttacherType = Attacher::AttachEngine3D
  Height = 32
  Placement = pos=(26,41,-42) rot=(0,0,1;0rad)
  Radius = 1.5
FEATURE [Part::Cylinder] Cylinder2165  label="Válec2165"
  Angle = 360
  AttacherType = Attacher::AttachEngine3D
  Height = 32
  Placement = pos=(78,41,-42) rot=(0,0,1;0rad)
  Radius = 1.5
FEATURE [Part::Cylinder] Cylinder2166  label="Válec2166"
  Angle = 360
  AttacherType = Attacher::AttachEngine3D
  Height = 100
  Placement = pos=(-34,-16,-90) rot=(0,0,1;0rad)
  Radius = 4
FEATURE [Part::Cylinder] Cylinder2167  label="Válec2167"
  Angle = 360
  AttacherType = Attacher::AttachEngine3D
  Height = 20
  Placement = pos=(103,-12,-20) rot=(0,0,1;0rad)
  Radius = 4
FEATURE [Part::Cylinder] Cylinder2168  label="Válec2168"
  Angle = 360
  AttacherType = Attacher::AttachEngine3D
  Height = 100
  Placement = pos=(-16,-34,-60) rot=(0,0,1;0rad)
  Radius = 1.5
FEATURE [Part::Cylinder] Cylinder2169  label="Válec2169"
  Angle = 360
  AttacherType = Attacher::AttachEngine3D
  Height = 100
  Placement = pos=(10,-36,-60) rot=(0,0,1;0rad)
  Radius = 1.5
FEATURE [Part::Box] Box568  label="Krychle568"
  AttacherType = Attacher::AttachEngine3D
  Height = 100
  Length = 200
  Placement = pos=(-60,44,-90) rot=(0,0,1;0rad)
  Width = 100
FEATURE [Part::Cylinder] Cylinder2170  label="Válec2170"
  Angle = 360
  AttacherType = Attacher::AttachEngine3D
  Height = 100
  Placement = pos=(34,-16,-60) rot=(0,0,1;0rad)
  Radius = 1.5
FEATURE [Part::Cylinder] Cylinder2171  label="Válec2171"
  Angle = 360
  AttacherType = Attacher::AttachEngine3D
  Height = 100
  Placement = pos=(91,-27,-60) rot=(0,0,1;0rad)
  Radius = 1.5
FEATURE [Part::Cylinder] Cylinder2172  label="Válec2172"
  Angle = 360
  AttacherType = Attacher::AttachEngine3D
  Height = 100
  Placement = pos=(103,-12,-60) rot=(0,0,1;0rad)
  Radius = 1.5
FEATURE [Part::Cylinder] Cylinder2173  label="Válec2173"
  Angle = 360
  AttacherType = Attacher::AttachEngine3D
  Height = 100
  Placement = pos=(-34,-16,-90) rot=(0,0,1;0rad)
  Radius = 4
FEATURE [Part::Cylinder] Cylinder2174  label="Válec2174"
  Angle = 360
  AttacherType = Attacher::AttachEngine3D
  Height = 32
  Placement = pos=(78,41,-46) rot=(0,0,1;0rad)
  Radius = 1.5
FEATURE [Part::Cylinder] Cylinder2175  label="Válec2175"
  Angle = 360
  AttacherType = Attacher::AttachEngine3D
  Height = 100
  Placement = pos=(76,24,-60) rot=(0,0,1;0rad)
  Radius = 1.5
FEATURE [Part::Cylinder] Cylinder2176  label="Válec2176"
  Angle = 360
  AttacherType = Attacher::AttachEngine3D
  Height = 4
  Placement = pos=(52,0,-26) rot=(0,0,1;0rad)
  Radius = 59
FEATURE [Part::Cylinder] Cylinder2177  label="Válec2177"
  Angle = 360
  AttacherType = Attacher::AttachEngine3D
  Height = 100
  Placement = pos=(34,16,-60) rot=(0,0,1;0rad)
  Radius = 1.5
FEATURE [Part::Cylinder] Cylinder2178  label="Válec2178"
  Angle = 360
  AttacherType = Attacher::AttachEngine3D
  Height = 100
  Placement = pos=(-34,16,-60) rot=(0,0,1;0rad)
  Radius = 1.5
FEATURE [Part::Cylinder] Cylinder2179  label="Válec2179"
  Angle = 360
  AttacherType = Attacher::AttachEngine3D
  Height = 100
  Placement = pos=(103,12,-60) rot=(0,0,1;0rad)
  Radius = 1.5
FEATURE [Part::Cylinder] Cylinder2180  label="Válec2180"
  Angle = 360
  AttacherType = Attacher::AttachEngine3D
  Height = 100
  Placement = pos=(-16,34,-90) rot=(0,0,1;0rad)
  Radius = 4
FEATURE [Part::Cylinder] Cylinder2181  label="Válec2181"
  Angle = 360
  AttacherType = Attacher::AttachEngine3D
  Height = 100
  Placement = pos=(90,0,-60) rot=(0,0,1;0rad)
  Radius = 1.5
FEATURE [Part::Cylinder] Cylinder2182  label="Válec2182"
  Angle = 360
  AttacherType = Attacher::AttachEngine3D
  Height = 160
  Placement = pos=(-18,0,-60) rot=(0,0,1;0rad)
  Radius = 17
FEATURE [Part::Cylinder] Cylinder2183  label="Válec2183"
  Angle = 360
  AttacherType = Attacher::AttachEngine3D
  Height = 100
  Placement = pos=(13,-27,-60) rot=(0,0,1;0rad)
  Radius = 1.5
FEATURE [Part::Cylinder] Cylinder2184  label="Válec2184"
  Angle = 360
  AttacherType = Attacher::AttachEngine3D
  Height = 160
  Placement = pos=(-18,0,-60) rot=(0,0,1;0rad)
  Radius = 17
FEATURE [Part::Cylinder] Cylinder2185  label="Válec2185"
  Angle = 360
  AttacherType = Attacher::AttachEngine3D
  Height = 100
  Placement = pos=(14,0,-18) rot=(0,0,1;0rad)
  Radius = 4
FEATURE [Part::Box] Box569  label="Krychle569"
  AttacherType = Attacher::AttachEngine3D
  Height = 2
  Length = 6
  Placement = pos=(23,38,-22) rot=(0,0,1;0rad)
  Width = 6
FEATURE [Part::Cylinder] Cylinder2186  label="Válec2186"
  Angle = 360
  AttacherType = Attacher::AttachEngine3D
  Height = 100
  Placement = pos=(-34,16,-90) rot=(0,0,1;0rad)
  Radius = 4
FEATURE [Part::Cylinder] Cylinder2187  label="Válec2187"
  Angle = 360
  AttacherType = Attacher::AttachEngine3D
  Height = 100
  Placement = pos=(14,0,-60) rot=(0,0,1;0rad)
  Radius = 1.5
FEATURE [Part::Cylinder] Cylinder2188  label="Válec2188"
  Angle = 360
  AttacherType = Attacher::AttachEngine3D
  Height = 100
  Placement = pos=(34,16,-90) rot=(0,0,1;0rad)
  Radius = 4
FEATURE [Part::Cylinder] Cylinder2189  label="Válec2189"
  Angle = 360
  AttacherType = Attacher::AttachEngine3D
  Height = 100
  Placement = pos=(1,-12,-60) rot=(0,0,1;0rad)
  Radius = 1.5
FEATURE [Part::Cylinder] Cylinder2190  label="Válec2190"
  Angle = 360
  AttacherType = Attacher::AttachEngine3D
  Height = 100
  Placement = pos=(103,-12,-60) rot=(0,0,1;0rad)
  Radius = 1.5
FEATURE [Part::Cylinder] Cylinder2191  label="Válec2191"
  Angle = 360
  AttacherType = Attacher::AttachEngine3D
  Height = 100
  Placement = pos=(16,34,-90) rot=(0,0,1;0rad)
  Radius = 4
FEATURE [Part::Cylinder] Cylinder2192  label="Válec2192"
  Angle = 360
  AttacherType = Attacher::AttachEngine3D
  Height = 100
  Placement = pos=(90,0,-60) rot=(0,0,1;0rad)
  Radius = 1.5
FEATURE [Part::Cylinder] Cylinder2193  label="Válec2193"
  Angle = 360
  AttacherType = Attacher::AttachEngine3D
  Height = 100
  Placement = pos=(34,-16,-60) rot=(0,0,1;0rad)
  Radius = 1.5
FEATURE [Part::Cylinder] Cylinder2194  label="Válec2194"
  Angle = 360
  AttacherType = Attacher::AttachEngine3D
  Height = 100
  Placement = pos=(-34,-16,-60) rot=(0,0,1;0rad)
  Radius = 1.5
FEATURE [Part::Cylinder] Cylinder2195  label="Válec2195"
  Angle = 360
  AttacherType = Attacher::AttachEngine3D
  Height = 100
  Placement = pos=(34,16,-60) rot=(0,0,1;0rad)
  Radius = 1.5
FEATURE [Part::Cylinder] Cylinder2196  label="Válec2196"
  Angle = 360
  AttacherType = Attacher::AttachEngine3D
  Height = 160
  Placement = pos=(-18,0,-60) rot=(0,0,1;0rad)
  Radius = 17
FEATURE [Part::Cylinder] Cylinder2197  label="Válec2197"
  Angle = 360
  AttacherType = Attacher::AttachEngine3D
  Height = 100
  Placement = pos=(90,0,-18) rot=(0,0,1;0rad)
  Radius = 4
FEATURE [Part::Box] Box570  label="Krychle570"
  AttacherType = Attacher::AttachEngine3D
  Height = 120
  Length = 200
  Placement = pos=(-60,-134,-90) rot=(0,0,1;0rad)
  Width = 100
FEATURE [Part::Cylinder] Cylinder2198  label="Válec2198"
  Angle = 360
  AttacherType = Attacher::AttachEngine3D
  Height = 100
  Placement = pos=(-16,34,-60) rot=(0,0,1;0rad)
  Radius = 1.5
FEATURE [Part::Cylinder] Cylinder2199  label="Válec2199"
  Angle = 360
  AttacherType = Attacher::AttachEngine3D
  Height = 20
  Placement = pos=(103,12,-20) rot=(0,0,1;0rad)
  Radius = 4
FEATURE [Part::Cylinder] Cylinder2200  label="Válec2200"
  Angle = 360
  AttacherType = Attacher::AttachEngine3D
  Height = 100
  Placement = pos=(10,-36,-60) rot=(0,0,1;0rad)
  Radius = 1.5
FEATURE [Part::Box] Box571  label="Krychle571"
  AttacherType = Attacher::AttachEngine3D
  Height = 120
  Length = 200
  Placement = pos=(-60,44,-90) rot=(0,0,1;0rad)
  Width = 100
FEATURE [Part::Cylinder] Cylinder2201  label="Válec2201"
  Angle = 360
  AttacherType = Attacher::AttachEngine3D
  Height = 100
  Placement = pos=(-34,-16,-90) rot=(0,0,1;0rad)
  Radius = 4
FEATURE [Part::Cylinder] Cylinder2202  label="Válec2202"
  Angle = 360
  AttacherType = Attacher::AttachEngine3D
  Height = 100
  Placement = pos=(-34,16,-60) rot=(0,0,1;0rad)
  Radius = 1.5
FEATURE [Part::Cylinder] Cylinder2203  label="Válec2203"
  Angle = 360
  AttacherType = Attacher::AttachEngine3D
  Height = 40
  Placement = pos=(1,-12,-18) rot=(0,0,1;0rad)
  Radius = 4
FEATURE [Part::Cylinder] Cylinder2204  label="Válec2204"
  Angle = 360
  AttacherType = Attacher::AttachEngine3D
  Height = 100
  Placement = pos=(28,24,-60) rot=(0,0,1;0rad)
  Radius = 1.5
FEATURE [Part::Cylinder] Cylinder2205  label="Válec2205"
  Angle = 360
  AttacherType = Attacher::AttachEngine3D
  Height = 20
  Placement = pos=(103,-12,-20) rot=(0,0,1;0rad)
  Radius = 4
FEATURE [Part::Cylinder] Cylinder2206  label="Válec2206"
  Angle = 360
  AttacherType = Attacher::AttachEngine3D
  Height = 32
  Placement = pos=(76,24,-18) rot=(0,0,1;0rad)
  Radius = 4
FEATURE [Part::Cylinder] Cylinder2207  label="Válec2207"
  Angle = 360
  AttacherType = Attacher::AttachEngine3D
  Height = 100
  Placement = pos=(103,12,-60) rot=(0,0,1;0rad)
  Radius = 1.5
FEATURE [Part::Cylinder] Cylinder2208  label="Válec2208"
  Angle = 360
  AttacherType = Attacher::AttachEngine3D
  Height = 100
  Placement = pos=(10,-36,-90) rot=(0,0,1;0rad)
  Radius = 4
FEATURE [Part::Cylinder] Cylinder2209  label="Válec2209"
  Angle = 360
  AttacherType = Attacher::AttachEngine3D
  Height = 100
  Placement = pos=(76,24,-60) rot=(0,0,1;0rad)
  Radius = 1.5
FEATURE [Part::Cylinder] Cylinder2210  label="Válec2210"
  Angle = 360
  AttacherType = Attacher::AttachEngine3D
  Height = 100
  Placement = pos=(91,-27,-60) rot=(0,0,1;0rad)
  Radius = 1.5
FEATURE [Part::Cylinder] Cylinder2211  label="Válec2211"
  Angle = 360
  AttacherType = Attacher::AttachEngine3D
  Height = 40
  Placement = pos=(13,-27,-18) rot=(0,0,1;0rad)
  Radius = 4
FEATURE [Part::Cylinder] Cylinder2212  label="Válec2212"
  Angle = 360
  AttacherType = Attacher::AttachEngine3D
  Height = 20
  Placement = pos=(91,-27,-18) rot=(0,0,1;0rad)
  Radius = 4
FEATURE [Part::Cylinder] Cylinder2213  label="Válec2213"
  Angle = 360
  AttacherType = Attacher::AttachEngine3D
  Height = 40
  Placement = pos=(28,24,-18) rot=(0,0,1;0rad)
  Radius = 4
FEATURE [Part::Cylinder] Cylinder2214  label="Válec2214"
  Angle = 360
  AttacherType = Attacher::AttachEngine3D
  Height = 100
  Placement = pos=(14,0,-60) rot=(0,0,1;0rad)
  Radius = 1.5
FEATURE [Part::Cylinder] Cylinder2215  label="Válec2215"
  Angle = 360
  AttacherType = Attacher::AttachEngine3D
  Height = 100
  Placement = pos=(16,34,-90) rot=(0,0,1;0rad)
  Radius = 4
FEATURE [Part::Cylinder] Cylinder2216  label="Válec2216"
  Angle = 360
  AttacherType = Attacher::AttachEngine3D
  Height = 100
  Placement = pos=(-16,-34,-90) rot=(0,0,1;0rad)
  Radius = 4
FEATURE [Part::Cylinder] Cylinder2217  label="Válec2217"
  Angle = 360
  AttacherType = Attacher::AttachEngine3D
  Height = 40
  Placement = pos=(1,12,-18) rot=(0,0,1;0rad)
  Radius = 4
FEATURE [Part::Cylinder] Cylinder2218  label="Válec2218"
  Angle = 360
  AttacherType = Attacher::AttachEngine3D
  Height = 100
  Placement = pos=(-16,-34,-60) rot=(0,0,1;0rad)
  Radius = 1.5
FEATURE [Part::Cylinder] Cylinder2219  label="Válec2219"
  Angle = 360
  AttacherType = Attacher::AttachEngine3D
  Height = 100
  Placement = pos=(-16,34,-90) rot=(0,0,1;0rad)
  Radius = 4
FEATURE [Part::Cylinder] Cylinder2220  label="Válec2220"
  Angle = 360
  AttacherType = Attacher::AttachEngine3D
  Height = 100
  Placement = pos=(13,-27,-60) rot=(0,0,1;0rad)
  Radius = 1.5
FEATURE [Part::Cylinder] Cylinder2221  label="Válec2221"
  Angle = 360
  AttacherType = Attacher::AttachEngine3D
  Height = 100
  Placement = pos=(16,34,-60) rot=(0,0,1;0rad)
  Radius = 1.5
FEATURE [Part::Compound] Compound1013  label="srouby_troj_silne018"
  Links = -> [Cylinder2143,Cylinder2134]
FEATURE [Part::Compound] Compound1014  label="sbouby_baze020"
  Links = -> [Cylinder2178,Cylinder2158,Cylinder2170,Cylinder2177,Cylinder2155,Cylinder2169,Cylinder2168,Cylinder2161]
FEATURE [Part::Compound] Compound1015  label="srouby_monoblok_silne021"
  Links = -> [Cylinder2128,Cylinder2121,Cylinder2111,Cylinder2114,Cylinder2124,Cylinder2116,Cylinder2113,Cylinder2122]
FEATURE [Part::Compound] Compound1016  label="srouby_troj_silne019"
  Links = -> [Cylinder2110,Cylinder2120]
FEATURE [Part::Compound] Compound1017  label="sbouby_baze021"
  Links = -> [Cylinder2127,Cylinder2112,Cylinder2136,Cylinder2137,Cylinder2135,Cylinder2117,Cylinder2123,Cylinder2118]
FEATURE [Part::Compound] Compound1018  label="sbouby_baze_silne028"
  Links = -> [Cylinder2173,Cylinder2180,Cylinder2138,Cylinder2139,Cylinder2141,Cylinder2131,Cylinder2126,Cylinder2142]
FEATURE [Part::Compound] Compound1020  label="srouby_troj_silne020"
  Links = -> [Cylinder2197,Cylinder2185]
FEATURE [Part::Compound] Compound1021  label="sbouby_baze_silne030"
  Links = -> [Cylinder2166,Cylinder2154,Cylinder2152,Cylinder2153,Cylinder2162,Cylinder2156,Cylinder2157,Cylinder2160]
  Placement = pos=(-0.5,0,0) rot=(0,0,1;0rad)
FEATURE [Part::Compound] Compound1022  label="srouby_monoblok_silne022"
  Links = -> [Cylinder2167,Cylinder2133,Cylinder2144,Cylinder2150,Cylinder2146,Cylinder2149,Cylinder2140,Cylinder2148]
FEATURE [Part::Compound] Compound1023  label="srouby_monoblok018"
  Links = -> [Cylinder2172,Cylinder2179,Cylinder2175,Cylinder2171,Cylinder2183,Cylinder2163,Cylinder2159,Cylinder2132]
FEATURE [Part::Compound] Compound1026  label="srouby_monoblok019"
  Links = -> [Cylinder2190,Cylinder2207,Cylinder2209,Cylinder2210,Cylinder2220,Cylinder2204,Cylinder2189,Cylinder2151]
FEATURE [Part::Compound] Compound1027
  Links = -> [Cylinder2164,Cylinder2165]
FEATURE [Part::Compound] Compound1028  label="sbouby_baze022"
  Links = -> [Cylinder2202,Cylinder2194,Cylinder2193,Cylinder2195,Cylinder2221,Cylinder2200,Cylinder2218,Cylinder2198]
FEATURE [Part::Compound] Compound1029  label="srouby_troj016"
  Links = -> [Cylinder2181,Cylinder2214]
FEATURE [Part::Compound] Compound1030  label="srouby_troj017"
  Links = -> [Cylinder2192,Cylinder2187]
FEATURE [Part::Compound] Compound1031  label="srouby_monoblok_silne023"
  Links = -> [Cylinder2205,Cylinder2199,Cylinder2206,Cylinder2212,Cylinder2211,Cylinder2213,Cylinder2203,Cylinder2217]
FEATURE [Part::Cut] Cut692
  Base = -> Cylinder2145
  Tool = -> Compound1022
FEATURE [Part::Cut] Cut697
  Base = -> Cylinder2129
  Tool = -> Compound1015
FEATURE [Part::Cut] Cut702
  Base = -> Cylinder2176
  Tool = -> Compound1023
FEATURE [Part::Cut] Cut709
  Base = -> Extrude018
  Tool = -> Compound1026
FEATURE [Part::Cut] Cut690
  Base = -> Cut709
  Tool = -> Compound1031
FEATURE [Part::Cut] Cut710
  Base = -> Cut692
  Tool = -> Compound1018
FEATURE [Part::Cut] Cut707
  Base = -> Cut710
  Tool = -> Compound1014
FEATURE [Part::Chamfer] Chamfer074
  Base = -> Cut707
  Edges = 1 edges r=4: [Edge3]
FEATURE [Part::Cut] Cut705
  Base = -> Chamfer074
  Placement = pos=(-0.5,0,14) rot=(0,0,1;0rad)
  Tool = -> Compound1013
FEATURE [Part::Cut] Cut691
  Base = -> Cut705
  Tool = -> Cylinder2184
FEATURE [Part::Fillet] Fillet033
  Base = -> Cut691
  Edges = 1 edges r=4: [Edge11]
  Placement = pos=(0,0,-0.15) rot=(0,0,1;0rad)
FEATURE [Part::Common] Common007
  Base = -> Fillet033
  Tool = -> Cylinder2147
FEATURE [Part::Cut] Cut711
  Base = -> Cut702
  Tool = -> Compound1021
FEATURE [Part::Cut] Cut701
  Base = -> Cut711
  Tool = -> Box567
FEATURE [Part::Cut] Cut704
  Base = -> Cut701
  Tool = -> Box568
FEATURE [Part::Cut] Cut706
  Base = -> Cut704
  Tool = -> Compound1027
FEATURE [Part::Cut] Cut708
  Base = -> Cut706
  Tool = -> Compound1029
FEATURE [Part::Cut] Cut689
  Base = -> Cut708
  Tool = -> Cylinder2182
FEATURE [Part::Fillet] Fillet031
  Base = -> Cut689
  Edges = 2 edges r=8: [Edge55,Edge57]
FEATURE [Sketcher::SketchObject] Sketch020
  FullyConstrained = false
  sketch-geometry (1):
    g0: Circle CenterX=-186.411 CenterY=73.9277 CenterZ=0 NormalX=0 NormalY=0 NormalZ=1 AngleXU=0 Radius=59
FEATURE [Part::Extrusion] Extrude017
  Base = -> Sketch020
  Dir = (40,0,32)
  DirMode = 0
  FaceMakerClass = Part::FaceMakerBullseye
  LengthFwd = 67
  LengthRev = 0
  Placement = pos=(-134.5,74,-22) rot=(0,0,1;3.14159rad)
  Solid = true
  Symmetric = false
FEATURE [Part::Box] Box572  label="Krychle572"
  AttacherType = Attacher::AttachEngine3D
  Height = 2
  Length = 6
  Placement = pos=(75,38,-22) rot=(0,0,1;0rad)
  Width = 6
FEATURE [Part::Compound] Compound1024
  Links = -> [Box572,Box569]
FEATURE [Part::Cylinder] Cylinder2222  label="Válec2222"
  Angle = 360
  AttacherType = Attacher::AttachEngine3D
  Height = 100
  Placement = pos=(10,-36,-90) rot=(0,0,1;0rad)
  Radius = 4
FEATURE [Part::Cylinder] Cylinder2223  label="Válec2223"
  Angle = 360
  AttacherType = Attacher::AttachEngine3D
  Height = 100
  Placement = pos=(34,16,-90) rot=(0,0,1;0rad)
  Radius = 4
FEATURE [Part::Compound] Compound1019  label="sbouby_baze_silne029"
  Links = -> [Cylinder2119,Cylinder2130,Cylinder2115,Cylinder2109,Cylinder2215,Cylinder2222,Cylinder2108,Cylinder2223]
FEATURE [Part::Cut] Cut694
  Base = -> Cut697
  Tool = -> Compound1019
FEATURE [Part::Cut] Cut693
  Base = -> Cut694
  Tool = -> Compound1017
FEATURE [Part::Chamfer] Chamfer073
  Base = -> Cut693
  Edges = 1 edges r=4: [Edge3]
FEATURE [Part::Cut] Cut712
  Base = -> Chamfer073
  Placement = pos=(-0.5,0,14) rot=(0,0,1;0rad)
  Tool = -> Compound1016
FEATURE [Part::Cut] Cut686
  Base = -> Cut712
  Tool = -> Cylinder2125
FEATURE [Part::Fillet] Fillet030
  Base = -> Cut686
  Edges = 1 edges r=4: [Edge11]
FEATURE [Part::Common] Common006
  Base = -> Extrude017
  Tool = -> Fillet030
FEATURE [Part::Cylinder] Cylinder2224  label="Válec2224"
  Angle = 360
  AttacherType = Attacher::AttachEngine3D
  Height = 100
  Placement = pos=(34,-16,-90) rot=(0,0,1;0rad)
  Radius = 4
FEATURE [Part::Compound] Compound1025  label="sbouby_baze_silne031"
  Links = -> [Cylinder2201,Cylinder2219,Cylinder2216,Cylinder2224,Cylinder2191,Cylinder2208,Cylinder2186,Cylinder2188]
  Placement = pos=(-0.5,0,12) rot=(0,0,1;0rad)
FEATURE [Part::Cut] Cut685
  Base = -> Cut690
  Tool = -> Compound1025
FEATURE [Part::Cut] Cut700
  Base = -> Cut685
  Tool = -> Compound1028
FEATURE [Part::Cut] Cut688
  Base = -> Cut700
  Tool = -> Box570
FEATURE [Part::Cut] Cut698
  Base = -> Cut688
  Tool = -> Box571
FEATURE [Part::Cut] Cut687
  Base = -> Cut698
  Tool = -> Compound1024
FEATURE [Part::Cylinder] Cylinder2225  label="Válec2225"
  Angle = 360
  AttacherType = Attacher::AttachEngine3D
  Height = 32
  Placement = pos=(26,41,-46) rot=(0,0,1;0rad)
  Radius = 1.5
FEATURE [Part::Compound] Compound1032
  Links = -> [Cylinder2225,Cylinder2174]
FEATURE [Part::Cut] Cut695
  Base = -> Cut687
  Tool = -> Compound1032
FEATURE [Part::Cut] Cut699
  Base = -> Cut695
  Tool = -> Compound1030
FEATURE [Part::Cut] Cut703
  Base = -> Cut699
  Tool = -> Compound1020
FEATURE [Part::Chamfer] Chamfer076
  Base = -> Cut703
  Edges = 1 edges r=4: [Edge44]
FEATURE [Part::Chamfer] Chamfer075
  Base = -> Chamfer076
  Edges = 2 edges r=3: [Edge4,Edge6]
FEATURE [Part::Cut] Cut696
  Base = -> Chamfer075
  Tool = -> Cylinder2196
FEATURE [Part::Fillet] Fillet032
  Base = -> Cut696
  Edges = 2 edges r=3: [Edge3,Edge34]
FEATURE [Part::Box] Box  label="Krychle"
  AttacherType = Attacher::AttachEngine3D
  Height = 100
  Length = 40
  Placement = pos=(-50,-48,-22) rot=(0,0,1;0rad)
  Width = 100
FEATURE [Part::Torus] Torus  label="Anuloid"
  Angle1 = -180
  Angle2 = 180
  Angle3 = 360
  AttacherType = Attacher::AttachEngine3D
  Placement = pos=(12,-33,-4) rot=(0,0,1;0rad)
  Radius1 = 40
  Radius2 = 4
FEATURE [Part::Cut] Cut713
  Base = -> Torus
  Tool = -> Box
FEATURE [Part::Cut] Cut684
  Base = -> Fillet032
  Tool = -> Cut713
FEATURE [Part::Fillet] Fillet034
  Base = -> Cut684
  Edges = 1 edges r=3: [Edge138]
FEATURE [Part::Fillet] Fillet009
  Base = -> Fillet034
  Edges = 1 edges r=3: [Edge48]
FEATURE [Part::Compound] Compound1033
  Links = -> [Common006,Common007,Fillet031,Fillet009]
FEATURE [Part::Mirroring] mirror  label="Base_deep-highneck-holed_v3"
  Base = (0,0,0)
  Normal = (1e-16,-1,0)
  Source = -> Compound1033
FEATURE [Part::Cylinder] Cylinder2226  label="Válec2226"
  Angle = 360
  AttacherType = Attacher::AttachEngine3D
  Height = 32
  Placement = pos=(78,41,-46) rot=(0,0,1;0rad)
  Radius = 1.5
FEATURE [Part::Cylinder] Cylinder2227  label="Válec2227"
  Angle = 360
  AttacherType = Attacher::AttachEngine3D
  Height = 20
  Placement = pos=(103,-12,-20) rot=(0,0,1;0rad)
  Radius = 4
FEATURE [Part::Cylinder] Cylinder2228  label="Válec2228"
  Angle = 360
  AttacherType = Attacher::AttachEngine3D
  Height = 20
  Placement = pos=(103,12,-20) rot=(0,0,1;0rad)
  Radius = 4
FEATURE [Part::Cylinder] Cylinder2229  label="Válec2229"
  Angle = 360
  AttacherType = Attacher::AttachEngine3D
  Height = 20
  Placement = pos=(76,24,-18) rot=(0,0,1;0rad)
  Radius = 4
FEATURE [Part::Cylinder] Cylinder2230  label="Válec2230"
  Angle = 360
  AttacherType = Attacher::AttachEngine3D
  Height = 100
  Placement = pos=(10,-36,-60) rot=(0,0,1;0rad)
  Radius = 1.5
FEATURE [Part::Cylinder] Cylinder2231  label="Válec2231"
  Angle = 360
  AttacherType = Attacher::AttachEngine3D
  Height = 40
  Placement = pos=(28,24,-18) rot=(0,0,1;0rad)
  Radius = 4
FEATURE [Part::Cylinder] Cylinder2232  label="Válec2232"
  Angle = 360
  AttacherType = Attacher::AttachEngine3D
  Height = 16
  Placement = pos=(0,0,2) rot=(0,0,1;0rad)
  Radius = 59
FEATURE [Part::Cylinder] Cylinder2233  label="Válec2233"
  Angle = 360
  AttacherType = Attacher::AttachEngine3D
  Height = 20
  Placement = pos=(91,-27,-18) rot=(0,0,1;0rad)
  Radius = 4
FEATURE [Part::Cylinder] Cylinder2234  label="Válec2234"
  Angle = 360
  AttacherType = Attacher::AttachEngine3D
  Height = 100
  Placement = pos=(-16,-34,-90) rot=(0,0,1;0rad)
  Radius = 4
FEATURE [Part::Cylinder] Cylinder2235  label="Válec2235"
  Angle = 360
  AttacherType = Attacher::AttachEngine3D
  Height = 100
  Placement = pos=(10,-36,-90) rot=(0,0,1;0rad)
  Radius = 4
FEATURE [Part::Cylinder] Cylinder2236  label="Válec2236"
  Angle = 360
  AttacherType = Attacher::AttachEngine3D
  Height = 32
  Placement = pos=(26,41,-42) rot=(0,0,1;0rad)
  Radius = 1.5
FEATURE [Part::Cylinder] Cylinder2237  label="Válec2237"
  Angle = 360
  AttacherType = Attacher::AttachEngine3D
  Height = 160
  Placement = pos=(-18,0,-60) rot=(0,0,1;0rad)
  Radius = 17
FEATURE [Part::Cylinder] Cylinder2238  label="Válec2238"
  Angle = 360
  AttacherType = Attacher::AttachEngine3D
  Height = 16
  Placement = pos=(0,0,10) rot=(0,0,1;0rad)
  Radius = 59
FEATURE [Part::Cylinder] Cylinder2239  label="Válec2239"
  Angle = 360
  AttacherType = Attacher::AttachEngine3D
  Height = 100
  Placement = pos=(-34,16,-90) rot=(0,0,1;0rad)
  Radius = 4
FEATURE [Part::Cylinder] Cylinder2240  label="Válec2240"
  Angle = 360
  AttacherType = Attacher::AttachEngine3D
  Height = 100
  Placement = pos=(14,0,-18) rot=(0,0,1;0rad)
  Radius = 4
FEATURE [Part::Cylinder] Cylinder2241  label="Válec2241"
  Angle = 360
  AttacherType = Attacher::AttachEngine3D
  Height = 100
  Placement = pos=(90,0,-18) rot=(0,0,1;0rad)
  Radius = 4
FEATURE [Part::Cylinder] Cylinder2242  label="Válec2242"
  Angle = 360
  AttacherType = Attacher::AttachEngine3D
  Height = 100
  Placement = pos=(91,-27,-60) rot=(0,0,1;0rad)
  Radius = 1.5
FEATURE [Part::Cylinder] Cylinder2243  label="Válec2243"
  Angle = 360
  AttacherType = Attacher::AttachEngine3D
  Height = 100
  Placement = pos=(16,34,-60) rot=(0,0,1;0rad)
  Radius = 1.5
FEATURE [Part::Cylinder] Cylinder2244  label="Válec2244"
  Angle = 360
  AttacherType = Attacher::AttachEngine3D
  Height = 100
  Placement = pos=(16,34,-90) rot=(0,0,1;0rad)
  Radius = 4
FEATURE [Part::Cylinder] Cylinder2245  label="Válec2245"
  Angle = 360
  AttacherType = Attacher::AttachEngine3D
  Height = 40
  Placement = pos=(1,-12,-18) rot=(0,0,1;0rad)
  Radius = 4
FEATURE [Part::Cylinder] Cylinder2246  label="Válec2246"
  Angle = 360
  AttacherType = Attacher::AttachEngine3D
  Height = 40
  Placement = pos=(1,12,-18) rot=(0,0,1;0rad)
  Radius = 4
FEATURE [Part::Cylinder] Cylinder2247  label="Válec2247"
  Angle = 360
  AttacherType = Attacher::AttachEngine3D
  Height = 40
  Placement = pos=(13,-27,-18) rot=(0,0,1;0rad)
  Radius = 4
FEATURE [Part::Cylinder] Cylinder2248  label="Válec2248"
  Angle = 360
  AttacherType = Attacher::AttachEngine3D
  Height = 100
  Placement = pos=(-16,34,-90) rot=(0,0,1;0rad)
  Radius = 4
FEATURE [Part::Cylinder] Cylinder2249  label="Válec2249"
  Angle = 360
  AttacherType = Attacher::AttachEngine3D
  Height = 100
  Placement = pos=(-34,16,-90) rot=(0,0,1;0rad)
  Radius = 4
FEATURE [Part::Box] Box573  label="Krychle573"
  AttacherType = Attacher::AttachEngine3D
  Height = 100
  Length = 200
  Placement = pos=(-60,44,-90) rot=(0,0,1;0rad)
  Width = 100
FEATURE [Part::Cylinder] Cylinder2250  label="Válec2250"
  Angle = 360
  AttacherType = Attacher::AttachEngine3D
  Height = 100
  Placement = pos=(34,16,-90) rot=(0,0,1;0rad)
  Radius = 4
FEATURE [Part::Cylinder] Cylinder2251  label="Válec2251"
  Angle = 360
  AttacherType = Attacher::AttachEngine3D
  Height = 100
  Placement = pos=(34,16,-90) rot=(0,0,1;0rad)
  Radius = 4
FEATURE [Part::Cylinder] Cylinder2252  label="Válec2252"
  Angle = 360
  AttacherType = Attacher::AttachEngine3D
  Height = 160
  Placement = pos=(-18,0,-60) rot=(0,0,1;0rad)
  Radius = 17
FEATURE [Part::Cylinder] Cylinder2253  label="Válec2253"
  Angle = 360
  AttacherType = Attacher::AttachEngine3D
  Height = 20
  Placement = pos=(103,12,-20) rot=(0,0,1;0rad)
  Radius = 4
FEATURE [Part::Cylinder] Cylinder2254  label="Válec2254"
  Angle = 360
  AttacherType = Attacher::AttachEngine3D
  Height = 100
  Placement = pos=(14,0,-60) rot=(0,0,1;0rad)
  Radius = 1.5
FEATURE [Part::Cylinder] Cylinder2255  label="Válec2255"
  Angle = 360
  AttacherType = Attacher::AttachEngine3D
  Height = 100
  Placement = pos=(-34,-16,-90) rot=(0,0,1;0rad)
  Radius = 4
FEATURE [Part::Cylinder] Cylinder2256  label="Válec2256"
  Angle = 360
  AttacherType = Attacher::AttachEngine3D
  Height = 100
  Placement = pos=(13,-27,-60) rot=(0,0,1;0rad)
  Radius = 1.5
FEATURE [Part::Cylinder] Cylinder2257  label="Válec2257"
  Angle = 360
  AttacherType = Attacher::AttachEngine3D
  Height = 40
  Placement = pos=(1,-12,-18) rot=(0,0,1;0rad)
  Radius = 4
FEATURE [Part::Cylinder] Cylinder2258  label="Válec2258"
  Angle = 360
  AttacherType = Attacher::AttachEngine3D
  Height = 100
  Placement = pos=(-16,-34,-60) rot=(0,0,1;0rad)
  Radius = 1.5
FEATURE [Part::Cylinder] Cylinder2259  label="Válec2259"
  Angle = 360
  AttacherType = Attacher::AttachEngine3D
  Height = 100
  Placement = pos=(34,-16,-60) rot=(0,0,1;0rad)
  Radius = 1.5
FEATURE [Part::Cylinder] Cylinder2260  label="Válec2260"
  Angle = 360
  AttacherType = Attacher::AttachEngine3D
  Height = 100
  Placement = pos=(16,-34,-90) rot=(0,0,1;0rad)
  Radius = 4
FEATURE [Part::Cylinder] Cylinder2261  label="Válec2261"
  Angle = 360
  AttacherType = Attacher::AttachEngine3D
  Height = 100
  Placement = pos=(34,16,-60) rot=(0,0,1;0rad)
  Radius = 1.5
FEATURE [Part::Cylinder] Cylinder2262  label="Válec2262"
  Angle = 360
  AttacherType = Attacher::AttachEngine3D
  Height = 100
  Placement = pos=(-34,-16,-60) rot=(0,0,1;0rad)
  Radius = 1.5
FEATURE [Part::Cylinder] Cylinder2263  label="Válec2263"
  Angle = 360
  AttacherType = Attacher::AttachEngine3D
  Height = 100
  Placement = pos=(1,-12,-60) rot=(0,0,1;0rad)
  Radius = 1.5
FEATURE [Part::Cylinder] Cylinder2264  label="Válec2264"
  Angle = 360
  AttacherType = Attacher::AttachEngine3D
  Height = 100
  Placement = pos=(-16,34,-60) rot=(0,0,1;0rad)
  Radius = 1.5
FEATURE [Part::Cylinder] Cylinder2265  label="Válec2265"
  Angle = 360
  AttacherType = Attacher::AttachEngine3D
  Height = 100
  Placement = pos=(103,-12,-60) rot=(0,0,1;0rad)
  Radius = 1.5
FEATURE [Part::Cylinder] Cylinder2266  label="Válec2266"
  Angle = 360
  AttacherType = Attacher::AttachEngine3D
  Height = 100
  Placement = pos=(103,12,-60) rot=(0,0,1;0rad)
  Radius = 1.5
FEATURE [Part::Cylinder] Cylinder2267  label="Válec2267"
  Angle = 360
  AttacherType = Attacher::AttachEngine3D
  Height = 100
  Placement = pos=(76,24,-60) rot=(0,0,1;0rad)
  Radius = 1.5
FEATURE [Part::Cylinder] Cylinder2268  label="Válec2268"
  Angle = 360
  AttacherType = Attacher::AttachEngine3D
  Height = 100
  Placement = pos=(34,-16,-90) rot=(0,0,1;0rad)
  Radius = 4
FEATURE [Part::Cylinder] Cylinder2269  label="Válec2269"
  Angle = 360
  AttacherType = Attacher::AttachEngine3D
  Height = 100
  Placement = pos=(-34,16,-60) rot=(0,0,1;0rad)
  Radius = 1.5
FEATURE [Part::Cylinder] Cylinder2270  label="Válec2270"
  Angle = 360
  AttacherType = Attacher::AttachEngine3D
  Height = 100
  Placement = pos=(16,34,-90) rot=(0,0,1;0rad)
  Radius = 4
FEATURE [Part::Cylinder] Cylinder2271  label="Válec2271"
  Angle = 360
  AttacherType = Attacher::AttachEngine3D
  Height = 20
  Placement = pos=(76,24,-18) rot=(0,0,1;0rad)
  Radius = 4
FEATURE [Part::Cylinder] Cylinder2272  label="Válec2272"
  Angle = 360
  AttacherType = Attacher::AttachEngine3D
  Height = 20
  Placement = pos=(91,-27,-18) rot=(0,0,1;0rad)
  Radius = 4
FEATURE [Part::Cylinder] Cylinder2273  label="Válec2273"
  Angle = 360
  AttacherType = Attacher::AttachEngine3D
  Height = 100
  Placement = pos=(-16,34,-90) rot=(0,0,1;0rad)
  Radius = 4
FEATURE [Part::Cylinder] Cylinder2274  label="Válec2274"
  Angle = 360
  AttacherType = Attacher::AttachEngine3D
  Height = 100
  Placement = pos=(28,24,-60) rot=(0,0,1;0rad)
  Radius = 1.5
FEATURE [Part::Cylinder] Cylinder2275  label="Válec2275"
  Angle = 360
  AttacherType = Attacher::AttachEngine3D
  Height = 100
  Placement = pos=(-34,-16,-90) rot=(0,0,1;0rad)
  Radius = 4
FEATURE [Part::Cylinder] Cylinder2276  label="Válec2276"
  Angle = 360
  AttacherType = Attacher::AttachEngine3D
  Height = 100
  Placement = pos=(34,-16,-90) rot=(0,0,1;0rad)
  Radius = 4
FEATURE [Part::Cylinder] Cylinder2277  label="Válec2277"
  Angle = 360
  AttacherType = Attacher::AttachEngine3D
  Height = 100
  Placement = pos=(-16,-34,-90) rot=(0,0,1;0rad)
  Radius = 4
FEATURE [Part::Cylinder] Cylinder2278  label="Válec2278"
  Angle = 360
  AttacherType = Attacher::AttachEngine3D
  Height = 100
  Placement = pos=(1,12,-60) rot=(0,0,1;0rad)
  Radius = 1.5
FEATURE [Part::Cylinder] Cylinder2279  label="Válec2279"
  Angle = 360
  AttacherType = Attacher::AttachEngine3D
  Height = 40
  Placement = pos=(1,12,-18) rot=(0,0,1;0rad)
  Radius = 4
FEATURE [Part::Cylinder] Cylinder2280  label="Válec2280"
  Angle = 360
  AttacherType = Attacher::AttachEngine3D
  Height = 100
  Placement = pos=(-16,-34,-90) rot=(0,0,1;0rad)
  Radius = 4
FEATURE [Part::Cylinder] Cylinder2281  label="Válec2281"
  Angle = 360
  AttacherType = Attacher::AttachEngine3D
  Height = 40
  Placement = pos=(13,-27,-18) rot=(0,0,1;0rad)
  Radius = 4
FEATURE [Part::Cylinder] Cylinder2282  label="Válec2282"
  Angle = 360
  AttacherType = Attacher::AttachEngine3D
  Height = 100
  Placement = pos=(-34,-16,-90) rot=(0,0,1;0rad)
  Radius = 4
FEATURE [Part::Cylinder] Cylinder2283  label="Válec2283"
  Angle = 360
  AttacherType = Attacher::AttachEngine3D
  Height = 20
  Placement = pos=(103,12,-20) rot=(0,0,1;0rad)
  Radius = 4
FEATURE [Part::Cylinder] Cylinder2284  label="Válec2284"
  Angle = 360
  AttacherType = Attacher::AttachEngine3D
  Height = 20
  Placement = pos=(76,24,-18) rot=(0,0,1;0rad)
  Radius = 4
FEATURE [Part::Cylinder] Cylinder2285  label="Válec2285"
  Angle = 360
  AttacherType = Attacher::AttachEngine3D
  Height = 40
  Placement = pos=(28,24,-18) rot=(0,0,1;0rad)
  Radius = 4
FEATURE [Part::Cylinder] Cylinder2286  label="Válec2286"
  Angle = 360
  AttacherType = Attacher::AttachEngine3D
  Height = 16
  Placement = pos=(0,0,2) rot=(0,0,1;0rad)
  Radius = 59
FEATURE [Part::Cylinder] Cylinder2287  label="Válec2287"
  Angle = 360
  AttacherType = Attacher::AttachEngine3D
  Height = 40
  Placement = pos=(1,12,-18) rot=(0,0,1;0rad)
  Radius = 4
FEATURE [Part::Cylinder] Cylinder2288  label="Válec2288"
  Angle = 360
  AttacherType = Attacher::AttachEngine3D
  Height = 40
  Placement = pos=(1,-12,-18) rot=(0,0,1;0rad)
  Radius = 4
FEATURE [Part::Cylinder] Cylinder2289  label="Válec2289"
  Angle = 360
  AttacherType = Attacher::AttachEngine3D
  Height = 100
  Placement = pos=(14,0,-18) rot=(0,0,1;0rad)
  Radius = 4
FEATURE [Part::Cylinder] Cylinder2290  label="Válec2290"
  Angle = 360
  AttacherType = Attacher::AttachEngine3D
  Height = 100
  Placement = pos=(-34,16,-90) rot=(0,0,1;0rad)
  Radius = 4
FEATURE [Part::Cylinder] Cylinder2291  label="Válec2291"
  Angle = 360
  AttacherType = Attacher::AttachEngine3D
  Height = 100
  Placement = pos=(16,34,-90) rot=(0,0,1;0rad)
  Radius = 4
FEATURE [Part::Cylinder] Cylinder2292  label="Válec2292"
  Angle = 360
  AttacherType = Attacher::AttachEngine3D
  Height = 100
  Placement = pos=(-16,34,-90) rot=(0,0,1;0rad)
  Radius = 4
FEATURE [Part::Cylinder] Cylinder2293  label="Válec2293"
  Angle = 360
  AttacherType = Attacher::AttachEngine3D
  Height = 100
  Placement = pos=(16,34,-90) rot=(0,0,1;0rad)
  Radius = 4
FEATURE [Part::Cylinder] Cylinder2294  label="Válec2294"
  Angle = 360
  AttacherType = Attacher::AttachEngine3D
  Height = 4
  Placement = pos=(52,0,-26) rot=(0,0,1;0rad)
  Radius = 59
FEATURE [Part::Cylinder] Cylinder2295  label="Válec2295"
  Angle = 360
  AttacherType = Attacher::AttachEngine3D
  Height = 100
  Placement = pos=(-16,34,-90) rot=(0,0,1;0rad)
  Radius = 4
FEATURE [Part::Cylinder] Cylinder2296  label="Válec2296"
  Angle = 360
  AttacherType = Attacher::AttachEngine3D
  Height = 20
  Placement = pos=(103,-12,-20) rot=(0,0,1;0rad)
  Radius = 4
FEATURE [Part::Box] Box574  label="Krychle574"
  AttacherType = Attacher::AttachEngine3D
  Height = 100
  Length = 200
  Placement = pos=(-60,-130,-90) rot=(0,0,1;0rad)
  Width = 100
FEATURE [Part::Cylinder] Cylinder2297  label="Válec2297"
  Angle = 360
  AttacherType = Attacher::AttachEngine3D
  Height = 100
  Placement = pos=(34,16,-90) rot=(0,0,1;0rad)
  Radius = 4
FEATURE [Part::Cylinder] Cylinder2298  label="Válec2298"
  Angle = 360
  AttacherType = Attacher::AttachEngine3D
  Height = 160
  Placement = pos=(-18,0,-60) rot=(0,0,1;0rad)
  Radius = 17
FEATURE [Part::Cylinder] Cylinder2299  label="Válec2299"
  Angle = 360
  AttacherType = Attacher::AttachEngine3D
  Height = 100
  Placement = pos=(-34,-16,-90) rot=(0,0,1;0rad)
  Radius = 4
FEATURE [Part::Cylinder] Cylinder2300  label="Válec2300"
  Angle = 360
  AttacherType = Attacher::AttachEngine3D
  Height = 100
  Placement = pos=(-34,-16,-60) rot=(0,0,1;0rad)
  Radius = 1.5
FEATURE [Part::Cylinder] Cylinder2301  label="Válec2301"
  Angle = 360
  AttacherType = Attacher::AttachEngine3D
  Height = 100
  Placement = pos=(-16,34,-60) rot=(0,0,1;0rad)
  Radius = 1.5
FEATURE [Part::Cylinder] Cylinder2302  label="Válec2302"
  Angle = 360
  AttacherType = Attacher::AttachEngine3D
  Height = 20
  Placement = pos=(103,-12,-20) rot=(0,0,1;0rad)
  Radius = 4
FEATURE [Part::Cylinder] Cylinder2303  label="Válec2303"
  Angle = 360
  AttacherType = Attacher::AttachEngine3D
  Height = 40
  Placement = pos=(13,-27,-18) rot=(0,0,1;0rad)
  Radius = 4
FEATURE [Part::Cylinder] Cylinder2304  label="Válec2304"
  Angle = 360
  AttacherType = Attacher::AttachEngine3D
  Height = 20
  Placement = pos=(91,-27,-18) rot=(0,0,1;0rad)
  Radius = 4
FEATURE [Part::Cylinder] Cylinder2305  label="Válec2305"
  Angle = 360
  AttacherType = Attacher::AttachEngine3D
  Height = 160
  Placement = pos=(-18,0,-60) rot=(0,0,1;0rad)
  Radius = 17
FEATURE [Part::Cylinder] Cylinder2306  label="Válec2306"
  Angle = 360
  AttacherType = Attacher::AttachEngine3D
  Height = 40
  Placement = pos=(28,24,-18) rot=(0,0,1;0rad)
  Radius = 4
FEATURE [Part::Cylinder] Cylinder2307  label="Válec2307"
  Angle = 360
  AttacherType = Attacher::AttachEngine3D
  Height = 100
  Placement = pos=(10,-36,-90) rot=(0,0,1;0rad)
  Radius = 4
FEATURE [Part::Cylinder] Cylinder2308  label="Válec2308"
  Angle = 360
  AttacherType = Attacher::AttachEngine3D
  Height = 100
  Placement = pos=(13,-27,-60) rot=(0,0,1;0rad)
  Radius = 1.5
FEATURE [Part::Cylinder] Cylinder2309  label="Válec2309"
  Angle = 360
  AttacherType = Attacher::AttachEngine3D
  Height = 100
  Placement = pos=(90,0,-18) rot=(0,0,1;0rad)
  Radius = 4
FEATURE [Part::Cylinder] Cylinder2310  label="Válec2310"
  Angle = 360
  AttacherType = Attacher::AttachEngine3D
  Height = 100
  Placement = pos=(34,-16,-60) rot=(0,0,1;0rad)
  Radius = 1.5
FEATURE [Part::Cylinder] Cylinder2311  label="Válec2311"
  Angle = 360
  AttacherType = Attacher::AttachEngine3D
  Height = 100
  Placement = pos=(103,-12,-60) rot=(0,0,1;0rad)
  Radius = 1.5
FEATURE [Part::Cylinder] Cylinder2312  label="Válec2312"
  Angle = 360
  AttacherType = Attacher::AttachEngine3D
  Height = 32
  Placement = pos=(78,41,-42) rot=(0,0,1;0rad)
  Radius = 1.5
FEATURE [Part::Cylinder] Cylinder2313  label="Válec2313"
  Angle = 360
  AttacherType = Attacher::AttachEngine3D
  Height = 100
  Placement = pos=(90,0,-60) rot=(0,0,1;0rad)
  Radius = 1.5
FEATURE [Part::Cylinder] Cylinder2314  label="Válec2314"
  Angle = 360
  AttacherType = Attacher::AttachEngine3D
  Height = 100
  Placement = pos=(34,16,-60) rot=(0,0,1;0rad)
  Radius = 1.5
FEATURE [Part::Cylinder] Cylinder2315  label="Válec2315"
  Angle = 360
  AttacherType = Attacher::AttachEngine3D
  Height = 100
  Placement = pos=(28,24,-60) rot=(0,0,1;0rad)
  Radius = 1.5
FEATURE [Part::Cylinder] Cylinder2316  label="Válec2316"
  Angle = 360
  AttacherType = Attacher::AttachEngine3D
  Height = 100
  Placement = pos=(10,-36,-60) rot=(0,0,1;0rad)
  Radius = 1.5
FEATURE [Part::Cylinder] Cylinder2317  label="Válec2317"
  Angle = 360
  AttacherType = Attacher::AttachEngine3D
  Height = 100
  Placement = pos=(-34,16,-60) rot=(0,0,1;0rad)
  Radius = 1.5
FEATURE [Part::Cylinder] Cylinder2318  label="Válec2318"
  Angle = 360
  AttacherType = Attacher::AttachEngine3D
  Height = 100
  Placement = pos=(91,-27,-60) rot=(0,0,1;0rad)
  Radius = 1.5
FEATURE [Part::Cylinder] Cylinder2319  label="Válec2319"
  Angle = 360
  AttacherType = Attacher::AttachEngine3D
  Height = 100
  Placement = pos=(-16,-34,-60) rot=(0,0,1;0rad)
  Radius = 1.5
FEATURE [Part::Cylinder] Cylinder2320  label="Válec2320"
  Angle = 360
  AttacherType = Attacher::AttachEngine3D
  Height = 100
  Placement = pos=(1,12,-60) rot=(0,0,1;0rad)
  Radius = 1.5
FEATURE [Part::Cylinder] Cylinder2321  label="Válec2321"
  Angle = 360
  AttacherType = Attacher::AttachEngine3D
  Height = 100
  Placement = pos=(76,24,-60) rot=(0,0,1;0rad)
  Radius = 1.5
FEATURE [Part::Cylinder] Cylinder2322  label="Válec2322"
  Angle = 360
  AttacherType = Attacher::AttachEngine3D
  Height = 100
  Placement = pos=(-16,-34,-60) rot=(0,0,1;0rad)
  Radius = 1.5
FEATURE [Part::Cylinder] Cylinder2323  label="Válec2323"
  Angle = 360
  AttacherType = Attacher::AttachEngine3D
  Height = 100
  Placement = pos=(34,-16,-90) rot=(0,0,1;0rad)
  Radius = 4
FEATURE [Part::Cylinder] Cylinder2324  label="Válec2324"
  Angle = 360
  AttacherType = Attacher::AttachEngine3D
  Height = 100
  Placement = pos=(34,16,-90) rot=(0,0,1;0rad)
  Radius = 4
FEATURE [Part::Cylinder] Cylinder2325  label="Válec2325"
  Angle = 360
  AttacherType = Attacher::AttachEngine3D
  Height = 100
  Placement = pos=(103,12,-60) rot=(0,0,1;0rad)
  Radius = 1.5
FEATURE [Part::Cylinder] Cylinder2326  label="Válec2326"
  Angle = 360
  AttacherType = Attacher::AttachEngine3D
  Height = 100
  Placement = pos=(1,-12,-60) rot=(0,0,1;0rad)
  Radius = 1.5
FEATURE [Part::Cylinder] Cylinder2327  label="Válec2327"
  Angle = 360
  AttacherType = Attacher::AttachEngine3D
  Height = 32
  Placement = pos=(26,41,-46) rot=(0,0,1;0rad)
  Radius = 1.5
FEATURE [Part::Cylinder] Cylinder2328  label="Válec2328"
  Angle = 360
  AttacherType = Attacher::AttachEngine3D
  Height = 100
  Placement = pos=(34,-16,-60) rot=(0,0,1;0rad)
  Radius = 1.5
FEATURE [Part::Cylinder] Cylinder2329  label="Válec2329"
  Angle = 360
  AttacherType = Attacher::AttachEngine3D
  Height = 100
  Placement = pos=(-34,16,-60) rot=(0,0,1;0rad)
  Radius = 1.5
FEATURE [Part::Cylinder] Cylinder2330  label="Válec2330"
  Angle = 360
  AttacherType = Attacher::AttachEngine3D
  Height = 100
  Placement = pos=(90,0,-60) rot=(0,0,1;0rad)
  Radius = 1.5
FEATURE [Part::Cylinder] Cylinder2331  label="Válec2331"
  Angle = 360
  AttacherType = Attacher::AttachEngine3D
  Height = 100
  Placement = pos=(-34,16,-90) rot=(0,0,1;0rad)
  Radius = 4
FEATURE [Part::Cylinder] Cylinder2332  label="Válec2332"
  Angle = 360
  AttacherType = Attacher::AttachEngine3D
  Height = 100
  Placement = pos=(34,16,-60) rot=(0,0,1;0rad)
  Radius = 1.5
FEATURE [Part::Cylinder] Cylinder2333  label="Válec2333"
  Angle = 360
  AttacherType = Attacher::AttachEngine3D
  Height = 100
  Placement = pos=(16,34,-60) rot=(0,0,1;0rad)
  Radius = 1.5
FEATURE [Part::Cylinder] Cylinder2334  label="Válec2334"
  Angle = 360
  AttacherType = Attacher::AttachEngine3D
  Height = 100
  Placement = pos=(14,0,-18) rot=(0,0,1;0rad)
  Radius = 4
FEATURE [Part::Cylinder] Cylinder2335  label="Válec2335"
  Angle = 360
  AttacherType = Attacher::AttachEngine3D
  Height = 100
  Placement = pos=(14,0,-60) rot=(0,0,1;0rad)
  Radius = 1.5
FEATURE [Sketcher::SketchObject] Sketch021
  FullyConstrained = false
  sketch-geometry (1):
    g0: Circle CenterX=-186.411 CenterY=73.9277 CenterZ=0 NormalX=0 NormalY=0 NormalZ=1 AngleXU=0 Radius=59
FEATURE [Part::Extrusion] Extrude020
  Base = -> Sketch021
  Dir = (52,0,32)
  DirMode = 0
  FaceMakerClass = Part::FaceMakerBullseye
  LengthFwd = 61
  LengthRev = 0
  Placement = pos=(-134.5,74,-22) rot=(0,0,1;3.14159rad)
  Solid = true
  Symmetric = false
FEATURE [Sketcher::SketchObject] Sketch022
  FullyConstrained = false
  sketch-geometry (1):
    g0: Circle CenterX=-186.411 CenterY=73.9277 CenterZ=0 NormalX=0 NormalY=0 NormalZ=1 AngleXU=0 Radius=59
FEATURE [Part::Extrusion] Extrude019
  Base = -> Sketch022
  Dir = (52,0,32)
  DirMode = 0
  FaceMakerClass = Part::FaceMakerBullseye
  LengthFwd = 61
  LengthRev = 0
  Placement = pos=(-134.5,74,-22) rot=(0,0,1;3.14159rad)
  Solid = true
  Symmetric = false
FEATURE [Part::Compound] Compound1034  label="srouby_monoblok_silne024"
  Links = -> [Cylinder2302,Cylinder2253,Cylinder2284,Cylinder2272,Cylinder2281,Cylinder2285,Cylinder2257,Cylinder2279]
FEATURE [Part::Compound] Compound1035  label="sbouby_baze_silne032"
  Links = -> [Cylinder2299,Cylinder2248,Cylinder2234,Cylinder2323,Cylinder2291,Cylinder2307,Cylinder2249,Cylinder2297]
FEATURE [Part::Compound] Compound1036  label="srouby_monoblok_silne025"
  Links = -> [Cylinder2227,Cylinder2228,Cylinder2229,Cylinder2233,Cylinder2247,Cylinder2231,Cylinder2245,Cylinder2246]
FEATURE [Part::Compound] Compound1037  label="srouby_monoblok_silne026"
  Links = -> [Cylinder2296,Cylinder2283,Cylinder2271,Cylinder2304,Cylinder2303,Cylinder2306,Cylinder2288,Cylinder2287]
FEATURE [Part::Compound] Compound1038  label="sbouby_baze023"
  Links = -> [Cylinder2317,Cylinder2300,Cylinder2310,Cylinder2314,Cylinder2333,Cylinder2316,Cylinder2319,Cylinder2301]
FEATURE [Part::Compound] Compound1039  label="srouby_troj_silne021"
  Links = -> [Cylinder2241,Cylinder2240]
FEATURE [Part::Compound] Compound1040  label="sbouby_baze_silne033"
  Links = -> [Cylinder2282,Cylinder2292,Cylinder2280,Cylinder2276,Cylinder2244,Cylinder2235,Cylinder2290,Cylinder2251]
FEATURE [Part::Compound] Compound1041  label="sbouby_baze024"
  Links = -> [Cylinder2269,Cylinder2262,Cylinder2259,Cylinder2261,Cylinder2243,Cylinder2230,Cylinder2258,Cylinder2264]
FEATURE [Part::Compound] Compound1042  label="srouby_troj018"
  Links = -> [Cylinder2330,Cylinder2335]
FEATURE [Part::Compound] Compound1043  label="sbouby_baze_silne034"
  Links = -> [Cylinder2275,Cylinder2273,Cylinder2277,Cylinder2268,Cylinder2270,Cylinder2260,Cylinder2239,Cylinder2250]
FEATURE [Part::Compound] Compound1044  label="srouby_monoblok020"
  Links = -> [Cylinder2265,Cylinder2266,Cylinder2267,Cylinder2242,Cylinder2256,Cylinder2274,Cylinder2263,Cylinder2278]
FEATURE [Part::Compound] Compound1045
  Links = -> [Cylinder2236,Cylinder2312]
FEATURE [Part::Compound] Compound1046  label="srouby_troj_silne022"
  Links = -> [Cylinder2309,Cylinder2289]
FEATURE [Part::Compound] Compound1047  label="srouby_monoblok021"
  Links = -> [Cylinder2311,Cylinder2325,Cylinder2321,Cylinder2318,Cylinder2308,Cylinder2315,Cylinder2326,Cylinder2320]
FEATURE [Part::Compound] Compound1048
  Links = -> [Cylinder2327,Cylinder2226]
FEATURE [Part::Compound] Compound1051  label="srouby_troj019"
  Links = -> [Cylinder2313,Cylinder2254]
FEATURE [Part::Cut] Cut715
  Base = -> Cylinder2294
  Tool = -> Compound1044
FEATURE [Part::Cut] Cut723
  Base = -> Extrude019
  Tool = -> Compound1047
FEATURE [Part::Cut] Cut730
  Base = -> Cylinder2286
  Tool = -> Compound1037
FEATURE [Part::Cut] Cut725
  Base = -> Cut730
  Tool = -> Compound1040
FEATURE [Part::Cut] Cut720
  Base = -> Cut725
  Tool = -> Compound1041
FEATURE [Part::Chamfer] Chamfer080
  Base = -> Cut720
  Edges = 1 edges r=4: [Edge3]
FEATURE [Part::Cut] Cut722
  Base = -> Chamfer080
  Placement = pos=(0,0,4) rot=(0,0,1;0rad)
  Tool = -> Compound1046
FEATURE [Part::Cut] Cut726
  Base = -> Cut722
  Tool = -> Cylinder2252
FEATURE [Part::Fillet] Fillet038
  Base = -> Cut726
  Edges = 1 edges r=4: [Edge10]
FEATURE [Part::Cut] Cut731
  Base = -> Cylinder2232
  Tool = -> Compound1036
FEATURE [Part::Cut] Cut734
  Base = -> Cut715
  Tool = -> Compound1043
FEATURE [Part::Cut] Cut735
  Base = -> Cut723
  Tool = -> Compound1034
FEATURE [Part::Common] Common009
  Base = -> Fillet038
  Tool = -> Extrude020
FEATURE [Part::Cut] Cut738
  Base = -> Cut731
  Tool = -> Compound1035
FEATURE [Part::Cut] Cut736
  Base = -> Cut738
  Tool = -> Compound1038
FEATURE [Part::Chamfer] Chamfer077
  Base = -> Cut736
  Edges = 1 edges r=4: [Edge3]
FEATURE [Part::Cut] Cut740
  Base = -> Cut734
  Tool = -> Box574
FEATURE [Part::Cut] Cut737
  Base = -> Cut740
  Tool = -> Box573
FEATURE [Part::Cut] Cut739
  Base = -> Cut737
  Tool = -> Compound1045
FEATURE [Part::Cut] Cut729
  Base = -> Cut739
  Tool = -> Compound1051
FEATURE [Part::Cut] Cut714
  Base = -> Cut729
  Tool = -> Cylinder2305
FEATURE [Part::Fillet] Fillet039
  Base = -> Cut714
  Edges = 1 edges r=8: [Edge55]
FEATURE [Part::Fillet] Fillet037
  Base = -> Fillet039
  Edges = 1 edges r=8: [Edge38]
FEATURE [Part::Cut] Cut741
  Base = -> Chamfer077
  Placement = pos=(0,0,4) rot=(0,0,1;0rad)
  Tool = -> Compound1039
FEATURE [Part::Cut] Cut733
  Base = -> Cut741
  Tool = -> Cylinder2298
FEATURE [Part::Fillet] Fillet036
  Base = -> Cut733
  Edges = 1 edges r=4: [Edge10]
FEATURE [Part::Common] Common008
  Base = -> Fillet036
  Tool = -> Cylinder2238
FEATURE [Part::Box] Box575  label="Krychle575"
  AttacherType = Attacher::AttachEngine3D
  Height = 2
  Length = 6
  Placement = pos=(23,38,-22) rot=(0,0,1;0rad)
  Width = 6
FEATURE [Part::Box] Box576  label="Krychle576"
  AttacherType = Attacher::AttachEngine3D
  Height = 100
  Length = 200
  Placement = pos=(-60,44,-90) rot=(0,0,1;0rad)
  Width = 100
FEATURE [Part::Cylinder] Cylinder2336  label="Válec2336"
  Angle = 360
  AttacherType = Attacher::AttachEngine3D
  Height = 100
  Placement = pos=(16,34,-60) rot=(0,0,1;0rad)
  Radius = 1.5
FEATURE [Part::Cylinder] Cylinder2337  label="Válec2337"
  Angle = 360
  AttacherType = Attacher::AttachEngine3D
  Height = 100
  Placement = pos=(10,-36,-60) rot=(0,0,1;0rad)
  Radius = 1.5
FEATURE [Part::Cylinder] Cylinder2338  label="Válec2338"
  Angle = 360
  AttacherType = Attacher::AttachEngine3D
  Height = 100
  Placement = pos=(90,0,-18) rot=(0,0,1;0rad)
  Radius = 4
FEATURE [Part::Compound] Compound1052  label="srouby_troj_silne023"
  Links = -> [Cylinder2338,Cylinder2334]
FEATURE [Part::Cylinder] Cylinder2339  label="Válec2339"
  Angle = 360
  AttacherType = Attacher::AttachEngine3D
  Height = 100
  Placement = pos=(34,-16,-90) rot=(0,0,1;0rad)
  Radius = 4
FEATURE [Part::Cylinder] Cylinder2340  label="Válec2340"
  Angle = 360
  AttacherType = Attacher::AttachEngine3D
  Height = 100
  Placement = pos=(10,-36,-90) rot=(0,0,1;0rad)
  Radius = 4
FEATURE [Part::Box] Box577  label="Krychle577"
  AttacherType = Attacher::AttachEngine3D
  Height = 100
  Length = 200
  Placement = pos=(-60,-134,-90) rot=(0,0,1;0rad)
  Width = 100
FEATURE [Part::Box] Box578  label="Krychle578"
  AttacherType = Attacher::AttachEngine3D
  Height = 2
  Length = 6
  Placement = pos=(75,38,-22) rot=(0,0,1;0rad)
  Width = 6
FEATURE [Part::Compound] Compound1049
  Links = -> [Box578,Box575]
FEATURE [Part::Cylinder] Cylinder2341  label="Válec2341"
  Angle = 360
  AttacherType = Attacher::AttachEngine3D
  Height = 100
  Placement = pos=(-34,-16,-60) rot=(0,0,1;0rad)
  Radius = 1.5
FEATURE [Part::Cylinder] Cylinder2342  label="Válec2342"
  Angle = 360
  AttacherType = Attacher::AttachEngine3D
  Height = 100
  Placement = pos=(-16,-34,-90) rot=(0,0,1;0rad)
  Radius = 4
FEATURE [Part::Compound] Compound1050  label="sbouby_baze_silne035"
  Links = -> [Cylinder2255,Cylinder2295,Cylinder2342,Cylinder2339,Cylinder2293,Cylinder2340,Cylinder2331,Cylinder2324]
FEATURE [Part::Cut] Cut717
  Base = -> Cut735
  Tool = -> Compound1050
FEATURE [Part::Cylinder] Cylinder2343  label="Válec2343"
  Angle = 360
  AttacherType = Attacher::AttachEngine3D
  Height = 100
  Placement = pos=(-16,34,-60) rot=(0,0,1;0rad)
  Radius = 1.5
FEATURE [Part::Compound] Compound1053  label="sbouby_baze025"
  Links = -> [Cylinder2329,Cylinder2341,Cylinder2328,Cylinder2332,Cylinder2336,Cylinder2337,Cylinder2322,Cylinder2343]
FEATURE [Part::Cut] Cut724
  Base = -> Cut717
  Tool = -> Compound1053
FEATURE [Part::Cut] Cut728
  Base = -> Cut724
  Tool = -> Box577
FEATURE [Part::Cut] Cut727
  Base = -> Cut728
  Tool = -> Box576
FEATURE [Part::Cut] Cut719
  Base = -> Cut727
  Tool = -> Compound1049
FEATURE [Part::Cut] Cut718
  Base = -> Cut719
  Tool = -> Compound1048
FEATURE [Part::Cut] Cut716
  Base = -> Cut718
  Tool = -> Compound1042
FEATURE [Part::Cut] Cut732
  Base = -> Cut716
  Tool = -> Compound1052
FEATURE [Part::Chamfer] Chamfer081
  Base = -> Cut732
  Edges = 1 edges r=4: [Edge44]
FEATURE [Part::Chamfer] Chamfer078
  Base = -> Chamfer081
  Edges = 1 edges r=3: [Edge6]
FEATURE [Part::Chamfer] Chamfer079
  Base = -> Chamfer078
  Edges = 1 edges r=3: [Edge7]
FEATURE [Part::Cut] Cut721
  Base = -> Chamfer079
  Tool = -> Cylinder2237
FEATURE [Part::Fillet] Fillet040
  Base = -> Cut721
  Edges = 2 edges r=3: [Edge4,Edge36]
FEATURE [Part::Box] Box579  label="Krychle579"
  AttacherType = Attacher::AttachEngine3D
  Height = 100
  Length = 40
  Placement = pos=(-50,-48,-22) rot=(0,0,1;0rad)
  Width = 100
FEATURE [Part::Torus] Torus005  label="Anuloid005"
  Angle1 = -180
  Angle2 = 180
  Angle3 = 360
  AttacherType = Attacher::AttachEngine3D
  Placement = pos=(12,-33,-4) rot=(0,0,1;0rad)
  Radius1 = 40
  Radius2 = 4
FEATURE [Part::Cut] Cut742
  Base = -> Torus005
  Placement = pos=(0,0,-2) rot=(0,0,1;0rad)
  Tool = -> Box579
FEATURE [Part::Cut] Cut743
  Base = -> Fillet040
  Tool = -> Cut742
FEATURE [Part::Fillet] Fillet035
  Base = -> Cut743
  Edges = 1 edges r=3: [Edge106]
FEATURE [Part::Fillet] Fillet041
  Base = -> Fillet035
  Edges = 1 edges r=3: [Edge53]
FEATURE [Part::Compound] Compound1054
  Links = -> [Fillet037,Common008,Common009,Fillet041]
FEATURE [Part::Mirroring] mirror001  label="Base_deep-neck-holed_v3"
  Base = (0,0,0)
  Normal = (1e-16,-1,0)
  Source = -> Compound1054
